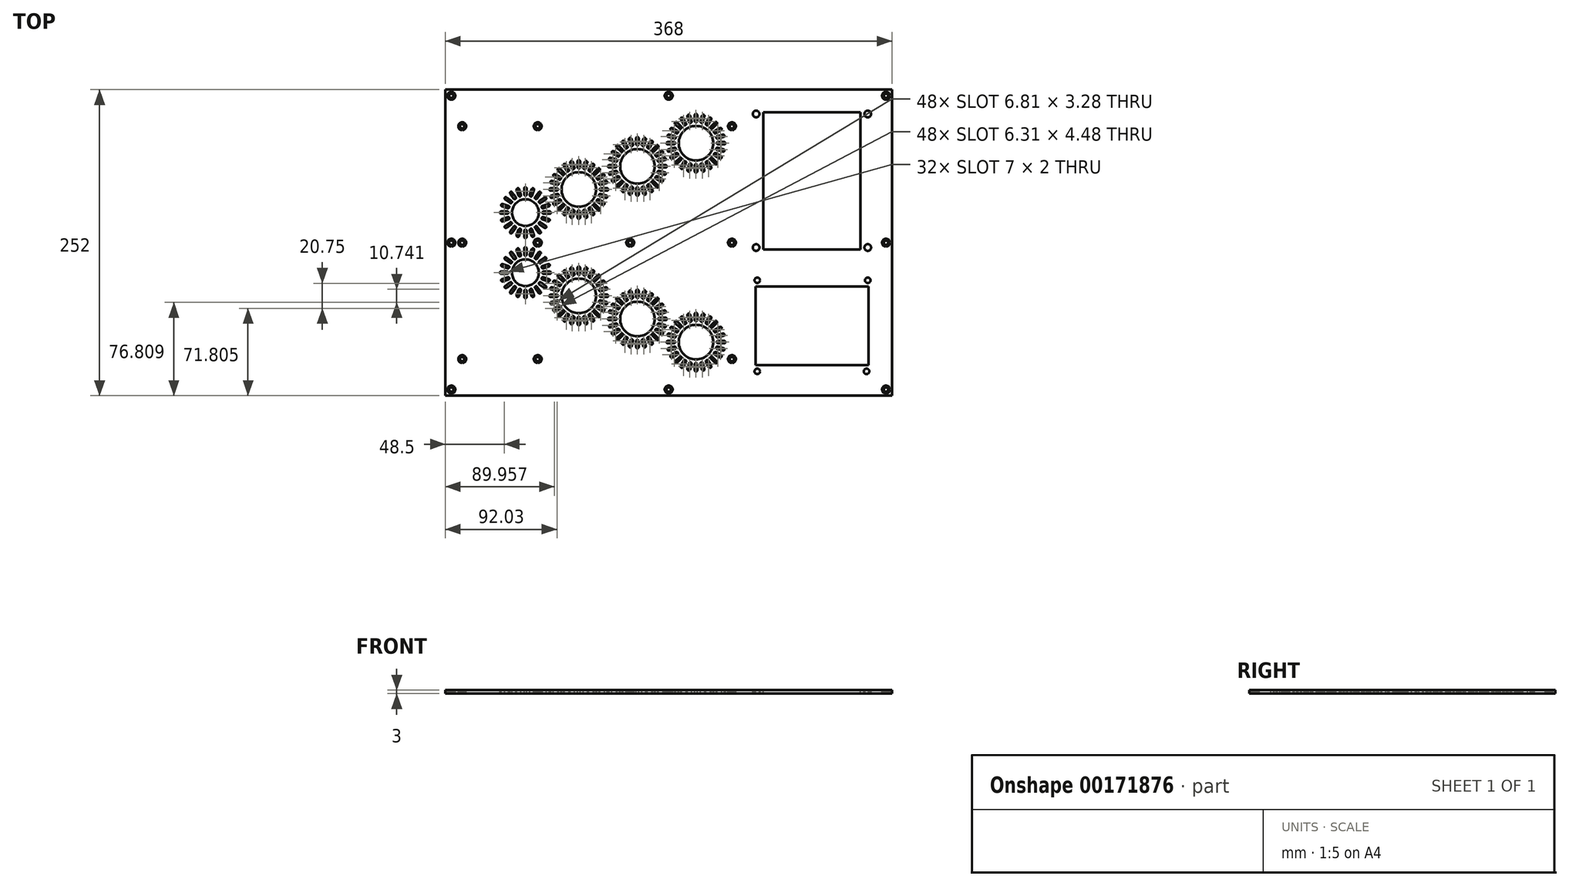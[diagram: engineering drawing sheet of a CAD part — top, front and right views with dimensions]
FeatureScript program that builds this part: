
annotation { "Feature Type Name" : "Feature", "Feature Type Description" : "" }
export const myFeature = defineFeature(function(context is Context, id is Id, definition is map)
    precondition{}
    {
        {
            var Q0;
            Q0=qCreatedBy(makeId("Top.planeOp"),FACE);
            var sketch = newSketch(context, id + "F0", { "sketchPlane" : qUnion([Q0])});
            skLineSegment(sketch, "E0.bottom", {"start": v(184, -126) * mm, "end": v(-184, -126) * mm});
            skLineSegment(sketch, "E0.top", {"start": v(184, 126) * mm, "end": v(-184, 126) * mm});
            skLineSegment(sketch, "E0.left", {"start": v(184, -126) * mm, "end": v(184, 126) * mm});
            skLineSegment(sketch, "E0.right", {"start": v(-184, -126) * mm, "end": v(-184, 126) * mm});
            skPoint(sketch, "E0.middle", {"position": v(0, 0) * mm});
            skLineSegment(sketch, "E1", {"start": v(-118, 153.33) * mm, "end": v(-118, -167.83) * mm, "construction": true});
            skLineSegment(sketch, "E2", {"start": v(-74, 180.26) * mm, "end": v(-74, -51.12) * mm, "construction": true});
            skLineSegment(sketch, "E3", {"start": v(-25.74, 83.61) * mm, "end": v(-25.74, -167.83) * mm, "construction": true});
            skLineSegment(sketch, "E4", {"start": v(-203.28, 62.86) * mm, "end": v(180.7, 62.86) * mm, "construction": true});
            skLineSegment(sketch, "E5", {"start": v(-202.8, 43.82) * mm, "end": v(185.48, 43.82) * mm, "construction": true});
            skLineSegment(sketch, "E6", {"start": v(-209.03, 24.75) * mm, "end": v(184.53, 24.75) * mm, "construction": true});
            skLineSegment(sketch, "E7.MirrorCS", {"start": v(-209.03, -24.75) * mm, "end": v(184.53, -24.75) * mm, "construction": true});
            skLineSegment(sketch, "E8.MirrorCS", {"start": v(-202.8, -43.82) * mm, "end": v(185.48, -43.82) * mm, "construction": true});
            skLineSegment(sketch, "E9.MirrorCS", {"start": v(-203.28, -62.86) * mm, "end": v(180.7, -62.86) * mm, "construction": true});
            skCircle(sketch, "E10", {"center": v(-118, 24.75) * mm, "radius": 11 * mm});
            skCircle(sketch, "E11", {"center": v(-74, 43.82) * mm, "radius": 14.25 * mm});
            skCircle(sketch, "E12", {"center": v(-118, -24.75) * mm, "radius": 11 * mm});
            skCircle(sketch, "E13", {"center": v(-74, -43.82) * mm, "radius": 14.25 * mm});
            skCircle(sketch, "E14", {"center": v(-25.74, -62.86) * mm, "radius": 14.25 * mm});
            skCircle(sketch, "E15", {"center": v(-25.74, 62.86) * mm, "radius": 14.25 * mm});
            skLineSegment(sketch, "E16.bottom", {"start": v(158, -5.5) * mm, "end": v(78, -5.5) * mm});
            skLineSegment(sketch, "E16.top", {"start": v(158, 107.5) * mm, "end": v(78, 107.5) * mm});
            skLineSegment(sketch, "E16.left", {"start": v(158, -5.5) * mm, "end": v(158, 107.5) * mm});
            skLineSegment(sketch, "E16.right", {"start": v(78, -5.5) * mm, "end": v(78, 107.5) * mm});
            skLineSegment(sketch, "E17", {"start": v(72, 135.4) * mm, "end": v(72, -139.42) * mm, "construction": true});
            skLineSegment(sketch, "E18", {"start": v(164, 132.45) * mm, "end": v(164, -295.29) * mm, "construction": true});
            skLineSegment(sketch, "E19", {"start": v(51.45, 106) * mm, "end": v(256.55, 106) * mm, "construction": true});
            skCircle(sketch, "E20", {"center": v(72, 106) * mm, "radius": 2.75 * mm});
            skCircle(sketch, "E21", {"center": v(164, 106) * mm, "radius": 2.75 * mm});
            skCircle(sketch, "E22", {"center": v(72, -4) * mm, "radius": 2.75 * mm});
            skCircle(sketch, "E23", {"center": v(164, -4) * mm, "radius": 2.75 * mm});
            skLineSegment(sketch, "E24", {"start": v(-146.66, 121) * mm, "end": v(202.1, 121) * mm, "construction": true});
            skLineSegment(sketch, "E25", {"start": v(-179, -133.01) * mm, "end": v(-179, 126) * mm, "construction": true});
            skLineSegment(sketch, "E26.MirrorCS", {"start": v(179, -133.01) * mm, "end": v(179, 126) * mm, "construction": true});
            skLineSegment(sketch, "E27.MirrorCS", {"start": v(-146.66, -121) * mm, "end": v(202.1, -121) * mm, "construction": true});
            skLineSegment(sketch, "E28", {"start": v(0, 148.7) * mm, "end": v(0, -121) * mm, "construction": true});
            skPoint(sketch, "E28.startSnap0", {"position": v(0, 126) * mm});
            skPoint(sketch, "E28.endSnap0", {"position": v(27.72, -121) * mm});
            skLineSegment(sketch, "E29", {"start": v(-194.49, 0) * mm, "end": v(194.49, 0) * mm, "construction": true});
            skPoint(sketch, "E29.startSnap0", {"position": v(-184, 0) * mm});
            skPoint(sketch, "E30", {"position": v(-179, 121) * mm});
            skPoint(sketch, "E31", {"position": v(0, 121) * mm});
            skPoint(sketch, "E32", {"position": v(-179, 0) * mm});
            skPoint(sketch, "E33", {"position": v(179, 121) * mm});
            skPoint(sketch, "E34", {"position": v(179, 0) * mm});
            skPoint(sketch, "E35", {"position": v(179, -121) * mm});
            skPoint(sketch, "E36", {"position": v(0, -121) * mm});
            skPoint(sketch, "E37", {"position": v(-179, -121) * mm});
            skLineSegment(sketch, "E38.bottom", {"start": v(169, -9) * mm, "end": v(67, -9) * mm, "construction": true});
            skLineSegment(sketch, "E38.top", {"start": v(169, 111) * mm, "end": v(67, 111) * mm, "construction": true});
            skLineSegment(sketch, "E38.left", {"start": v(169, -9) * mm, "end": v(169, 111) * mm, "construction": true});
            skLineSegment(sketch, "E38.right", {"start": v(67, -9) * mm, "end": v(67, 111) * mm, "construction": true});
            skPoint(sketch, "E38.middle", {"position": v(118, 51) * mm});
            skLineSegment(sketch, "E39", {"start": v(48.88, -4) * mm, "end": v(192, -4) * mm, "construction": true});
            skLineSegment(sketch, "E40.bottom", {"start": v(164.5, -101) * mm, "end": v(71.5, -101) * mm});
            skLineSegment(sketch, "E40.top", {"start": v(164.5, -36) * mm, "end": v(71.5, -36) * mm});
            skLineSegment(sketch, "E40.left", {"start": v(164.5, -101) * mm, "end": v(164.5, -36) * mm});
            skLineSegment(sketch, "E40.right", {"start": v(71.5, -101) * mm, "end": v(71.5, -36) * mm});
            skLineSegment(sketch, "E41", {"start": v(65.3, -31) * mm, "end": v(270.4, -31) * mm, "construction": true});
            skCircle(sketch, "E42", {"center": v(73, -31) * mm, "radius": 2.25 * mm});
            skCircle(sketch, "E43", {"center": v(164, -31) * mm, "radius": 2.25 * mm});
            skCircle(sketch, "E44", {"center": v(73, -106) * mm, "radius": 2.25 * mm});
            skCircle(sketch, "E45", {"center": v(163, -106) * mm, "radius": 2.25 * mm});
            skLineSegment(sketch, "E46.bottom", {"start": v(168, -111) * mm, "end": v(68, -111) * mm, "construction": true});
            skLineSegment(sketch, "E46.top", {"start": v(168, -26) * mm, "end": v(68, -26) * mm, "construction": true});
            skLineSegment(sketch, "E46.left", {"start": v(168, -111) * mm, "end": v(168, -26) * mm, "construction": true});
            skLineSegment(sketch, "E46.right", {"start": v(68, -111) * mm, "end": v(68, -26) * mm, "construction": true});
            skPoint(sketch, "E46.middle", {"position": v(118, -68.5) * mm});
            skLineSegment(sketch, "E47", {"start": v(62.73, -106) * mm, "end": v(205.85, -106) * mm, "construction": true});
            skLineSegment(sketch, "E48", {"start": v(118, 51) * mm, "end": v(118, -168.55) * mm, "construction": true});
            skLineSegment(sketch, "E49", {"start": v(73, -94.18) * mm, "end": v(73, -202) * mm, "construction": true});
            skLineSegment(sketch, "E50", {"start": v(163, -92.42) * mm, "end": v(163, -205.46) * mm, "construction": true});
            skLineSegment(sketch, "E51", {"start": v(22.52, 102.67) * mm, "end": v(22.52, -225.01) * mm, "construction": true});
            skLineSegment(sketch, "E52", {"start": v(-198.69, 81.92) * mm, "end": v(203.66, 81.92) * mm, "construction": true});
            skLineSegment(sketch, "E53.MirrorCS", {"start": v(-198.69, -81.92) * mm, "end": v(203.66, -81.92) * mm, "construction": true});
            skCircle(sketch, "E54", {"center": v(22.52, 81.92) * mm, "radius": 14.25 * mm});
            skCircle(sketch, "E55.MirrorC", {"center": v(22.52, -81.92) * mm, "radius": 14.25 * mm});
            skLineSegment(sketch, "E56.bottom", {"start": v(-118, 38.75) * mm, "end": v(-118, 38.75) * mm});
            skLineSegment(sketch, "E56.top", {"start": v(-118, 45.75) * mm, "end": v(-118, 45.75) * mm});
            skLineSegment(sketch, "E56.left", {"start": v(-117, 39.75) * mm, "end": v(-117, 44.75) * mm});
            skLineSegment(sketch, "E56.right", {"start": v(-119, 39.75) * mm, "end": v(-119, 44.75) * mm});
            skPoint(sketch, "E56.middle", {"position": v(-118, 42.25) * mm});
            skPoint(sketch, "E57.visualSharp", {"position": v(-117, 45.75) * mm});
            skArc(sketch, "E57.filletArc", {"start": v(-117, 44.75) * mm, "mid": v(-117.3, 45.46) * mm, "end": v(-118, 45.75) * mm});
            skPoint(sketch, "E58.visualSharp", {"position": v(-119, 45.75) * mm});
            skArc(sketch, "E58.filletArc", {"start": v(-118, 45.75) * mm, "mid": v(-118.7, 45.46) * mm, "end": v(-119, 44.75) * mm});
            skPoint(sketch, "E59.visualSharp", {"position": v(-119, 38.75) * mm});
            skArc(sketch, "E59.filletArc", {"start": v(-119, 39.75) * mm, "mid": v(-118.7, 39.04) * mm, "end": v(-118, 38.75) * mm});
            skPoint(sketch, "E60.visualSharp", {"position": v(-117, 38.75) * mm});
            skArc(sketch, "E60.filletArc", {"start": v(-118, 38.75) * mm, "mid": v(-117.3, 39.04) * mm, "end": v(-117, 39.75) * mm});
            skPoint(sketch, "E61.1.0", {"position": v(-123.54, 45.03) * mm});
            skPoint(sketch, "E61.1.1", {"position": v(-125.44, 44.41) * mm});
            skPoint(sketch, "E61.1.2", {"position": v(-121.38, 38.37) * mm});
            skLineSegment(sketch, "E61.1.3", {"start": v(-121.68, 39.32) * mm, "end": v(-123.23, 44.08) * mm});
            skPoint(sketch, "E61.1.4", {"position": v(-123.28, 37.76) * mm});
            skLineSegment(sketch, "E61.1.5", {"start": v(-123.59, 38.7) * mm, "end": v(-125.13, 43.46) * mm});
            skPoint(sketch, "E61.1.6", {"position": v(-123.4, 41.4) * mm});
            skArc(sketch, "E61.1.7", {"start": v(-124.49, 44.72) * mm, "mid": v(-125.07, 44.23) * mm, "end": v(-125.13, 43.46) * mm});
            skArc(sketch, "E61.1.8", {"start": v(-122.33, 38.06) * mm, "mid": v(-121.74, 38.56) * mm, "end": v(-121.68, 39.32) * mm});
            skArc(sketch, "E61.1.9", {"start": v(-123.59, 38.7) * mm, "mid": v(-123.09, 38.12) * mm, "end": v(-122.33, 38.06) * mm});
            skArc(sketch, "E61.1.10", {"start": v(-123.23, 44.08) * mm, "mid": v(-123.73, 44.66) * mm, "end": v(-124.49, 44.72) * mm});
            skPoint(sketch, "E61.2.0", {"position": v(-129.53, 42.33) * mm});
            skPoint(sketch, "E61.2.1", {"position": v(-131.15, 41.15) * mm});
            skPoint(sketch, "E61.2.2", {"position": v(-125.42, 36.66) * mm});
            skLineSegment(sketch, "E61.2.3", {"start": v(-126, 37.47) * mm, "end": v(-128.95, 41.52) * mm});
            skPoint(sketch, "E61.2.4", {"position": v(-127.04, 35.49) * mm});
            skLineSegment(sketch, "E61.2.5", {"start": v(-127.63, 36.3) * mm, "end": v(-130.56, 40.34) * mm});
            skPoint(sketch, "E61.2.6", {"position": v(-128.29, 38.9) * mm});
            skArc(sketch, "E61.2.7", {"start": v(-130.34, 41.74) * mm, "mid": v(-130.74, 41.09) * mm, "end": v(-130.56, 40.34) * mm});
            skArc(sketch, "E61.2.8", {"start": v(-126.23, 36.08) * mm, "mid": v(-125.83, 36.73) * mm, "end": v(-126, 37.47) * mm});
            skArc(sketch, "E61.2.9", {"start": v(-127.63, 36.3) * mm, "mid": v(-126.97, 35.9) * mm, "end": v(-126.23, 36.08) * mm});
            skArc(sketch, "E61.2.10", {"start": v(-128.95, 41.52) * mm, "mid": v(-129.6, 41.92) * mm, "end": v(-130.34, 41.74) * mm});
            skPoint(sketch, "E61.3.0", {"position": v(-134.4, 37.9) * mm});
            skPoint(sketch, "E61.3.1", {"position": v(-135.58, 36.28) * mm});
            skPoint(sketch, "E61.3.2", {"position": v(-128.74, 33.79) * mm});
            skLineSegment(sketch, "E61.3.3", {"start": v(-129.55, 34.38) * mm, "end": v(-133.6, 37.31) * mm});
            skPoint(sketch, "E61.3.4", {"position": v(-129.91, 32.17) * mm});
            skLineSegment(sketch, "E61.3.5", {"start": v(-130.72, 32.76) * mm, "end": v(-134.77, 35.7) * mm});
            skPoint(sketch, "E61.3.6", {"position": v(-132.16, 35.04) * mm});
            skArc(sketch, "E61.3.7", {"start": v(-134.99, 37.1) * mm, "mid": v(-135.17, 36.35) * mm, "end": v(-134.77, 35.7) * mm});
            skArc(sketch, "E61.3.8", {"start": v(-129.33, 32.98) * mm, "mid": v(-129.15, 33.72) * mm, "end": v(-129.55, 34.38) * mm});
            skArc(sketch, "E61.3.9", {"start": v(-130.72, 32.76) * mm, "mid": v(-129.98, 32.58) * mm, "end": v(-129.33, 32.98) * mm});
            skArc(sketch, "E61.3.10", {"start": v(-133.6, 37.31) * mm, "mid": v(-134.34, 37.5) * mm, "end": v(-134.99, 37.1) * mm});
            skPoint(sketch, "E61.4.0", {"position": v(-137.66, 32.2) * mm});
            skPoint(sketch, "E61.4.1", {"position": v(-138.28, 30.29) * mm});
            skPoint(sketch, "E61.4.2", {"position": v(-131, 30.03) * mm});
            skLineSegment(sketch, "E61.4.3", {"start": v(-131.96, 30.34) * mm, "end": v(-136.71, 31.88) * mm});
            skPoint(sketch, "E61.4.4", {"position": v(-131.62, 28.13) * mm});
            skLineSegment(sketch, "E61.4.5", {"start": v(-132.57, 28.43) * mm, "end": v(-137.33, 29.98) * mm});
            skPoint(sketch, "E61.4.6", {"position": v(-134.64, 30.16) * mm});
            skArc(sketch, "E61.4.7", {"start": v(-137.97, 31.24) * mm, "mid": v(-137.91, 30.48) * mm, "end": v(-137.33, 29.98) * mm});
            skArc(sketch, "E61.4.8", {"start": v(-131.31, 29.08) * mm, "mid": v(-131.37, 29.84) * mm, "end": v(-131.96, 30.34) * mm});
            skArc(sketch, "E61.4.9", {"start": v(-132.57, 28.43) * mm, "mid": v(-131.81, 28.5) * mm, "end": v(-131.31, 29.08) * mm});
            skArc(sketch, "E61.4.10", {"start": v(-136.71, 31.88) * mm, "mid": v(-137.48, 31.82) * mm, "end": v(-137.97, 31.24) * mm});
            skPoint(sketch, "E61.5.0", {"position": v(-139, 25.75) * mm});
            skPoint(sketch, "E61.5.1", {"position": v(-139, 23.75) * mm});
            skPoint(sketch, "E61.5.2", {"position": v(-132, 25.75) * mm});
            skLineSegment(sketch, "E61.5.3", {"start": v(-133, 25.75) * mm, "end": v(-138, 25.75) * mm});
            skPoint(sketch, "E61.5.4", {"position": v(-132, 23.75) * mm});
            skLineSegment(sketch, "E61.5.5", {"start": v(-133, 23.75) * mm, "end": v(-138, 23.75) * mm});
            skPoint(sketch, "E61.5.6", {"position": v(-135.5, 24.75) * mm});
            skArc(sketch, "E61.5.7", {"start": v(-139, 24.75) * mm, "mid": v(-138.7, 24.04) * mm, "end": v(-138, 23.75) * mm});
            skArc(sketch, "E61.5.8", {"start": v(-132, 24.75) * mm, "mid": v(-132.3, 25.46) * mm, "end": v(-133, 25.75) * mm});
            skArc(sketch, "E61.5.9", {"start": v(-133, 23.75) * mm, "mid": v(-132.3, 24.04) * mm, "end": v(-132, 24.75) * mm});
            skArc(sketch, "E61.5.10", {"start": v(-138, 25.75) * mm, "mid": v(-138.7, 25.46) * mm, "end": v(-139, 24.75) * mm});
            skPoint(sketch, "E61.6.0", {"position": v(-138.28, 19.21) * mm});
            skPoint(sketch, "E61.6.1", {"position": v(-137.66, 17.3) * mm});
            skPoint(sketch, "E61.6.2", {"position": v(-131.62, 21.37) * mm});
            skLineSegment(sketch, "E61.6.3", {"start": v(-132.57, 21.07) * mm, "end": v(-137.33, 19.52) * mm});
            skPoint(sketch, "E61.6.4", {"position": v(-131, 19.47) * mm});
            skLineSegment(sketch, "E61.6.5", {"start": v(-131.96, 19.16) * mm, "end": v(-136.71, 17.62) * mm});
            skPoint(sketch, "E61.6.6", {"position": v(-134.64, 19.34) * mm});
            skArc(sketch, "E61.6.7", {"start": v(-137.97, 18.26) * mm, "mid": v(-137.48, 17.68) * mm, "end": v(-136.71, 17.62) * mm});
            skArc(sketch, "E61.6.8", {"start": v(-131.31, 20.42) * mm, "mid": v(-131.81, 21) * mm, "end": v(-132.57, 21.07) * mm});
            skArc(sketch, "E61.6.9", {"start": v(-131.96, 19.16) * mm, "mid": v(-131.37, 19.66) * mm, "end": v(-131.31, 20.42) * mm});
            skArc(sketch, "E61.6.10", {"start": v(-137.33, 19.52) * mm, "mid": v(-137.91, 19.02) * mm, "end": v(-137.97, 18.26) * mm});
            skPoint(sketch, "E61.7.0", {"position": v(-135.58, 13.22) * mm});
            skPoint(sketch, "E61.7.1", {"position": v(-134.4, 11.6) * mm});
            skPoint(sketch, "E61.7.2", {"position": v(-129.91, 17.33) * mm});
            skLineSegment(sketch, "E61.7.3", {"start": v(-130.72, 16.74) * mm, "end": v(-134.77, 13.8) * mm});
            skPoint(sketch, "E61.7.4", {"position": v(-128.74, 15.71) * mm});
            skLineSegment(sketch, "E61.7.5", {"start": v(-129.55, 15.12) * mm, "end": v(-133.6, 12.19) * mm});
            skPoint(sketch, "E61.7.6", {"position": v(-132.16, 14.46) * mm});
            skArc(sketch, "E61.7.7", {"start": v(-134.99, 12.4) * mm, "mid": v(-134.34, 12) * mm, "end": v(-133.6, 12.19) * mm});
            skArc(sketch, "E61.7.8", {"start": v(-129.33, 16.52) * mm, "mid": v(-129.98, 16.92) * mm, "end": v(-130.72, 16.74) * mm});
            skArc(sketch, "E61.7.9", {"start": v(-129.55, 15.12) * mm, "mid": v(-129.15, 15.78) * mm, "end": v(-129.33, 16.52) * mm});
            skArc(sketch, "E61.7.10", {"start": v(-134.77, 13.8) * mm, "mid": v(-135.17, 13.15) * mm, "end": v(-134.99, 12.4) * mm});
            skPoint(sketch, "E61.8.0", {"position": v(-131.15, 8.35) * mm});
            skPoint(sketch, "E61.8.1", {"position": v(-129.53, 7.17) * mm});
            skPoint(sketch, "E61.8.2", {"position": v(-127.04, 14.01) * mm});
            skLineSegment(sketch, "E61.8.3", {"start": v(-127.63, 13.2) * mm, "end": v(-130.56, 9.16) * mm});
            skPoint(sketch, "E61.8.4", {"position": v(-125.42, 12.84) * mm});
            skLineSegment(sketch, "E61.8.5", {"start": v(-126, 12.03) * mm, "end": v(-128.95, 7.98) * mm});
            skPoint(sketch, "E61.8.6", {"position": v(-128.29, 10.6) * mm});
            skArc(sketch, "E61.8.7", {"start": v(-130.34, 7.76) * mm, "mid": v(-129.6, 7.58) * mm, "end": v(-128.95, 7.98) * mm});
            skArc(sketch, "E61.8.8", {"start": v(-126.23, 13.42) * mm, "mid": v(-126.97, 13.6) * mm, "end": v(-127.63, 13.2) * mm});
            skArc(sketch, "E61.8.9", {"start": v(-126, 12.03) * mm, "mid": v(-125.83, 12.77) * mm, "end": v(-126.23, 13.42) * mm});
            skArc(sketch, "E61.8.10", {"start": v(-130.56, 9.16) * mm, "mid": v(-130.74, 8.41) * mm, "end": v(-130.34, 7.76) * mm});
            skPoint(sketch, "E61.9.0", {"position": v(-125.44, 5.09) * mm});
            skPoint(sketch, "E61.9.1", {"position": v(-123.54, 4.47) * mm});
            skPoint(sketch, "E61.9.2", {"position": v(-123.28, 11.74) * mm});
            skLineSegment(sketch, "E61.9.3", {"start": v(-123.59, 10.8) * mm, "end": v(-125.13, 6.04) * mm});
            skPoint(sketch, "E61.9.4", {"position": v(-121.38, 11.13) * mm});
            skLineSegment(sketch, "E61.9.5", {"start": v(-121.68, 10.18) * mm, "end": v(-123.23, 5.42) * mm});
            skPoint(sketch, "E61.9.6", {"position": v(-123.4, 8.1) * mm});
            skArc(sketch, "E61.9.7", {"start": v(-124.49, 4.78) * mm, "mid": v(-123.73, 4.84) * mm, "end": v(-123.23, 5.42) * mm});
            skArc(sketch, "E61.9.8", {"start": v(-122.33, 11.44) * mm, "mid": v(-123.09, 11.38) * mm, "end": v(-123.59, 10.8) * mm});
            skArc(sketch, "E61.9.9", {"start": v(-121.68, 10.18) * mm, "mid": v(-121.74, 10.94) * mm, "end": v(-122.33, 11.44) * mm});
            skArc(sketch, "E61.9.10", {"start": v(-125.13, 6.04) * mm, "mid": v(-125.07, 5.27) * mm, "end": v(-124.49, 4.78) * mm});
            skPoint(sketch, "E61.10.0", {"position": v(-119, 3.75) * mm});
            skPoint(sketch, "E61.10.1", {"position": v(-117, 3.75) * mm});
            skPoint(sketch, "E61.10.2", {"position": v(-119, 10.75) * mm});
            skLineSegment(sketch, "E61.10.3", {"start": v(-119, 9.75) * mm, "end": v(-119, 4.75) * mm});
            skPoint(sketch, "E61.10.4", {"position": v(-117, 10.75) * mm});
            skLineSegment(sketch, "E61.10.5", {"start": v(-117, 9.75) * mm, "end": v(-117, 4.75) * mm});
            skPoint(sketch, "E61.10.6", {"position": v(-118, 7.25) * mm});
            skArc(sketch, "E61.10.7", {"start": v(-118, 3.75) * mm, "mid": v(-117.3, 4.04) * mm, "end": v(-117, 4.75) * mm});
            skArc(sketch, "E61.10.8", {"start": v(-118, 10.75) * mm, "mid": v(-118.7, 10.46) * mm, "end": v(-119, 9.75) * mm});
            skArc(sketch, "E61.10.9", {"start": v(-117, 9.75) * mm, "mid": v(-117.3, 10.46) * mm, "end": v(-118, 10.75) * mm});
            skArc(sketch, "E61.10.10", {"start": v(-119, 4.75) * mm, "mid": v(-118.7, 4.04) * mm, "end": v(-118, 3.75) * mm});
            skPoint(sketch, "E61.11.0", {"position": v(-112.46, 4.47) * mm});
            skPoint(sketch, "E61.11.1", {"position": v(-110.56, 5.09) * mm});
            skPoint(sketch, "E61.11.2", {"position": v(-114.62, 11.13) * mm});
            skLineSegment(sketch, "E61.11.3", {"start": v(-114.32, 10.18) * mm, "end": v(-112.77, 5.42) * mm});
            skPoint(sketch, "E61.11.4", {"position": v(-112.72, 11.74) * mm});
            skLineSegment(sketch, "E61.11.5", {"start": v(-112.41, 10.8) * mm, "end": v(-110.87, 6.04) * mm});
            skPoint(sketch, "E61.11.6", {"position": v(-112.6, 8.1) * mm});
            skArc(sketch, "E61.11.7", {"start": v(-111.51, 4.78) * mm, "mid": v(-110.93, 5.27) * mm, "end": v(-110.87, 6.04) * mm});
            skArc(sketch, "E61.11.8", {"start": v(-113.67, 11.44) * mm, "mid": v(-114.26, 10.94) * mm, "end": v(-114.32, 10.18) * mm});
            skArc(sketch, "E61.11.9", {"start": v(-112.41, 10.8) * mm, "mid": v(-112.91, 11.38) * mm, "end": v(-113.67, 11.44) * mm});
            skArc(sketch, "E61.11.10", {"start": v(-112.77, 5.42) * mm, "mid": v(-112.27, 4.84) * mm, "end": v(-111.51, 4.78) * mm});
            skPoint(sketch, "E61.12.0", {"position": v(-106.47, 7.17) * mm});
            skPoint(sketch, "E61.12.1", {"position": v(-104.85, 8.35) * mm});
            skPoint(sketch, "E61.12.2", {"position": v(-110.58, 12.84) * mm});
            skLineSegment(sketch, "E61.12.3", {"start": v(-110, 12.03) * mm, "end": v(-107.05, 7.98) * mm});
            skPoint(sketch, "E61.12.4", {"position": v(-108.96, 14.01) * mm});
            skLineSegment(sketch, "E61.12.5", {"start": v(-108.37, 13.2) * mm, "end": v(-105.44, 9.16) * mm});
            skPoint(sketch, "E61.12.6", {"position": v(-107.71, 10.6) * mm});
            skArc(sketch, "E61.12.7", {"start": v(-105.66, 7.76) * mm, "mid": v(-105.26, 8.41) * mm, "end": v(-105.44, 9.16) * mm});
            skArc(sketch, "E61.12.8", {"start": v(-109.77, 13.42) * mm, "mid": v(-110.17, 12.77) * mm, "end": v(-110, 12.03) * mm});
            skArc(sketch, "E61.12.9", {"start": v(-108.37, 13.2) * mm, "mid": v(-109.03, 13.6) * mm, "end": v(-109.77, 13.42) * mm});
            skArc(sketch, "E61.12.10", {"start": v(-107.05, 7.98) * mm, "mid": v(-106.4, 7.58) * mm, "end": v(-105.66, 7.76) * mm});
            skPoint(sketch, "E61.13.0", {"position": v(-101.6, 11.6) * mm});
            skPoint(sketch, "E61.13.1", {"position": v(-100.42, 13.22) * mm});
            skPoint(sketch, "E61.13.2", {"position": v(-107.26, 15.71) * mm});
            skLineSegment(sketch, "E61.13.3", {"start": v(-106.45, 15.12) * mm, "end": v(-102.4, 12.19) * mm});
            skPoint(sketch, "E61.13.4", {"position": v(-106.09, 17.33) * mm});
            skLineSegment(sketch, "E61.13.5", {"start": v(-105.28, 16.74) * mm, "end": v(-101.23, 13.8) * mm});
            skPoint(sketch, "E61.13.6", {"position": v(-103.84, 14.46) * mm});
            skArc(sketch, "E61.13.7", {"start": v(-101.01, 12.4) * mm, "mid": v(-100.83, 13.15) * mm, "end": v(-101.23, 13.8) * mm});
            skArc(sketch, "E61.13.8", {"start": v(-106.67, 16.52) * mm, "mid": v(-106.85, 15.78) * mm, "end": v(-106.45, 15.12) * mm});
            skArc(sketch, "E61.13.9", {"start": v(-105.28, 16.74) * mm, "mid": v(-106.02, 16.92) * mm, "end": v(-106.67, 16.52) * mm});
            skArc(sketch, "E61.13.10", {"start": v(-102.4, 12.19) * mm, "mid": v(-101.66, 12) * mm, "end": v(-101.01, 12.4) * mm});
            skPoint(sketch, "E61.14.0", {"position": v(-98.34, 17.3) * mm});
            skPoint(sketch, "E61.14.1", {"position": v(-97.72, 19.21) * mm});
            skPoint(sketch, "E61.14.2", {"position": v(-105, 19.47) * mm});
            skLineSegment(sketch, "E61.14.3", {"start": v(-104.04, 19.16) * mm, "end": v(-99.29, 17.62) * mm});
            skPoint(sketch, "E61.14.4", {"position": v(-104.38, 21.37) * mm});
            skLineSegment(sketch, "E61.14.5", {"start": v(-103.43, 21.07) * mm, "end": v(-98.67, 19.52) * mm});
            skPoint(sketch, "E61.14.6", {"position": v(-101.36, 19.34) * mm});
            skArc(sketch, "E61.14.7", {"start": v(-98.03, 18.26) * mm, "mid": v(-98.09, 19.02) * mm, "end": v(-98.67, 19.52) * mm});
            skArc(sketch, "E61.14.8", {"start": v(-104.69, 20.42) * mm, "mid": v(-104.63, 19.66) * mm, "end": v(-104.04, 19.16) * mm});
            skArc(sketch, "E61.14.9", {"start": v(-103.43, 21.07) * mm, "mid": v(-104.19, 21) * mm, "end": v(-104.69, 20.42) * mm});
            skArc(sketch, "E61.14.10", {"start": v(-99.29, 17.62) * mm, "mid": v(-98.52, 17.68) * mm, "end": v(-98.03, 18.26) * mm});
            skPoint(sketch, "E61.15.0", {"position": v(-97, 23.75) * mm});
            skPoint(sketch, "E61.15.1", {"position": v(-97, 25.75) * mm});
            skPoint(sketch, "E61.15.2", {"position": v(-104, 23.75) * mm});
            skLineSegment(sketch, "E61.15.3", {"start": v(-103, 23.75) * mm, "end": v(-98, 23.75) * mm});
            skPoint(sketch, "E61.15.4", {"position": v(-104, 25.75) * mm});
            skLineSegment(sketch, "E61.15.5", {"start": v(-103, 25.75) * mm, "end": v(-98, 25.75) * mm});
            skPoint(sketch, "E61.15.6", {"position": v(-100.5, 24.75) * mm});
            skArc(sketch, "E61.15.7", {"start": v(-97, 24.75) * mm, "mid": v(-97.3, 25.46) * mm, "end": v(-98, 25.75) * mm});
            skArc(sketch, "E61.15.8", {"start": v(-104, 24.75) * mm, "mid": v(-103.7, 24.04) * mm, "end": v(-103, 23.75) * mm});
            skArc(sketch, "E61.15.9", {"start": v(-103, 25.75) * mm, "mid": v(-103.7, 25.46) * mm, "end": v(-104, 24.75) * mm});
            skArc(sketch, "E61.15.10", {"start": v(-98, 23.75) * mm, "mid": v(-97.3, 24.04) * mm, "end": v(-97, 24.75) * mm});
            skPoint(sketch, "E61.16.0", {"position": v(-97.72, 30.29) * mm});
            skPoint(sketch, "E61.16.1", {"position": v(-98.34, 32.2) * mm});
            skPoint(sketch, "E61.16.2", {"position": v(-104.38, 28.13) * mm});
            skLineSegment(sketch, "E61.16.3", {"start": v(-103.43, 28.43) * mm, "end": v(-98.67, 29.98) * mm});
            skPoint(sketch, "E61.16.4", {"position": v(-105, 30.03) * mm});
            skLineSegment(sketch, "E61.16.5", {"start": v(-104.04, 30.34) * mm, "end": v(-99.29, 31.88) * mm});
            skPoint(sketch, "E61.16.6", {"position": v(-101.36, 30.16) * mm});
            skArc(sketch, "E61.16.7", {"start": v(-98.03, 31.24) * mm, "mid": v(-98.52, 31.82) * mm, "end": v(-99.29, 31.88) * mm});
            skArc(sketch, "E61.16.8", {"start": v(-104.69, 29.08) * mm, "mid": v(-104.19, 28.5) * mm, "end": v(-103.43, 28.43) * mm});
            skArc(sketch, "E61.16.9", {"start": v(-104.04, 30.34) * mm, "mid": v(-104.63, 29.84) * mm, "end": v(-104.69, 29.08) * mm});
            skArc(sketch, "E61.16.10", {"start": v(-98.67, 29.98) * mm, "mid": v(-98.09, 30.48) * mm, "end": v(-98.03, 31.24) * mm});
            skPoint(sketch, "E61.17.0", {"position": v(-100.42, 36.28) * mm});
            skPoint(sketch, "E61.17.1", {"position": v(-101.6, 37.9) * mm});
            skPoint(sketch, "E61.17.2", {"position": v(-106.09, 32.17) * mm});
            skLineSegment(sketch, "E61.17.3", {"start": v(-105.28, 32.76) * mm, "end": v(-101.23, 35.7) * mm});
            skPoint(sketch, "E61.17.4", {"position": v(-107.26, 33.79) * mm});
            skLineSegment(sketch, "E61.17.5", {"start": v(-106.45, 34.38) * mm, "end": v(-102.4, 37.31) * mm});
            skPoint(sketch, "E61.17.6", {"position": v(-103.84, 35.04) * mm});
            skArc(sketch, "E61.17.7", {"start": v(-101.01, 37.1) * mm, "mid": v(-101.66, 37.5) * mm, "end": v(-102.4, 37.31) * mm});
            skArc(sketch, "E61.17.8", {"start": v(-106.67, 32.98) * mm, "mid": v(-106.02, 32.58) * mm, "end": v(-105.28, 32.76) * mm});
            skArc(sketch, "E61.17.9", {"start": v(-106.45, 34.38) * mm, "mid": v(-106.85, 33.72) * mm, "end": v(-106.67, 32.98) * mm});
            skArc(sketch, "E61.17.10", {"start": v(-101.23, 35.7) * mm, "mid": v(-100.83, 36.35) * mm, "end": v(-101.01, 37.1) * mm});
            skPoint(sketch, "E61.18.0", {"position": v(-104.85, 41.15) * mm});
            skPoint(sketch, "E61.18.1", {"position": v(-106.47, 42.33) * mm});
            skPoint(sketch, "E61.18.2", {"position": v(-108.96, 35.49) * mm});
            skLineSegment(sketch, "E61.18.3", {"start": v(-108.37, 36.3) * mm, "end": v(-105.44, 40.34) * mm});
            skPoint(sketch, "E61.18.4", {"position": v(-110.58, 36.66) * mm});
            skLineSegment(sketch, "E61.18.5", {"start": v(-110, 37.47) * mm, "end": v(-107.05, 41.52) * mm});
            skPoint(sketch, "E61.18.6", {"position": v(-107.71, 38.9) * mm});
            skArc(sketch, "E61.18.7", {"start": v(-105.66, 41.74) * mm, "mid": v(-106.4, 41.92) * mm, "end": v(-107.05, 41.52) * mm});
            skArc(sketch, "E61.18.8", {"start": v(-109.77, 36.08) * mm, "mid": v(-109.03, 35.9) * mm, "end": v(-108.37, 36.3) * mm});
            skArc(sketch, "E61.18.9", {"start": v(-110, 37.47) * mm, "mid": v(-110.17, 36.73) * mm, "end": v(-109.77, 36.08) * mm});
            skArc(sketch, "E61.18.10", {"start": v(-105.44, 40.34) * mm, "mid": v(-105.26, 41.09) * mm, "end": v(-105.66, 41.74) * mm});
            skPoint(sketch, "E61.19.0", {"position": v(-110.56, 44.41) * mm});
            skPoint(sketch, "E61.19.1", {"position": v(-112.46, 45.03) * mm});
            skPoint(sketch, "E61.19.2", {"position": v(-112.72, 37.76) * mm});
            skLineSegment(sketch, "E61.19.3", {"start": v(-112.41, 38.7) * mm, "end": v(-110.87, 43.46) * mm});
            skPoint(sketch, "E61.19.4", {"position": v(-114.62, 38.37) * mm});
            skLineSegment(sketch, "E61.19.5", {"start": v(-114.32, 39.32) * mm, "end": v(-112.77, 44.08) * mm});
            skPoint(sketch, "E61.19.6", {"position": v(-112.6, 41.4) * mm});
            skArc(sketch, "E61.19.7", {"start": v(-111.51, 44.72) * mm, "mid": v(-112.27, 44.66) * mm, "end": v(-112.77, 44.08) * mm});
            skArc(sketch, "E61.19.8", {"start": v(-113.67, 38.06) * mm, "mid": v(-112.91, 38.12) * mm, "end": v(-112.41, 38.7) * mm});
            skArc(sketch, "E61.19.9", {"start": v(-114.32, 39.32) * mm, "mid": v(-114.26, 38.56) * mm, "end": v(-113.67, 38.06) * mm});
            skArc(sketch, "E61.19.10", {"start": v(-110.87, 43.46) * mm, "mid": v(-110.93, 44.23) * mm, "end": v(-111.51, 44.72) * mm});
            skLineSegment(sketch, "E62.bottom", {"start": v(-74, 61.07) * mm, "end": v(-74, 61.07) * mm});
            skLineSegment(sketch, "E62.top", {"start": v(-74, 68.07) * mm, "end": v(-74, 68.07) * mm});
            skLineSegment(sketch, "E62.left", {"start": v(-73, 62.07) * mm, "end": v(-73, 67.07) * mm});
            skLineSegment(sketch, "E62.right", {"start": v(-75, 62.07) * mm, "end": v(-75, 67.07) * mm});
            skPoint(sketch, "E62.middle", {"position": v(-74, 64.57) * mm});
            skPoint(sketch, "E63.visualSharp", {"position": v(-73, 68.07) * mm});
            skArc(sketch, "E63.filletArc", {"start": v(-73, 67.07) * mm, "mid": v(-73.3, 67.78) * mm, "end": v(-74, 68.07) * mm});
            skPoint(sketch, "E64.visualSharp", {"position": v(-75, 68.07) * mm});
            skArc(sketch, "E64.filletArc", {"start": v(-74, 68.07) * mm, "mid": v(-74.7, 67.78) * mm, "end": v(-75, 67.07) * mm});
            skPoint(sketch, "E65.visualSharp", {"position": v(-75, 61.07) * mm});
            skArc(sketch, "E65.filletArc", {"start": v(-75, 62.07) * mm, "mid": v(-74.7, 61.36) * mm, "end": v(-74, 61.07) * mm});
            skPoint(sketch, "E66.visualSharp", {"position": v(-73, 61.07) * mm});
            skArc(sketch, "E66.filletArc", {"start": v(-74, 61.07) * mm, "mid": v(-73.3, 61.36) * mm, "end": v(-73, 62.07) * mm});
            skPoint(sketch, "E67.1.0", {"position": v(-79.37, 63.86) * mm});
            skPoint(sketch, "E67.1.1", {"position": v(-77.5, 60.74) * mm});
            skLineSegment(sketch, "E67.1.2", {"start": v(-77.76, 61.7) * mm, "end": v(-79.05, 66.54) * mm});
            skLineSegment(sketch, "E67.1.3", {"start": v(-79.69, 61.19) * mm, "end": v(-80.98, 66.02) * mm});
            skPoint(sketch, "E67.1.4", {"position": v(-79.31, 67.5) * mm});
            skArc(sketch, "E67.1.5", {"start": v(-79.69, 61.19) * mm, "mid": v(-79.22, 60.58) * mm, "end": v(-78.46, 60.48) * mm});
            skPoint(sketch, "E67.1.6", {"position": v(-81.24, 66.98) * mm});
            skArc(sketch, "E67.1.7", {"start": v(-79.05, 66.54) * mm, "mid": v(-79.52, 67.14) * mm, "end": v(-80.28, 67.24) * mm});
            skPoint(sketch, "E67.1.8", {"position": v(-79.43, 60.22) * mm});
            skArc(sketch, "E67.1.9", {"start": v(-80.28, 67.24) * mm, "mid": v(-80.88, 66.78) * mm, "end": v(-80.98, 66.02) * mm});
            skArc(sketch, "E67.1.10", {"start": v(-78.46, 60.48) * mm, "mid": v(-77.86, 60.95) * mm, "end": v(-77.76, 61.7) * mm});
            skPoint(sketch, "E67.2.0", {"position": v(-84.37, 61.8) * mm});
            skPoint(sketch, "E67.2.1", {"position": v(-81.76, 59.26) * mm});
            skLineSegment(sketch, "E67.2.2", {"start": v(-82.26, 60.12) * mm, "end": v(-84.76, 64.46) * mm});
            skLineSegment(sketch, "E67.2.3", {"start": v(-84, 59.12) * mm, "end": v(-86.5, 63.46) * mm});
            skPoint(sketch, "E67.2.4", {"position": v(-85.26, 65.32) * mm});
            skArc(sketch, "E67.2.5", {"start": v(-84, 59.12) * mm, "mid": v(-83.38, 58.66) * mm, "end": v(-82.62, 58.76) * mm});
            skPoint(sketch, "E67.2.6", {"position": v(-87, 64.32) * mm});
            skArc(sketch, "E67.2.7", {"start": v(-84.76, 64.46) * mm, "mid": v(-85.37, 64.92) * mm, "end": v(-86.12, 64.82) * mm});
            skPoint(sketch, "E67.2.8", {"position": v(-83.5, 58.26) * mm});
            skArc(sketch, "E67.2.9", {"start": v(-86.12, 64.82) * mm, "mid": v(-86.6, 64.21) * mm, "end": v(-86.5, 63.46) * mm});
            skArc(sketch, "E67.2.10", {"start": v(-82.62, 58.76) * mm, "mid": v(-82.16, 59.37) * mm, "end": v(-82.26, 60.12) * mm});
            skPoint(sketch, "E67.3.0", {"position": v(-88.67, 58.5) * mm});
            skPoint(sketch, "E67.3.1", {"position": v(-85.5, 56.72) * mm});
            skLineSegment(sketch, "E67.3.2", {"start": v(-86.2, 57.43) * mm, "end": v(-89.73, 60.97) * mm});
            skLineSegment(sketch, "E67.3.3", {"start": v(-87.61, 56.02) * mm, "end": v(-91.15, 59.55) * mm});
            skPoint(sketch, "E67.3.4", {"position": v(-90.44, 61.67) * mm});
            skArc(sketch, "E67.3.5", {"start": v(-87.61, 56.02) * mm, "mid": v(-86.9, 55.72) * mm, "end": v(-86.2, 56.02) * mm});
            skPoint(sketch, "E67.3.6", {"position": v(-91.85, 60.26) * mm});
            skArc(sketch, "E67.3.7", {"start": v(-89.73, 60.97) * mm, "mid": v(-90.44, 61.26) * mm, "end": v(-91.15, 60.97) * mm});
            skPoint(sketch, "E67.3.8", {"position": v(-86.9, 55.31) * mm});
            skArc(sketch, "E67.3.9", {"start": v(-91.15, 60.97) * mm, "mid": v(-91.44, 60.26) * mm, "end": v(-91.15, 59.55) * mm});
            skArc(sketch, "E67.3.10", {"start": v(-86.2, 56.02) * mm, "mid": v(-85.9, 56.72) * mm, "end": v(-86.2, 57.43) * mm});
            skPoint(sketch, "E67.4.0", {"position": v(-91.97, 54.2) * mm});
            skPoint(sketch, "E67.4.1", {"position": v(-88.44, 53.31) * mm});
            skLineSegment(sketch, "E67.4.2", {"start": v(-89.3, 53.81) * mm, "end": v(-93.64, 56.31) * mm});
            skLineSegment(sketch, "E67.4.3", {"start": v(-90.3, 52.08) * mm, "end": v(-94.64, 54.58) * mm});
            skPoint(sketch, "E67.4.4", {"position": v(-94.5, 56.81) * mm});
            skArc(sketch, "E67.4.5", {"start": v(-90.3, 52.08) * mm, "mid": v(-89.55, 51.98) * mm, "end": v(-88.94, 52.44) * mm});
            skPoint(sketch, "E67.4.6", {"position": v(-95.5, 55.08) * mm});
            skArc(sketch, "E67.4.7", {"start": v(-93.64, 56.31) * mm, "mid": v(-94.4, 56.41) * mm, "end": v(-95, 55.94) * mm});
            skPoint(sketch, "E67.4.8", {"position": v(-89.44, 51.58) * mm});
            skArc(sketch, "E67.4.9", {"start": v(-95, 55.94) * mm, "mid": v(-95.1, 55.19) * mm, "end": v(-94.64, 54.58) * mm});
            skArc(sketch, "E67.4.10", {"start": v(-88.94, 52.44) * mm, "mid": v(-88.84, 53.2) * mm, "end": v(-89.3, 53.81) * mm});
            skPoint(sketch, "E67.5.0", {"position": v(-94.04, 49.2) * mm});
            skPoint(sketch, "E67.5.1", {"position": v(-90.4, 49.25) * mm});
            skLineSegment(sketch, "E67.5.2", {"start": v(-91.37, 49.5) * mm, "end": v(-96.2, 50.8) * mm});
            skLineSegment(sketch, "E67.5.3", {"start": v(-91.89, 47.58) * mm, "end": v(-96.72, 48.87) * mm});
            skPoint(sketch, "E67.5.4", {"position": v(-97.16, 51.06) * mm});
            skArc(sketch, "E67.5.5", {"start": v(-91.89, 47.58) * mm, "mid": v(-91.13, 47.68) * mm, "end": v(-90.66, 48.28) * mm});
            skPoint(sketch, "E67.5.6", {"position": v(-97.68, 49.13) * mm});
            skArc(sketch, "E67.5.7", {"start": v(-96.2, 50.8) * mm, "mid": v(-96.96, 50.7) * mm, "end": v(-97.42, 50.1) * mm});
            skPoint(sketch, "E67.5.8", {"position": v(-90.92, 47.32) * mm});
            skArc(sketch, "E67.5.9", {"start": v(-97.42, 50.1) * mm, "mid": v(-97.32, 49.34) * mm, "end": v(-96.72, 48.87) * mm});
            skArc(sketch, "E67.5.10", {"start": v(-90.66, 48.28) * mm, "mid": v(-90.76, 49.04) * mm, "end": v(-91.37, 49.5) * mm});
            skPoint(sketch, "E67.6.0", {"position": v(-94.75, 43.82) * mm});
            skPoint(sketch, "E67.6.1", {"position": v(-91.25, 44.82) * mm});
            skLineSegment(sketch, "E67.6.2", {"start": v(-92.25, 44.82) * mm, "end": v(-97.25, 44.82) * mm});
            skLineSegment(sketch, "E67.6.3", {"start": v(-92.25, 42.82) * mm, "end": v(-97.25, 42.82) * mm});
            skPoint(sketch, "E67.6.4", {"position": v(-98.25, 44.82) * mm});
            skArc(sketch, "E67.6.5", {"start": v(-92.25, 42.82) * mm, "mid": v(-91.54, 43.11) * mm, "end": v(-91.25, 43.82) * mm});
            skPoint(sketch, "E67.6.6", {"position": v(-98.25, 42.82) * mm});
            skArc(sketch, "E67.6.7", {"start": v(-97.25, 44.82) * mm, "mid": v(-97.96, 44.53) * mm, "end": v(-98.25, 43.82) * mm});
            skPoint(sketch, "E67.6.8", {"position": v(-91.25, 42.82) * mm});
            skArc(sketch, "E67.6.9", {"start": v(-98.25, 43.82) * mm, "mid": v(-97.96, 43.11) * mm, "end": v(-97.25, 42.82) * mm});
            skArc(sketch, "E67.6.10", {"start": v(-91.25, 43.82) * mm, "mid": v(-91.54, 44.53) * mm, "end": v(-92.25, 44.82) * mm});
            skPoint(sketch, "E67.7.0", {"position": v(-94.04, 38.45) * mm});
            skPoint(sketch, "E67.7.1", {"position": v(-90.92, 40.32) * mm});
            skLineSegment(sketch, "E67.7.2", {"start": v(-91.89, 40.06) * mm, "end": v(-96.72, 38.77) * mm});
            skLineSegment(sketch, "E67.7.3", {"start": v(-91.37, 38.13) * mm, "end": v(-96.2, 36.84) * mm});
            skPoint(sketch, "E67.7.4", {"position": v(-97.68, 38.5) * mm});
            skArc(sketch, "E67.7.5", {"start": v(-91.37, 38.13) * mm, "mid": v(-90.76, 38.6) * mm, "end": v(-90.66, 39.36) * mm});
            skPoint(sketch, "E67.7.6", {"position": v(-97.16, 36.58) * mm});
            skArc(sketch, "E67.7.7", {"start": v(-96.72, 38.77) * mm, "mid": v(-97.32, 38.3) * mm, "end": v(-97.42, 37.54) * mm});
            skPoint(sketch, "E67.7.8", {"position": v(-90.4, 38.39) * mm});
            skArc(sketch, "E67.7.9", {"start": v(-97.42, 37.54) * mm, "mid": v(-96.96, 36.94) * mm, "end": v(-96.2, 36.84) * mm});
            skArc(sketch, "E67.7.10", {"start": v(-90.66, 39.36) * mm, "mid": v(-91.13, 39.96) * mm, "end": v(-91.89, 40.06) * mm});
            skPoint(sketch, "E67.8.0", {"position": v(-91.97, 33.44) * mm});
            skPoint(sketch, "E67.8.1", {"position": v(-89.44, 36.06) * mm});
            skLineSegment(sketch, "E67.8.2", {"start": v(-90.3, 35.56) * mm, "end": v(-94.64, 33.06) * mm});
            skLineSegment(sketch, "E67.8.3", {"start": v(-89.3, 33.83) * mm, "end": v(-93.64, 31.33) * mm});
            skPoint(sketch, "E67.8.4", {"position": v(-95.5, 32.56) * mm});
            skArc(sketch, "E67.8.5", {"start": v(-89.3, 33.83) * mm, "mid": v(-88.84, 34.44) * mm, "end": v(-88.94, 35.2) * mm});
            skPoint(sketch, "E67.8.6", {"position": v(-94.5, 30.83) * mm});
            skArc(sketch, "E67.8.7", {"start": v(-94.64, 33.06) * mm, "mid": v(-95.1, 32.45) * mm, "end": v(-95, 31.7) * mm});
            skPoint(sketch, "E67.8.8", {"position": v(-88.44, 34.33) * mm});
            skArc(sketch, "E67.8.9", {"start": v(-95, 31.7) * mm, "mid": v(-94.4, 31.23) * mm, "end": v(-93.64, 31.33) * mm});
            skArc(sketch, "E67.8.10", {"start": v(-88.94, 35.2) * mm, "mid": v(-89.55, 35.66) * mm, "end": v(-90.3, 35.56) * mm});
            skPoint(sketch, "E67.9.0", {"position": v(-88.67, 29.15) * mm});
            skPoint(sketch, "E67.9.1", {"position": v(-86.9, 32.33) * mm});
            skLineSegment(sketch, "E67.9.2", {"start": v(-87.61, 31.62) * mm, "end": v(-91.15, 28.09) * mm});
            skLineSegment(sketch, "E67.9.3", {"start": v(-86.2, 30.2) * mm, "end": v(-89.73, 26.67) * mm});
            skPoint(sketch, "E67.9.4", {"position": v(-91.85, 27.38) * mm});
            skArc(sketch, "E67.9.5", {"start": v(-86.2, 30.2) * mm, "mid": v(-85.9, 30.92) * mm, "end": v(-86.2, 31.62) * mm});
            skPoint(sketch, "E67.9.6", {"position": v(-90.44, 25.97) * mm});
            skArc(sketch, "E67.9.7", {"start": v(-91.15, 28.09) * mm, "mid": v(-91.44, 27.38) * mm, "end": v(-91.15, 26.67) * mm});
            skPoint(sketch, "E67.9.8", {"position": v(-85.5, 30.92) * mm});
            skArc(sketch, "E67.9.9", {"start": v(-91.15, 26.67) * mm, "mid": v(-90.44, 26.38) * mm, "end": v(-89.73, 26.67) * mm});
            skArc(sketch, "E67.9.10", {"start": v(-86.2, 31.62) * mm, "mid": v(-86.9, 31.92) * mm, "end": v(-87.61, 31.62) * mm});
            skPoint(sketch, "E67.10.0", {"position": v(-84.38, 25.85) * mm});
            skPoint(sketch, "E67.10.1", {"position": v(-83.5, 29.38) * mm});
            skLineSegment(sketch, "E67.10.2", {"start": v(-84, 28.52) * mm, "end": v(-86.5, 24.18) * mm});
            skLineSegment(sketch, "E67.10.3", {"start": v(-82.26, 27.52) * mm, "end": v(-84.76, 23.18) * mm});
            skPoint(sketch, "E67.10.4", {"position": v(-87, 23.32) * mm});
            skArc(sketch, "E67.10.5", {"start": v(-82.26, 27.52) * mm, "mid": v(-82.16, 28.27) * mm, "end": v(-82.62, 28.88) * mm});
            skPoint(sketch, "E67.10.6", {"position": v(-85.26, 22.32) * mm});
            skArc(sketch, "E67.10.7", {"start": v(-86.5, 24.18) * mm, "mid": v(-86.6, 23.43) * mm, "end": v(-86.12, 22.82) * mm});
            skPoint(sketch, "E67.10.8", {"position": v(-81.76, 28.38) * mm});
            skArc(sketch, "E67.10.9", {"start": v(-86.13, 22.82) * mm, "mid": v(-85.37, 22.72) * mm, "end": v(-84.76, 23.18) * mm});
            skArc(sketch, "E67.10.10", {"start": v(-82.62, 28.88) * mm, "mid": v(-83.38, 28.98) * mm, "end": v(-84, 28.52) * mm});
            skPoint(sketch, "E67.11.0", {"position": v(-79.37, 23.78) * mm});
            skPoint(sketch, "E67.11.1", {"position": v(-79.43, 27.42) * mm});
            skLineSegment(sketch, "E67.11.2", {"start": v(-79.69, 26.45) * mm, "end": v(-80.98, 21.62) * mm});
            skLineSegment(sketch, "E67.11.3", {"start": v(-77.76, 25.93) * mm, "end": v(-79.05, 21.1) * mm});
            skPoint(sketch, "E67.11.4", {"position": v(-81.24, 20.66) * mm});
            skArc(sketch, "E67.11.5", {"start": v(-77.76, 25.93) * mm, "mid": v(-77.86, 26.7) * mm, "end": v(-78.46, 27.16) * mm});
            skPoint(sketch, "E67.11.6", {"position": v(-79.31, 20.14) * mm});
            skArc(sketch, "E67.11.7", {"start": v(-80.98, 21.62) * mm, "mid": v(-80.88, 20.86) * mm, "end": v(-80.28, 20.4) * mm});
            skPoint(sketch, "E67.11.8", {"position": v(-77.5, 26.9) * mm});
            skArc(sketch, "E67.11.9", {"start": v(-80.28, 20.4) * mm, "mid": v(-79.52, 20.5) * mm, "end": v(-79.05, 21.1) * mm});
            skArc(sketch, "E67.11.10", {"start": v(-78.46, 27.16) * mm, "mid": v(-79.22, 27.06) * mm, "end": v(-79.69, 26.45) * mm});
            skPoint(sketch, "E67.12.0", {"position": v(-74, 23.07) * mm});
            skPoint(sketch, "E67.12.1", {"position": v(-75, 26.57) * mm});
            skLineSegment(sketch, "E67.12.2", {"start": v(-75, 25.57) * mm, "end": v(-75, 20.57) * mm});
            skLineSegment(sketch, "E67.12.3", {"start": v(-73, 25.57) * mm, "end": v(-73, 20.57) * mm});
            skPoint(sketch, "E67.12.4", {"position": v(-75, 19.57) * mm});
            skArc(sketch, "E67.12.5", {"start": v(-73, 25.57) * mm, "mid": v(-73.3, 26.28) * mm, "end": v(-74, 26.57) * mm});
            skPoint(sketch, "E67.12.6", {"position": v(-73, 19.57) * mm});
            skArc(sketch, "E67.12.7", {"start": v(-75, 20.57) * mm, "mid": v(-74.7, 19.86) * mm, "end": v(-74, 19.57) * mm});
            skPoint(sketch, "E67.12.8", {"position": v(-73, 26.57) * mm});
            skArc(sketch, "E67.12.9", {"start": v(-74, 19.57) * mm, "mid": v(-73.3, 19.86) * mm, "end": v(-73, 20.57) * mm});
            skArc(sketch, "E67.12.10", {"start": v(-74, 26.57) * mm, "mid": v(-74.7, 26.28) * mm, "end": v(-75, 25.57) * mm});
            skPoint(sketch, "E67.13.0", {"position": v(-68.63, 23.78) * mm});
            skPoint(sketch, "E67.13.1", {"position": v(-70.5, 26.9) * mm});
            skLineSegment(sketch, "E67.13.2", {"start": v(-70.24, 25.93) * mm, "end": v(-68.95, 21.1) * mm});
            skLineSegment(sketch, "E67.13.3", {"start": v(-68.31, 26.45) * mm, "end": v(-67.02, 21.62) * mm});
            skPoint(sketch, "E67.13.4", {"position": v(-68.69, 20.14) * mm});
            skArc(sketch, "E67.13.5", {"start": v(-68.31, 26.45) * mm, "mid": v(-68.78, 27.06) * mm, "end": v(-69.54, 27.16) * mm});
            skPoint(sketch, "E67.13.6", {"position": v(-66.76, 20.66) * mm});
            skArc(sketch, "E67.13.7", {"start": v(-68.95, 21.1) * mm, "mid": v(-68.48, 20.5) * mm, "end": v(-67.72, 20.4) * mm});
            skPoint(sketch, "E67.13.8", {"position": v(-68.57, 27.42) * mm});
            skArc(sketch, "E67.13.9", {"start": v(-67.72, 20.4) * mm, "mid": v(-67.12, 20.86) * mm, "end": v(-67.02, 21.62) * mm});
            skArc(sketch, "E67.13.10", {"start": v(-69.54, 27.16) * mm, "mid": v(-70.14, 26.7) * mm, "end": v(-70.24, 25.93) * mm});
            skPoint(sketch, "E67.14.0", {"position": v(-63.63, 25.85) * mm});
            skPoint(sketch, "E67.14.1", {"position": v(-66.24, 28.38) * mm});
            skLineSegment(sketch, "E67.14.2", {"start": v(-65.74, 27.52) * mm, "end": v(-63.24, 23.18) * mm});
            skLineSegment(sketch, "E67.14.3", {"start": v(-64, 28.52) * mm, "end": v(-61.5, 24.18) * mm});
            skPoint(sketch, "E67.14.4", {"position": v(-62.74, 22.32) * mm});
            skArc(sketch, "E67.14.5", {"start": v(-64, 28.52) * mm, "mid": v(-64.62, 28.98) * mm, "end": v(-65.37, 28.88) * mm});
            skPoint(sketch, "E67.14.6", {"position": v(-61, 23.32) * mm});
            skArc(sketch, "E67.14.7", {"start": v(-63.24, 23.18) * mm, "mid": v(-62.63, 22.72) * mm, "end": v(-61.88, 22.82) * mm});
            skPoint(sketch, "E67.14.8", {"position": v(-64.5, 29.38) * mm});
            skArc(sketch, "E67.14.9", {"start": v(-61.88, 22.82) * mm, "mid": v(-61.4, 23.43) * mm, "end": v(-61.5, 24.18) * mm});
            skArc(sketch, "E67.14.10", {"start": v(-65.38, 28.88) * mm, "mid": v(-65.84, 28.27) * mm, "end": v(-65.74, 27.52) * mm});
            skPoint(sketch, "E67.15.0", {"position": v(-59.33, 29.15) * mm});
            skPoint(sketch, "E67.15.1", {"position": v(-62.5, 30.92) * mm});
            skLineSegment(sketch, "E67.15.2", {"start": v(-61.8, 30.2) * mm, "end": v(-58.27, 26.67) * mm});
            skLineSegment(sketch, "E67.15.3", {"start": v(-60.39, 31.62) * mm, "end": v(-56.85, 28.09) * mm});
            skPoint(sketch, "E67.15.4", {"position": v(-57.56, 25.97) * mm});
            skArc(sketch, "E67.15.5", {"start": v(-60.39, 31.62) * mm, "mid": v(-61.1, 31.92) * mm, "end": v(-61.8, 31.62) * mm});
            skPoint(sketch, "E67.15.6", {"position": v(-56.15, 27.38) * mm});
            skArc(sketch, "E67.15.7", {"start": v(-58.27, 26.67) * mm, "mid": v(-57.56, 26.38) * mm, "end": v(-56.85, 26.67) * mm});
            skPoint(sketch, "E67.15.8", {"position": v(-61.1, 32.33) * mm});
            skArc(sketch, "E67.15.9", {"start": v(-56.85, 26.67) * mm, "mid": v(-56.56, 27.38) * mm, "end": v(-56.85, 28.09) * mm});
            skArc(sketch, "E67.15.10", {"start": v(-61.8, 31.62) * mm, "mid": v(-62.1, 30.92) * mm, "end": v(-61.8, 30.2) * mm});
            skPoint(sketch, "E67.16.0", {"position": v(-56.03, 33.44) * mm});
            skPoint(sketch, "E67.16.1", {"position": v(-59.56, 34.33) * mm});
            skLineSegment(sketch, "E67.16.2", {"start": v(-58.7, 33.83) * mm, "end": v(-54.36, 31.33) * mm});
            skLineSegment(sketch, "E67.16.3", {"start": v(-57.7, 35.56) * mm, "end": v(-53.36, 33.06) * mm});
            skPoint(sketch, "E67.16.4", {"position": v(-53.5, 30.83) * mm});
            skArc(sketch, "E67.16.5", {"start": v(-57.7, 35.56) * mm, "mid": v(-58.45, 35.66) * mm, "end": v(-59.06, 35.2) * mm});
            skPoint(sketch, "E67.16.6", {"position": v(-52.5, 32.56) * mm});
            skArc(sketch, "E67.16.7", {"start": v(-54.36, 31.33) * mm, "mid": v(-53.6, 31.23) * mm, "end": v(-53, 31.7) * mm});
            skPoint(sketch, "E67.16.8", {"position": v(-58.56, 36.06) * mm});
            skArc(sketch, "E67.16.9", {"start": v(-53, 31.7) * mm, "mid": v(-52.9, 32.45) * mm, "end": v(-53.36, 33.06) * mm});
            skArc(sketch, "E67.16.10", {"start": v(-59.06, 35.2) * mm, "mid": v(-59.16, 34.44) * mm, "end": v(-58.7, 33.83) * mm});
            skPoint(sketch, "E67.17.0", {"position": v(-53.96, 38.45) * mm});
            skPoint(sketch, "E67.17.1", {"position": v(-57.6, 38.39) * mm});
            skLineSegment(sketch, "E67.17.2", {"start": v(-56.63, 38.13) * mm, "end": v(-51.8, 36.84) * mm});
            skLineSegment(sketch, "E67.17.3", {"start": v(-56.11, 40.06) * mm, "end": v(-51.28, 38.77) * mm});
            skPoint(sketch, "E67.17.4", {"position": v(-50.84, 36.58) * mm});
            skArc(sketch, "E67.17.5", {"start": v(-56.11, 40.06) * mm, "mid": v(-56.87, 39.96) * mm, "end": v(-57.34, 39.36) * mm});
            skPoint(sketch, "E67.17.6", {"position": v(-50.32, 38.5) * mm});
            skArc(sketch, "E67.17.7", {"start": v(-51.8, 36.84) * mm, "mid": v(-51.04, 36.94) * mm, "end": v(-50.58, 37.54) * mm});
            skPoint(sketch, "E67.17.8", {"position": v(-57.08, 40.32) * mm});
            skArc(sketch, "E67.17.9", {"start": v(-50.58, 37.54) * mm, "mid": v(-50.68, 38.3) * mm, "end": v(-51.28, 38.77) * mm});
            skArc(sketch, "E67.17.10", {"start": v(-57.34, 39.36) * mm, "mid": v(-57.24, 38.6) * mm, "end": v(-56.63, 38.13) * mm});
            skPoint(sketch, "E67.18.0", {"position": v(-53.25, 43.82) * mm});
            skPoint(sketch, "E67.18.1", {"position": v(-56.75, 42.82) * mm});
            skLineSegment(sketch, "E67.18.2", {"start": v(-55.75, 42.82) * mm, "end": v(-50.75, 42.82) * mm});
            skLineSegment(sketch, "E67.18.3", {"start": v(-55.75, 44.82) * mm, "end": v(-50.75, 44.82) * mm});
            skPoint(sketch, "E67.18.4", {"position": v(-49.75, 42.82) * mm});
            skArc(sketch, "E67.18.5", {"start": v(-55.75, 44.82) * mm, "mid": v(-56.46, 44.53) * mm, "end": v(-56.75, 43.82) * mm});
            skPoint(sketch, "E67.18.6", {"position": v(-49.75, 44.82) * mm});
            skArc(sketch, "E67.18.7", {"start": v(-50.75, 42.82) * mm, "mid": v(-50.04, 43.11) * mm, "end": v(-49.75, 43.82) * mm});
            skPoint(sketch, "E67.18.8", {"position": v(-56.75, 44.82) * mm});
            skArc(sketch, "E67.18.9", {"start": v(-49.75, 43.82) * mm, "mid": v(-50.04, 44.53) * mm, "end": v(-50.75, 44.82) * mm});
            skArc(sketch, "E67.18.10", {"start": v(-56.75, 43.82) * mm, "mid": v(-56.46, 43.11) * mm, "end": v(-55.75, 42.82) * mm});
            skPoint(sketch, "E67.19.0", {"position": v(-53.96, 49.2) * mm});
            skPoint(sketch, "E67.19.1", {"position": v(-57.08, 47.32) * mm});
            skLineSegment(sketch, "E67.19.2", {"start": v(-56.11, 47.58) * mm, "end": v(-51.28, 48.87) * mm});
            skLineSegment(sketch, "E67.19.3", {"start": v(-56.63, 49.5) * mm, "end": v(-51.8, 50.8) * mm});
            skPoint(sketch, "E67.19.4", {"position": v(-50.32, 49.13) * mm});
            skArc(sketch, "E67.19.5", {"start": v(-56.63, 49.5) * mm, "mid": v(-57.24, 49.04) * mm, "end": v(-57.34, 48.28) * mm});
            skPoint(sketch, "E67.19.6", {"position": v(-50.84, 51.06) * mm});
            skArc(sketch, "E67.19.7", {"start": v(-51.28, 48.87) * mm, "mid": v(-50.68, 49.34) * mm, "end": v(-50.58, 50.1) * mm});
            skPoint(sketch, "E67.19.8", {"position": v(-57.6, 49.25) * mm});
            skArc(sketch, "E67.19.9", {"start": v(-50.58, 50.1) * mm, "mid": v(-51.04, 50.7) * mm, "end": v(-51.8, 50.8) * mm});
            skArc(sketch, "E67.19.10", {"start": v(-57.34, 48.28) * mm, "mid": v(-56.87, 47.68) * mm, "end": v(-56.11, 47.58) * mm});
            skPoint(sketch, "E68.0.20.0", {"position": v(-59.56, 53.31) * mm});
            skPoint(sketch, "E68.1.20.0", {"position": v(-58.56, 51.58) * mm});
            skLineSegment(sketch, "E68.2.20.0", {"start": v(-57.7, 52.08) * mm, "end": v(-53.36, 54.58) * mm});
            skLineSegment(sketch, "E68.5.20.0", {"start": v(-58.7, 53.81) * mm, "end": v(-54.36, 56.31) * mm});
            skPoint(sketch, "E68.8.20.0", {"position": v(-52.5, 55.08) * mm});
            skArc(sketch, "E68.9.20.0", {"start": v(-58.7, 53.81) * mm, "mid": v(-59.16, 53.2) * mm, "end": v(-59.06, 52.44) * mm});
            skPoint(sketch, "E68.13.20.0", {"position": v(-53.5, 56.81) * mm});
            skArc(sketch, "E68.14.20.0", {"start": v(-53.36, 54.58) * mm, "mid": v(-52.9, 55.19) * mm, "end": v(-53, 55.94) * mm});
            skPoint(sketch, "E68.18.20.0", {"position": v(-56.03, 54.2) * mm});
            skArc(sketch, "E68.19.20.0", {"start": v(-53, 55.94) * mm, "mid": v(-53.6, 56.41) * mm, "end": v(-54.36, 56.31) * mm});
            skArc(sketch, "E68.23.20.0", {"start": v(-59.06, 52.44) * mm, "mid": v(-58.45, 51.98) * mm, "end": v(-57.7, 52.08) * mm});
            skPoint(sketch, "E68.0.21.0", {"position": v(-62.5, 56.72) * mm});
            skPoint(sketch, "E68.1.21.0", {"position": v(-61.1, 55.31) * mm});
            skLineSegment(sketch, "E68.2.21.0", {"start": v(-60.39, 56.02) * mm, "end": v(-56.85, 59.55) * mm});
            skLineSegment(sketch, "E68.5.21.0", {"start": v(-61.8, 57.43) * mm, "end": v(-58.27, 60.97) * mm});
            skPoint(sketch, "E68.8.21.0", {"position": v(-56.15, 60.26) * mm});
            skArc(sketch, "E68.9.21.0", {"start": v(-61.8, 57.43) * mm, "mid": v(-62.1, 56.72) * mm, "end": v(-61.8, 56.02) * mm});
            skPoint(sketch, "E68.13.21.0", {"position": v(-57.56, 61.67) * mm});
            skArc(sketch, "E68.14.21.0", {"start": v(-56.85, 59.55) * mm, "mid": v(-56.56, 60.26) * mm, "end": v(-56.85, 60.97) * mm});
            skPoint(sketch, "E68.18.21.0", {"position": v(-59.33, 58.5) * mm});
            skArc(sketch, "E68.19.21.0", {"start": v(-56.85, 60.97) * mm, "mid": v(-57.56, 61.26) * mm, "end": v(-58.27, 60.97) * mm});
            skArc(sketch, "E68.23.21.0", {"start": v(-61.8, 56.02) * mm, "mid": v(-61.1, 55.72) * mm, "end": v(-60.39, 56.02) * mm});
            skPoint(sketch, "E68.0.22.0", {"position": v(-66.24, 59.26) * mm});
            skPoint(sketch, "E68.1.22.0", {"position": v(-64.5, 58.26) * mm});
            skLineSegment(sketch, "E68.2.22.0", {"start": v(-64, 59.12) * mm, "end": v(-61.5, 63.46) * mm});
            skLineSegment(sketch, "E68.5.22.0", {"start": v(-65.74, 60.12) * mm, "end": v(-63.24, 64.46) * mm});
            skPoint(sketch, "E68.8.22.0", {"position": v(-61, 64.32) * mm});
            skArc(sketch, "E68.9.22.0", {"start": v(-65.74, 60.12) * mm, "mid": v(-65.84, 59.37) * mm, "end": v(-65.37, 58.76) * mm});
            skPoint(sketch, "E68.13.22.0", {"position": v(-62.74, 65.32) * mm});
            skArc(sketch, "E68.14.22.0", {"start": v(-61.5, 63.46) * mm, "mid": v(-61.4, 64.21) * mm, "end": v(-61.87, 64.82) * mm});
            skPoint(sketch, "E68.18.22.0", {"position": v(-63.62, 61.8) * mm});
            skArc(sketch, "E68.19.22.0", {"start": v(-61.87, 64.82) * mm, "mid": v(-62.63, 64.92) * mm, "end": v(-63.24, 64.46) * mm});
            skArc(sketch, "E68.23.22.0", {"start": v(-65.37, 58.76) * mm, "mid": v(-64.62, 58.66) * mm, "end": v(-64, 59.12) * mm});
            skPoint(sketch, "E68.0.23.0", {"position": v(-70.5, 60.74) * mm});
            skPoint(sketch, "E68.1.23.0", {"position": v(-68.57, 60.22) * mm});
            skLineSegment(sketch, "E68.2.23.0", {"start": v(-68.31, 61.19) * mm, "end": v(-67.02, 66.02) * mm});
            skLineSegment(sketch, "E68.5.23.0", {"start": v(-70.24, 61.7) * mm, "end": v(-68.95, 66.54) * mm});
            skPoint(sketch, "E68.8.23.0", {"position": v(-66.76, 66.98) * mm});
            skArc(sketch, "E68.9.23.0", {"start": v(-70.24, 61.7) * mm, "mid": v(-70.14, 60.95) * mm, "end": v(-69.54, 60.48) * mm});
            skPoint(sketch, "E68.13.23.0", {"position": v(-68.69, 67.5) * mm});
            skArc(sketch, "E68.14.23.0", {"start": v(-67.02, 66.02) * mm, "mid": v(-67.12, 66.78) * mm, "end": v(-67.72, 67.24) * mm});
            skPoint(sketch, "E68.18.23.0", {"position": v(-68.63, 63.86) * mm});
            skArc(sketch, "E68.19.23.0", {"start": v(-67.72, 67.24) * mm, "mid": v(-68.48, 67.14) * mm, "end": v(-68.95, 66.54) * mm});
            skArc(sketch, "E68.23.23.0", {"start": v(-69.54, 60.48) * mm, "mid": v(-68.78, 60.58) * mm, "end": v(-68.31, 61.19) * mm});
            skLineSegment(sketch, "E69.bottom", {"start": v(22.52, -64.67) * mm, "end": v(22.52, -64.67) * mm});
            skLineSegment(sketch, "E69.top", {"start": v(22.52, -57.67) * mm, "end": v(22.52, -57.67) * mm});
            skLineSegment(sketch, "E69.left", {"start": v(23.52, -63.67) * mm, "end": v(23.52, -58.67) * mm});
            skLineSegment(sketch, "E69.right", {"start": v(21.52, -63.67) * mm, "end": v(21.52, -58.67) * mm});
            skPoint(sketch, "E69.middle", {"position": v(22.52, -61.17) * mm});
            skPoint(sketch, "E70.visualSharp", {"position": v(23.52, -57.67) * mm});
            skArc(sketch, "E70.filletArc", {"start": v(23.52, -58.67) * mm, "mid": v(23.23, -57.96) * mm, "end": v(22.52, -57.67) * mm});
            skPoint(sketch, "E71.visualSharp", {"position": v(21.52, -57.67) * mm});
            skArc(sketch, "E71.filletArc", {"start": v(22.52, -57.67) * mm, "mid": v(21.81, -57.96) * mm, "end": v(21.52, -58.67) * mm});
            skPoint(sketch, "E72.visualSharp", {"position": v(21.52, -64.67) * mm});
            skArc(sketch, "E72.filletArc", {"start": v(21.52, -63.67) * mm, "mid": v(21.81, -64.38) * mm, "end": v(22.52, -64.67) * mm});
            skPoint(sketch, "E73.visualSharp", {"position": v(23.52, -64.67) * mm});
            skArc(sketch, "E73.filletArc", {"start": v(22.52, -64.67) * mm, "mid": v(23.23, -64.38) * mm, "end": v(23.52, -63.67) * mm});
            skLineSegment(sketch, "E74.bottom", {"start": v(-118, -10.75) * mm, "end": v(-118, -10.75) * mm});
            skLineSegment(sketch, "E74.top", {"start": v(-118, -3.75) * mm, "end": v(-118, -3.75) * mm});
            skLineSegment(sketch, "E74.left", {"start": v(-117, -9.75) * mm, "end": v(-117, -4.75) * mm});
            skLineSegment(sketch, "E74.right", {"start": v(-119, -9.75) * mm, "end": v(-119, -4.75) * mm});
            skPoint(sketch, "E74.middle", {"position": v(-118, -7.25) * mm});
            skPoint(sketch, "E75.visualSharp", {"position": v(-117, -3.75) * mm});
            skArc(sketch, "E75.filletArc", {"start": v(-117, -4.75) * mm, "mid": v(-117.3, -4.04) * mm, "end": v(-118, -3.75) * mm});
            skPoint(sketch, "E76.visualSharp", {"position": v(-119, -3.75) * mm});
            skArc(sketch, "E76.filletArc", {"start": v(-118, -3.75) * mm, "mid": v(-118.7, -4.04) * mm, "end": v(-119, -4.75) * mm});
            skPoint(sketch, "E77.visualSharp", {"position": v(-119, -10.75) * mm});
            skArc(sketch, "E77.filletArc", {"start": v(-119, -9.75) * mm, "mid": v(-118.7, -10.46) * mm, "end": v(-118, -10.75) * mm});
            skPoint(sketch, "E78.visualSharp", {"position": v(-117, -10.75) * mm});
            skArc(sketch, "E78.filletArc", {"start": v(-118, -10.75) * mm, "mid": v(-117.3, -10.46) * mm, "end": v(-117, -9.75) * mm});
            skLineSegment(sketch, "E79.bottom", {"start": v(-74, -26.57) * mm, "end": v(-74, -26.57) * mm});
            skLineSegment(sketch, "E79.top", {"start": v(-74, -19.57) * mm, "end": v(-74, -19.57) * mm});
            skLineSegment(sketch, "E79.left", {"start": v(-73, -25.57) * mm, "end": v(-73, -20.57) * mm});
            skLineSegment(sketch, "E79.right", {"start": v(-75, -25.57) * mm, "end": v(-75, -20.57) * mm});
            skPoint(sketch, "E79.middle", {"position": v(-74, -23.07) * mm});
            skPoint(sketch, "E80.visualSharp", {"position": v(-73, -19.57) * mm});
            skArc(sketch, "E80.filletArc", {"start": v(-73, -20.57) * mm, "mid": v(-73.3, -19.86) * mm, "end": v(-74, -19.57) * mm});
            skPoint(sketch, "E81.visualSharp", {"position": v(-75, -19.57) * mm});
            skArc(sketch, "E81.filletArc", {"start": v(-74, -19.57) * mm, "mid": v(-74.7, -19.86) * mm, "end": v(-75, -20.57) * mm});
            skPoint(sketch, "E82.visualSharp", {"position": v(-75, -26.57) * mm});
            skArc(sketch, "E82.filletArc", {"start": v(-75, -25.57) * mm, "mid": v(-74.7, -26.28) * mm, "end": v(-74, -26.57) * mm});
            skPoint(sketch, "E83.visualSharp", {"position": v(-73, -26.57) * mm});
            skArc(sketch, "E83.filletArc", {"start": v(-74, -26.57) * mm, "mid": v(-73.3, -26.28) * mm, "end": v(-73, -25.57) * mm});
            skLineSegment(sketch, "E84.bottom", {"start": v(-25.74, -45.6) * mm, "end": v(-25.74, -45.6) * mm});
            skLineSegment(sketch, "E84.top", {"start": v(-25.74, -38.6) * mm, "end": v(-25.74, -38.6) * mm});
            skLineSegment(sketch, "E84.left", {"start": v(-24.74, -44.6) * mm, "end": v(-24.74, -39.6) * mm});
            skLineSegment(sketch, "E84.right", {"start": v(-26.74, -44.6) * mm, "end": v(-26.74, -39.6) * mm});
            skPoint(sketch, "E84.middle", {"position": v(-25.74, -42.1) * mm});
            skPoint(sketch, "E85.visualSharp", {"position": v(-24.74, -38.6) * mm});
            skArc(sketch, "E85.filletArc", {"start": v(-24.74, -39.6) * mm, "mid": v(-25.03, -38.9) * mm, "end": v(-25.74, -38.6) * mm});
            skPoint(sketch, "E86.visualSharp", {"position": v(-26.74, -38.6) * mm});
            skArc(sketch, "E86.filletArc", {"start": v(-25.74, -38.6) * mm, "mid": v(-26.45, -38.9) * mm, "end": v(-26.74, -39.6) * mm});
            skPoint(sketch, "E87.visualSharp", {"position": v(-26.74, -45.6) * mm});
            skArc(sketch, "E87.filletArc", {"start": v(-26.74, -44.6) * mm, "mid": v(-26.45, -45.32) * mm, "end": v(-25.74, -45.61) * mm});
            skPoint(sketch, "E88.visualSharp", {"position": v(-24.74, -45.6) * mm});
            skArc(sketch, "E88.filletArc", {"start": v(-25.74, -45.61) * mm, "mid": v(-25.03, -45.32) * mm, "end": v(-24.74, -44.6) * mm});
            skLineSegment(sketch, "E89.bottom", {"start": v(-25.74, 80.11) * mm, "end": v(-25.74, 80.11) * mm});
            skLineSegment(sketch, "E89.top", {"start": v(-25.74, 87.11) * mm, "end": v(-25.74, 87.11) * mm});
            skLineSegment(sketch, "E89.left", {"start": v(-24.74, 81.11) * mm, "end": v(-24.74, 86.11) * mm});
            skLineSegment(sketch, "E89.right", {"start": v(-26.74, 81.11) * mm, "end": v(-26.74, 86.11) * mm});
            skPoint(sketch, "E89.middle", {"position": v(-25.74, 83.61) * mm});
            skPoint(sketch, "E90.visualSharp", {"position": v(-24.74, 87.11) * mm});
            skArc(sketch, "E90.filletArc", {"start": v(-24.74, 86.11) * mm, "mid": v(-25.03, 86.82) * mm, "end": v(-25.74, 87.11) * mm});
            skPoint(sketch, "E91.visualSharp", {"position": v(-26.74, 87.11) * mm});
            skArc(sketch, "E91.filletArc", {"start": v(-25.74, 87.11) * mm, "mid": v(-26.45, 86.82) * mm, "end": v(-26.74, 86.11) * mm});
            skPoint(sketch, "E92.visualSharp", {"position": v(-26.74, 80.11) * mm});
            skArc(sketch, "E92.filletArc", {"start": v(-26.74, 81.11) * mm, "mid": v(-26.45, 80.4) * mm, "end": v(-25.74, 80.11) * mm});
            skPoint(sketch, "E93.visualSharp", {"position": v(-24.74, 80.11) * mm});
            skArc(sketch, "E93.filletArc", {"start": v(-25.74, 80.11) * mm, "mid": v(-25.03, 80.4) * mm, "end": v(-24.74, 81.11) * mm});
            skLineSegment(sketch, "E94.bottom", {"start": v(22.52, 99.17) * mm, "end": v(22.52, 99.17) * mm});
            skLineSegment(sketch, "E94.top", {"start": v(22.52, 106.17) * mm, "end": v(22.52, 106.17) * mm});
            skLineSegment(sketch, "E94.left", {"start": v(23.52, 100.17) * mm, "end": v(23.52, 105.17) * mm});
            skLineSegment(sketch, "E94.right", {"start": v(21.52, 100.17) * mm, "end": v(21.52, 105.17) * mm});
            skPoint(sketch, "E94.middle", {"position": v(22.52, 102.67) * mm});
            skPoint(sketch, "E95.visualSharp", {"position": v(23.52, 106.17) * mm});
            skArc(sketch, "E95.filletArc", {"start": v(23.52, 105.17) * mm, "mid": v(23.23, 105.88) * mm, "end": v(22.52, 106.17) * mm});
            skPoint(sketch, "E96.visualSharp", {"position": v(21.52, 106.17) * mm});
            skArc(sketch, "E96.filletArc", {"start": v(22.52, 106.17) * mm, "mid": v(21.81, 105.88) * mm, "end": v(21.52, 105.17) * mm});
            skPoint(sketch, "E97.visualSharp", {"position": v(21.52, 99.17) * mm});
            skArc(sketch, "E97.filletArc", {"start": v(21.52, 100.17) * mm, "mid": v(21.81, 99.46) * mm, "end": v(22.52, 99.17) * mm});
            skPoint(sketch, "E98.visualSharp", {"position": v(23.52, 99.17) * mm});
            skArc(sketch, "E98.filletArc", {"start": v(22.52, 99.17) * mm, "mid": v(23.23, 99.46) * mm, "end": v(23.52, 100.17) * mm});
            skLineSegment(sketch, "E99", {"start": v(22.52, 92.76) * mm, "end": v(22.52, 112.58) * mm, "construction": true});
            skLineSegment(sketch, "E100", {"start": v(-25.74, 60.16) * mm, "end": v(-25.74, 107.06) * mm, "construction": true});
            skPoint(sketch, "E101.1.0", {"position": v(-31.17, 79.26) * mm});
            skArc(sketch, "E101.1.1", {"start": v(-30.2, 79.52) * mm, "mid": v(-29.6, 79.99) * mm, "end": v(-29.5, 80.75) * mm});
            skPoint(sketch, "E101.1.2", {"position": v(-31.11, 82.9) * mm});
            skPoint(sketch, "E101.1.3", {"position": v(-29.24, 79.78) * mm});
            skLineSegment(sketch, "E101.1.4", {"start": v(-29.5, 80.75) * mm, "end": v(-30.8, 85.58) * mm});
            skLineSegment(sketch, "E101.1.5", {"start": v(-31.43, 80.23) * mm, "end": v(-32.72, 85.06) * mm});
            skArc(sketch, "E101.1.6", {"start": v(-31.43, 80.23) * mm, "mid": v(-30.96, 79.62) * mm, "end": v(-30.2, 79.52) * mm});
            skPoint(sketch, "E101.1.7", {"position": v(-31.05, 86.54) * mm});
            skPoint(sketch, "E101.1.8", {"position": v(-32.98, 86.02) * mm});
            skArc(sketch, "E101.1.9", {"start": v(-30.8, 85.58) * mm, "mid": v(-31.26, 86.18) * mm, "end": v(-32.02, 86.28) * mm});
            skArc(sketch, "E101.1.10", {"start": v(-32.02, 86.28) * mm, "mid": v(-32.62, 85.82) * mm, "end": v(-32.72, 85.06) * mm});
            skPoint(sketch, "E101.2.0", {"position": v(-35.23, 77.3) * mm});
            skArc(sketch, "E101.2.1", {"start": v(-34.37, 77.8) * mm, "mid": v(-33.9, 78.4) * mm, "end": v(-34, 79.16) * mm});
            skPoint(sketch, "E101.2.2", {"position": v(-36.12, 80.83) * mm});
            skPoint(sketch, "E101.2.3", {"position": v(-33.5, 78.3) * mm});
            skLineSegment(sketch, "E101.2.4", {"start": v(-34, 79.16) * mm, "end": v(-36.5, 83.5) * mm});
            skLineSegment(sketch, "E101.2.5", {"start": v(-35.73, 78.16) * mm, "end": v(-38.23, 82.5) * mm});
            skArc(sketch, "E101.2.6", {"start": v(-35.73, 78.16) * mm, "mid": v(-35.12, 77.7) * mm, "end": v(-34.37, 77.8) * mm});
            skPoint(sketch, "E101.2.7", {"position": v(-37, 84.36) * mm});
            skPoint(sketch, "E101.2.8", {"position": v(-38.73, 83.36) * mm});
            skArc(sketch, "E101.2.9", {"start": v(-36.5, 83.5) * mm, "mid": v(-37.1, 83.96) * mm, "end": v(-37.87, 83.86) * mm});
            skArc(sketch, "E101.2.10", {"start": v(-37.87, 83.86) * mm, "mid": v(-38.33, 83.25) * mm, "end": v(-38.23, 82.5) * mm});
            skPoint(sketch, "E101.3.0", {"position": v(-38.64, 74.35) * mm});
            skArc(sketch, "E101.3.1", {"start": v(-37.94, 75.06) * mm, "mid": v(-37.64, 75.76) * mm, "end": v(-37.94, 76.47) * mm});
            skPoint(sketch, "E101.3.2", {"position": v(-40.41, 77.53) * mm});
            skPoint(sketch, "E101.3.3", {"position": v(-37.23, 75.76) * mm});
            skLineSegment(sketch, "E101.3.4", {"start": v(-37.94, 76.47) * mm, "end": v(-41.47, 80) * mm});
            skLineSegment(sketch, "E101.3.5", {"start": v(-39.35, 75.06) * mm, "end": v(-42.89, 78.6) * mm});
            skArc(sketch, "E101.3.6", {"start": v(-39.35, 75.06) * mm, "mid": v(-38.64, 74.76) * mm, "end": v(-37.94, 75.06) * mm});
            skPoint(sketch, "E101.3.7", {"position": v(-42.18, 80.71) * mm});
            skPoint(sketch, "E101.3.8", {"position": v(-43.6, 79.3) * mm});
            skArc(sketch, "E101.3.9", {"start": v(-41.47, 80) * mm, "mid": v(-42.18, 80.3) * mm, "end": v(-42.89, 80) * mm});
            skArc(sketch, "E101.3.10", {"start": v(-42.89, 80) * mm, "mid": v(-43.18, 79.3) * mm, "end": v(-42.89, 78.6) * mm});
            skPoint(sketch, "E101.4.0", {"position": v(-41.18, 70.62) * mm});
            skArc(sketch, "E101.4.1", {"start": v(-40.68, 71.48) * mm, "mid": v(-40.58, 72.24) * mm, "end": v(-41.04, 72.85) * mm});
            skPoint(sketch, "E101.4.2", {"position": v(-43.71, 73.23) * mm});
            skPoint(sketch, "E101.4.3", {"position": v(-40.18, 72.35) * mm});
            skLineSegment(sketch, "E101.4.4", {"start": v(-41.04, 72.85) * mm, "end": v(-45.38, 75.35) * mm});
            skLineSegment(sketch, "E101.4.5", {"start": v(-42.04, 71.12) * mm, "end": v(-46.38, 73.62) * mm});
            skArc(sketch, "E101.4.6", {"start": v(-42.04, 71.12) * mm, "mid": v(-41.29, 71.02) * mm, "end": v(-40.68, 71.48) * mm});
            skPoint(sketch, "E101.4.7", {"position": v(-46.24, 75.85) * mm});
            skPoint(sketch, "E101.4.8", {"position": v(-47.24, 74.12) * mm});
            skArc(sketch, "E101.4.9", {"start": v(-45.38, 75.35) * mm, "mid": v(-46.13, 75.45) * mm, "end": v(-46.74, 74.98) * mm});
            skArc(sketch, "E101.4.10", {"start": v(-46.74, 74.98) * mm, "mid": v(-46.84, 74.23) * mm, "end": v(-46.38, 73.62) * mm});
            skPoint(sketch, "E101.5.0", {"position": v(-42.66, 66.36) * mm});
            skArc(sketch, "E101.5.1", {"start": v(-42.4, 67.32) * mm, "mid": v(-42.5, 68.08) * mm, "end": v(-43.1, 68.55) * mm});
            skPoint(sketch, "E101.5.2", {"position": v(-45.78, 68.23) * mm});
            skPoint(sketch, "E101.5.3", {"position": v(-42.14, 68.3) * mm});
            skLineSegment(sketch, "E101.5.4", {"start": v(-43.1, 68.55) * mm, "end": v(-47.94, 69.84) * mm});
            skLineSegment(sketch, "E101.5.5", {"start": v(-43.63, 66.62) * mm, "end": v(-48.46, 67.91) * mm});
            skArc(sketch, "E101.5.6", {"start": v(-43.63, 66.62) * mm, "mid": v(-42.87, 66.72) * mm, "end": v(-42.4, 67.32) * mm});
            skPoint(sketch, "E101.5.7", {"position": v(-48.9, 70.1) * mm});
            skPoint(sketch, "E101.5.8", {"position": v(-49.42, 68.17) * mm});
            skArc(sketch, "E101.5.9", {"start": v(-47.94, 69.84) * mm, "mid": v(-48.7, 69.74) * mm, "end": v(-49.16, 69.14) * mm});
            skArc(sketch, "E101.5.10", {"start": v(-49.16, 69.14) * mm, "mid": v(-49.06, 68.38) * mm, "end": v(-48.46, 67.91) * mm});
            skPoint(sketch, "E101.6.0", {"position": v(-42.99, 61.86) * mm});
            skArc(sketch, "E101.6.1", {"start": v(-42.99, 62.86) * mm, "mid": v(-43.28, 63.57) * mm, "end": v(-43.99, 63.86) * mm});
            skPoint(sketch, "E101.6.2", {"position": v(-46.49, 62.86) * mm});
            skPoint(sketch, "E101.6.3", {"position": v(-42.99, 63.86) * mm});
            skLineSegment(sketch, "E101.6.4", {"start": v(-43.99, 63.86) * mm, "end": v(-48.99, 63.86) * mm});
            skLineSegment(sketch, "E101.6.5", {"start": v(-43.99, 61.86) * mm, "end": v(-48.99, 61.86) * mm});
            skArc(sketch, "E101.6.6", {"start": v(-43.99, 61.86) * mm, "mid": v(-43.28, 62.15) * mm, "end": v(-42.99, 62.86) * mm});
            skPoint(sketch, "E101.6.7", {"position": v(-49.99, 63.86) * mm});
            skPoint(sketch, "E101.6.8", {"position": v(-49.99, 61.86) * mm});
            skArc(sketch, "E101.6.9", {"start": v(-48.99, 63.86) * mm, "mid": v(-49.7, 63.57) * mm, "end": v(-49.99, 62.86) * mm});
            skArc(sketch, "E101.6.10", {"start": v(-49.99, 62.86) * mm, "mid": v(-49.7, 62.15) * mm, "end": v(-48.99, 61.86) * mm});
            skPoint(sketch, "E101.7.0", {"position": v(-42.14, 57.43) * mm});
            skArc(sketch, "E101.7.1", {"start": v(-42.4, 58.4) * mm, "mid": v(-42.87, 59) * mm, "end": v(-43.63, 59.1) * mm});
            skPoint(sketch, "E101.7.2", {"position": v(-45.78, 57.49) * mm});
            skPoint(sketch, "E101.7.3", {"position": v(-42.66, 59.36) * mm});
            skLineSegment(sketch, "E101.7.4", {"start": v(-43.63, 59.1) * mm, "end": v(-48.46, 57.8) * mm});
            skLineSegment(sketch, "E101.7.5", {"start": v(-43.1, 57.17) * mm, "end": v(-47.94, 55.88) * mm});
            skArc(sketch, "E101.7.6", {"start": v(-43.1, 57.17) * mm, "mid": v(-42.5, 57.64) * mm, "end": v(-42.4, 58.4) * mm});
            skPoint(sketch, "E101.7.7", {"position": v(-49.42, 57.55) * mm});
            skPoint(sketch, "E101.7.8", {"position": v(-48.9, 55.62) * mm});
            skArc(sketch, "E101.7.9", {"start": v(-48.46, 57.8) * mm, "mid": v(-49.06, 57.34) * mm, "end": v(-49.16, 56.58) * mm});
            skArc(sketch, "E101.7.10", {"start": v(-49.16, 56.58) * mm, "mid": v(-48.7, 55.98) * mm, "end": v(-47.94, 55.88) * mm});
            skPoint(sketch, "E101.8.0", {"position": v(-40.18, 53.37) * mm});
            skArc(sketch, "E101.8.1", {"start": v(-40.68, 54.23) * mm, "mid": v(-41.29, 54.7) * mm, "end": v(-42.04, 54.6) * mm});
            skPoint(sketch, "E101.8.2", {"position": v(-43.71, 52.48) * mm});
            skPoint(sketch, "E101.8.3", {"position": v(-41.18, 55.1) * mm});
            skLineSegment(sketch, "E101.8.4", {"start": v(-42.04, 54.6) * mm, "end": v(-46.38, 52.1) * mm});
            skLineSegment(sketch, "E101.8.5", {"start": v(-41.04, 52.87) * mm, "end": v(-45.38, 50.37) * mm});
            skArc(sketch, "E101.8.6", {"start": v(-41.04, 52.87) * mm, "mid": v(-40.58, 53.48) * mm, "end": v(-40.68, 54.23) * mm});
            skPoint(sketch, "E101.8.7", {"position": v(-47.24, 51.6) * mm});
            skPoint(sketch, "E101.8.8", {"position": v(-46.24, 49.87) * mm});
            skArc(sketch, "E101.8.9", {"start": v(-46.38, 52.1) * mm, "mid": v(-46.84, 51.5) * mm, "end": v(-46.74, 50.73) * mm});
            skArc(sketch, "E101.8.10", {"start": v(-46.74, 50.73) * mm, "mid": v(-46.13, 50.27) * mm, "end": v(-45.38, 50.37) * mm});
            skPoint(sketch, "E101.9.0", {"position": v(-37.23, 49.96) * mm});
            skArc(sketch, "E101.9.1", {"start": v(-37.94, 50.66) * mm, "mid": v(-38.64, 50.96) * mm, "end": v(-39.35, 50.66) * mm});
            skPoint(sketch, "E101.9.2", {"position": v(-40.41, 48.19) * mm});
            skPoint(sketch, "E101.9.3", {"position": v(-38.64, 51.37) * mm});
            skLineSegment(sketch, "E101.9.4", {"start": v(-39.35, 50.66) * mm, "end": v(-42.89, 47.13) * mm});
            skLineSegment(sketch, "E101.9.5", {"start": v(-37.94, 49.25) * mm, "end": v(-41.47, 45.71) * mm});
            skArc(sketch, "E101.9.6", {"start": v(-37.94, 49.25) * mm, "mid": v(-37.64, 49.96) * mm, "end": v(-37.94, 50.66) * mm});
            skPoint(sketch, "E101.9.7", {"position": v(-43.6, 46.42) * mm});
            skPoint(sketch, "E101.9.8", {"position": v(-42.18, 45) * mm});
            skArc(sketch, "E101.9.9", {"start": v(-42.89, 47.13) * mm, "mid": v(-43.18, 46.42) * mm, "end": v(-42.89, 45.71) * mm});
            skArc(sketch, "E101.9.10", {"start": v(-42.89, 45.71) * mm, "mid": v(-42.18, 45.42) * mm, "end": v(-41.47, 45.71) * mm});
            skPoint(sketch, "E101.10.0", {"position": v(-33.5, 47.42) * mm});
            skArc(sketch, "E101.10.1", {"start": v(-34.36, 47.92) * mm, "mid": v(-35.12, 48.02) * mm, "end": v(-35.73, 47.56) * mm});
            skPoint(sketch, "E101.10.2", {"position": v(-36.11, 44.89) * mm});
            skPoint(sketch, "E101.10.3", {"position": v(-35.23, 48.42) * mm});
            skLineSegment(sketch, "E101.10.4", {"start": v(-35.73, 47.56) * mm, "end": v(-38.23, 43.22) * mm});
            skLineSegment(sketch, "E101.10.5", {"start": v(-34, 46.56) * mm, "end": v(-36.5, 42.22) * mm});
            skArc(sketch, "E101.10.6", {"start": v(-34, 46.56) * mm, "mid": v(-33.9, 47.31) * mm, "end": v(-34.36, 47.92) * mm});
            skPoint(sketch, "E101.10.7", {"position": v(-38.73, 42.36) * mm});
            skPoint(sketch, "E101.10.8", {"position": v(-37, 41.36) * mm});
            skArc(sketch, "E101.10.9", {"start": v(-38.23, 43.22) * mm, "mid": v(-38.33, 42.47) * mm, "end": v(-37.86, 41.86) * mm});
            skArc(sketch, "E101.10.10", {"start": v(-37.86, 41.86) * mm, "mid": v(-37.1, 41.76) * mm, "end": v(-36.5, 42.22) * mm});
            skPoint(sketch, "E101.11.0", {"position": v(-29.24, 45.94) * mm});
            skArc(sketch, "E101.11.1", {"start": v(-30.2, 46.2) * mm, "mid": v(-30.96, 46.1) * mm, "end": v(-31.43, 45.5) * mm});
            skPoint(sketch, "E101.11.2", {"position": v(-31.11, 42.82) * mm});
            skPoint(sketch, "E101.11.3", {"position": v(-31.17, 46.46) * mm});
            skLineSegment(sketch, "E101.11.4", {"start": v(-31.43, 45.5) * mm, "end": v(-32.72, 40.66) * mm});
            skLineSegment(sketch, "E101.11.5", {"start": v(-29.5, 44.97) * mm, "end": v(-30.8, 40.14) * mm});
            skArc(sketch, "E101.11.6", {"start": v(-29.5, 44.97) * mm, "mid": v(-29.6, 45.73) * mm, "end": v(-30.2, 46.2) * mm});
            skPoint(sketch, "E101.11.7", {"position": v(-32.98, 39.7) * mm});
            skPoint(sketch, "E101.11.8", {"position": v(-31.05, 39.18) * mm});
            skArc(sketch, "E101.11.9", {"start": v(-32.72, 40.66) * mm, "mid": v(-32.62, 39.9) * mm, "end": v(-32.02, 39.44) * mm});
            skArc(sketch, "E101.11.10", {"start": v(-32.02, 39.44) * mm, "mid": v(-31.26, 39.54) * mm, "end": v(-30.8, 40.14) * mm});
            skPoint(sketch, "E101.12.0", {"position": v(-24.74, 45.6) * mm});
            skArc(sketch, "E101.12.1", {"start": v(-25.74, 45.6) * mm, "mid": v(-26.45, 45.32) * mm, "end": v(-26.74, 44.6) * mm});
            skPoint(sketch, "E101.12.2", {"position": v(-25.74, 42.1) * mm});
            skPoint(sketch, "E101.12.3", {"position": v(-26.74, 45.6) * mm});
            skLineSegment(sketch, "E101.12.4", {"start": v(-26.74, 44.6) * mm, "end": v(-26.74, 39.6) * mm});
            skLineSegment(sketch, "E101.12.5", {"start": v(-24.74, 44.6) * mm, "end": v(-24.74, 39.6) * mm});
            skArc(sketch, "E101.12.6", {"start": v(-24.74, 44.6) * mm, "mid": v(-25.03, 45.32) * mm, "end": v(-25.74, 45.6) * mm});
            skPoint(sketch, "E101.12.7", {"position": v(-26.74, 38.6) * mm});
            skPoint(sketch, "E101.12.8", {"position": v(-24.74, 38.6) * mm});
            skArc(sketch, "E101.12.9", {"start": v(-26.74, 39.6) * mm, "mid": v(-26.45, 38.9) * mm, "end": v(-25.74, 38.6) * mm});
            skArc(sketch, "E101.12.10", {"start": v(-25.74, 38.6) * mm, "mid": v(-25.03, 38.9) * mm, "end": v(-24.74, 39.6) * mm});
            skPoint(sketch, "E101.13.0", {"position": v(-20.3, 46.46) * mm});
            skArc(sketch, "E101.13.1", {"start": v(-21.28, 46.2) * mm, "mid": v(-21.88, 45.73) * mm, "end": v(-21.98, 44.97) * mm});
            skPoint(sketch, "E101.13.2", {"position": v(-20.37, 42.82) * mm});
            skPoint(sketch, "E101.13.3", {"position": v(-22.24, 45.94) * mm});
            skLineSegment(sketch, "E101.13.4", {"start": v(-21.98, 44.97) * mm, "end": v(-20.69, 40.14) * mm});
            skLineSegment(sketch, "E101.13.5", {"start": v(-20.05, 45.5) * mm, "end": v(-18.76, 40.66) * mm});
            skArc(sketch, "E101.13.6", {"start": v(-20.05, 45.5) * mm, "mid": v(-20.52, 46.1) * mm, "end": v(-21.28, 46.2) * mm});
            skPoint(sketch, "E101.13.7", {"position": v(-20.43, 39.18) * mm});
            skPoint(sketch, "E101.13.8", {"position": v(-18.5, 39.7) * mm});
            skArc(sketch, "E101.13.9", {"start": v(-20.69, 40.14) * mm, "mid": v(-20.22, 39.54) * mm, "end": v(-19.46, 39.44) * mm});
            skArc(sketch, "E101.13.10", {"start": v(-19.46, 39.44) * mm, "mid": v(-18.86, 39.9) * mm, "end": v(-18.76, 40.66) * mm});
            skPoint(sketch, "E101.14.0", {"position": v(-16.25, 48.42) * mm});
            skArc(sketch, "E101.14.1", {"start": v(-17.11, 47.92) * mm, "mid": v(-17.58, 47.31) * mm, "end": v(-17.48, 46.56) * mm});
            skPoint(sketch, "E101.14.2", {"position": v(-15.36, 44.89) * mm});
            skPoint(sketch, "E101.14.3", {"position": v(-17.98, 47.42) * mm});
            skLineSegment(sketch, "E101.14.4", {"start": v(-17.48, 46.56) * mm, "end": v(-14.98, 42.22) * mm});
            skLineSegment(sketch, "E101.14.5", {"start": v(-15.75, 47.56) * mm, "end": v(-13.25, 43.22) * mm});
            skArc(sketch, "E101.14.6", {"start": v(-15.75, 47.56) * mm, "mid": v(-16.36, 48.02) * mm, "end": v(-17.11, 47.92) * mm});
            skPoint(sketch, "E101.14.7", {"position": v(-14.48, 41.36) * mm});
            skPoint(sketch, "E101.14.8", {"position": v(-12.75, 42.36) * mm});
            skArc(sketch, "E101.14.9", {"start": v(-14.98, 42.22) * mm, "mid": v(-14.37, 41.76) * mm, "end": v(-13.61, 41.86) * mm});
            skArc(sketch, "E101.14.10", {"start": v(-13.61, 41.86) * mm, "mid": v(-13.15, 42.47) * mm, "end": v(-13.25, 43.22) * mm});
            skPoint(sketch, "E101.15.0", {"position": v(-12.84, 51.37) * mm});
            skArc(sketch, "E101.15.1", {"start": v(-13.54, 50.66) * mm, "mid": v(-13.84, 49.96) * mm, "end": v(-13.54, 49.25) * mm});
            skPoint(sketch, "E101.15.2", {"position": v(-11.07, 48.19) * mm});
            skPoint(sketch, "E101.15.3", {"position": v(-14.25, 49.96) * mm});
            skLineSegment(sketch, "E101.15.4", {"start": v(-13.54, 49.25) * mm, "end": v(-10, 45.71) * mm});
            skLineSegment(sketch, "E101.15.5", {"start": v(-12.13, 50.66) * mm, "end": v(-8.6, 47.13) * mm});
            skArc(sketch, "E101.15.6", {"start": v(-12.13, 50.66) * mm, "mid": v(-12.84, 50.96) * mm, "end": v(-13.54, 50.66) * mm});
            skPoint(sketch, "E101.15.7", {"position": v(-9.3, 45) * mm});
            skPoint(sketch, "E101.15.8", {"position": v(-7.89, 46.42) * mm});
            skArc(sketch, "E101.15.9", {"start": v(-10, 45.71) * mm, "mid": v(-9.3, 45.42) * mm, "end": v(-8.6, 45.71) * mm});
            skArc(sketch, "E101.15.10", {"start": v(-8.6, 45.71) * mm, "mid": v(-8.3, 46.42) * mm, "end": v(-8.6, 47.13) * mm});
            skPoint(sketch, "E101.16.0", {"position": v(-10.3, 55.1) * mm});
            skArc(sketch, "E101.16.1", {"start": v(-10.8, 54.24) * mm, "mid": v(-10.9, 53.48) * mm, "end": v(-10.44, 52.87) * mm});
            skPoint(sketch, "E101.16.2", {"position": v(-7.77, 52.49) * mm});
            skPoint(sketch, "E101.16.3", {"position": v(-11.3, 53.37) * mm});
            skLineSegment(sketch, "E101.16.4", {"start": v(-10.44, 52.87) * mm, "end": v(-6.1, 50.37) * mm});
            skLineSegment(sketch, "E101.16.5", {"start": v(-9.44, 54.6) * mm, "end": v(-5.1, 52.1) * mm});
            skArc(sketch, "E101.16.6", {"start": v(-9.44, 54.6) * mm, "mid": v(-10.2, 54.7) * mm, "end": v(-10.8, 54.24) * mm});
            skPoint(sketch, "E101.16.7", {"position": v(-5.24, 49.87) * mm});
            skPoint(sketch, "E101.16.8", {"position": v(-4.24, 51.6) * mm});
            skArc(sketch, "E101.16.9", {"start": v(-6.1, 50.37) * mm, "mid": v(-5.35, 50.27) * mm, "end": v(-4.74, 50.74) * mm});
            skArc(sketch, "E101.16.10", {"start": v(-4.74, 50.74) * mm, "mid": v(-4.64, 51.5) * mm, "end": v(-5.1, 52.1) * mm});
            skPoint(sketch, "E101.17.0", {"position": v(-8.82, 59.36) * mm});
            skArc(sketch, "E101.17.1", {"start": v(-9.08, 58.4) * mm, "mid": v(-8.98, 57.64) * mm, "end": v(-8.37, 57.17) * mm});
            skPoint(sketch, "E101.17.2", {"position": v(-5.7, 57.49) * mm});
            skPoint(sketch, "E101.17.3", {"position": v(-9.34, 57.43) * mm});
            skLineSegment(sketch, "E101.17.4", {"start": v(-8.37, 57.17) * mm, "end": v(-3.54, 55.88) * mm});
            skLineSegment(sketch, "E101.17.5", {"start": v(-7.85, 59.1) * mm, "end": v(-3.02, 57.8) * mm});
            skArc(sketch, "E101.17.6", {"start": v(-7.85, 59.1) * mm, "mid": v(-8.61, 59) * mm, "end": v(-9.08, 58.4) * mm});
            skPoint(sketch, "E101.17.7", {"position": v(-2.58, 55.62) * mm});
            skPoint(sketch, "E101.17.8", {"position": v(-2.06, 57.55) * mm});
            skArc(sketch, "E101.17.9", {"start": v(-3.54, 55.88) * mm, "mid": v(-2.78, 55.98) * mm, "end": v(-2.32, 56.58) * mm});
            skArc(sketch, "E101.17.10", {"start": v(-2.32, 56.58) * mm, "mid": v(-2.42, 57.34) * mm, "end": v(-3.02, 57.8) * mm});
            skPoint(sketch, "E101.18.0", {"position": v(-8.49, 63.86) * mm});
            skArc(sketch, "E101.18.1", {"start": v(-8.49, 62.86) * mm, "mid": v(-8.2, 62.15) * mm, "end": v(-7.49, 61.86) * mm});
            skPoint(sketch, "E101.18.2", {"position": v(-4.99, 62.86) * mm});
            skPoint(sketch, "E101.18.3", {"position": v(-8.49, 61.86) * mm});
            skLineSegment(sketch, "E101.18.4", {"start": v(-7.49, 61.86) * mm, "end": v(-2.49, 61.86) * mm});
            skLineSegment(sketch, "E101.18.5", {"start": v(-7.49, 63.86) * mm, "end": v(-2.49, 63.86) * mm});
            skArc(sketch, "E101.18.6", {"start": v(-7.49, 63.86) * mm, "mid": v(-8.2, 63.57) * mm, "end": v(-8.49, 62.86) * mm});
            skPoint(sketch, "E101.18.7", {"position": v(-1.49, 61.86) * mm});
            skPoint(sketch, "E101.18.8", {"position": v(-1.49, 63.86) * mm});
            skArc(sketch, "E101.18.9", {"start": v(-2.49, 61.86) * mm, "mid": v(-1.78, 62.15) * mm, "end": v(-1.49, 62.86) * mm});
            skArc(sketch, "E101.18.10", {"start": v(-1.49, 62.86) * mm, "mid": v(-1.78, 63.57) * mm, "end": v(-2.49, 63.86) * mm});
            skPoint(sketch, "E101.19.0", {"position": v(-9.34, 68.3) * mm});
            skArc(sketch, "E101.19.1", {"start": v(-9.08, 67.32) * mm, "mid": v(-8.61, 66.72) * mm, "end": v(-7.85, 66.62) * mm});
            skPoint(sketch, "E101.19.2", {"position": v(-5.7, 68.23) * mm});
            skPoint(sketch, "E101.19.3", {"position": v(-8.82, 66.36) * mm});
            skLineSegment(sketch, "E101.19.4", {"start": v(-7.85, 66.62) * mm, "end": v(-3.02, 67.91) * mm});
            skLineSegment(sketch, "E101.19.5", {"start": v(-8.37, 68.55) * mm, "end": v(-3.54, 69.84) * mm});
            skArc(sketch, "E101.19.6", {"start": v(-8.37, 68.55) * mm, "mid": v(-8.98, 68.08) * mm, "end": v(-9.08, 67.32) * mm});
            skPoint(sketch, "E101.19.7", {"position": v(-2.06, 68.17) * mm});
            skPoint(sketch, "E101.19.8", {"position": v(-2.58, 70.1) * mm});
            skArc(sketch, "E101.19.9", {"start": v(-3.02, 67.91) * mm, "mid": v(-2.42, 68.38) * mm, "end": v(-2.32, 69.14) * mm});
            skArc(sketch, "E101.19.10", {"start": v(-2.32, 69.14) * mm, "mid": v(-2.78, 69.74) * mm, "end": v(-3.54, 69.84) * mm});
            skPoint(sketch, "E101.20.0", {"position": v(-11.3, 72.35) * mm});
            skArc(sketch, "E101.20.1", {"start": v(-10.8, 71.49) * mm, "mid": v(-10.2, 71.02) * mm, "end": v(-9.44, 71.12) * mm});
            skPoint(sketch, "E101.20.2", {"position": v(-7.77, 73.24) * mm});
            skPoint(sketch, "E101.20.3", {"position": v(-10.3, 70.62) * mm});
            skLineSegment(sketch, "E101.20.4", {"start": v(-9.44, 71.12) * mm, "end": v(-5.1, 73.62) * mm});
            skLineSegment(sketch, "E101.20.5", {"start": v(-10.44, 72.85) * mm, "end": v(-6.1, 75.35) * mm});
            skArc(sketch, "E101.20.6", {"start": v(-10.44, 72.85) * mm, "mid": v(-10.9, 72.24) * mm, "end": v(-10.8, 71.49) * mm});
            skPoint(sketch, "E101.20.7", {"position": v(-4.24, 74.12) * mm});
            skPoint(sketch, "E101.20.8", {"position": v(-5.24, 75.85) * mm});
            skArc(sketch, "E101.20.9", {"start": v(-5.1, 73.62) * mm, "mid": v(-4.64, 74.23) * mm, "end": v(-4.74, 74.99) * mm});
            skArc(sketch, "E101.20.10", {"start": v(-4.74, 74.99) * mm, "mid": v(-5.35, 75.45) * mm, "end": v(-6.1, 75.35) * mm});
            skPoint(sketch, "E101.21.0", {"position": v(-14.25, 75.76) * mm});
            skArc(sketch, "E101.21.1", {"start": v(-13.54, 75.06) * mm, "mid": v(-12.84, 74.76) * mm, "end": v(-12.13, 75.06) * mm});
            skPoint(sketch, "E101.21.2", {"position": v(-11.07, 77.53) * mm});
            skPoint(sketch, "E101.21.3", {"position": v(-12.84, 74.35) * mm});
            skLineSegment(sketch, "E101.21.4", {"start": v(-12.13, 75.06) * mm, "end": v(-8.6, 78.6) * mm});
            skLineSegment(sketch, "E101.21.5", {"start": v(-13.54, 76.47) * mm, "end": v(-10, 80) * mm});
            skArc(sketch, "E101.21.6", {"start": v(-13.54, 76.47) * mm, "mid": v(-13.84, 75.76) * mm, "end": v(-13.54, 75.06) * mm});
            skPoint(sketch, "E101.21.7", {"position": v(-7.89, 79.3) * mm});
            skPoint(sketch, "E101.21.8", {"position": v(-9.3, 80.71) * mm});
            skArc(sketch, "E101.21.9", {"start": v(-8.6, 78.6) * mm, "mid": v(-8.3, 79.3) * mm, "end": v(-8.6, 80) * mm});
            skArc(sketch, "E101.21.10", {"start": v(-8.6, 80) * mm, "mid": v(-9.3, 80.3) * mm, "end": v(-10, 80) * mm});
            skPoint(sketch, "E101.22.0", {"position": v(-17.98, 78.3) * mm});
            skArc(sketch, "E101.22.1", {"start": v(-17.12, 77.8) * mm, "mid": v(-16.36, 77.7) * mm, "end": v(-15.75, 78.16) * mm});
            skPoint(sketch, "E101.22.2", {"position": v(-15.36, 80.83) * mm});
            skPoint(sketch, "E101.22.3", {"position": v(-16.25, 77.3) * mm});
            skLineSegment(sketch, "E101.22.4", {"start": v(-15.75, 78.16) * mm, "end": v(-13.25, 82.5) * mm});
            skLineSegment(sketch, "E101.22.5", {"start": v(-17.48, 79.16) * mm, "end": v(-14.98, 83.5) * mm});
            skArc(sketch, "E101.22.6", {"start": v(-17.48, 79.16) * mm, "mid": v(-17.58, 78.4) * mm, "end": v(-17.12, 77.8) * mm});
            skPoint(sketch, "E101.22.7", {"position": v(-12.75, 83.36) * mm});
            skPoint(sketch, "E101.22.8", {"position": v(-14.48, 84.36) * mm});
            skArc(sketch, "E101.22.9", {"start": v(-13.25, 82.5) * mm, "mid": v(-13.15, 83.25) * mm, "end": v(-13.62, 83.86) * mm});
            skArc(sketch, "E101.22.10", {"start": v(-13.61, 83.86) * mm, "mid": v(-14.37, 83.96) * mm, "end": v(-14.98, 83.5) * mm});
            skPoint(sketch, "E101.23.0", {"position": v(-22.24, 79.78) * mm});
            skArc(sketch, "E101.23.1", {"start": v(-21.28, 79.52) * mm, "mid": v(-20.52, 79.62) * mm, "end": v(-20.05, 80.23) * mm});
            skPoint(sketch, "E101.23.2", {"position": v(-20.37, 82.9) * mm});
            skPoint(sketch, "E101.23.3", {"position": v(-20.3, 79.26) * mm});
            skLineSegment(sketch, "E101.23.4", {"start": v(-20.05, 80.23) * mm, "end": v(-18.76, 85.06) * mm});
            skLineSegment(sketch, "E101.23.5", {"start": v(-21.98, 80.75) * mm, "end": v(-20.69, 85.58) * mm});
            skArc(sketch, "E101.23.6", {"start": v(-21.98, 80.75) * mm, "mid": v(-21.88, 79.99) * mm, "end": v(-21.28, 79.52) * mm});
            skPoint(sketch, "E101.23.7", {"position": v(-18.5, 86.02) * mm});
            skPoint(sketch, "E101.23.8", {"position": v(-20.43, 86.54) * mm});
            skArc(sketch, "E101.23.9", {"start": v(-18.76, 85.06) * mm, "mid": v(-18.86, 85.82) * mm, "end": v(-19.46, 86.28) * mm});
            skArc(sketch, "E101.23.10", {"start": v(-19.46, 86.28) * mm, "mid": v(-20.22, 86.18) * mm, "end": v(-20.69, 85.58) * mm});
            skLineSegment(sketch, "E102.1.0", {"start": v(18.76, 99.8) * mm, "end": v(17.47, 104.64) * mm});
            skPoint(sketch, "E102.1.1", {"position": v(17.15, 101.96) * mm});
            skLineSegment(sketch, "E102.1.2", {"start": v(16.83, 99.29) * mm, "end": v(15.54, 104.12) * mm});
            skPoint(sketch, "E102.1.3", {"position": v(17.09, 98.32) * mm});
            skPoint(sketch, "E102.1.4", {"position": v(19.02, 98.84) * mm});
            skArc(sketch, "E102.1.5", {"start": v(18.06, 98.58) * mm, "mid": v(18.66, 99.05) * mm, "end": v(18.76, 99.8) * mm});
            skArc(sketch, "E102.1.6", {"start": v(16.83, 99.29) * mm, "mid": v(17.3, 98.68) * mm, "end": v(18.06, 98.58) * mm});
            skArc(sketch, "E102.1.7", {"start": v(17.47, 104.64) * mm, "mid": v(17, 105.24) * mm, "end": v(16.24, 105.34) * mm});
            skArc(sketch, "E102.1.8", {"start": v(16.24, 105.34) * mm, "mid": v(15.64, 104.88) * mm, "end": v(15.54, 104.12) * mm});
            skPoint(sketch, "E102.1.9", {"position": v(15.28, 105.08) * mm});
            skPoint(sketch, "E102.1.10", {"position": v(17.2, 105.6) * mm});
            skLineSegment(sketch, "E102.2.0", {"start": v(14.26, 98.22) * mm, "end": v(11.76, 102.56) * mm});
            skPoint(sketch, "E102.2.1", {"position": v(12.14, 99.9) * mm});
            skLineSegment(sketch, "E102.2.2", {"start": v(12.53, 97.22) * mm, "end": v(10.03, 101.56) * mm});
            skPoint(sketch, "E102.2.3", {"position": v(13.03, 96.36) * mm});
            skPoint(sketch, "E102.2.4", {"position": v(14.76, 97.36) * mm});
            skArc(sketch, "E102.2.5", {"start": v(13.9, 96.86) * mm, "mid": v(14.36, 97.47) * mm, "end": v(14.26, 98.22) * mm});
            skArc(sketch, "E102.2.6", {"start": v(12.53, 97.22) * mm, "mid": v(13.14, 96.76) * mm, "end": v(13.9, 96.86) * mm});
            skArc(sketch, "E102.2.7", {"start": v(11.76, 102.56) * mm, "mid": v(11.15, 103.02) * mm, "end": v(10.4, 102.92) * mm});
            skArc(sketch, "E102.2.8", {"start": v(10.4, 102.92) * mm, "mid": v(9.93, 102.31) * mm, "end": v(10.03, 101.56) * mm});
            skPoint(sketch, "E102.2.9", {"position": v(9.53, 102.42) * mm});
            skPoint(sketch, "E102.2.10", {"position": v(11.26, 103.42) * mm});
            skLineSegment(sketch, "E102.3.0", {"start": v(10.32, 95.53) * mm, "end": v(6.79, 99.07) * mm});
            skPoint(sketch, "E102.3.1", {"position": v(7.85, 96.6) * mm});
            skLineSegment(sketch, "E102.3.2", {"start": v(8.9, 94.12) * mm, "end": v(5.37, 97.65) * mm});
            skPoint(sketch, "E102.3.3", {"position": v(9.62, 93.41) * mm});
            skPoint(sketch, "E102.3.4", {"position": v(11.03, 94.82) * mm});
            skArc(sketch, "E102.3.5", {"start": v(10.32, 94.12) * mm, "mid": v(10.62, 94.82) * mm, "end": v(10.32, 95.53) * mm});
            skArc(sketch, "E102.3.6", {"start": v(8.9, 94.12) * mm, "mid": v(9.62, 93.82) * mm, "end": v(10.32, 94.12) * mm});
            skArc(sketch, "E102.3.7", {"start": v(6.79, 99.07) * mm, "mid": v(6.08, 99.36) * mm, "end": v(5.37, 99.07) * mm});
            skArc(sketch, "E102.3.8", {"start": v(5.37, 99.07) * mm, "mid": v(5.08, 98.36) * mm, "end": v(5.37, 97.65) * mm});
            skPoint(sketch, "E102.3.9", {"position": v(4.67, 98.36) * mm});
            skPoint(sketch, "E102.3.10", {"position": v(6.08, 99.77) * mm});
            skLineSegment(sketch, "E102.4.0", {"start": v(7.22, 91.91) * mm, "end": v(2.88, 94.41) * mm});
            skPoint(sketch, "E102.4.1", {"position": v(4.55, 92.3) * mm});
            skLineSegment(sketch, "E102.4.2", {"start": v(6.22, 90.18) * mm, "end": v(1.88, 92.68) * mm});
            skPoint(sketch, "E102.4.3", {"position": v(7.08, 89.68) * mm});
            skPoint(sketch, "E102.4.4", {"position": v(8.08, 91.41) * mm});
            skArc(sketch, "E102.4.5", {"start": v(7.58, 90.54) * mm, "mid": v(7.68, 91.3) * mm, "end": v(7.22, 91.91) * mm});
            skArc(sketch, "E102.4.6", {"start": v(6.22, 90.18) * mm, "mid": v(6.97, 90.08) * mm, "end": v(7.58, 90.54) * mm});
            skArc(sketch, "E102.4.7", {"start": v(2.88, 94.41) * mm, "mid": v(2.13, 94.51) * mm, "end": v(1.52, 94.05) * mm});
            skArc(sketch, "E102.4.8", {"start": v(1.52, 94.04) * mm, "mid": v(1.42, 93.29) * mm, "end": v(1.88, 92.68) * mm});
            skPoint(sketch, "E102.4.9", {"position": v(1.02, 93.18) * mm});
            skPoint(sketch, "E102.4.10", {"position": v(2.02, 94.91) * mm});
            skLineSegment(sketch, "E102.5.0", {"start": v(5.15, 87.6) * mm, "end": v(0.32, 88.9) * mm});
            skPoint(sketch, "E102.5.1", {"position": v(2.48, 87.3) * mm});
            skLineSegment(sketch, "E102.5.2", {"start": v(4.63, 85.68) * mm, "end": v(-0.2, 86.97) * mm});
            skPoint(sketch, "E102.5.3", {"position": v(5.6, 85.42) * mm});
            skPoint(sketch, "E102.5.4", {"position": v(6.12, 87.35) * mm});
            skArc(sketch, "E102.5.5", {"start": v(5.86, 86.38) * mm, "mid": v(5.76, 87.14) * mm, "end": v(5.15, 87.6) * mm});
            skArc(sketch, "E102.5.6", {"start": v(4.63, 85.68) * mm, "mid": v(5.4, 85.78) * mm, "end": v(5.86, 86.38) * mm});
            skArc(sketch, "E102.5.7", {"start": v(0.32, 88.9) * mm, "mid": v(-0.44, 88.8) * mm, "end": v(-0.9, 88.2) * mm});
            skArc(sketch, "E102.5.8", {"start": v(-0.9, 88.2) * mm, "mid": v(-0.8, 87.44) * mm, "end": v(-0.2, 86.97) * mm});
            skPoint(sketch, "E102.5.9", {"position": v(-1.16, 87.23) * mm});
            skPoint(sketch, "E102.5.10", {"position": v(-0.64, 89.16) * mm});
            skLineSegment(sketch, "E102.6.0", {"start": v(4.27, 82.92) * mm, "end": v(-0.73, 82.92) * mm});
            skPoint(sketch, "E102.6.1", {"position": v(1.77, 81.92) * mm});
            skLineSegment(sketch, "E102.6.2", {"start": v(4.27, 80.92) * mm, "end": v(-0.73, 80.92) * mm});
            skPoint(sketch, "E102.6.3", {"position": v(5.27, 80.92) * mm});
            skPoint(sketch, "E102.6.4", {"position": v(5.27, 82.92) * mm});
            skArc(sketch, "E102.6.5", {"start": v(5.27, 81.92) * mm, "mid": v(4.98, 82.63) * mm, "end": v(4.27, 82.92) * mm});
            skArc(sketch, "E102.6.6", {"start": v(4.27, 80.92) * mm, "mid": v(4.98, 81.21) * mm, "end": v(5.27, 81.92) * mm});
            skArc(sketch, "E102.6.7", {"start": v(-0.73, 82.92) * mm, "mid": v(-1.44, 82.63) * mm, "end": v(-1.73, 81.92) * mm});
            skArc(sketch, "E102.6.8", {"start": v(-1.73, 81.92) * mm, "mid": v(-1.44, 81.21) * mm, "end": v(-0.73, 80.92) * mm});
            skPoint(sketch, "E102.6.9", {"position": v(-1.73, 80.92) * mm});
            skPoint(sketch, "E102.6.10", {"position": v(-1.73, 82.92) * mm});
            skLineSegment(sketch, "E102.7.0", {"start": v(4.63, 78.16) * mm, "end": v(-0.2, 76.87) * mm});
            skPoint(sketch, "E102.7.1", {"position": v(2.48, 76.55) * mm});
            skLineSegment(sketch, "E102.7.2", {"start": v(5.15, 76.23) * mm, "end": v(0.32, 74.94) * mm});
            skPoint(sketch, "E102.7.3", {"position": v(6.12, 76.49) * mm});
            skPoint(sketch, "E102.7.4", {"position": v(5.6, 78.42) * mm});
            skArc(sketch, "E102.7.5", {"start": v(5.86, 77.46) * mm, "mid": v(5.4, 78.06) * mm, "end": v(4.63, 78.16) * mm});
            skArc(sketch, "E102.7.6", {"start": v(5.15, 76.23) * mm, "mid": v(5.76, 76.7) * mm, "end": v(5.86, 77.46) * mm});
            skArc(sketch, "E102.7.7", {"start": v(-0.2, 76.87) * mm, "mid": v(-0.8, 76.4) * mm, "end": v(-0.9, 75.64) * mm});
            skArc(sketch, "E102.7.8", {"start": v(-0.9, 75.64) * mm, "mid": v(-0.44, 75.04) * mm, "end": v(0.32, 74.94) * mm});
            skPoint(sketch, "E102.7.9", {"position": v(-0.64, 74.68) * mm});
            skPoint(sketch, "E102.7.10", {"position": v(-1.16, 76.6) * mm});
            skLineSegment(sketch, "E102.8.0", {"start": v(6.22, 73.66) * mm, "end": v(1.88, 71.16) * mm});
            skPoint(sketch, "E102.8.1", {"position": v(4.55, 71.54) * mm});
            skLineSegment(sketch, "E102.8.2", {"start": v(7.22, 71.93) * mm, "end": v(2.88, 69.43) * mm});
            skPoint(sketch, "E102.8.3", {"position": v(8.08, 72.43) * mm});
            skPoint(sketch, "E102.8.4", {"position": v(7.08, 74.16) * mm});
            skArc(sketch, "E102.8.5", {"start": v(7.58, 73.3) * mm, "mid": v(6.97, 73.76) * mm, "end": v(6.22, 73.66) * mm});
            skArc(sketch, "E102.8.6", {"start": v(7.22, 71.93) * mm, "mid": v(7.68, 72.54) * mm, "end": v(7.58, 73.3) * mm});
            skArc(sketch, "E102.8.7", {"start": v(1.88, 71.16) * mm, "mid": v(1.42, 70.55) * mm, "end": v(1.52, 69.8) * mm});
            skArc(sketch, "E102.8.8", {"start": v(1.52, 69.8) * mm, "mid": v(2.13, 69.33) * mm, "end": v(2.88, 69.43) * mm});
            skPoint(sketch, "E102.8.9", {"position": v(2.02, 68.93) * mm});
            skPoint(sketch, "E102.8.10", {"position": v(1.02, 70.66) * mm});
            skLineSegment(sketch, "E102.9.0", {"start": v(8.9, 69.72) * mm, "end": v(5.37, 66.19) * mm});
            skPoint(sketch, "E102.9.1", {"position": v(7.85, 67.25) * mm});
            skLineSegment(sketch, "E102.9.2", {"start": v(10.32, 68.3) * mm, "end": v(6.79, 64.77) * mm});
            skPoint(sketch, "E102.9.3", {"position": v(11.03, 69.02) * mm});
            skPoint(sketch, "E102.9.4", {"position": v(9.62, 70.43) * mm});
            skArc(sketch, "E102.9.5", {"start": v(10.32, 69.72) * mm, "mid": v(9.62, 70.02) * mm, "end": v(8.9, 69.72) * mm});
            skArc(sketch, "E102.9.6", {"start": v(10.32, 68.3) * mm, "mid": v(10.62, 69.02) * mm, "end": v(10.32, 69.72) * mm});
            skArc(sketch, "E102.9.7", {"start": v(5.37, 66.19) * mm, "mid": v(5.08, 65.48) * mm, "end": v(5.37, 64.77) * mm});
            skArc(sketch, "E102.9.8", {"start": v(5.37, 64.77) * mm, "mid": v(6.08, 64.48) * mm, "end": v(6.79, 64.77) * mm});
            skPoint(sketch, "E102.9.9", {"position": v(6.08, 64.07) * mm});
            skPoint(sketch, "E102.9.10", {"position": v(4.67, 65.48) * mm});
            skLineSegment(sketch, "E102.10.0", {"start": v(12.53, 66.62) * mm, "end": v(10.03, 62.28) * mm});
            skPoint(sketch, "E102.10.1", {"position": v(12.14, 63.95) * mm});
            skLineSegment(sketch, "E102.10.2", {"start": v(14.26, 65.62) * mm, "end": v(11.76, 61.28) * mm});
            skPoint(sketch, "E102.10.3", {"position": v(14.76, 66.48) * mm});
            skPoint(sketch, "E102.10.4", {"position": v(13.03, 67.48) * mm});
            skArc(sketch, "E102.10.5", {"start": v(13.9, 66.98) * mm, "mid": v(13.14, 67.08) * mm, "end": v(12.53, 66.62) * mm});
            skArc(sketch, "E102.10.6", {"start": v(14.26, 65.62) * mm, "mid": v(14.36, 66.37) * mm, "end": v(13.9, 66.98) * mm});
            skArc(sketch, "E102.10.7", {"start": v(10.03, 62.28) * mm, "mid": v(9.93, 61.53) * mm, "end": v(10.4, 60.92) * mm});
            skArc(sketch, "E102.10.8", {"start": v(10.4, 60.92) * mm, "mid": v(11.15, 60.82) * mm, "end": v(11.76, 61.28) * mm});
            skPoint(sketch, "E102.10.9", {"position": v(11.26, 60.42) * mm});
            skPoint(sketch, "E102.10.10", {"position": v(9.53, 61.42) * mm});
            skLineSegment(sketch, "E102.11.0", {"start": v(16.83, 64.55) * mm, "end": v(15.54, 59.72) * mm});
            skPoint(sketch, "E102.11.1", {"position": v(17.15, 61.88) * mm});
            skLineSegment(sketch, "E102.11.2", {"start": v(18.76, 64.03) * mm, "end": v(17.47, 59.2) * mm});
            skPoint(sketch, "E102.11.3", {"position": v(19.02, 65) * mm});
            skPoint(sketch, "E102.11.4", {"position": v(17.09, 65.52) * mm});
            skArc(sketch, "E102.11.5", {"start": v(18.06, 65.26) * mm, "mid": v(17.3, 65.16) * mm, "end": v(16.83, 64.55) * mm});
            skArc(sketch, "E102.11.6", {"start": v(18.76, 64.03) * mm, "mid": v(18.66, 64.8) * mm, "end": v(18.06, 65.26) * mm});
            skArc(sketch, "E102.11.7", {"start": v(15.54, 59.72) * mm, "mid": v(15.64, 58.96) * mm, "end": v(16.24, 58.5) * mm});
            skArc(sketch, "E102.11.8", {"start": v(16.24, 58.5) * mm, "mid": v(17, 58.6) * mm, "end": v(17.47, 59.2) * mm});
            skPoint(sketch, "E102.11.9", {"position": v(17.2, 58.24) * mm});
            skPoint(sketch, "E102.11.10", {"position": v(15.28, 58.76) * mm});
            skLineSegment(sketch, "E102.12.0", {"start": v(21.52, 63.67) * mm, "end": v(21.52, 58.67) * mm});
            skPoint(sketch, "E102.12.1", {"position": v(22.52, 61.17) * mm});
            skLineSegment(sketch, "E102.12.2", {"start": v(23.52, 63.67) * mm, "end": v(23.52, 58.67) * mm});
            skPoint(sketch, "E102.12.3", {"position": v(23.52, 64.67) * mm});
            skPoint(sketch, "E102.12.4", {"position": v(21.52, 64.67) * mm});
            skArc(sketch, "E102.12.5", {"start": v(22.52, 64.67) * mm, "mid": v(21.81, 64.38) * mm, "end": v(21.52, 63.67) * mm});
            skArc(sketch, "E102.12.6", {"start": v(23.52, 63.67) * mm, "mid": v(23.23, 64.38) * mm, "end": v(22.52, 64.67) * mm});
            skArc(sketch, "E102.12.7", {"start": v(21.52, 58.67) * mm, "mid": v(21.81, 57.96) * mm, "end": v(22.52, 57.67) * mm});
            skArc(sketch, "E102.12.8", {"start": v(22.52, 57.67) * mm, "mid": v(23.23, 57.96) * mm, "end": v(23.52, 58.67) * mm});
            skPoint(sketch, "E102.12.9", {"position": v(23.52, 57.67) * mm});
            skPoint(sketch, "E102.12.10", {"position": v(21.52, 57.67) * mm});
            skLineSegment(sketch, "E102.13.0", {"start": v(26.28, 64.03) * mm, "end": v(27.57, 59.2) * mm});
            skPoint(sketch, "E102.13.1", {"position": v(27.9, 61.88) * mm});
            skLineSegment(sketch, "E102.13.2", {"start": v(28.2, 64.55) * mm, "end": v(29.5, 59.72) * mm});
            skPoint(sketch, "E102.13.3", {"position": v(27.95, 65.52) * mm});
            skPoint(sketch, "E102.13.4", {"position": v(26.02, 65) * mm});
            skArc(sketch, "E102.13.5", {"start": v(26.98, 65.26) * mm, "mid": v(26.38, 64.8) * mm, "end": v(26.28, 64.03) * mm});
            skArc(sketch, "E102.13.6", {"start": v(28.2, 64.55) * mm, "mid": v(27.74, 65.16) * mm, "end": v(26.98, 65.26) * mm});
            skArc(sketch, "E102.13.7", {"start": v(27.57, 59.2) * mm, "mid": v(28.04, 58.6) * mm, "end": v(28.8, 58.5) * mm});
            skArc(sketch, "E102.13.8", {"start": v(28.8, 58.5) * mm, "mid": v(29.4, 58.96) * mm, "end": v(29.5, 59.72) * mm});
            skPoint(sketch, "E102.13.9", {"position": v(29.76, 58.76) * mm});
            skPoint(sketch, "E102.13.10", {"position": v(27.83, 58.24) * mm});
            skLineSegment(sketch, "E102.14.0", {"start": v(30.78, 65.62) * mm, "end": v(33.28, 61.28) * mm});
            skPoint(sketch, "E102.14.1", {"position": v(32.9, 63.95) * mm});
            skLineSegment(sketch, "E102.14.2", {"start": v(32.51, 66.62) * mm, "end": v(35.01, 62.28) * mm});
            skPoint(sketch, "E102.14.3", {"position": v(32.01, 67.48) * mm});
            skPoint(sketch, "E102.14.4", {"position": v(30.28, 66.48) * mm});
            skArc(sketch, "E102.14.5", {"start": v(31.14, 66.98) * mm, "mid": v(30.68, 66.37) * mm, "end": v(30.78, 65.62) * mm});
            skArc(sketch, "E102.14.6", {"start": v(32.51, 66.62) * mm, "mid": v(31.9, 67.08) * mm, "end": v(31.14, 66.98) * mm});
            skArc(sketch, "E102.14.7", {"start": v(33.28, 61.28) * mm, "mid": v(33.89, 60.82) * mm, "end": v(34.64, 60.92) * mm});
            skArc(sketch, "E102.14.8", {"start": v(34.64, 60.92) * mm, "mid": v(35.11, 61.53) * mm, "end": v(35.01, 62.28) * mm});
            skPoint(sketch, "E102.14.9", {"position": v(35.51, 61.42) * mm});
            skPoint(sketch, "E102.14.10", {"position": v(33.78, 60.42) * mm});
            skLineSegment(sketch, "E102.15.0", {"start": v(34.72, 68.3) * mm, "end": v(38.25, 64.77) * mm});
            skPoint(sketch, "E102.15.1", {"position": v(37.2, 67.25) * mm});
            skLineSegment(sketch, "E102.15.2", {"start": v(36.13, 69.72) * mm, "end": v(39.67, 66.19) * mm});
            skPoint(sketch, "E102.15.3", {"position": v(35.42, 70.43) * mm});
            skPoint(sketch, "E102.15.4", {"position": v(34.01, 69.02) * mm});
            skArc(sketch, "E102.15.5", {"start": v(34.72, 69.72) * mm, "mid": v(34.42, 69.02) * mm, "end": v(34.72, 68.3) * mm});
            skArc(sketch, "E102.15.6", {"start": v(36.13, 69.72) * mm, "mid": v(35.42, 70.02) * mm, "end": v(34.72, 69.72) * mm});
            skArc(sketch, "E102.15.7", {"start": v(38.25, 64.77) * mm, "mid": v(38.96, 64.48) * mm, "end": v(39.67, 64.77) * mm});
            skArc(sketch, "E102.15.8", {"start": v(39.67, 64.77) * mm, "mid": v(39.96, 65.48) * mm, "end": v(39.67, 66.19) * mm});
            skPoint(sketch, "E102.15.9", {"position": v(40.37, 65.48) * mm});
            skPoint(sketch, "E102.15.10", {"position": v(38.96, 64.07) * mm});
            skLineSegment(sketch, "E102.16.0", {"start": v(37.82, 71.93) * mm, "end": v(42.16, 69.43) * mm});
            skPoint(sketch, "E102.16.1", {"position": v(40.5, 71.55) * mm});
            skLineSegment(sketch, "E102.16.2", {"start": v(38.82, 73.66) * mm, "end": v(43.16, 71.16) * mm});
            skPoint(sketch, "E102.16.3", {"position": v(37.96, 74.16) * mm});
            skPoint(sketch, "E102.16.4", {"position": v(36.96, 72.43) * mm});
            skArc(sketch, "E102.16.5", {"start": v(37.46, 73.3) * mm, "mid": v(37.36, 72.54) * mm, "end": v(37.82, 71.93) * mm});
            skArc(sketch, "E102.16.6", {"start": v(38.82, 73.66) * mm, "mid": v(38.07, 73.76) * mm, "end": v(37.46, 73.3) * mm});
            skArc(sketch, "E102.16.7", {"start": v(42.16, 69.43) * mm, "mid": v(42.91, 69.33) * mm, "end": v(43.52, 69.8) * mm});
            skArc(sketch, "E102.16.8", {"start": v(43.52, 69.8) * mm, "mid": v(43.62, 70.55) * mm, "end": v(43.16, 71.16) * mm});
            skPoint(sketch, "E102.16.9", {"position": v(44.02, 70.66) * mm});
            skPoint(sketch, "E102.16.10", {"position": v(43.02, 68.93) * mm});
            skLineSegment(sketch, "E102.17.0", {"start": v(39.89, 76.23) * mm, "end": v(44.72, 74.94) * mm});
            skPoint(sketch, "E102.17.1", {"position": v(42.56, 76.55) * mm});
            skLineSegment(sketch, "E102.17.2", {"start": v(40.4, 78.16) * mm, "end": v(45.24, 76.87) * mm});
            skPoint(sketch, "E102.17.3", {"position": v(39.44, 78.42) * mm});
            skPoint(sketch, "E102.17.4", {"position": v(38.92, 76.49) * mm});
            skArc(sketch, "E102.17.5", {"start": v(39.18, 77.46) * mm, "mid": v(39.28, 76.7) * mm, "end": v(39.89, 76.23) * mm});
            skArc(sketch, "E102.17.6", {"start": v(40.4, 78.16) * mm, "mid": v(39.65, 78.06) * mm, "end": v(39.18, 77.46) * mm});
            skArc(sketch, "E102.17.7", {"start": v(44.72, 74.94) * mm, "mid": v(45.48, 75.04) * mm, "end": v(45.94, 75.64) * mm});
            skArc(sketch, "E102.17.8", {"start": v(45.94, 75.64) * mm, "mid": v(45.84, 76.4) * mm, "end": v(45.24, 76.87) * mm});
            skPoint(sketch, "E102.17.9", {"position": v(46.2, 76.6) * mm});
            skPoint(sketch, "E102.17.10", {"position": v(45.68, 74.68) * mm});
            skLineSegment(sketch, "E102.18.0", {"start": v(40.77, 80.92) * mm, "end": v(45.77, 80.92) * mm});
            skPoint(sketch, "E102.18.1", {"position": v(43.27, 81.92) * mm});
            skLineSegment(sketch, "E102.18.2", {"start": v(40.77, 82.92) * mm, "end": v(45.77, 82.92) * mm});
            skPoint(sketch, "E102.18.3", {"position": v(39.77, 82.92) * mm});
            skPoint(sketch, "E102.18.4", {"position": v(39.77, 80.92) * mm});
            skArc(sketch, "E102.18.5", {"start": v(39.77, 81.92) * mm, "mid": v(40.06, 81.21) * mm, "end": v(40.77, 80.92) * mm});
            skArc(sketch, "E102.18.6", {"start": v(40.77, 82.92) * mm, "mid": v(40.06, 82.63) * mm, "end": v(39.77, 81.92) * mm});
            skArc(sketch, "E102.18.7", {"start": v(45.77, 80.92) * mm, "mid": v(46.48, 81.21) * mm, "end": v(46.77, 81.92) * mm});
            skArc(sketch, "E102.18.8", {"start": v(46.77, 81.92) * mm, "mid": v(46.48, 82.63) * mm, "end": v(45.77, 82.92) * mm});
            skPoint(sketch, "E102.18.9", {"position": v(46.77, 82.92) * mm});
            skPoint(sketch, "E102.18.10", {"position": v(46.77, 80.92) * mm});
            skLineSegment(sketch, "E102.19.0", {"start": v(40.4, 85.68) * mm, "end": v(45.24, 86.97) * mm});
            skPoint(sketch, "E102.19.1", {"position": v(42.56, 87.3) * mm});
            skLineSegment(sketch, "E102.19.2", {"start": v(39.89, 87.6) * mm, "end": v(44.72, 88.9) * mm});
            skPoint(sketch, "E102.19.3", {"position": v(38.92, 87.35) * mm});
            skPoint(sketch, "E102.19.4", {"position": v(39.44, 85.42) * mm});
            skArc(sketch, "E102.19.5", {"start": v(39.18, 86.38) * mm, "mid": v(39.65, 85.78) * mm, "end": v(40.4, 85.68) * mm});
            skArc(sketch, "E102.19.6", {"start": v(39.89, 87.6) * mm, "mid": v(39.28, 87.14) * mm, "end": v(39.18, 86.38) * mm});
            skArc(sketch, "E102.19.7", {"start": v(45.24, 86.97) * mm, "mid": v(45.84, 87.44) * mm, "end": v(45.94, 88.2) * mm});
            skArc(sketch, "E102.19.8", {"start": v(45.94, 88.2) * mm, "mid": v(45.48, 88.8) * mm, "end": v(44.72, 88.9) * mm});
            skPoint(sketch, "E102.19.9", {"position": v(45.68, 89.16) * mm});
            skPoint(sketch, "E102.19.10", {"position": v(46.2, 87.23) * mm});
            skLineSegment(sketch, "E102.20.0", {"start": v(38.82, 90.18) * mm, "end": v(43.16, 92.68) * mm});
            skPoint(sketch, "E102.20.1", {"position": v(40.5, 92.3) * mm});
            skLineSegment(sketch, "E102.20.2", {"start": v(37.82, 91.91) * mm, "end": v(42.16, 94.41) * mm});
            skPoint(sketch, "E102.20.3", {"position": v(36.96, 91.41) * mm});
            skPoint(sketch, "E102.20.4", {"position": v(37.96, 89.68) * mm});
            skArc(sketch, "E102.20.5", {"start": v(37.46, 90.55) * mm, "mid": v(38.07, 90.08) * mm, "end": v(38.82, 90.18) * mm});
            skArc(sketch, "E102.20.6", {"start": v(37.82, 91.91) * mm, "mid": v(37.36, 91.3) * mm, "end": v(37.46, 90.55) * mm});
            skArc(sketch, "E102.20.7", {"start": v(43.16, 92.68) * mm, "mid": v(43.62, 93.29) * mm, "end": v(43.52, 94.05) * mm});
            skArc(sketch, "E102.20.8", {"start": v(43.52, 94.05) * mm, "mid": v(42.91, 94.51) * mm, "end": v(42.16, 94.41) * mm});
            skPoint(sketch, "E102.20.9", {"position": v(43.02, 94.91) * mm});
            skPoint(sketch, "E102.20.10", {"position": v(44.02, 93.18) * mm});
            skLineSegment(sketch, "E102.21.0", {"start": v(36.13, 94.12) * mm, "end": v(39.67, 97.65) * mm});
            skPoint(sketch, "E102.21.1", {"position": v(37.2, 96.6) * mm});
            skLineSegment(sketch, "E102.21.2", {"start": v(34.72, 95.53) * mm, "end": v(38.25, 99.07) * mm});
            skPoint(sketch, "E102.21.3", {"position": v(34.01, 94.82) * mm});
            skPoint(sketch, "E102.21.4", {"position": v(35.42, 93.41) * mm});
            skArc(sketch, "E102.21.5", {"start": v(34.72, 94.12) * mm, "mid": v(35.42, 93.82) * mm, "end": v(36.13, 94.12) * mm});
            skArc(sketch, "E102.21.6", {"start": v(34.72, 95.53) * mm, "mid": v(34.42, 94.82) * mm, "end": v(34.72, 94.12) * mm});
            skArc(sketch, "E102.21.7", {"start": v(39.67, 97.65) * mm, "mid": v(39.96, 98.36) * mm, "end": v(39.67, 99.07) * mm});
            skArc(sketch, "E102.21.8", {"start": v(39.67, 99.07) * mm, "mid": v(38.96, 99.36) * mm, "end": v(38.25, 99.07) * mm});
            skPoint(sketch, "E102.21.9", {"position": v(38.96, 99.77) * mm});
            skPoint(sketch, "E102.21.10", {"position": v(40.37, 98.36) * mm});
            skLineSegment(sketch, "E102.22.0", {"start": v(32.51, 97.22) * mm, "end": v(35.01, 101.56) * mm});
            skPoint(sketch, "E102.22.1", {"position": v(32.9, 99.9) * mm});
            skLineSegment(sketch, "E102.22.2", {"start": v(30.78, 98.22) * mm, "end": v(33.28, 102.56) * mm});
            skPoint(sketch, "E102.22.3", {"position": v(30.28, 97.36) * mm});
            skPoint(sketch, "E102.22.4", {"position": v(32.01, 96.36) * mm});
            skArc(sketch, "E102.22.5", {"start": v(31.14, 96.86) * mm, "mid": v(31.9, 96.76) * mm, "end": v(32.51, 97.22) * mm});
            skArc(sketch, "E102.22.6", {"start": v(30.78, 98.22) * mm, "mid": v(30.68, 97.47) * mm, "end": v(31.14, 96.86) * mm});
            skArc(sketch, "E102.22.7", {"start": v(35.01, 101.56) * mm, "mid": v(35.11, 102.31) * mm, "end": v(34.64, 102.92) * mm});
            skArc(sketch, "E102.22.8", {"start": v(34.64, 102.92) * mm, "mid": v(33.89, 103.02) * mm, "end": v(33.28, 102.56) * mm});
            skPoint(sketch, "E102.22.9", {"position": v(33.78, 103.42) * mm});
            skPoint(sketch, "E102.22.10", {"position": v(35.51, 102.42) * mm});
            skLineSegment(sketch, "E102.23.0", {"start": v(28.2, 99.29) * mm, "end": v(29.5, 104.12) * mm});
            skPoint(sketch, "E102.23.1", {"position": v(27.9, 101.96) * mm});
            skLineSegment(sketch, "E102.23.2", {"start": v(26.28, 99.8) * mm, "end": v(27.57, 104.64) * mm});
            skPoint(sketch, "E102.23.3", {"position": v(26.02, 98.84) * mm});
            skPoint(sketch, "E102.23.4", {"position": v(27.95, 98.32) * mm});
            skArc(sketch, "E102.23.5", {"start": v(26.98, 98.58) * mm, "mid": v(27.74, 98.68) * mm, "end": v(28.2, 99.29) * mm});
            skArc(sketch, "E102.23.6", {"start": v(26.28, 99.8) * mm, "mid": v(26.38, 99.05) * mm, "end": v(26.98, 98.58) * mm});
            skArc(sketch, "E102.23.7", {"start": v(29.5, 104.12) * mm, "mid": v(29.4, 104.88) * mm, "end": v(28.8, 105.34) * mm});
            skArc(sketch, "E102.23.8", {"start": v(28.8, 105.34) * mm, "mid": v(28.04, 105.24) * mm, "end": v(27.57, 104.64) * mm});
            skPoint(sketch, "E102.23.9", {"position": v(27.83, 105.6) * mm});
            skPoint(sketch, "E102.23.10", {"position": v(29.76, 105.08) * mm});
            skPoint(sketch, "E103.1.0", {"position": v(19.02, -65) * mm});
            skPoint(sketch, "E103.1.1", {"position": v(17.15, -61.88) * mm});
            skPoint(sketch, "E103.1.2", {"position": v(17.09, -65.52) * mm});
            skLineSegment(sketch, "E103.1.3", {"start": v(18.76, -64.03) * mm, "end": v(17.47, -59.2) * mm});
            skLineSegment(sketch, "E103.1.4", {"start": v(16.83, -64.55) * mm, "end": v(15.54, -59.72) * mm});
            skPoint(sketch, "E103.1.5", {"position": v(19.02, -65) * mm});
            skPoint(sketch, "E103.1.6", {"position": v(17.15, -61.88) * mm});
            skPoint(sketch, "E103.1.7", {"position": v(17.09, -65.52) * mm});
            skLineSegment(sketch, "E103.1.8", {"start": v(18.76, -64.03) * mm, "end": v(17.47, -59.2) * mm});
            skLineSegment(sketch, "E103.1.9", {"start": v(16.83, -64.55) * mm, "end": v(15.54, -59.72) * mm});
            skArc(sketch, "E103.1.10", {"start": v(16.83, -64.55) * mm, "mid": v(17.3, -65.16) * mm, "end": v(18.06, -65.26) * mm});
            skPoint(sketch, "E103.1.11", {"position": v(15.28, -58.76) * mm});
            skArc(sketch, "E103.1.12", {"start": v(18.06, -65.26) * mm, "mid": v(18.66, -64.8) * mm, "end": v(18.76, -64.03) * mm});
            skPoint(sketch, "E103.1.13", {"position": v(17.2, -58.24) * mm});
            skArc(sketch, "E103.1.14", {"start": v(16.83, -64.55) * mm, "mid": v(17.3, -65.16) * mm, "end": v(18.06, -65.26) * mm});
            skArc(sketch, "E103.1.15", {"start": v(18.06, -65.26) * mm, "mid": v(18.66, -64.8) * mm, "end": v(18.76, -64.03) * mm});
            skPoint(sketch, "E103.1.16", {"position": v(15.28, -58.76) * mm});
            skPoint(sketch, "E103.1.17", {"position": v(17.2, -58.24) * mm});
            skArc(sketch, "E103.1.18", {"start": v(17.47, -59.2) * mm, "mid": v(17, -58.6) * mm, "end": v(16.24, -58.5) * mm});
            skArc(sketch, "E103.1.19", {"start": v(16.24, -58.5) * mm, "mid": v(15.64, -58.96) * mm, "end": v(15.54, -59.72) * mm});
            skArc(sketch, "E103.1.20", {"start": v(17.47, -59.2) * mm, "mid": v(17, -58.6) * mm, "end": v(16.24, -58.5) * mm});
            skArc(sketch, "E103.1.21", {"start": v(16.24, -58.5) * mm, "mid": v(15.64, -58.96) * mm, "end": v(15.54, -59.72) * mm});
            skPoint(sketch, "E103.2.0", {"position": v(14.76, -66.48) * mm});
            skPoint(sketch, "E103.2.1", {"position": v(12.14, -63.95) * mm});
            skPoint(sketch, "E103.2.2", {"position": v(13.03, -67.48) * mm});
            skLineSegment(sketch, "E103.2.3", {"start": v(14.26, -65.62) * mm, "end": v(11.76, -61.28) * mm});
            skLineSegment(sketch, "E103.2.4", {"start": v(12.53, -66.62) * mm, "end": v(10.03, -62.28) * mm});
            skPoint(sketch, "E103.2.5", {"position": v(14.76, -66.48) * mm});
            skPoint(sketch, "E103.2.6", {"position": v(12.14, -63.95) * mm});
            skPoint(sketch, "E103.2.7", {"position": v(13.03, -67.48) * mm});
            skLineSegment(sketch, "E103.2.8", {"start": v(14.26, -65.62) * mm, "end": v(11.76, -61.28) * mm});
            skLineSegment(sketch, "E103.2.9", {"start": v(12.53, -66.62) * mm, "end": v(10.03, -62.28) * mm});
            skArc(sketch, "E103.2.10", {"start": v(12.53, -66.62) * mm, "mid": v(13.14, -67.08) * mm, "end": v(13.9, -66.98) * mm});
            skPoint(sketch, "E103.2.11", {"position": v(9.53, -61.42) * mm});
            skArc(sketch, "E103.2.12", {"start": v(13.9, -66.98) * mm, "mid": v(14.36, -66.37) * mm, "end": v(14.26, -65.62) * mm});
            skPoint(sketch, "E103.2.13", {"position": v(11.26, -60.42) * mm});
            skArc(sketch, "E103.2.14", {"start": v(12.53, -66.62) * mm, "mid": v(13.14, -67.08) * mm, "end": v(13.9, -66.98) * mm});
            skArc(sketch, "E103.2.15", {"start": v(13.9, -66.98) * mm, "mid": v(14.36, -66.37) * mm, "end": v(14.26, -65.62) * mm});
            skPoint(sketch, "E103.2.16", {"position": v(9.53, -61.42) * mm});
            skPoint(sketch, "E103.2.17", {"position": v(11.26, -60.42) * mm});
            skArc(sketch, "E103.2.18", {"start": v(11.76, -61.28) * mm, "mid": v(11.15, -60.82) * mm, "end": v(10.4, -60.92) * mm});
            skArc(sketch, "E103.2.19", {"start": v(10.4, -60.92) * mm, "mid": v(9.93, -61.53) * mm, "end": v(10.03, -62.28) * mm});
            skArc(sketch, "E103.2.20", {"start": v(11.76, -61.28) * mm, "mid": v(11.15, -60.82) * mm, "end": v(10.4, -60.92) * mm});
            skArc(sketch, "E103.2.21", {"start": v(10.4, -60.92) * mm, "mid": v(9.93, -61.53) * mm, "end": v(10.03, -62.28) * mm});
            skPoint(sketch, "E103.3.0", {"position": v(11.03, -69.02) * mm});
            skPoint(sketch, "E103.3.1", {"position": v(7.85, -67.25) * mm});
            skPoint(sketch, "E103.3.2", {"position": v(9.62, -70.43) * mm});
            skLineSegment(sketch, "E103.3.3", {"start": v(10.32, -68.3) * mm, "end": v(6.79, -64.77) * mm});
            skLineSegment(sketch, "E103.3.4", {"start": v(8.9, -69.72) * mm, "end": v(5.37, -66.19) * mm});
            skPoint(sketch, "E103.3.5", {"position": v(11.03, -69.02) * mm});
            skPoint(sketch, "E103.3.6", {"position": v(7.85, -67.25) * mm});
            skPoint(sketch, "E103.3.7", {"position": v(9.62, -70.43) * mm});
            skLineSegment(sketch, "E103.3.8", {"start": v(10.32, -68.3) * mm, "end": v(6.79, -64.77) * mm});
            skLineSegment(sketch, "E103.3.9", {"start": v(8.9, -69.72) * mm, "end": v(5.37, -66.19) * mm});
            skArc(sketch, "E103.3.10", {"start": v(8.9, -69.72) * mm, "mid": v(9.62, -70.02) * mm, "end": v(10.32, -69.72) * mm});
            skPoint(sketch, "E103.3.11", {"position": v(4.67, -65.48) * mm});
            skArc(sketch, "E103.3.12", {"start": v(10.32, -69.72) * mm, "mid": v(10.62, -69.02) * mm, "end": v(10.32, -68.3) * mm});
            skPoint(sketch, "E103.3.13", {"position": v(6.08, -64.07) * mm});
            skArc(sketch, "E103.3.14", {"start": v(8.9, -69.72) * mm, "mid": v(9.62, -70.02) * mm, "end": v(10.32, -69.72) * mm});
            skArc(sketch, "E103.3.15", {"start": v(10.32, -69.72) * mm, "mid": v(10.62, -69.02) * mm, "end": v(10.32, -68.3) * mm});
            skPoint(sketch, "E103.3.16", {"position": v(4.67, -65.48) * mm});
            skPoint(sketch, "E103.3.17", {"position": v(6.08, -64.07) * mm});
            skArc(sketch, "E103.3.18", {"start": v(6.79, -64.77) * mm, "mid": v(6.08, -64.48) * mm, "end": v(5.37, -64.77) * mm});
            skArc(sketch, "E103.3.19", {"start": v(5.37, -64.77) * mm, "mid": v(5.08, -65.48) * mm, "end": v(5.37, -66.19) * mm});
            skArc(sketch, "E103.3.20", {"start": v(6.79, -64.77) * mm, "mid": v(6.08, -64.48) * mm, "end": v(5.37, -64.77) * mm});
            skArc(sketch, "E103.3.21", {"start": v(5.37, -64.77) * mm, "mid": v(5.08, -65.48) * mm, "end": v(5.37, -66.19) * mm});
            skPoint(sketch, "E103.4.0", {"position": v(8.08, -72.43) * mm});
            skPoint(sketch, "E103.4.1", {"position": v(4.55, -71.55) * mm});
            skPoint(sketch, "E103.4.2", {"position": v(7.08, -74.16) * mm});
            skLineSegment(sketch, "E103.4.3", {"start": v(7.22, -71.93) * mm, "end": v(2.88, -69.43) * mm});
            skLineSegment(sketch, "E103.4.4", {"start": v(6.22, -73.66) * mm, "end": v(1.88, -71.16) * mm});
            skPoint(sketch, "E103.4.5", {"position": v(8.08, -72.43) * mm});
            skPoint(sketch, "E103.4.6", {"position": v(4.55, -71.55) * mm});
            skPoint(sketch, "E103.4.7", {"position": v(7.08, -74.16) * mm});
            skLineSegment(sketch, "E103.4.8", {"start": v(7.22, -71.93) * mm, "end": v(2.88, -69.43) * mm});
            skLineSegment(sketch, "E103.4.9", {"start": v(6.22, -73.66) * mm, "end": v(1.88, -71.16) * mm});
            skArc(sketch, "E103.4.10", {"start": v(6.22, -73.66) * mm, "mid": v(6.97, -73.76) * mm, "end": v(7.58, -73.3) * mm});
            skPoint(sketch, "E103.4.11", {"position": v(1.02, -70.66) * mm});
            skArc(sketch, "E103.4.12", {"start": v(7.58, -73.3) * mm, "mid": v(7.68, -72.54) * mm, "end": v(7.22, -71.93) * mm});
            skPoint(sketch, "E103.4.13", {"position": v(2.02, -68.93) * mm});
            skArc(sketch, "E103.4.14", {"start": v(6.22, -73.66) * mm, "mid": v(6.97, -73.76) * mm, "end": v(7.58, -73.3) * mm});
            skArc(sketch, "E103.4.15", {"start": v(7.58, -73.3) * mm, "mid": v(7.68, -72.54) * mm, "end": v(7.22, -71.93) * mm});
            skPoint(sketch, "E103.4.16", {"position": v(1.02, -70.66) * mm});
            skPoint(sketch, "E103.4.17", {"position": v(2.02, -68.93) * mm});
            skArc(sketch, "E103.4.18", {"start": v(2.88, -69.43) * mm, "mid": v(2.13, -69.33) * mm, "end": v(1.52, -69.8) * mm});
            skArc(sketch, "E103.4.19", {"start": v(1.52, -69.8) * mm, "mid": v(1.42, -70.55) * mm, "end": v(1.88, -71.16) * mm});
            skArc(sketch, "E103.4.20", {"start": v(2.88, -69.43) * mm, "mid": v(2.13, -69.33) * mm, "end": v(1.52, -69.8) * mm});
            skArc(sketch, "E103.4.21", {"start": v(1.52, -69.8) * mm, "mid": v(1.42, -70.55) * mm, "end": v(1.88, -71.16) * mm});
            skPoint(sketch, "E103.5.0", {"position": v(6.12, -76.49) * mm});
            skPoint(sketch, "E103.5.1", {"position": v(2.48, -76.55) * mm});
            skPoint(sketch, "E103.5.2", {"position": v(5.6, -78.42) * mm});
            skLineSegment(sketch, "E103.5.3", {"start": v(5.15, -76.23) * mm, "end": v(0.32, -74.94) * mm});
            skLineSegment(sketch, "E103.5.4", {"start": v(4.63, -78.16) * mm, "end": v(-0.2, -76.87) * mm});
            skPoint(sketch, "E103.5.5", {"position": v(6.12, -76.49) * mm});
            skPoint(sketch, "E103.5.6", {"position": v(2.48, -76.55) * mm});
            skPoint(sketch, "E103.5.7", {"position": v(5.6, -78.42) * mm});
            skLineSegment(sketch, "E103.5.8", {"start": v(5.15, -76.23) * mm, "end": v(0.32, -74.94) * mm});
            skLineSegment(sketch, "E103.5.9", {"start": v(4.63, -78.16) * mm, "end": v(-0.2, -76.87) * mm});
            skArc(sketch, "E103.5.10", {"start": v(4.63, -78.16) * mm, "mid": v(5.4, -78.06) * mm, "end": v(5.86, -77.46) * mm});
            skPoint(sketch, "E103.5.11", {"position": v(-1.16, -76.6) * mm});
            skArc(sketch, "E103.5.12", {"start": v(5.86, -77.46) * mm, "mid": v(5.76, -76.7) * mm, "end": v(5.15, -76.23) * mm});
            skPoint(sketch, "E103.5.13", {"position": v(-0.64, -74.68) * mm});
            skArc(sketch, "E103.5.14", {"start": v(4.63, -78.16) * mm, "mid": v(5.4, -78.06) * mm, "end": v(5.86, -77.46) * mm});
            skArc(sketch, "E103.5.15", {"start": v(5.86, -77.46) * mm, "mid": v(5.76, -76.7) * mm, "end": v(5.15, -76.23) * mm});
            skPoint(sketch, "E103.5.16", {"position": v(-1.16, -76.6) * mm});
            skPoint(sketch, "E103.5.17", {"position": v(-0.64, -74.68) * mm});
            skArc(sketch, "E103.5.18", {"start": v(0.32, -74.94) * mm, "mid": v(-0.44, -75.04) * mm, "end": v(-0.9, -75.64) * mm});
            skArc(sketch, "E103.5.19", {"start": v(-0.9, -75.64) * mm, "mid": v(-0.8, -76.4) * mm, "end": v(-0.2, -76.87) * mm});
            skArc(sketch, "E103.5.20", {"start": v(0.32, -74.94) * mm, "mid": v(-0.44, -75.04) * mm, "end": v(-0.9, -75.64) * mm});
            skArc(sketch, "E103.5.21", {"start": v(-0.9, -75.64) * mm, "mid": v(-0.8, -76.4) * mm, "end": v(-0.2, -76.87) * mm});
            skPoint(sketch, "E103.6.0", {"position": v(5.27, -80.92) * mm});
            skPoint(sketch, "E103.6.1", {"position": v(1.77, -81.92) * mm});
            skPoint(sketch, "E103.6.2", {"position": v(5.27, -82.92) * mm});
            skLineSegment(sketch, "E103.6.3", {"start": v(4.27, -80.92) * mm, "end": v(-0.73, -80.92) * mm});
            skLineSegment(sketch, "E103.6.4", {"start": v(4.27, -82.92) * mm, "end": v(-0.73, -82.92) * mm});
            skPoint(sketch, "E103.6.5", {"position": v(5.27, -80.92) * mm});
            skPoint(sketch, "E103.6.6", {"position": v(1.77, -81.92) * mm});
            skPoint(sketch, "E103.6.7", {"position": v(5.27, -82.92) * mm});
            skLineSegment(sketch, "E103.6.8", {"start": v(4.27, -80.92) * mm, "end": v(-0.73, -80.92) * mm});
            skLineSegment(sketch, "E103.6.9", {"start": v(4.27, -82.92) * mm, "end": v(-0.73, -82.92) * mm});
            skArc(sketch, "E103.6.10", {"start": v(4.27, -82.92) * mm, "mid": v(4.98, -82.63) * mm, "end": v(5.27, -81.92) * mm});
            skPoint(sketch, "E103.6.11", {"position": v(-1.73, -82.92) * mm});
            skArc(sketch, "E103.6.12", {"start": v(5.27, -81.92) * mm, "mid": v(4.98, -81.21) * mm, "end": v(4.27, -80.92) * mm});
            skPoint(sketch, "E103.6.13", {"position": v(-1.73, -80.92) * mm});
            skArc(sketch, "E103.6.14", {"start": v(4.27, -82.92) * mm, "mid": v(4.98, -82.63) * mm, "end": v(5.27, -81.92) * mm});
            skArc(sketch, "E103.6.15", {"start": v(5.27, -81.92) * mm, "mid": v(4.98, -81.21) * mm, "end": v(4.27, -80.92) * mm});
            skPoint(sketch, "E103.6.16", {"position": v(-1.73, -82.92) * mm});
            skPoint(sketch, "E103.6.17", {"position": v(-1.73, -80.92) * mm});
            skArc(sketch, "E103.6.18", {"start": v(-0.73, -80.92) * mm, "mid": v(-1.44, -81.21) * mm, "end": v(-1.73, -81.92) * mm});
            skArc(sketch, "E103.6.19", {"start": v(-1.73, -81.92) * mm, "mid": v(-1.44, -82.63) * mm, "end": v(-0.73, -82.92) * mm});
            skArc(sketch, "E103.6.20", {"start": v(-0.73, -80.92) * mm, "mid": v(-1.44, -81.21) * mm, "end": v(-1.73, -81.92) * mm});
            skArc(sketch, "E103.6.21", {"start": v(-1.73, -81.92) * mm, "mid": v(-1.44, -82.63) * mm, "end": v(-0.73, -82.92) * mm});
            skPoint(sketch, "E103.7.0", {"position": v(5.6, -85.42) * mm});
            skPoint(sketch, "E103.7.1", {"position": v(2.48, -87.3) * mm});
            skPoint(sketch, "E103.7.2", {"position": v(6.12, -87.35) * mm});
            skLineSegment(sketch, "E103.7.3", {"start": v(4.63, -85.68) * mm, "end": v(-0.2, -86.97) * mm});
            skLineSegment(sketch, "E103.7.4", {"start": v(5.15, -87.6) * mm, "end": v(0.32, -88.9) * mm});
            skPoint(sketch, "E103.7.5", {"position": v(5.6, -85.42) * mm});
            skPoint(sketch, "E103.7.6", {"position": v(2.48, -87.3) * mm});
            skPoint(sketch, "E103.7.7", {"position": v(6.12, -87.35) * mm});
            skLineSegment(sketch, "E103.7.8", {"start": v(4.63, -85.68) * mm, "end": v(-0.2, -86.97) * mm});
            skLineSegment(sketch, "E103.7.9", {"start": v(5.15, -87.6) * mm, "end": v(0.32, -88.9) * mm});
            skArc(sketch, "E103.7.10", {"start": v(5.15, -87.6) * mm, "mid": v(5.76, -87.14) * mm, "end": v(5.86, -86.38) * mm});
            skPoint(sketch, "E103.7.11", {"position": v(-0.64, -89.16) * mm});
            skArc(sketch, "E103.7.12", {"start": v(5.86, -86.38) * mm, "mid": v(5.4, -85.78) * mm, "end": v(4.63, -85.68) * mm});
            skPoint(sketch, "E103.7.13", {"position": v(-1.16, -87.23) * mm});
            skArc(sketch, "E103.7.14", {"start": v(5.15, -87.6) * mm, "mid": v(5.76, -87.14) * mm, "end": v(5.86, -86.38) * mm});
            skArc(sketch, "E103.7.15", {"start": v(5.86, -86.38) * mm, "mid": v(5.4, -85.78) * mm, "end": v(4.63, -85.68) * mm});
            skPoint(sketch, "E103.7.16", {"position": v(-0.64, -89.16) * mm});
            skPoint(sketch, "E103.7.17", {"position": v(-1.16, -87.23) * mm});
            skArc(sketch, "E103.7.18", {"start": v(-0.2, -86.97) * mm, "mid": v(-0.8, -87.44) * mm, "end": v(-0.9, -88.2) * mm});
            skArc(sketch, "E103.7.19", {"start": v(-0.9, -88.2) * mm, "mid": v(-0.44, -88.8) * mm, "end": v(0.32, -88.9) * mm});
            skArc(sketch, "E103.7.20", {"start": v(-0.2, -86.97) * mm, "mid": v(-0.8, -87.44) * mm, "end": v(-0.9, -88.2) * mm});
            skArc(sketch, "E103.7.21", {"start": v(-0.9, -88.2) * mm, "mid": v(-0.44, -88.8) * mm, "end": v(0.32, -88.9) * mm});
            skPoint(sketch, "E103.8.0", {"position": v(7.08, -89.68) * mm});
            skPoint(sketch, "E103.8.1", {"position": v(4.55, -92.3) * mm});
            skPoint(sketch, "E103.8.2", {"position": v(8.08, -91.41) * mm});
            skLineSegment(sketch, "E103.8.3", {"start": v(6.22, -90.18) * mm, "end": v(1.88, -92.68) * mm});
            skLineSegment(sketch, "E103.8.4", {"start": v(7.22, -91.91) * mm, "end": v(2.88, -94.41) * mm});
            skPoint(sketch, "E103.8.5", {"position": v(7.08, -89.68) * mm});
            skPoint(sketch, "E103.8.6", {"position": v(4.55, -92.3) * mm});
            skPoint(sketch, "E103.8.7", {"position": v(8.08, -91.41) * mm});
            skLineSegment(sketch, "E103.8.8", {"start": v(6.22, -90.18) * mm, "end": v(1.88, -92.68) * mm});
            skLineSegment(sketch, "E103.8.9", {"start": v(7.22, -91.91) * mm, "end": v(2.88, -94.41) * mm});
            skArc(sketch, "E103.8.10", {"start": v(7.22, -91.91) * mm, "mid": v(7.68, -91.3) * mm, "end": v(7.58, -90.55) * mm});
            skPoint(sketch, "E103.8.11", {"position": v(2.02, -94.91) * mm});
            skArc(sketch, "E103.8.12", {"start": v(7.58, -90.55) * mm, "mid": v(6.97, -90.08) * mm, "end": v(6.22, -90.18) * mm});
            skPoint(sketch, "E103.8.13", {"position": v(1.02, -93.18) * mm});
            skArc(sketch, "E103.8.14", {"start": v(7.22, -91.91) * mm, "mid": v(7.68, -91.3) * mm, "end": v(7.58, -90.55) * mm});
            skArc(sketch, "E103.8.15", {"start": v(7.58, -90.55) * mm, "mid": v(6.97, -90.08) * mm, "end": v(6.22, -90.18) * mm});
            skPoint(sketch, "E103.8.16", {"position": v(2.02, -94.91) * mm});
            skPoint(sketch, "E103.8.17", {"position": v(1.02, -93.18) * mm});
            skArc(sketch, "E103.8.18", {"start": v(1.88, -92.68) * mm, "mid": v(1.42, -93.29) * mm, "end": v(1.52, -94.05) * mm});
            skArc(sketch, "E103.8.19", {"start": v(1.52, -94.05) * mm, "mid": v(2.13, -94.51) * mm, "end": v(2.88, -94.41) * mm});
            skArc(sketch, "E103.8.20", {"start": v(1.88, -92.68) * mm, "mid": v(1.42, -93.29) * mm, "end": v(1.52, -94.05) * mm});
            skArc(sketch, "E103.8.21", {"start": v(1.52, -94.05) * mm, "mid": v(2.13, -94.51) * mm, "end": v(2.88, -94.41) * mm});
            skPoint(sketch, "E103.9.0", {"position": v(9.62, -93.41) * mm});
            skPoint(sketch, "E103.9.1", {"position": v(7.85, -96.6) * mm});
            skPoint(sketch, "E103.9.2", {"position": v(11.03, -94.82) * mm});
            skLineSegment(sketch, "E103.9.3", {"start": v(8.9, -94.12) * mm, "end": v(5.37, -97.65) * mm});
            skLineSegment(sketch, "E103.9.4", {"start": v(10.32, -95.53) * mm, "end": v(6.79, -99.07) * mm});
            skPoint(sketch, "E103.9.5", {"position": v(9.62, -93.41) * mm});
            skPoint(sketch, "E103.9.6", {"position": v(7.85, -96.6) * mm});
            skPoint(sketch, "E103.9.7", {"position": v(11.03, -94.82) * mm});
            skLineSegment(sketch, "E103.9.8", {"start": v(8.9, -94.12) * mm, "end": v(5.37, -97.65) * mm});
            skLineSegment(sketch, "E103.9.9", {"start": v(10.32, -95.53) * mm, "end": v(6.79, -99.07) * mm});
            skArc(sketch, "E103.9.10", {"start": v(10.32, -95.53) * mm, "mid": v(10.62, -94.82) * mm, "end": v(10.32, -94.12) * mm});
            skPoint(sketch, "E103.9.11", {"position": v(6.08, -99.77) * mm});
            skArc(sketch, "E103.9.12", {"start": v(10.32, -94.12) * mm, "mid": v(9.62, -93.82) * mm, "end": v(8.9, -94.12) * mm});
            skPoint(sketch, "E103.9.13", {"position": v(4.67, -98.36) * mm});
            skArc(sketch, "E103.9.14", {"start": v(10.32, -95.53) * mm, "mid": v(10.62, -94.82) * mm, "end": v(10.32, -94.12) * mm});
            skArc(sketch, "E103.9.15", {"start": v(10.32, -94.12) * mm, "mid": v(9.62, -93.82) * mm, "end": v(8.9, -94.12) * mm});
            skPoint(sketch, "E103.9.16", {"position": v(6.08, -99.77) * mm});
            skPoint(sketch, "E103.9.17", {"position": v(4.67, -98.36) * mm});
            skArc(sketch, "E103.9.18", {"start": v(5.37, -97.65) * mm, "mid": v(5.08, -98.36) * mm, "end": v(5.37, -99.07) * mm});
            skArc(sketch, "E103.9.19", {"start": v(5.37, -99.07) * mm, "mid": v(6.08, -99.36) * mm, "end": v(6.79, -99.07) * mm});
            skArc(sketch, "E103.9.20", {"start": v(5.37, -97.65) * mm, "mid": v(5.08, -98.36) * mm, "end": v(5.37, -99.07) * mm});
            skArc(sketch, "E103.9.21", {"start": v(5.37, -99.07) * mm, "mid": v(6.08, -99.36) * mm, "end": v(6.79, -99.07) * mm});
            skPoint(sketch, "E103.10.0", {"position": v(13.03, -96.36) * mm});
            skPoint(sketch, "E103.10.1", {"position": v(12.14, -99.9) * mm});
            skPoint(sketch, "E103.10.2", {"position": v(14.76, -97.36) * mm});
            skLineSegment(sketch, "E103.10.3", {"start": v(12.53, -97.22) * mm, "end": v(10.03, -101.56) * mm});
            skLineSegment(sketch, "E103.10.4", {"start": v(14.26, -98.22) * mm, "end": v(11.76, -102.56) * mm});
            skPoint(sketch, "E103.10.5", {"position": v(13.03, -96.36) * mm});
            skPoint(sketch, "E103.10.6", {"position": v(12.14, -99.9) * mm});
            skPoint(sketch, "E103.10.7", {"position": v(14.76, -97.36) * mm});
            skLineSegment(sketch, "E103.10.8", {"start": v(12.53, -97.22) * mm, "end": v(10.03, -101.56) * mm});
            skLineSegment(sketch, "E103.10.9", {"start": v(14.26, -98.22) * mm, "end": v(11.76, -102.56) * mm});
            skArc(sketch, "E103.10.10", {"start": v(14.26, -98.22) * mm, "mid": v(14.36, -97.47) * mm, "end": v(13.9, -96.86) * mm});
            skPoint(sketch, "E103.10.11", {"position": v(11.26, -103.42) * mm});
            skArc(sketch, "E103.10.12", {"start": v(13.9, -96.86) * mm, "mid": v(13.14, -96.76) * mm, "end": v(12.53, -97.22) * mm});
            skPoint(sketch, "E103.10.13", {"position": v(9.53, -102.42) * mm});
            skArc(sketch, "E103.10.14", {"start": v(14.26, -98.22) * mm, "mid": v(14.36, -97.47) * mm, "end": v(13.9, -96.86) * mm});
            skArc(sketch, "E103.10.15", {"start": v(13.9, -96.86) * mm, "mid": v(13.14, -96.76) * mm, "end": v(12.53, -97.22) * mm});
            skPoint(sketch, "E103.10.16", {"position": v(11.26, -103.42) * mm});
            skPoint(sketch, "E103.10.17", {"position": v(9.53, -102.42) * mm});
            skArc(sketch, "E103.10.18", {"start": v(10.03, -101.56) * mm, "mid": v(9.93, -102.31) * mm, "end": v(10.4, -102.92) * mm});
            skArc(sketch, "E103.10.19", {"start": v(10.4, -102.92) * mm, "mid": v(11.15, -103.02) * mm, "end": v(11.76, -102.56) * mm});
            skArc(sketch, "E103.10.20", {"start": v(10.03, -101.56) * mm, "mid": v(9.93, -102.31) * mm, "end": v(10.4, -102.92) * mm});
            skArc(sketch, "E103.10.21", {"start": v(10.4, -102.92) * mm, "mid": v(11.15, -103.02) * mm, "end": v(11.76, -102.56) * mm});
            skPoint(sketch, "E103.11.0", {"position": v(17.09, -98.32) * mm});
            skPoint(sketch, "E103.11.1", {"position": v(17.15, -101.96) * mm});
            skPoint(sketch, "E103.11.2", {"position": v(19.02, -98.84) * mm});
            skLineSegment(sketch, "E103.11.3", {"start": v(16.83, -99.29) * mm, "end": v(15.54, -104.12) * mm});
            skLineSegment(sketch, "E103.11.4", {"start": v(18.76, -99.8) * mm, "end": v(17.47, -104.64) * mm});
            skPoint(sketch, "E103.11.5", {"position": v(17.09, -98.32) * mm});
            skPoint(sketch, "E103.11.6", {"position": v(17.15, -101.96) * mm});
            skPoint(sketch, "E103.11.7", {"position": v(19.02, -98.84) * mm});
            skLineSegment(sketch, "E103.11.8", {"start": v(16.83, -99.29) * mm, "end": v(15.54, -104.12) * mm});
            skLineSegment(sketch, "E103.11.9", {"start": v(18.76, -99.8) * mm, "end": v(17.47, -104.64) * mm});
            skArc(sketch, "E103.11.10", {"start": v(18.76, -99.8) * mm, "mid": v(18.66, -99.05) * mm, "end": v(18.06, -98.58) * mm});
            skPoint(sketch, "E103.11.11", {"position": v(17.2, -105.6) * mm});
            skArc(sketch, "E103.11.12", {"start": v(18.06, -98.58) * mm, "mid": v(17.3, -98.68) * mm, "end": v(16.83, -99.29) * mm});
            skPoint(sketch, "E103.11.13", {"position": v(15.28, -105.08) * mm});
            skArc(sketch, "E103.11.14", {"start": v(18.76, -99.8) * mm, "mid": v(18.66, -99.05) * mm, "end": v(18.06, -98.58) * mm});
            skArc(sketch, "E103.11.15", {"start": v(18.06, -98.58) * mm, "mid": v(17.3, -98.68) * mm, "end": v(16.83, -99.29) * mm});
            skPoint(sketch, "E103.11.16", {"position": v(17.2, -105.6) * mm});
            skPoint(sketch, "E103.11.17", {"position": v(15.28, -105.08) * mm});
            skArc(sketch, "E103.11.18", {"start": v(15.54, -104.12) * mm, "mid": v(15.64, -104.88) * mm, "end": v(16.24, -105.34) * mm});
            skArc(sketch, "E103.11.19", {"start": v(16.24, -105.34) * mm, "mid": v(17, -105.24) * mm, "end": v(17.47, -104.64) * mm});
            skArc(sketch, "E103.11.20", {"start": v(15.54, -104.12) * mm, "mid": v(15.64, -104.88) * mm, "end": v(16.24, -105.34) * mm});
            skArc(sketch, "E103.11.21", {"start": v(16.24, -105.34) * mm, "mid": v(17, -105.24) * mm, "end": v(17.47, -104.64) * mm});
            skPoint(sketch, "E103.12.0", {"position": v(21.52, -99.17) * mm});
            skPoint(sketch, "E103.12.1", {"position": v(22.52, -102.67) * mm});
            skPoint(sketch, "E103.12.2", {"position": v(23.52, -99.17) * mm});
            skLineSegment(sketch, "E103.12.3", {"start": v(21.52, -100.17) * mm, "end": v(21.52, -105.17) * mm});
            skLineSegment(sketch, "E103.12.4", {"start": v(23.52, -100.17) * mm, "end": v(23.52, -105.17) * mm});
            skPoint(sketch, "E103.12.5", {"position": v(21.52, -99.17) * mm});
            skPoint(sketch, "E103.12.6", {"position": v(22.52, -102.67) * mm});
            skPoint(sketch, "E103.12.7", {"position": v(23.52, -99.17) * mm});
            skLineSegment(sketch, "E103.12.8", {"start": v(21.52, -100.17) * mm, "end": v(21.52, -105.17) * mm});
            skLineSegment(sketch, "E103.12.9", {"start": v(23.52, -100.17) * mm, "end": v(23.52, -105.17) * mm});
            skArc(sketch, "E103.12.10", {"start": v(23.52, -100.17) * mm, "mid": v(23.23, -99.46) * mm, "end": v(22.52, -99.17) * mm});
            skPoint(sketch, "E103.12.11", {"position": v(23.52, -106.17) * mm});
            skArc(sketch, "E103.12.12", {"start": v(22.52, -99.17) * mm, "mid": v(21.81, -99.46) * mm, "end": v(21.52, -100.17) * mm});
            skPoint(sketch, "E103.12.13", {"position": v(21.52, -106.17) * mm});
            skArc(sketch, "E103.12.14", {"start": v(23.52, -100.17) * mm, "mid": v(23.23, -99.46) * mm, "end": v(22.52, -99.17) * mm});
            skArc(sketch, "E103.12.15", {"start": v(22.52, -99.17) * mm, "mid": v(21.81, -99.46) * mm, "end": v(21.52, -100.17) * mm});
            skPoint(sketch, "E103.12.16", {"position": v(23.52, -106.17) * mm});
            skPoint(sketch, "E103.12.17", {"position": v(21.52, -106.17) * mm});
            skArc(sketch, "E103.12.18", {"start": v(21.52, -105.17) * mm, "mid": v(21.81, -105.88) * mm, "end": v(22.52, -106.17) * mm});
            skArc(sketch, "E103.12.19", {"start": v(22.52, -106.17) * mm, "mid": v(23.23, -105.88) * mm, "end": v(23.52, -105.17) * mm});
            skArc(sketch, "E103.12.20", {"start": v(21.52, -105.17) * mm, "mid": v(21.81, -105.88) * mm, "end": v(22.52, -106.17) * mm});
            skArc(sketch, "E103.12.21", {"start": v(22.52, -106.17) * mm, "mid": v(23.23, -105.88) * mm, "end": v(23.52, -105.17) * mm});
            skPoint(sketch, "E103.13.0", {"position": v(26.02, -98.84) * mm});
            skPoint(sketch, "E103.13.1", {"position": v(27.9, -101.96) * mm});
            skPoint(sketch, "E103.13.2", {"position": v(27.95, -98.32) * mm});
            skLineSegment(sketch, "E103.13.3", {"start": v(26.28, -99.8) * mm, "end": v(27.57, -104.64) * mm});
            skLineSegment(sketch, "E103.13.4", {"start": v(28.2, -99.29) * mm, "end": v(29.5, -104.12) * mm});
            skPoint(sketch, "E103.13.5", {"position": v(26.02, -98.84) * mm});
            skPoint(sketch, "E103.13.6", {"position": v(27.9, -101.96) * mm});
            skPoint(sketch, "E103.13.7", {"position": v(27.95, -98.32) * mm});
            skLineSegment(sketch, "E103.13.8", {"start": v(26.28, -99.8) * mm, "end": v(27.57, -104.64) * mm});
            skLineSegment(sketch, "E103.13.9", {"start": v(28.2, -99.29) * mm, "end": v(29.5, -104.12) * mm});
            skArc(sketch, "E103.13.10", {"start": v(28.2, -99.29) * mm, "mid": v(27.74, -98.68) * mm, "end": v(26.98, -98.58) * mm});
            skPoint(sketch, "E103.13.11", {"position": v(29.76, -105.08) * mm});
            skArc(sketch, "E103.13.12", {"start": v(26.98, -98.58) * mm, "mid": v(26.38, -99.05) * mm, "end": v(26.28, -99.8) * mm});
            skPoint(sketch, "E103.13.13", {"position": v(27.83, -105.6) * mm});
            skArc(sketch, "E103.13.14", {"start": v(28.2, -99.29) * mm, "mid": v(27.74, -98.68) * mm, "end": v(26.98, -98.58) * mm});
            skArc(sketch, "E103.13.15", {"start": v(26.98, -98.58) * mm, "mid": v(26.38, -99.05) * mm, "end": v(26.28, -99.8) * mm});
            skPoint(sketch, "E103.13.16", {"position": v(29.76, -105.08) * mm});
            skPoint(sketch, "E103.13.17", {"position": v(27.83, -105.6) * mm});
            skArc(sketch, "E103.13.18", {"start": v(27.57, -104.64) * mm, "mid": v(28.04, -105.24) * mm, "end": v(28.8, -105.34) * mm});
            skArc(sketch, "E103.13.19", {"start": v(28.8, -105.34) * mm, "mid": v(29.4, -104.88) * mm, "end": v(29.5, -104.12) * mm});
            skArc(sketch, "E103.13.20", {"start": v(27.57, -104.64) * mm, "mid": v(28.04, -105.24) * mm, "end": v(28.8, -105.34) * mm});
            skArc(sketch, "E103.13.21", {"start": v(28.8, -105.34) * mm, "mid": v(29.4, -104.88) * mm, "end": v(29.5, -104.12) * mm});
            skPoint(sketch, "E103.14.0", {"position": v(30.28, -97.36) * mm});
            skPoint(sketch, "E103.14.1", {"position": v(32.9, -99.9) * mm});
            skPoint(sketch, "E103.14.2", {"position": v(32.01, -96.36) * mm});
            skLineSegment(sketch, "E103.14.3", {"start": v(30.78, -98.22) * mm, "end": v(33.28, -102.56) * mm});
            skLineSegment(sketch, "E103.14.4", {"start": v(32.51, -97.22) * mm, "end": v(35.01, -101.56) * mm});
            skPoint(sketch, "E103.14.5", {"position": v(30.28, -97.36) * mm});
            skPoint(sketch, "E103.14.6", {"position": v(32.9, -99.9) * mm});
            skPoint(sketch, "E103.14.7", {"position": v(32.01, -96.36) * mm});
            skLineSegment(sketch, "E103.14.8", {"start": v(30.78, -98.22) * mm, "end": v(33.28, -102.56) * mm});
            skLineSegment(sketch, "E103.14.9", {"start": v(32.51, -97.22) * mm, "end": v(35.01, -101.56) * mm});
            skArc(sketch, "E103.14.10", {"start": v(32.51, -97.22) * mm, "mid": v(31.9, -96.76) * mm, "end": v(31.14, -96.86) * mm});
            skPoint(sketch, "E103.14.11", {"position": v(35.51, -102.42) * mm});
            skArc(sketch, "E103.14.12", {"start": v(31.14, -96.86) * mm, "mid": v(30.68, -97.47) * mm, "end": v(30.78, -98.22) * mm});
            skPoint(sketch, "E103.14.13", {"position": v(33.78, -103.42) * mm});
            skArc(sketch, "E103.14.14", {"start": v(32.51, -97.22) * mm, "mid": v(31.9, -96.76) * mm, "end": v(31.15, -96.86) * mm});
            skArc(sketch, "E103.14.15", {"start": v(31.14, -96.86) * mm, "mid": v(30.68, -97.47) * mm, "end": v(30.78, -98.22) * mm});
            skPoint(sketch, "E103.14.16", {"position": v(35.51, -102.42) * mm});
            skPoint(sketch, "E103.14.17", {"position": v(33.78, -103.42) * mm});
            skArc(sketch, "E103.14.18", {"start": v(33.28, -102.56) * mm, "mid": v(33.89, -103.02) * mm, "end": v(34.64, -102.92) * mm});
            skArc(sketch, "E103.14.19", {"start": v(34.65, -102.92) * mm, "mid": v(35.11, -102.31) * mm, "end": v(35.01, -101.56) * mm});
            skArc(sketch, "E103.14.20", {"start": v(33.28, -102.56) * mm, "mid": v(33.89, -103.02) * mm, "end": v(34.64, -102.92) * mm});
            skArc(sketch, "E103.14.21", {"start": v(34.65, -102.92) * mm, "mid": v(35.11, -102.31) * mm, "end": v(35.01, -101.56) * mm});
            skPoint(sketch, "E103.15.0", {"position": v(34.01, -94.82) * mm});
            skPoint(sketch, "E103.15.1", {"position": v(37.2, -96.6) * mm});
            skPoint(sketch, "E103.15.2", {"position": v(35.42, -93.41) * mm});
            skLineSegment(sketch, "E103.15.3", {"start": v(34.72, -95.53) * mm, "end": v(38.25, -99.07) * mm});
            skLineSegment(sketch, "E103.15.4", {"start": v(36.13, -94.12) * mm, "end": v(39.67, -97.65) * mm});
            skPoint(sketch, "E103.15.5", {"position": v(34.01, -94.82) * mm});
            skPoint(sketch, "E103.15.6", {"position": v(37.2, -96.6) * mm});
            skPoint(sketch, "E103.15.7", {"position": v(35.42, -93.41) * mm});
            skLineSegment(sketch, "E103.15.8", {"start": v(34.72, -95.53) * mm, "end": v(38.25, -99.07) * mm});
            skLineSegment(sketch, "E103.15.9", {"start": v(36.13, -94.12) * mm, "end": v(39.67, -97.65) * mm});
            skArc(sketch, "E103.15.10", {"start": v(36.13, -94.12) * mm, "mid": v(35.42, -93.82) * mm, "end": v(34.72, -94.12) * mm});
            skPoint(sketch, "E103.15.11", {"position": v(40.37, -98.36) * mm});
            skArc(sketch, "E103.15.12", {"start": v(34.72, -94.12) * mm, "mid": v(34.42, -94.82) * mm, "end": v(34.72, -95.53) * mm});
            skPoint(sketch, "E103.15.13", {"position": v(38.96, -99.77) * mm});
            skArc(sketch, "E103.15.14", {"start": v(36.13, -94.12) * mm, "mid": v(35.42, -93.82) * mm, "end": v(34.72, -94.12) * mm});
            skArc(sketch, "E103.15.15", {"start": v(34.72, -94.12) * mm, "mid": v(34.42, -94.82) * mm, "end": v(34.72, -95.53) * mm});
            skPoint(sketch, "E103.15.16", {"position": v(40.37, -98.36) * mm});
            skPoint(sketch, "E103.15.17", {"position": v(38.96, -99.77) * mm});
            skArc(sketch, "E103.15.18", {"start": v(38.25, -99.07) * mm, "mid": v(38.96, -99.36) * mm, "end": v(39.67, -99.07) * mm});
            skArc(sketch, "E103.15.19", {"start": v(39.67, -99.07) * mm, "mid": v(39.96, -98.36) * mm, "end": v(39.67, -97.65) * mm});
            skArc(sketch, "E103.15.20", {"start": v(38.25, -99.07) * mm, "mid": v(38.96, -99.36) * mm, "end": v(39.67, -99.07) * mm});
            skArc(sketch, "E103.15.21", {"start": v(39.67, -99.07) * mm, "mid": v(39.96, -98.36) * mm, "end": v(39.67, -97.65) * mm});
            skPoint(sketch, "E103.16.0", {"position": v(36.96, -91.41) * mm});
            skPoint(sketch, "E103.16.1", {"position": v(40.5, -92.3) * mm});
            skPoint(sketch, "E103.16.2", {"position": v(37.96, -89.68) * mm});
            skLineSegment(sketch, "E103.16.3", {"start": v(37.82, -91.91) * mm, "end": v(42.16, -94.41) * mm});
            skLineSegment(sketch, "E103.16.4", {"start": v(38.82, -90.18) * mm, "end": v(43.16, -92.68) * mm});
            skPoint(sketch, "E103.16.5", {"position": v(36.96, -91.41) * mm});
            skPoint(sketch, "E103.16.6", {"position": v(40.5, -92.3) * mm});
            skPoint(sketch, "E103.16.7", {"position": v(37.96, -89.68) * mm});
            skLineSegment(sketch, "E103.16.8", {"start": v(37.82, -91.91) * mm, "end": v(42.16, -94.41) * mm});
            skLineSegment(sketch, "E103.16.9", {"start": v(38.82, -90.18) * mm, "end": v(43.16, -92.68) * mm});
            skArc(sketch, "E103.16.10", {"start": v(38.82, -90.18) * mm, "mid": v(38.07, -90.08) * mm, "end": v(37.46, -90.54) * mm});
            skPoint(sketch, "E103.16.11", {"position": v(44.02, -93.18) * mm});
            skArc(sketch, "E103.16.12", {"start": v(37.46, -90.54) * mm, "mid": v(37.36, -91.3) * mm, "end": v(37.82, -91.91) * mm});
            skPoint(sketch, "E103.16.13", {"position": v(43.02, -94.91) * mm});
            skArc(sketch, "E103.16.14", {"start": v(38.82, -90.18) * mm, "mid": v(38.07, -90.08) * mm, "end": v(37.46, -90.54) * mm});
            skArc(sketch, "E103.16.15", {"start": v(37.46, -90.54) * mm, "mid": v(37.36, -91.3) * mm, "end": v(37.82, -91.91) * mm});
            skPoint(sketch, "E103.16.16", {"position": v(44.02, -93.18) * mm});
            skPoint(sketch, "E103.16.17", {"position": v(43.02, -94.91) * mm});
            skArc(sketch, "E103.16.18", {"start": v(42.16, -94.41) * mm, "mid": v(42.91, -94.51) * mm, "end": v(43.52, -94.04) * mm});
            skArc(sketch, "E103.16.19", {"start": v(43.52, -94.04) * mm, "mid": v(43.62, -93.29) * mm, "end": v(43.16, -92.68) * mm});
            skArc(sketch, "E103.16.20", {"start": v(42.16, -94.41) * mm, "mid": v(42.91, -94.51) * mm, "end": v(43.52, -94.04) * mm});
            skArc(sketch, "E103.16.21", {"start": v(43.52, -94.04) * mm, "mid": v(43.62, -93.29) * mm, "end": v(43.16, -92.68) * mm});
            skPoint(sketch, "E103.17.0", {"position": v(38.92, -87.35) * mm});
            skPoint(sketch, "E103.17.1", {"position": v(42.56, -87.3) * mm});
            skPoint(sketch, "E103.17.2", {"position": v(39.44, -85.42) * mm});
            skLineSegment(sketch, "E103.17.3", {"start": v(39.89, -87.6) * mm, "end": v(44.72, -88.9) * mm});
            skLineSegment(sketch, "E103.17.4", {"start": v(40.4, -85.68) * mm, "end": v(45.24, -86.97) * mm});
            skPoint(sketch, "E103.17.5", {"position": v(38.92, -87.35) * mm});
            skPoint(sketch, "E103.17.6", {"position": v(42.56, -87.3) * mm});
            skPoint(sketch, "E103.17.7", {"position": v(39.44, -85.42) * mm});
            skLineSegment(sketch, "E103.17.8", {"start": v(39.89, -87.6) * mm, "end": v(44.72, -88.9) * mm});
            skLineSegment(sketch, "E103.17.9", {"start": v(40.4, -85.68) * mm, "end": v(45.24, -86.97) * mm});
            skArc(sketch, "E103.17.10", {"start": v(40.4, -85.68) * mm, "mid": v(39.65, -85.78) * mm, "end": v(39.18, -86.38) * mm});
            skPoint(sketch, "E103.17.11", {"position": v(46.2, -87.23) * mm});
            skArc(sketch, "E103.17.12", {"start": v(39.18, -86.38) * mm, "mid": v(39.28, -87.14) * mm, "end": v(39.89, -87.6) * mm});
            skPoint(sketch, "E103.17.13", {"position": v(45.68, -89.16) * mm});
            skArc(sketch, "E103.17.14", {"start": v(40.4, -85.68) * mm, "mid": v(39.65, -85.78) * mm, "end": v(39.18, -86.38) * mm});
            skArc(sketch, "E103.17.15", {"start": v(39.18, -86.38) * mm, "mid": v(39.28, -87.14) * mm, "end": v(39.89, -87.6) * mm});
            skPoint(sketch, "E103.17.16", {"position": v(46.2, -87.23) * mm});
            skPoint(sketch, "E103.17.17", {"position": v(45.68, -89.16) * mm});
            skArc(sketch, "E103.17.18", {"start": v(44.72, -88.9) * mm, "mid": v(45.48, -88.8) * mm, "end": v(45.94, -88.2) * mm});
            skArc(sketch, "E103.17.19", {"start": v(45.94, -88.2) * mm, "mid": v(45.84, -87.44) * mm, "end": v(45.24, -86.97) * mm});
            skArc(sketch, "E103.17.20", {"start": v(44.72, -88.9) * mm, "mid": v(45.48, -88.8) * mm, "end": v(45.94, -88.2) * mm});
            skArc(sketch, "E103.17.21", {"start": v(45.94, -88.2) * mm, "mid": v(45.84, -87.44) * mm, "end": v(45.24, -86.97) * mm});
            skPoint(sketch, "E103.18.0", {"position": v(39.77, -82.92) * mm});
            skPoint(sketch, "E103.18.1", {"position": v(43.27, -81.92) * mm});
            skPoint(sketch, "E103.18.2", {"position": v(39.77, -80.92) * mm});
            skLineSegment(sketch, "E103.18.3", {"start": v(40.77, -82.92) * mm, "end": v(45.77, -82.92) * mm});
            skLineSegment(sketch, "E103.18.4", {"start": v(40.77, -80.92) * mm, "end": v(45.77, -80.92) * mm});
            skPoint(sketch, "E103.18.5", {"position": v(39.77, -82.92) * mm});
            skPoint(sketch, "E103.18.6", {"position": v(43.27, -81.92) * mm});
            skPoint(sketch, "E103.18.7", {"position": v(39.77, -80.92) * mm});
            skLineSegment(sketch, "E103.18.8", {"start": v(40.77, -82.92) * mm, "end": v(45.77, -82.92) * mm});
            skLineSegment(sketch, "E103.18.9", {"start": v(40.77, -80.92) * mm, "end": v(45.77, -80.92) * mm});
            skArc(sketch, "E103.18.10", {"start": v(40.77, -80.92) * mm, "mid": v(40.06, -81.21) * mm, "end": v(39.77, -81.92) * mm});
            skPoint(sketch, "E103.18.11", {"position": v(46.77, -80.92) * mm});
            skArc(sketch, "E103.18.12", {"start": v(39.77, -81.92) * mm, "mid": v(40.06, -82.63) * mm, "end": v(40.77, -82.92) * mm});
            skPoint(sketch, "E103.18.13", {"position": v(46.77, -82.92) * mm});
            skArc(sketch, "E103.18.14", {"start": v(40.77, -80.92) * mm, "mid": v(40.06, -81.21) * mm, "end": v(39.77, -81.92) * mm});
            skArc(sketch, "E103.18.15", {"start": v(39.77, -81.92) * mm, "mid": v(40.06, -82.63) * mm, "end": v(40.77, -82.92) * mm});
            skPoint(sketch, "E103.18.16", {"position": v(46.77, -80.92) * mm});
            skPoint(sketch, "E103.18.17", {"position": v(46.77, -82.92) * mm});
            skArc(sketch, "E103.18.18", {"start": v(45.77, -82.92) * mm, "mid": v(46.48, -82.63) * mm, "end": v(46.77, -81.92) * mm});
            skArc(sketch, "E103.18.19", {"start": v(46.77, -81.92) * mm, "mid": v(46.48, -81.21) * mm, "end": v(45.77, -80.92) * mm});
            skArc(sketch, "E103.18.20", {"start": v(45.77, -82.92) * mm, "mid": v(46.48, -82.63) * mm, "end": v(46.77, -81.92) * mm});
            skArc(sketch, "E103.18.21", {"start": v(46.77, -81.92) * mm, "mid": v(46.48, -81.21) * mm, "end": v(45.77, -80.92) * mm});
            skPoint(sketch, "E103.19.0", {"position": v(39.44, -78.42) * mm});
            skPoint(sketch, "E103.19.1", {"position": v(42.56, -76.55) * mm});
            skPoint(sketch, "E103.19.2", {"position": v(38.92, -76.49) * mm});
            skLineSegment(sketch, "E103.19.3", {"start": v(40.4, -78.16) * mm, "end": v(45.24, -76.87) * mm});
            skLineSegment(sketch, "E103.19.4", {"start": v(39.89, -76.23) * mm, "end": v(44.72, -74.94) * mm});
            skPoint(sketch, "E103.19.5", {"position": v(39.44, -78.42) * mm});
            skPoint(sketch, "E103.19.6", {"position": v(42.56, -76.55) * mm});
            skPoint(sketch, "E103.19.7", {"position": v(38.92, -76.49) * mm});
            skLineSegment(sketch, "E103.19.8", {"start": v(40.4, -78.16) * mm, "end": v(45.24, -76.87) * mm});
            skLineSegment(sketch, "E103.19.9", {"start": v(39.89, -76.23) * mm, "end": v(44.72, -74.94) * mm});
            skArc(sketch, "E103.19.10", {"start": v(39.89, -76.23) * mm, "mid": v(39.28, -76.7) * mm, "end": v(39.18, -77.46) * mm});
            skPoint(sketch, "E103.19.11", {"position": v(45.68, -74.68) * mm});
            skArc(sketch, "E103.19.12", {"start": v(39.18, -77.46) * mm, "mid": v(39.65, -78.06) * mm, "end": v(40.4, -78.16) * mm});
            skPoint(sketch, "E103.19.13", {"position": v(46.2, -76.6) * mm});
            skArc(sketch, "E103.19.14", {"start": v(39.89, -76.23) * mm, "mid": v(39.28, -76.7) * mm, "end": v(39.18, -77.46) * mm});
            skArc(sketch, "E103.19.15", {"start": v(39.18, -77.46) * mm, "mid": v(39.65, -78.06) * mm, "end": v(40.4, -78.16) * mm});
            skPoint(sketch, "E103.19.16", {"position": v(45.68, -74.68) * mm});
            skPoint(sketch, "E103.19.17", {"position": v(46.2, -76.6) * mm});
            skArc(sketch, "E103.19.18", {"start": v(45.24, -76.87) * mm, "mid": v(45.84, -76.4) * mm, "end": v(45.94, -75.64) * mm});
            skArc(sketch, "E103.19.19", {"start": v(45.94, -75.64) * mm, "mid": v(45.48, -75.04) * mm, "end": v(44.72, -74.94) * mm});
            skArc(sketch, "E103.19.20", {"start": v(45.24, -76.87) * mm, "mid": v(45.84, -76.4) * mm, "end": v(45.94, -75.64) * mm});
            skArc(sketch, "E103.19.21", {"start": v(45.94, -75.64) * mm, "mid": v(45.48, -75.04) * mm, "end": v(44.72, -74.94) * mm});
            skPoint(sketch, "E103.20.0", {"position": v(37.96, -74.16) * mm});
            skPoint(sketch, "E103.20.1", {"position": v(40.5, -71.54) * mm});
            skPoint(sketch, "E103.20.2", {"position": v(36.96, -72.43) * mm});
            skLineSegment(sketch, "E103.20.3", {"start": v(38.82, -73.66) * mm, "end": v(43.16, -71.16) * mm});
            skLineSegment(sketch, "E103.20.4", {"start": v(37.82, -71.93) * mm, "end": v(42.16, -69.43) * mm});
            skPoint(sketch, "E103.20.5", {"position": v(37.96, -74.16) * mm});
            skPoint(sketch, "E103.20.6", {"position": v(40.5, -71.54) * mm});
            skPoint(sketch, "E103.20.7", {"position": v(36.96, -72.43) * mm});
            skLineSegment(sketch, "E103.20.8", {"start": v(38.82, -73.66) * mm, "end": v(43.16, -71.16) * mm});
            skLineSegment(sketch, "E103.20.9", {"start": v(37.82, -71.93) * mm, "end": v(42.16, -69.43) * mm});
            skArc(sketch, "E103.20.10", {"start": v(37.82, -71.93) * mm, "mid": v(37.36, -72.54) * mm, "end": v(37.46, -73.3) * mm});
            skPoint(sketch, "E103.20.11", {"position": v(43.02, -68.93) * mm});
            skArc(sketch, "E103.20.12", {"start": v(37.46, -73.3) * mm, "mid": v(38.07, -73.76) * mm, "end": v(38.82, -73.66) * mm});
            skPoint(sketch, "E103.20.13", {"position": v(44.02, -70.66) * mm});
            skArc(sketch, "E103.20.14", {"start": v(37.82, -71.93) * mm, "mid": v(37.36, -72.54) * mm, "end": v(37.46, -73.3) * mm});
            skArc(sketch, "E103.20.15", {"start": v(37.46, -73.3) * mm, "mid": v(38.07, -73.76) * mm, "end": v(38.82, -73.66) * mm});
            skPoint(sketch, "E103.20.16", {"position": v(43.02, -68.93) * mm});
            skPoint(sketch, "E103.20.17", {"position": v(44.02, -70.66) * mm});
            skArc(sketch, "E103.20.18", {"start": v(43.16, -71.16) * mm, "mid": v(43.62, -70.55) * mm, "end": v(43.52, -69.8) * mm});
            skArc(sketch, "E103.20.19", {"start": v(43.52, -69.8) * mm, "mid": v(42.91, -69.33) * mm, "end": v(42.16, -69.43) * mm});
            skArc(sketch, "E103.20.20", {"start": v(43.16, -71.16) * mm, "mid": v(43.62, -70.55) * mm, "end": v(43.52, -69.8) * mm});
            skArc(sketch, "E103.20.21", {"start": v(43.52, -69.8) * mm, "mid": v(42.91, -69.33) * mm, "end": v(42.16, -69.43) * mm});
            skPoint(sketch, "E103.21.0", {"position": v(35.42, -70.43) * mm});
            skPoint(sketch, "E103.21.1", {"position": v(37.2, -67.25) * mm});
            skPoint(sketch, "E103.21.2", {"position": v(34.01, -69.02) * mm});
            skLineSegment(sketch, "E103.21.3", {"start": v(36.13, -69.72) * mm, "end": v(39.67, -66.19) * mm});
            skLineSegment(sketch, "E103.21.4", {"start": v(34.72, -68.3) * mm, "end": v(38.25, -64.77) * mm});
            skPoint(sketch, "E103.21.5", {"position": v(35.42, -70.43) * mm});
            skPoint(sketch, "E103.21.6", {"position": v(37.2, -67.25) * mm});
            skPoint(sketch, "E103.21.7", {"position": v(34.01, -69.02) * mm});
            skLineSegment(sketch, "E103.21.8", {"start": v(36.13, -69.72) * mm, "end": v(39.67, -66.19) * mm});
            skLineSegment(sketch, "E103.21.9", {"start": v(34.72, -68.3) * mm, "end": v(38.25, -64.77) * mm});
            skArc(sketch, "E103.21.10", {"start": v(34.72, -68.3) * mm, "mid": v(34.42, -69.02) * mm, "end": v(34.72, -69.72) * mm});
            skPoint(sketch, "E103.21.11", {"position": v(38.96, -64.07) * mm});
            skArc(sketch, "E103.21.12", {"start": v(34.72, -69.72) * mm, "mid": v(35.42, -70.02) * mm, "end": v(36.13, -69.72) * mm});
            skPoint(sketch, "E103.21.13", {"position": v(40.37, -65.48) * mm});
            skArc(sketch, "E103.21.14", {"start": v(34.72, -68.3) * mm, "mid": v(34.42, -69.02) * mm, "end": v(34.72, -69.72) * mm});
            skArc(sketch, "E103.21.15", {"start": v(34.72, -69.72) * mm, "mid": v(35.42, -70.02) * mm, "end": v(36.13, -69.72) * mm});
            skPoint(sketch, "E103.21.16", {"position": v(38.96, -64.07) * mm});
            skPoint(sketch, "E103.21.17", {"position": v(40.37, -65.48) * mm});
            skArc(sketch, "E103.21.18", {"start": v(39.67, -66.19) * mm, "mid": v(39.96, -65.48) * mm, "end": v(39.67, -64.77) * mm});
            skArc(sketch, "E103.21.19", {"start": v(39.67, -64.77) * mm, "mid": v(38.96, -64.48) * mm, "end": v(38.25, -64.77) * mm});
            skArc(sketch, "E103.21.20", {"start": v(39.67, -66.19) * mm, "mid": v(39.96, -65.48) * mm, "end": v(39.67, -64.77) * mm});
            skArc(sketch, "E103.21.21", {"start": v(39.67, -64.77) * mm, "mid": v(38.96, -64.48) * mm, "end": v(38.25, -64.77) * mm});
            skPoint(sketch, "E103.22.0", {"position": v(32.01, -67.48) * mm});
            skPoint(sketch, "E103.22.1", {"position": v(32.9, -63.95) * mm});
            skPoint(sketch, "E103.22.2", {"position": v(30.28, -66.48) * mm});
            skLineSegment(sketch, "E103.22.3", {"start": v(32.51, -66.62) * mm, "end": v(35.01, -62.28) * mm});
            skLineSegment(sketch, "E103.22.4", {"start": v(30.78, -65.62) * mm, "end": v(33.28, -61.28) * mm});
            skPoint(sketch, "E103.22.5", {"position": v(32.01, -67.48) * mm});
            skPoint(sketch, "E103.22.6", {"position": v(32.9, -63.95) * mm});
            skPoint(sketch, "E103.22.7", {"position": v(30.28, -66.48) * mm});
            skLineSegment(sketch, "E103.22.8", {"start": v(32.51, -66.62) * mm, "end": v(35.01, -62.28) * mm});
            skLineSegment(sketch, "E103.22.9", {"start": v(30.78, -65.62) * mm, "end": v(33.28, -61.28) * mm});
            skArc(sketch, "E103.22.10", {"start": v(30.78, -65.62) * mm, "mid": v(30.68, -66.37) * mm, "end": v(31.14, -66.98) * mm});
            skPoint(sketch, "E103.22.11", {"position": v(33.78, -60.42) * mm});
            skArc(sketch, "E103.22.12", {"start": v(31.14, -66.98) * mm, "mid": v(31.9, -67.08) * mm, "end": v(32.51, -66.62) * mm});
            skPoint(sketch, "E103.22.13", {"position": v(35.51, -61.42) * mm});
            skArc(sketch, "E103.22.14", {"start": v(30.78, -65.62) * mm, "mid": v(30.68, -66.37) * mm, "end": v(31.14, -66.98) * mm});
            skArc(sketch, "E103.22.15", {"start": v(31.14, -66.98) * mm, "mid": v(31.9, -67.08) * mm, "end": v(32.51, -66.62) * mm});
            skPoint(sketch, "E103.22.16", {"position": v(33.78, -60.42) * mm});
            skPoint(sketch, "E103.22.17", {"position": v(35.51, -61.42) * mm});
            skArc(sketch, "E103.22.18", {"start": v(35.01, -62.28) * mm, "mid": v(35.11, -61.53) * mm, "end": v(34.64, -60.92) * mm});
            skArc(sketch, "E103.22.19", {"start": v(34.64, -60.92) * mm, "mid": v(33.89, -60.82) * mm, "end": v(33.28, -61.28) * mm});
            skArc(sketch, "E103.22.20", {"start": v(35.01, -62.28) * mm, "mid": v(35.11, -61.53) * mm, "end": v(34.64, -60.92) * mm});
            skArc(sketch, "E103.22.21", {"start": v(34.64, -60.92) * mm, "mid": v(33.89, -60.82) * mm, "end": v(33.28, -61.28) * mm});
            skPoint(sketch, "E103.23.0", {"position": v(27.95, -65.52) * mm});
            skPoint(sketch, "E103.23.1", {"position": v(27.9, -61.88) * mm});
            skPoint(sketch, "E103.23.2", {"position": v(26.02, -65) * mm});
            skLineSegment(sketch, "E103.23.3", {"start": v(28.2, -64.55) * mm, "end": v(29.5, -59.72) * mm});
            skLineSegment(sketch, "E103.23.4", {"start": v(26.28, -64.03) * mm, "end": v(27.57, -59.2) * mm});
            skPoint(sketch, "E103.23.5", {"position": v(27.95, -65.52) * mm});
            skPoint(sketch, "E103.23.6", {"position": v(27.9, -61.88) * mm});
            skPoint(sketch, "E103.23.7", {"position": v(26.02, -65) * mm});
            skLineSegment(sketch, "E103.23.8", {"start": v(28.2, -64.55) * mm, "end": v(29.5, -59.72) * mm});
            skLineSegment(sketch, "E103.23.9", {"start": v(26.28, -64.03) * mm, "end": v(27.57, -59.2) * mm});
            skArc(sketch, "E103.23.10", {"start": v(26.28, -64.03) * mm, "mid": v(26.38, -64.8) * mm, "end": v(26.98, -65.26) * mm});
            skPoint(sketch, "E103.23.11", {"position": v(27.83, -58.24) * mm});
            skArc(sketch, "E103.23.12", {"start": v(26.98, -65.26) * mm, "mid": v(27.74, -65.16) * mm, "end": v(28.2, -64.55) * mm});
            skPoint(sketch, "E103.23.13", {"position": v(29.76, -58.76) * mm});
            skArc(sketch, "E103.23.14", {"start": v(26.28, -64.03) * mm, "mid": v(26.38, -64.8) * mm, "end": v(26.98, -65.26) * mm});
            skArc(sketch, "E103.23.15", {"start": v(26.98, -65.26) * mm, "mid": v(27.74, -65.16) * mm, "end": v(28.2, -64.55) * mm});
            skPoint(sketch, "E103.23.16", {"position": v(27.83, -58.24) * mm});
            skPoint(sketch, "E103.23.17", {"position": v(29.76, -58.76) * mm});
            skArc(sketch, "E103.23.18", {"start": v(29.5, -59.72) * mm, "mid": v(29.4, -58.96) * mm, "end": v(28.8, -58.5) * mm});
            skArc(sketch, "E103.23.19", {"start": v(28.8, -58.5) * mm, "mid": v(28.04, -58.6) * mm, "end": v(27.57, -59.2) * mm});
            skArc(sketch, "E103.23.20", {"start": v(29.5, -59.72) * mm, "mid": v(29.4, -58.96) * mm, "end": v(28.8, -58.5) * mm});
            skArc(sketch, "E103.23.21", {"start": v(28.8, -58.5) * mm, "mid": v(28.04, -58.6) * mm, "end": v(27.57, -59.2) * mm});
            skLineSegment(sketch, "E104.1.0", {"start": v(-31.43, -45.5) * mm, "end": v(-32.72, -40.66) * mm});
            skLineSegment(sketch, "E104.1.1", {"start": v(-29.5, -44.97) * mm, "end": v(-30.8, -40.14) * mm});
            skPoint(sketch, "E104.1.2", {"position": v(-31.17, -46.46) * mm});
            skPoint(sketch, "E104.1.3", {"position": v(-31.11, -42.82) * mm});
            skPoint(sketch, "E104.1.4", {"position": v(-29.24, -45.94) * mm});
            skArc(sketch, "E104.1.5", {"start": v(-30.2, -46.2) * mm, "mid": v(-29.6, -45.73) * mm, "end": v(-29.5, -44.97) * mm});
            skArc(sketch, "E104.1.6", {"start": v(-31.43, -45.5) * mm, "mid": v(-30.96, -46.1) * mm, "end": v(-30.2, -46.2) * mm});
            skPoint(sketch, "E104.1.7", {"position": v(-32.98, -39.7) * mm});
            skPoint(sketch, "E104.1.8", {"position": v(-31.05, -39.18) * mm});
            skArc(sketch, "E104.1.9", {"start": v(-30.8, -40.14) * mm, "mid": v(-31.26, -39.54) * mm, "end": v(-32.02, -39.44) * mm});
            skArc(sketch, "E104.1.10", {"start": v(-32.02, -39.44) * mm, "mid": v(-32.62, -39.9) * mm, "end": v(-32.72, -40.66) * mm});
            skLineSegment(sketch, "E104.2.0", {"start": v(-35.73, -47.56) * mm, "end": v(-38.23, -43.22) * mm});
            skLineSegment(sketch, "E104.2.1", {"start": v(-34, -46.56) * mm, "end": v(-36.5, -42.22) * mm});
            skPoint(sketch, "E104.2.2", {"position": v(-35.23, -48.42) * mm});
            skPoint(sketch, "E104.2.3", {"position": v(-36.12, -44.89) * mm});
            skPoint(sketch, "E104.2.4", {"position": v(-33.5, -47.42) * mm});
            skArc(sketch, "E104.2.5", {"start": v(-34.37, -47.92) * mm, "mid": v(-33.9, -47.31) * mm, "end": v(-34, -46.56) * mm});
            skArc(sketch, "E104.2.6", {"start": v(-35.73, -47.56) * mm, "mid": v(-35.12, -48.02) * mm, "end": v(-34.37, -47.92) * mm});
            skPoint(sketch, "E104.2.7", {"position": v(-38.73, -42.36) * mm});
            skPoint(sketch, "E104.2.8", {"position": v(-37, -41.36) * mm});
            skArc(sketch, "E104.2.9", {"start": v(-36.5, -42.22) * mm, "mid": v(-37.1, -41.76) * mm, "end": v(-37.87, -41.86) * mm});
            skArc(sketch, "E104.2.10", {"start": v(-37.87, -41.86) * mm, "mid": v(-38.33, -42.47) * mm, "end": v(-38.23, -43.22) * mm});
            skLineSegment(sketch, "E104.3.0", {"start": v(-39.35, -50.66) * mm, "end": v(-42.89, -47.13) * mm});
            skLineSegment(sketch, "E104.3.1", {"start": v(-37.94, -49.25) * mm, "end": v(-41.47, -45.71) * mm});
            skPoint(sketch, "E104.3.2", {"position": v(-38.64, -51.37) * mm});
            skPoint(sketch, "E104.3.3", {"position": v(-40.41, -48.19) * mm});
            skPoint(sketch, "E104.3.4", {"position": v(-37.23, -49.96) * mm});
            skArc(sketch, "E104.3.5", {"start": v(-37.94, -50.66) * mm, "mid": v(-37.64, -49.96) * mm, "end": v(-37.94, -49.25) * mm});
            skArc(sketch, "E104.3.6", {"start": v(-39.35, -50.66) * mm, "mid": v(-38.64, -50.96) * mm, "end": v(-37.94, -50.66) * mm});
            skPoint(sketch, "E104.3.7", {"position": v(-43.6, -46.42) * mm});
            skPoint(sketch, "E104.3.8", {"position": v(-42.18, -45) * mm});
            skArc(sketch, "E104.3.9", {"start": v(-41.47, -45.71) * mm, "mid": v(-42.18, -45.42) * mm, "end": v(-42.89, -45.71) * mm});
            skArc(sketch, "E104.3.10", {"start": v(-42.89, -45.71) * mm, "mid": v(-43.18, -46.42) * mm, "end": v(-42.89, -47.13) * mm});
            skLineSegment(sketch, "E104.4.0", {"start": v(-42.04, -54.6) * mm, "end": v(-46.38, -52.1) * mm});
            skLineSegment(sketch, "E104.4.1", {"start": v(-41.04, -52.87) * mm, "end": v(-45.38, -50.37) * mm});
            skPoint(sketch, "E104.4.2", {"position": v(-41.18, -55.1) * mm});
            skPoint(sketch, "E104.4.3", {"position": v(-43.71, -52.49) * mm});
            skPoint(sketch, "E104.4.4", {"position": v(-40.18, -53.37) * mm});
            skArc(sketch, "E104.4.5", {"start": v(-40.68, -54.24) * mm, "mid": v(-40.58, -53.48) * mm, "end": v(-41.04, -52.87) * mm});
            skArc(sketch, "E104.4.6", {"start": v(-42.04, -54.6) * mm, "mid": v(-41.29, -54.7) * mm, "end": v(-40.68, -54.24) * mm});
            skPoint(sketch, "E104.4.7", {"position": v(-47.24, -51.6) * mm});
            skPoint(sketch, "E104.4.8", {"position": v(-46.24, -49.87) * mm});
            skArc(sketch, "E104.4.9", {"start": v(-45.38, -50.37) * mm, "mid": v(-46.13, -50.27) * mm, "end": v(-46.74, -50.74) * mm});
            skArc(sketch, "E104.4.10", {"start": v(-46.74, -50.74) * mm, "mid": v(-46.84, -51.5) * mm, "end": v(-46.38, -52.1) * mm});
            skLineSegment(sketch, "E104.5.0", {"start": v(-43.63, -59.1) * mm, "end": v(-48.46, -57.8) * mm});
            skLineSegment(sketch, "E104.5.1", {"start": v(-43.1, -57.17) * mm, "end": v(-47.94, -55.88) * mm});
            skPoint(sketch, "E104.5.2", {"position": v(-42.66, -59.36) * mm});
            skPoint(sketch, "E104.5.3", {"position": v(-45.78, -57.49) * mm});
            skPoint(sketch, "E104.5.4", {"position": v(-42.14, -57.43) * mm});
            skArc(sketch, "E104.5.5", {"start": v(-42.4, -58.4) * mm, "mid": v(-42.5, -57.64) * mm, "end": v(-43.1, -57.17) * mm});
            skArc(sketch, "E104.5.6", {"start": v(-43.63, -59.1) * mm, "mid": v(-42.87, -59) * mm, "end": v(-42.4, -58.4) * mm});
            skPoint(sketch, "E104.5.7", {"position": v(-49.42, -57.55) * mm});
            skPoint(sketch, "E104.5.8", {"position": v(-48.9, -55.62) * mm});
            skArc(sketch, "E104.5.9", {"start": v(-47.94, -55.88) * mm, "mid": v(-48.7, -55.98) * mm, "end": v(-49.16, -56.58) * mm});
            skArc(sketch, "E104.5.10", {"start": v(-49.16, -56.58) * mm, "mid": v(-49.06, -57.34) * mm, "end": v(-48.46, -57.8) * mm});
            skLineSegment(sketch, "E104.6.0", {"start": v(-43.99, -63.86) * mm, "end": v(-48.99, -63.86) * mm});
            skLineSegment(sketch, "E104.6.1", {"start": v(-43.99, -61.86) * mm, "end": v(-48.99, -61.86) * mm});
            skPoint(sketch, "E104.6.2", {"position": v(-42.99, -63.86) * mm});
            skPoint(sketch, "E104.6.3", {"position": v(-46.49, -62.86) * mm});
            skPoint(sketch, "E104.6.4", {"position": v(-42.99, -61.86) * mm});
            skArc(sketch, "E104.6.5", {"start": v(-42.99, -62.86) * mm, "mid": v(-43.28, -62.15) * mm, "end": v(-43.99, -61.86) * mm});
            skArc(sketch, "E104.6.6", {"start": v(-43.99, -63.86) * mm, "mid": v(-43.28, -63.57) * mm, "end": v(-42.99, -62.86) * mm});
            skPoint(sketch, "E104.6.7", {"position": v(-49.99, -63.86) * mm});
            skPoint(sketch, "E104.6.8", {"position": v(-49.99, -61.86) * mm});
            skArc(sketch, "E104.6.9", {"start": v(-48.99, -61.86) * mm, "mid": v(-49.7, -62.15) * mm, "end": v(-49.99, -62.86) * mm});
            skArc(sketch, "E104.6.10", {"start": v(-49.99, -62.86) * mm, "mid": v(-49.7, -63.57) * mm, "end": v(-48.99, -63.86) * mm});
            skLineSegment(sketch, "E104.7.0", {"start": v(-43.1, -68.55) * mm, "end": v(-47.94, -69.84) * mm});
            skLineSegment(sketch, "E104.7.1", {"start": v(-43.63, -66.62) * mm, "end": v(-48.46, -67.91) * mm});
            skPoint(sketch, "E104.7.2", {"position": v(-42.14, -68.3) * mm});
            skPoint(sketch, "E104.7.3", {"position": v(-45.78, -68.23) * mm});
            skPoint(sketch, "E104.7.4", {"position": v(-42.66, -66.36) * mm});
            skArc(sketch, "E104.7.5", {"start": v(-42.4, -67.32) * mm, "mid": v(-42.87, -66.72) * mm, "end": v(-43.63, -66.62) * mm});
            skArc(sketch, "E104.7.6", {"start": v(-43.1, -68.55) * mm, "mid": v(-42.5, -68.08) * mm, "end": v(-42.4, -67.32) * mm});
            skPoint(sketch, "E104.7.7", {"position": v(-48.9, -70.1) * mm});
            skPoint(sketch, "E104.7.8", {"position": v(-49.42, -68.17) * mm});
            skArc(sketch, "E104.7.9", {"start": v(-48.46, -67.91) * mm, "mid": v(-49.06, -68.38) * mm, "end": v(-49.16, -69.14) * mm});
            skArc(sketch, "E104.7.10", {"start": v(-49.16, -69.14) * mm, "mid": v(-48.7, -69.74) * mm, "end": v(-47.94, -69.84) * mm});
            skLineSegment(sketch, "E104.8.0", {"start": v(-41.04, -72.85) * mm, "end": v(-45.38, -75.35) * mm});
            skLineSegment(sketch, "E104.8.1", {"start": v(-42.04, -71.12) * mm, "end": v(-46.38, -73.62) * mm});
            skPoint(sketch, "E104.8.2", {"position": v(-40.18, -72.35) * mm});
            skPoint(sketch, "E104.8.3", {"position": v(-43.71, -73.24) * mm});
            skPoint(sketch, "E104.8.4", {"position": v(-41.18, -70.62) * mm});
            skArc(sketch, "E104.8.5", {"start": v(-40.68, -71.49) * mm, "mid": v(-41.29, -71.02) * mm, "end": v(-42.04, -71.12) * mm});
            skArc(sketch, "E104.8.6", {"start": v(-41.04, -72.85) * mm, "mid": v(-40.58, -72.24) * mm, "end": v(-40.68, -71.49) * mm});
            skPoint(sketch, "E104.8.7", {"position": v(-46.24, -75.85) * mm});
            skPoint(sketch, "E104.8.8", {"position": v(-47.24, -74.12) * mm});
            skArc(sketch, "E104.8.9", {"start": v(-46.38, -73.62) * mm, "mid": v(-46.84, -74.23) * mm, "end": v(-46.74, -74.99) * mm});
            skArc(sketch, "E104.8.10", {"start": v(-46.74, -74.99) * mm, "mid": v(-46.13, -75.45) * mm, "end": v(-45.38, -75.35) * mm});
            skLineSegment(sketch, "E104.9.0", {"start": v(-37.94, -76.47) * mm, "end": v(-41.47, -80) * mm});
            skLineSegment(sketch, "E104.9.1", {"start": v(-39.35, -75.06) * mm, "end": v(-42.89, -78.6) * mm});
            skPoint(sketch, "E104.9.2", {"position": v(-37.23, -75.76) * mm});
            skPoint(sketch, "E104.9.3", {"position": v(-40.41, -77.53) * mm});
            skPoint(sketch, "E104.9.4", {"position": v(-38.64, -74.35) * mm});
            skArc(sketch, "E104.9.5", {"start": v(-37.94, -75.06) * mm, "mid": v(-38.64, -74.76) * mm, "end": v(-39.35, -75.06) * mm});
            skArc(sketch, "E104.9.6", {"start": v(-37.94, -76.47) * mm, "mid": v(-37.64, -75.76) * mm, "end": v(-37.94, -75.06) * mm});
            skPoint(sketch, "E104.9.7", {"position": v(-42.18, -80.71) * mm});
            skPoint(sketch, "E104.9.8", {"position": v(-43.6, -79.3) * mm});
            skArc(sketch, "E104.9.9", {"start": v(-42.89, -78.6) * mm, "mid": v(-43.18, -79.3) * mm, "end": v(-42.89, -80) * mm});
            skArc(sketch, "E104.9.10", {"start": v(-42.89, -80) * mm, "mid": v(-42.18, -80.3) * mm, "end": v(-41.47, -80) * mm});
            skLineSegment(sketch, "E104.10.0", {"start": v(-34, -79.16) * mm, "end": v(-36.5, -83.5) * mm});
            skLineSegment(sketch, "E104.10.1", {"start": v(-35.73, -78.16) * mm, "end": v(-38.23, -82.5) * mm});
            skPoint(sketch, "E104.10.2", {"position": v(-33.5, -78.3) * mm});
            skPoint(sketch, "E104.10.3", {"position": v(-36.11, -80.83) * mm});
            skPoint(sketch, "E104.10.4", {"position": v(-35.23, -77.3) * mm});
            skArc(sketch, "E104.10.5", {"start": v(-34.36, -77.8) * mm, "mid": v(-35.12, -77.7) * mm, "end": v(-35.73, -78.16) * mm});
            skArc(sketch, "E104.10.6", {"start": v(-34, -79.16) * mm, "mid": v(-33.9, -78.4) * mm, "end": v(-34.36, -77.8) * mm});
            skPoint(sketch, "E104.10.7", {"position": v(-37, -84.36) * mm});
            skPoint(sketch, "E104.10.8", {"position": v(-38.73, -83.36) * mm});
            skArc(sketch, "E104.10.9", {"start": v(-38.23, -82.5) * mm, "mid": v(-38.33, -83.25) * mm, "end": v(-37.86, -83.86) * mm});
            skArc(sketch, "E104.10.10", {"start": v(-37.86, -83.86) * mm, "mid": v(-37.1, -83.96) * mm, "end": v(-36.5, -83.5) * mm});
            skLineSegment(sketch, "E104.11.0", {"start": v(-29.5, -80.75) * mm, "end": v(-30.8, -85.58) * mm});
            skLineSegment(sketch, "E104.11.1", {"start": v(-31.43, -80.23) * mm, "end": v(-32.72, -85.06) * mm});
            skPoint(sketch, "E104.11.2", {"position": v(-29.24, -79.78) * mm});
            skPoint(sketch, "E104.11.3", {"position": v(-31.11, -82.9) * mm});
            skPoint(sketch, "E104.11.4", {"position": v(-31.17, -79.26) * mm});
            skArc(sketch, "E104.11.5", {"start": v(-30.2, -79.52) * mm, "mid": v(-30.96, -79.62) * mm, "end": v(-31.43, -80.23) * mm});
            skArc(sketch, "E104.11.6", {"start": v(-29.5, -80.75) * mm, "mid": v(-29.6, -79.99) * mm, "end": v(-30.2, -79.52) * mm});
            skPoint(sketch, "E104.11.7", {"position": v(-31.05, -86.54) * mm});
            skPoint(sketch, "E104.11.8", {"position": v(-32.98, -86.02) * mm});
            skArc(sketch, "E104.11.9", {"start": v(-32.72, -85.06) * mm, "mid": v(-32.62, -85.82) * mm, "end": v(-32.02, -86.28) * mm});
            skArc(sketch, "E104.11.10", {"start": v(-32.02, -86.28) * mm, "mid": v(-31.26, -86.18) * mm, "end": v(-30.8, -85.58) * mm});
            skLineSegment(sketch, "E104.12.0", {"start": v(-24.74, -81.1) * mm, "end": v(-24.74, -86.1) * mm});
            skLineSegment(sketch, "E104.12.1", {"start": v(-26.74, -81.11) * mm, "end": v(-26.74, -86.11) * mm});
            skPoint(sketch, "E104.12.2", {"position": v(-24.74, -80.11) * mm});
            skPoint(sketch, "E104.12.3", {"position": v(-25.74, -83.6) * mm});
            skPoint(sketch, "E104.12.4", {"position": v(-26.74, -80.11) * mm});
            skArc(sketch, "E104.12.5", {"start": v(-25.74, -80.1) * mm, "mid": v(-26.45, -80.4) * mm, "end": v(-26.74, -81.11) * mm});
            skArc(sketch, "E104.12.6", {"start": v(-24.74, -81.11) * mm, "mid": v(-25.03, -80.4) * mm, "end": v(-25.74, -80.1) * mm});
            skPoint(sketch, "E104.12.7", {"position": v(-24.74, -87.11) * mm});
            skPoint(sketch, "E104.12.8", {"position": v(-26.74, -87.11) * mm});
            skArc(sketch, "E104.12.9", {"start": v(-26.74, -86.1) * mm, "mid": v(-26.45, -86.82) * mm, "end": v(-25.74, -87.11) * mm});
            skArc(sketch, "E104.12.10", {"start": v(-25.74, -87.11) * mm, "mid": v(-25.03, -86.82) * mm, "end": v(-24.74, -86.1) * mm});
            skLineSegment(sketch, "E104.13.0", {"start": v(-20.05, -80.23) * mm, "end": v(-18.76, -85.06) * mm});
            skLineSegment(sketch, "E104.13.1", {"start": v(-21.98, -80.75) * mm, "end": v(-20.69, -85.58) * mm});
            skPoint(sketch, "E104.13.2", {"position": v(-20.3, -79.26) * mm});
            skPoint(sketch, "E104.13.3", {"position": v(-20.37, -82.9) * mm});
            skPoint(sketch, "E104.13.4", {"position": v(-22.24, -79.78) * mm});
            skArc(sketch, "E104.13.5", {"start": v(-21.28, -79.52) * mm, "mid": v(-21.88, -79.99) * mm, "end": v(-21.98, -80.75) * mm});
            skArc(sketch, "E104.13.6", {"start": v(-20.05, -80.23) * mm, "mid": v(-20.52, -79.62) * mm, "end": v(-21.28, -79.52) * mm});
            skPoint(sketch, "E104.13.7", {"position": v(-18.5, -86.02) * mm});
            skPoint(sketch, "E104.13.8", {"position": v(-20.43, -86.54) * mm});
            skArc(sketch, "E104.13.9", {"start": v(-20.69, -85.58) * mm, "mid": v(-20.22, -86.18) * mm, "end": v(-19.46, -86.28) * mm});
            skArc(sketch, "E104.13.10", {"start": v(-19.46, -86.28) * mm, "mid": v(-18.86, -85.82) * mm, "end": v(-18.76, -85.06) * mm});
            skLineSegment(sketch, "E104.14.0", {"start": v(-15.75, -78.16) * mm, "end": v(-13.25, -82.5) * mm});
            skLineSegment(sketch, "E104.14.1", {"start": v(-17.48, -79.16) * mm, "end": v(-14.98, -83.5) * mm});
            skPoint(sketch, "E104.14.2", {"position": v(-16.25, -77.3) * mm});
            skPoint(sketch, "E104.14.3", {"position": v(-15.36, -80.83) * mm});
            skPoint(sketch, "E104.14.4", {"position": v(-17.98, -78.3) * mm});
            skArc(sketch, "E104.14.5", {"start": v(-17.11, -77.8) * mm, "mid": v(-17.58, -78.4) * mm, "end": v(-17.48, -79.16) * mm});
            skArc(sketch, "E104.14.6", {"start": v(-15.75, -78.16) * mm, "mid": v(-16.36, -77.7) * mm, "end": v(-17.11, -77.8) * mm});
            skPoint(sketch, "E104.14.7", {"position": v(-12.75, -83.36) * mm});
            skPoint(sketch, "E104.14.8", {"position": v(-14.48, -84.36) * mm});
            skArc(sketch, "E104.14.9", {"start": v(-14.98, -83.5) * mm, "mid": v(-14.37, -83.96) * mm, "end": v(-13.61, -83.86) * mm});
            skArc(sketch, "E104.14.10", {"start": v(-13.61, -83.86) * mm, "mid": v(-13.15, -83.25) * mm, "end": v(-13.25, -82.5) * mm});
            skLineSegment(sketch, "E104.15.0", {"start": v(-12.13, -75.06) * mm, "end": v(-8.6, -78.6) * mm});
            skLineSegment(sketch, "E104.15.1", {"start": v(-13.54, -76.47) * mm, "end": v(-10, -80) * mm});
            skPoint(sketch, "E104.15.2", {"position": v(-12.84, -74.35) * mm});
            skPoint(sketch, "E104.15.3", {"position": v(-11.07, -77.53) * mm});
            skPoint(sketch, "E104.15.4", {"position": v(-14.25, -75.76) * mm});
            skArc(sketch, "E104.15.5", {"start": v(-13.54, -75.06) * mm, "mid": v(-13.84, -75.76) * mm, "end": v(-13.54, -76.47) * mm});
            skArc(sketch, "E104.15.6", {"start": v(-12.13, -75.06) * mm, "mid": v(-12.84, -74.76) * mm, "end": v(-13.54, -75.06) * mm});
            skPoint(sketch, "E104.15.7", {"position": v(-7.89, -79.3) * mm});
            skPoint(sketch, "E104.15.8", {"position": v(-9.3, -80.71) * mm});
            skArc(sketch, "E104.15.9", {"start": v(-10, -80) * mm, "mid": v(-9.3, -80.3) * mm, "end": v(-8.6, -80) * mm});
            skArc(sketch, "E104.15.10", {"start": v(-8.6, -80) * mm, "mid": v(-8.3, -79.3) * mm, "end": v(-8.6, -78.6) * mm});
            skLineSegment(sketch, "E104.16.0", {"start": v(-9.44, -71.12) * mm, "end": v(-5.1, -73.62) * mm});
            skLineSegment(sketch, "E104.16.1", {"start": v(-10.44, -72.85) * mm, "end": v(-6.1, -75.35) * mm});
            skPoint(sketch, "E104.16.2", {"position": v(-10.3, -70.62) * mm});
            skPoint(sketch, "E104.16.3", {"position": v(-7.77, -73.23) * mm});
            skPoint(sketch, "E104.16.4", {"position": v(-11.3, -72.35) * mm});
            skArc(sketch, "E104.16.5", {"start": v(-10.8, -71.48) * mm, "mid": v(-10.9, -72.24) * mm, "end": v(-10.44, -72.85) * mm});
            skArc(sketch, "E104.16.6", {"start": v(-9.44, -71.12) * mm, "mid": v(-10.2, -71.02) * mm, "end": v(-10.8, -71.48) * mm});
            skPoint(sketch, "E104.16.7", {"position": v(-4.24, -74.12) * mm});
            skPoint(sketch, "E104.16.8", {"position": v(-5.24, -75.85) * mm});
            skArc(sketch, "E104.16.9", {"start": v(-6.1, -75.35) * mm, "mid": v(-5.35, -75.45) * mm, "end": v(-4.74, -74.98) * mm});
            skArc(sketch, "E104.16.10", {"start": v(-4.74, -74.98) * mm, "mid": v(-4.64, -74.23) * mm, "end": v(-5.1, -73.62) * mm});
            skLineSegment(sketch, "E104.17.0", {"start": v(-7.85, -66.62) * mm, "end": v(-3.02, -67.91) * mm});
            skLineSegment(sketch, "E104.17.1", {"start": v(-8.37, -68.55) * mm, "end": v(-3.54, -69.84) * mm});
            skPoint(sketch, "E104.17.2", {"position": v(-8.82, -66.36) * mm});
            skPoint(sketch, "E104.17.3", {"position": v(-5.7, -68.23) * mm});
            skPoint(sketch, "E104.17.4", {"position": v(-9.34, -68.3) * mm});
            skArc(sketch, "E104.17.5", {"start": v(-9.08, -67.32) * mm, "mid": v(-8.98, -68.08) * mm, "end": v(-8.37, -68.55) * mm});
            skArc(sketch, "E104.17.6", {"start": v(-7.85, -66.62) * mm, "mid": v(-8.61, -66.72) * mm, "end": v(-9.08, -67.32) * mm});
            skPoint(sketch, "E104.17.7", {"position": v(-2.06, -68.17) * mm});
            skPoint(sketch, "E104.17.8", {"position": v(-2.58, -70.1) * mm});
            skArc(sketch, "E104.17.9", {"start": v(-3.54, -69.84) * mm, "mid": v(-2.78, -69.74) * mm, "end": v(-2.32, -69.14) * mm});
            skArc(sketch, "E104.17.10", {"start": v(-2.32, -69.14) * mm, "mid": v(-2.42, -68.38) * mm, "end": v(-3.02, -67.91) * mm});
            skLineSegment(sketch, "E104.18.0", {"start": v(-7.49, -61.86) * mm, "end": v(-2.49, -61.86) * mm});
            skLineSegment(sketch, "E104.18.1", {"start": v(-7.49, -63.86) * mm, "end": v(-2.49, -63.86) * mm});
            skPoint(sketch, "E104.18.2", {"position": v(-8.49, -61.86) * mm});
            skPoint(sketch, "E104.18.3", {"position": v(-4.99, -62.86) * mm});
            skPoint(sketch, "E104.18.4", {"position": v(-8.49, -63.86) * mm});
            skArc(sketch, "E104.18.5", {"start": v(-8.49, -62.86) * mm, "mid": v(-8.2, -63.57) * mm, "end": v(-7.49, -63.86) * mm});
            skArc(sketch, "E104.18.6", {"start": v(-7.49, -61.86) * mm, "mid": v(-8.2, -62.15) * mm, "end": v(-8.49, -62.86) * mm});
            skPoint(sketch, "E104.18.7", {"position": v(-1.49, -61.86) * mm});
            skPoint(sketch, "E104.18.8", {"position": v(-1.49, -63.86) * mm});
            skArc(sketch, "E104.18.9", {"start": v(-2.49, -63.86) * mm, "mid": v(-1.78, -63.57) * mm, "end": v(-1.49, -62.86) * mm});
            skArc(sketch, "E104.18.10", {"start": v(-1.49, -62.86) * mm, "mid": v(-1.78, -62.15) * mm, "end": v(-2.49, -61.86) * mm});
            skLineSegment(sketch, "E104.19.0", {"start": v(-8.37, -57.17) * mm, "end": v(-3.54, -55.88) * mm});
            skLineSegment(sketch, "E104.19.1", {"start": v(-7.85, -59.1) * mm, "end": v(-3.02, -57.8) * mm});
            skPoint(sketch, "E104.19.2", {"position": v(-9.34, -57.43) * mm});
            skPoint(sketch, "E104.19.3", {"position": v(-5.7, -57.49) * mm});
            skPoint(sketch, "E104.19.4", {"position": v(-8.82, -59.36) * mm});
            skArc(sketch, "E104.19.5", {"start": v(-9.08, -58.4) * mm, "mid": v(-8.61, -59) * mm, "end": v(-7.85, -59.1) * mm});
            skArc(sketch, "E104.19.6", {"start": v(-8.37, -57.17) * mm, "mid": v(-8.98, -57.64) * mm, "end": v(-9.08, -58.4) * mm});
            skPoint(sketch, "E104.19.7", {"position": v(-2.58, -55.62) * mm});
            skPoint(sketch, "E104.19.8", {"position": v(-2.06, -57.55) * mm});
            skArc(sketch, "E104.19.9", {"start": v(-3.02, -57.8) * mm, "mid": v(-2.42, -57.34) * mm, "end": v(-2.32, -56.58) * mm});
            skArc(sketch, "E104.19.10", {"start": v(-2.32, -56.58) * mm, "mid": v(-2.78, -55.98) * mm, "end": v(-3.54, -55.88) * mm});
            skLineSegment(sketch, "E104.20.0", {"start": v(-10.44, -52.87) * mm, "end": v(-6.1, -50.37) * mm});
            skLineSegment(sketch, "E104.20.1", {"start": v(-9.44, -54.6) * mm, "end": v(-5.1, -52.1) * mm});
            skPoint(sketch, "E104.20.2", {"position": v(-11.3, -53.37) * mm});
            skPoint(sketch, "E104.20.3", {"position": v(-7.77, -52.48) * mm});
            skPoint(sketch, "E104.20.4", {"position": v(-10.3, -55.1) * mm});
            skArc(sketch, "E104.20.5", {"start": v(-10.8, -54.23) * mm, "mid": v(-10.2, -54.7) * mm, "end": v(-9.44, -54.6) * mm});
            skArc(sketch, "E104.20.6", {"start": v(-10.44, -52.87) * mm, "mid": v(-10.9, -53.48) * mm, "end": v(-10.8, -54.23) * mm});
            skPoint(sketch, "E104.20.7", {"position": v(-5.24, -49.87) * mm});
            skPoint(sketch, "E104.20.8", {"position": v(-4.24, -51.6) * mm});
            skArc(sketch, "E104.20.9", {"start": v(-5.1, -52.1) * mm, "mid": v(-4.64, -51.5) * mm, "end": v(-4.74, -50.73) * mm});
            skArc(sketch, "E104.20.10", {"start": v(-4.74, -50.73) * mm, "mid": v(-5.35, -50.27) * mm, "end": v(-6.1, -50.37) * mm});
            skLineSegment(sketch, "E104.21.0", {"start": v(-13.54, -49.25) * mm, "end": v(-10, -45.71) * mm});
            skLineSegment(sketch, "E104.21.1", {"start": v(-12.13, -50.66) * mm, "end": v(-8.6, -47.13) * mm});
            skPoint(sketch, "E104.21.2", {"position": v(-14.25, -49.96) * mm});
            skPoint(sketch, "E104.21.3", {"position": v(-11.07, -48.19) * mm});
            skPoint(sketch, "E104.21.4", {"position": v(-12.84, -51.37) * mm});
            skArc(sketch, "E104.21.5", {"start": v(-13.54, -50.66) * mm, "mid": v(-12.84, -50.96) * mm, "end": v(-12.13, -50.66) * mm});
            skArc(sketch, "E104.21.6", {"start": v(-13.54, -49.25) * mm, "mid": v(-13.84, -49.96) * mm, "end": v(-13.54, -50.66) * mm});
            skPoint(sketch, "E104.21.7", {"position": v(-9.3, -45) * mm});
            skPoint(sketch, "E104.21.8", {"position": v(-7.89, -46.42) * mm});
            skArc(sketch, "E104.21.9", {"start": v(-8.6, -47.13) * mm, "mid": v(-8.3, -46.42) * mm, "end": v(-8.6, -45.71) * mm});
            skArc(sketch, "E104.21.10", {"start": v(-8.6, -45.71) * mm, "mid": v(-9.3, -45.42) * mm, "end": v(-10, -45.71) * mm});
            skLineSegment(sketch, "E104.22.0", {"start": v(-17.48, -46.56) * mm, "end": v(-14.98, -42.22) * mm});
            skLineSegment(sketch, "E104.22.1", {"start": v(-15.75, -47.56) * mm, "end": v(-13.25, -43.22) * mm});
            skPoint(sketch, "E104.22.2", {"position": v(-17.98, -47.42) * mm});
            skPoint(sketch, "E104.22.3", {"position": v(-15.37, -44.89) * mm});
            skPoint(sketch, "E104.22.4", {"position": v(-16.25, -48.42) * mm});
            skArc(sketch, "E104.22.5", {"start": v(-17.12, -47.92) * mm, "mid": v(-16.36, -48.02) * mm, "end": v(-15.75, -47.56) * mm});
            skArc(sketch, "E104.22.6", {"start": v(-17.48, -46.56) * mm, "mid": v(-17.58, -47.31) * mm, "end": v(-17.12, -47.92) * mm});
            skPoint(sketch, "E104.22.7", {"position": v(-14.48, -41.36) * mm});
            skPoint(sketch, "E104.22.8", {"position": v(-12.75, -42.36) * mm});
            skArc(sketch, "E104.22.9", {"start": v(-13.25, -43.22) * mm, "mid": v(-13.15, -42.47) * mm, "end": v(-13.62, -41.86) * mm});
            skArc(sketch, "E104.22.10", {"start": v(-13.62, -41.86) * mm, "mid": v(-14.37, -41.76) * mm, "end": v(-14.98, -42.22) * mm});
            skLineSegment(sketch, "E104.23.0", {"start": v(-21.98, -44.97) * mm, "end": v(-20.69, -40.14) * mm});
            skLineSegment(sketch, "E104.23.1", {"start": v(-20.05, -45.5) * mm, "end": v(-18.76, -40.66) * mm});
            skPoint(sketch, "E104.23.2", {"position": v(-22.24, -45.94) * mm});
            skPoint(sketch, "E104.23.3", {"position": v(-20.37, -42.82) * mm});
            skPoint(sketch, "E104.23.4", {"position": v(-20.3, -46.46) * mm});
            skArc(sketch, "E104.23.5", {"start": v(-21.28, -46.2) * mm, "mid": v(-20.52, -46.1) * mm, "end": v(-20.05, -45.5) * mm});
            skArc(sketch, "E104.23.6", {"start": v(-21.98, -44.97) * mm, "mid": v(-21.88, -45.73) * mm, "end": v(-21.28, -46.2) * mm});
            skPoint(sketch, "E104.23.7", {"position": v(-20.43, -39.18) * mm});
            skPoint(sketch, "E104.23.8", {"position": v(-18.5, -39.7) * mm});
            skArc(sketch, "E104.23.9", {"start": v(-18.76, -40.66) * mm, "mid": v(-18.86, -39.9) * mm, "end": v(-19.46, -39.44) * mm});
            skArc(sketch, "E104.23.10", {"start": v(-19.46, -39.44) * mm, "mid": v(-20.22, -39.54) * mm, "end": v(-20.69, -40.14) * mm});
            skPoint(sketch, "E105.1.0", {"position": v(-79.37, -23.78) * mm});
            skLineSegment(sketch, "E105.1.1", {"start": v(-77.76, -25.93) * mm, "end": v(-79.05, -21.1) * mm});
            skLineSegment(sketch, "E105.1.2", {"start": v(-79.69, -26.45) * mm, "end": v(-80.98, -21.62) * mm});
            skPoint(sketch, "E105.1.3", {"position": v(-79.43, -27.42) * mm});
            skPoint(sketch, "E105.1.4", {"position": v(-77.5, -26.9) * mm});
            skArc(sketch, "E105.1.5", {"start": v(-79.69, -26.45) * mm, "mid": v(-79.22, -27.06) * mm, "end": v(-78.46, -27.16) * mm});
            skArc(sketch, "E105.1.6", {"start": v(-78.46, -27.16) * mm, "mid": v(-77.86, -26.7) * mm, "end": v(-77.76, -25.93) * mm});
            skPoint(sketch, "E105.1.7", {"position": v(-81.24, -20.66) * mm});
            skPoint(sketch, "E105.1.8", {"position": v(-79.31, -20.14) * mm});
            skArc(sketch, "E105.1.9", {"start": v(-79.05, -21.1) * mm, "mid": v(-79.52, -20.5) * mm, "end": v(-80.28, -20.4) * mm});
            skArc(sketch, "E105.1.10", {"start": v(-80.28, -20.4) * mm, "mid": v(-80.88, -20.86) * mm, "end": v(-80.98, -21.62) * mm});
            skPoint(sketch, "E105.2.0", {"position": v(-84.37, -25.85) * mm});
            skLineSegment(sketch, "E105.2.1", {"start": v(-82.26, -27.52) * mm, "end": v(-84.76, -23.18) * mm});
            skLineSegment(sketch, "E105.2.2", {"start": v(-84, -28.52) * mm, "end": v(-86.5, -24.18) * mm});
            skPoint(sketch, "E105.2.3", {"position": v(-83.5, -29.38) * mm});
            skPoint(sketch, "E105.2.4", {"position": v(-81.76, -28.38) * mm});
            skArc(sketch, "E105.2.5", {"start": v(-84, -28.52) * mm, "mid": v(-83.38, -28.98) * mm, "end": v(-82.62, -28.88) * mm});
            skArc(sketch, "E105.2.6", {"start": v(-82.62, -28.88) * mm, "mid": v(-82.16, -28.27) * mm, "end": v(-82.26, -27.52) * mm});
            skPoint(sketch, "E105.2.7", {"position": v(-87, -23.32) * mm});
            skPoint(sketch, "E105.2.8", {"position": v(-85.26, -22.32) * mm});
            skArc(sketch, "E105.2.9", {"start": v(-84.76, -23.18) * mm, "mid": v(-85.37, -22.72) * mm, "end": v(-86.12, -22.82) * mm});
            skArc(sketch, "E105.2.10", {"start": v(-86.12, -22.82) * mm, "mid": v(-86.6, -23.43) * mm, "end": v(-86.5, -24.18) * mm});
            skPoint(sketch, "E105.3.0", {"position": v(-88.67, -29.15) * mm});
            skLineSegment(sketch, "E105.3.1", {"start": v(-86.2, -30.2) * mm, "end": v(-89.73, -26.67) * mm});
            skLineSegment(sketch, "E105.3.2", {"start": v(-87.61, -31.62) * mm, "end": v(-91.15, -28.09) * mm});
            skPoint(sketch, "E105.3.3", {"position": v(-86.9, -32.33) * mm});
            skPoint(sketch, "E105.3.4", {"position": v(-85.5, -30.92) * mm});
            skArc(sketch, "E105.3.5", {"start": v(-87.61, -31.62) * mm, "mid": v(-86.9, -31.92) * mm, "end": v(-86.2, -31.62) * mm});
            skArc(sketch, "E105.3.6", {"start": v(-86.2, -31.62) * mm, "mid": v(-85.9, -30.92) * mm, "end": v(-86.2, -30.2) * mm});
            skPoint(sketch, "E105.3.7", {"position": v(-91.85, -27.38) * mm});
            skPoint(sketch, "E105.3.8", {"position": v(-90.44, -25.97) * mm});
            skArc(sketch, "E105.3.9", {"start": v(-89.73, -26.67) * mm, "mid": v(-90.44, -26.38) * mm, "end": v(-91.15, -26.67) * mm});
            skArc(sketch, "E105.3.10", {"start": v(-91.15, -26.67) * mm, "mid": v(-91.44, -27.38) * mm, "end": v(-91.15, -28.09) * mm});
            skPoint(sketch, "E105.4.0", {"position": v(-91.97, -33.44) * mm});
            skLineSegment(sketch, "E105.4.1", {"start": v(-89.3, -33.83) * mm, "end": v(-93.64, -31.33) * mm});
            skLineSegment(sketch, "E105.4.2", {"start": v(-90.3, -35.56) * mm, "end": v(-94.64, -33.06) * mm});
            skPoint(sketch, "E105.4.3", {"position": v(-89.44, -36.06) * mm});
            skPoint(sketch, "E105.4.4", {"position": v(-88.44, -34.33) * mm});
            skArc(sketch, "E105.4.5", {"start": v(-90.3, -35.56) * mm, "mid": v(-89.55, -35.66) * mm, "end": v(-88.94, -35.2) * mm});
            skArc(sketch, "E105.4.6", {"start": v(-88.94, -35.2) * mm, "mid": v(-88.84, -34.44) * mm, "end": v(-89.3, -33.83) * mm});
            skPoint(sketch, "E105.4.7", {"position": v(-95.5, -32.56) * mm});
            skPoint(sketch, "E105.4.8", {"position": v(-94.5, -30.83) * mm});
            skArc(sketch, "E105.4.9", {"start": v(-93.64, -31.33) * mm, "mid": v(-94.4, -31.23) * mm, "end": v(-95, -31.7) * mm});
            skArc(sketch, "E105.4.10", {"start": v(-95, -31.7) * mm, "mid": v(-95.1, -32.45) * mm, "end": v(-94.64, -33.06) * mm});
            skPoint(sketch, "E105.5.0", {"position": v(-94.04, -38.45) * mm});
            skLineSegment(sketch, "E105.5.1", {"start": v(-91.37, -38.13) * mm, "end": v(-96.2, -36.84) * mm});
            skLineSegment(sketch, "E105.5.2", {"start": v(-91.89, -40.06) * mm, "end": v(-96.72, -38.77) * mm});
            skPoint(sketch, "E105.5.3", {"position": v(-90.92, -40.32) * mm});
            skPoint(sketch, "E105.5.4", {"position": v(-90.4, -38.39) * mm});
            skArc(sketch, "E105.5.5", {"start": v(-91.89, -40.06) * mm, "mid": v(-91.13, -39.96) * mm, "end": v(-90.66, -39.36) * mm});
            skArc(sketch, "E105.5.6", {"start": v(-90.66, -39.36) * mm, "mid": v(-90.76, -38.6) * mm, "end": v(-91.37, -38.13) * mm});
            skPoint(sketch, "E105.5.7", {"position": v(-97.68, -38.5) * mm});
            skPoint(sketch, "E105.5.8", {"position": v(-97.16, -36.58) * mm});
            skArc(sketch, "E105.5.9", {"start": v(-96.2, -36.84) * mm, "mid": v(-96.96, -36.94) * mm, "end": v(-97.42, -37.54) * mm});
            skArc(sketch, "E105.5.10", {"start": v(-97.42, -37.54) * mm, "mid": v(-97.32, -38.3) * mm, "end": v(-96.72, -38.77) * mm});
            skPoint(sketch, "E105.6.0", {"position": v(-94.75, -43.82) * mm});
            skLineSegment(sketch, "E105.6.1", {"start": v(-92.25, -42.82) * mm, "end": v(-97.25, -42.82) * mm});
            skLineSegment(sketch, "E105.6.2", {"start": v(-92.25, -44.82) * mm, "end": v(-97.25, -44.82) * mm});
            skPoint(sketch, "E105.6.3", {"position": v(-91.25, -44.82) * mm});
            skPoint(sketch, "E105.6.4", {"position": v(-91.25, -42.82) * mm});
            skArc(sketch, "E105.6.5", {"start": v(-92.25, -44.82) * mm, "mid": v(-91.54, -44.53) * mm, "end": v(-91.25, -43.82) * mm});
            skArc(sketch, "E105.6.6", {"start": v(-91.25, -43.82) * mm, "mid": v(-91.54, -43.11) * mm, "end": v(-92.25, -42.82) * mm});
            skPoint(sketch, "E105.6.7", {"position": v(-98.25, -44.82) * mm});
            skPoint(sketch, "E105.6.8", {"position": v(-98.25, -42.82) * mm});
            skArc(sketch, "E105.6.9", {"start": v(-97.25, -42.82) * mm, "mid": v(-97.96, -43.11) * mm, "end": v(-98.25, -43.82) * mm});
            skArc(sketch, "E105.6.10", {"start": v(-98.25, -43.82) * mm, "mid": v(-97.96, -44.53) * mm, "end": v(-97.25, -44.82) * mm});
            skPoint(sketch, "E105.7.0", {"position": v(-94.04, -49.2) * mm});
            skLineSegment(sketch, "E105.7.1", {"start": v(-91.89, -47.58) * mm, "end": v(-96.72, -48.87) * mm});
            skLineSegment(sketch, "E105.7.2", {"start": v(-91.37, -49.5) * mm, "end": v(-96.2, -50.8) * mm});
            skPoint(sketch, "E105.7.3", {"position": v(-90.4, -49.25) * mm});
            skPoint(sketch, "E105.7.4", {"position": v(-90.92, -47.32) * mm});
            skArc(sketch, "E105.7.5", {"start": v(-91.37, -49.5) * mm, "mid": v(-90.76, -49.04) * mm, "end": v(-90.66, -48.28) * mm});
            skArc(sketch, "E105.7.6", {"start": v(-90.66, -48.28) * mm, "mid": v(-91.13, -47.68) * mm, "end": v(-91.89, -47.58) * mm});
            skPoint(sketch, "E105.7.7", {"position": v(-97.16, -51.06) * mm});
            skPoint(sketch, "E105.7.8", {"position": v(-97.68, -49.13) * mm});
            skArc(sketch, "E105.7.9", {"start": v(-96.72, -48.87) * mm, "mid": v(-97.32, -49.34) * mm, "end": v(-97.42, -50.1) * mm});
            skArc(sketch, "E105.7.10", {"start": v(-97.42, -50.1) * mm, "mid": v(-96.96, -50.7) * mm, "end": v(-96.2, -50.8) * mm});
            skPoint(sketch, "E105.8.0", {"position": v(-91.97, -54.2) * mm});
            skLineSegment(sketch, "E105.8.1", {"start": v(-90.3, -52.08) * mm, "end": v(-94.64, -54.58) * mm});
            skLineSegment(sketch, "E105.8.2", {"start": v(-89.3, -53.81) * mm, "end": v(-93.64, -56.31) * mm});
            skPoint(sketch, "E105.8.3", {"position": v(-88.44, -53.31) * mm});
            skPoint(sketch, "E105.8.4", {"position": v(-89.44, -51.58) * mm});
            skArc(sketch, "E105.8.5", {"start": v(-89.3, -53.81) * mm, "mid": v(-88.84, -53.2) * mm, "end": v(-88.94, -52.44) * mm});
            skArc(sketch, "E105.8.6", {"start": v(-88.94, -52.44) * mm, "mid": v(-89.55, -51.98) * mm, "end": v(-90.3, -52.08) * mm});
            skPoint(sketch, "E105.8.7", {"position": v(-94.5, -56.81) * mm});
            skPoint(sketch, "E105.8.8", {"position": v(-95.5, -55.08) * mm});
            skArc(sketch, "E105.8.9", {"start": v(-94.64, -54.58) * mm, "mid": v(-95.1, -55.19) * mm, "end": v(-95, -55.95) * mm});
            skArc(sketch, "E105.8.10", {"start": v(-95, -55.95) * mm, "mid": v(-94.4, -56.41) * mm, "end": v(-93.64, -56.31) * mm});
            skPoint(sketch, "E105.9.0", {"position": v(-88.67, -58.5) * mm});
            skLineSegment(sketch, "E105.9.1", {"start": v(-87.61, -56.02) * mm, "end": v(-91.15, -59.55) * mm});
            skLineSegment(sketch, "E105.9.2", {"start": v(-86.2, -57.43) * mm, "end": v(-89.73, -60.97) * mm});
            skPoint(sketch, "E105.9.3", {"position": v(-85.5, -56.72) * mm});
            skPoint(sketch, "E105.9.4", {"position": v(-86.9, -55.31) * mm});
            skArc(sketch, "E105.9.5", {"start": v(-86.2, -57.43) * mm, "mid": v(-85.9, -56.72) * mm, "end": v(-86.2, -56.02) * mm});
            skArc(sketch, "E105.9.6", {"start": v(-86.2, -56.02) * mm, "mid": v(-86.9, -55.72) * mm, "end": v(-87.61, -56.02) * mm});
            skPoint(sketch, "E105.9.7", {"position": v(-90.44, -61.67) * mm});
            skPoint(sketch, "E105.9.8", {"position": v(-91.85, -60.26) * mm});
            skArc(sketch, "E105.9.9", {"start": v(-91.15, -59.55) * mm, "mid": v(-91.44, -60.26) * mm, "end": v(-91.15, -60.97) * mm});
            skArc(sketch, "E105.9.10", {"start": v(-91.15, -60.97) * mm, "mid": v(-90.44, -61.26) * mm, "end": v(-89.73, -60.97) * mm});
            skPoint(sketch, "E105.10.0", {"position": v(-84.37, -61.8) * mm});
            skLineSegment(sketch, "E105.10.1", {"start": v(-84, -59.12) * mm, "end": v(-86.5, -63.46) * mm});
            skLineSegment(sketch, "E105.10.2", {"start": v(-82.26, -60.12) * mm, "end": v(-84.76, -64.46) * mm});
            skPoint(sketch, "E105.10.3", {"position": v(-81.76, -59.26) * mm});
            skPoint(sketch, "E105.10.4", {"position": v(-83.5, -58.26) * mm});
            skArc(sketch, "E105.10.5", {"start": v(-82.26, -60.12) * mm, "mid": v(-82.16, -59.37) * mm, "end": v(-82.62, -58.76) * mm});
            skArc(sketch, "E105.10.6", {"start": v(-82.62, -58.76) * mm, "mid": v(-83.38, -58.66) * mm, "end": v(-84, -59.12) * mm});
            skPoint(sketch, "E105.10.7", {"position": v(-85.26, -65.32) * mm});
            skPoint(sketch, "E105.10.8", {"position": v(-87, -64.32) * mm});
            skArc(sketch, "E105.10.9", {"start": v(-86.5, -63.46) * mm, "mid": v(-86.6, -64.21) * mm, "end": v(-86.12, -64.82) * mm});
            skArc(sketch, "E105.10.10", {"start": v(-86.12, -64.82) * mm, "mid": v(-85.37, -64.92) * mm, "end": v(-84.76, -64.46) * mm});
            skPoint(sketch, "E105.11.0", {"position": v(-79.37, -63.86) * mm});
            skLineSegment(sketch, "E105.11.1", {"start": v(-79.69, -61.19) * mm, "end": v(-80.98, -66.02) * mm});
            skLineSegment(sketch, "E105.11.2", {"start": v(-77.76, -61.7) * mm, "end": v(-79.05, -66.54) * mm});
            skPoint(sketch, "E105.11.3", {"position": v(-77.5, -60.74) * mm});
            skPoint(sketch, "E105.11.4", {"position": v(-79.43, -60.22) * mm});
            skArc(sketch, "E105.11.5", {"start": v(-77.76, -61.7) * mm, "mid": v(-77.86, -60.95) * mm, "end": v(-78.46, -60.48) * mm});
            skArc(sketch, "E105.11.6", {"start": v(-78.46, -60.48) * mm, "mid": v(-79.22, -60.58) * mm, "end": v(-79.69, -61.19) * mm});
            skPoint(sketch, "E105.11.7", {"position": v(-79.31, -67.5) * mm});
            skPoint(sketch, "E105.11.8", {"position": v(-81.24, -66.98) * mm});
            skArc(sketch, "E105.11.9", {"start": v(-80.98, -66.02) * mm, "mid": v(-80.88, -66.78) * mm, "end": v(-80.28, -67.24) * mm});
            skArc(sketch, "E105.11.10", {"start": v(-80.28, -67.24) * mm, "mid": v(-79.52, -67.14) * mm, "end": v(-79.05, -66.54) * mm});
            skPoint(sketch, "E105.12.0", {"position": v(-74, -64.57) * mm});
            skLineSegment(sketch, "E105.12.1", {"start": v(-75, -62.07) * mm, "end": v(-75, -67.07) * mm});
            skLineSegment(sketch, "E105.12.2", {"start": v(-73, -62.07) * mm, "end": v(-73, -67.07) * mm});
            skPoint(sketch, "E105.12.3", {"position": v(-73, -61.07) * mm});
            skPoint(sketch, "E105.12.4", {"position": v(-75, -61.07) * mm});
            skArc(sketch, "E105.12.5", {"start": v(-73, -62.07) * mm, "mid": v(-73.3, -61.36) * mm, "end": v(-74, -61.07) * mm});
            skArc(sketch, "E105.12.6", {"start": v(-74, -61.07) * mm, "mid": v(-74.7, -61.36) * mm, "end": v(-75, -62.07) * mm});
            skPoint(sketch, "E105.12.7", {"position": v(-73, -68.07) * mm});
            skPoint(sketch, "E105.12.8", {"position": v(-75, -68.07) * mm});
            skArc(sketch, "E105.12.9", {"start": v(-75, -67.07) * mm, "mid": v(-74.7, -67.78) * mm, "end": v(-74, -68.07) * mm});
            skArc(sketch, "E105.12.10", {"start": v(-74, -68.07) * mm, "mid": v(-73.3, -67.78) * mm, "end": v(-73, -67.07) * mm});
            skPoint(sketch, "E105.13.0", {"position": v(-68.63, -63.86) * mm});
            skLineSegment(sketch, "E105.13.1", {"start": v(-70.24, -61.7) * mm, "end": v(-68.95, -66.54) * mm});
            skLineSegment(sketch, "E105.13.2", {"start": v(-68.31, -61.19) * mm, "end": v(-67.02, -66.02) * mm});
            skPoint(sketch, "E105.13.3", {"position": v(-68.57, -60.22) * mm});
            skPoint(sketch, "E105.13.4", {"position": v(-70.5, -60.74) * mm});
            skArc(sketch, "E105.13.5", {"start": v(-68.31, -61.19) * mm, "mid": v(-68.78, -60.58) * mm, "end": v(-69.54, -60.48) * mm});
            skArc(sketch, "E105.13.6", {"start": v(-69.54, -60.48) * mm, "mid": v(-70.14, -60.95) * mm, "end": v(-70.24, -61.7) * mm});
            skPoint(sketch, "E105.13.7", {"position": v(-66.76, -66.98) * mm});
            skPoint(sketch, "E105.13.8", {"position": v(-68.69, -67.5) * mm});
            skArc(sketch, "E105.13.9", {"start": v(-68.95, -66.54) * mm, "mid": v(-68.48, -67.14) * mm, "end": v(-67.72, -67.24) * mm});
            skArc(sketch, "E105.13.10", {"start": v(-67.72, -67.24) * mm, "mid": v(-67.12, -66.78) * mm, "end": v(-67.02, -66.02) * mm});
            skPoint(sketch, "E105.14.0", {"position": v(-63.62, -61.8) * mm});
            skLineSegment(sketch, "E105.14.1", {"start": v(-65.74, -60.12) * mm, "end": v(-63.24, -64.46) * mm});
            skLineSegment(sketch, "E105.14.2", {"start": v(-64, -59.12) * mm, "end": v(-61.5, -63.46) * mm});
            skPoint(sketch, "E105.14.3", {"position": v(-64.5, -58.26) * mm});
            skPoint(sketch, "E105.14.4", {"position": v(-66.24, -59.26) * mm});
            skArc(sketch, "E105.14.5", {"start": v(-64, -59.12) * mm, "mid": v(-64.62, -58.66) * mm, "end": v(-65.37, -58.76) * mm});
            skArc(sketch, "E105.14.6", {"start": v(-65.37, -58.76) * mm, "mid": v(-65.84, -59.37) * mm, "end": v(-65.74, -60.12) * mm});
            skPoint(sketch, "E105.14.7", {"position": v(-61, -64.32) * mm});
            skPoint(sketch, "E105.14.8", {"position": v(-62.74, -65.32) * mm});
            skArc(sketch, "E105.14.9", {"start": v(-63.24, -64.46) * mm, "mid": v(-62.63, -64.92) * mm, "end": v(-61.87, -64.82) * mm});
            skArc(sketch, "E105.14.10", {"start": v(-61.87, -64.82) * mm, "mid": v(-61.4, -64.21) * mm, "end": v(-61.5, -63.46) * mm});
            skPoint(sketch, "E105.15.0", {"position": v(-59.33, -58.5) * mm});
            skLineSegment(sketch, "E105.15.1", {"start": v(-61.8, -57.43) * mm, "end": v(-58.27, -60.97) * mm});
            skLineSegment(sketch, "E105.15.2", {"start": v(-60.39, -56.02) * mm, "end": v(-56.85, -59.55) * mm});
            skPoint(sketch, "E105.15.3", {"position": v(-61.1, -55.31) * mm});
            skPoint(sketch, "E105.15.4", {"position": v(-62.5, -56.72) * mm});
            skArc(sketch, "E105.15.5", {"start": v(-60.39, -56.02) * mm, "mid": v(-61.1, -55.72) * mm, "end": v(-61.8, -56.02) * mm});
            skArc(sketch, "E105.15.6", {"start": v(-61.8, -56.02) * mm, "mid": v(-62.1, -56.72) * mm, "end": v(-61.8, -57.43) * mm});
            skPoint(sketch, "E105.15.7", {"position": v(-56.15, -60.26) * mm});
            skPoint(sketch, "E105.15.8", {"position": v(-57.56, -61.67) * mm});
            skArc(sketch, "E105.15.9", {"start": v(-58.27, -60.97) * mm, "mid": v(-57.56, -61.26) * mm, "end": v(-56.85, -60.97) * mm});
            skArc(sketch, "E105.15.10", {"start": v(-56.85, -60.97) * mm, "mid": v(-56.56, -60.26) * mm, "end": v(-56.85, -59.55) * mm});
            skPoint(sketch, "E105.16.0", {"position": v(-56.03, -54.2) * mm});
            skLineSegment(sketch, "E105.16.1", {"start": v(-58.7, -53.81) * mm, "end": v(-54.36, -56.31) * mm});
            skLineSegment(sketch, "E105.16.2", {"start": v(-57.7, -52.08) * mm, "end": v(-53.36, -54.58) * mm});
            skPoint(sketch, "E105.16.3", {"position": v(-58.56, -51.58) * mm});
            skPoint(sketch, "E105.16.4", {"position": v(-59.56, -53.31) * mm});
            skArc(sketch, "E105.16.5", {"start": v(-57.7, -52.08) * mm, "mid": v(-58.45, -51.98) * mm, "end": v(-59.06, -52.44) * mm});
            skArc(sketch, "E105.16.6", {"start": v(-59.06, -52.44) * mm, "mid": v(-59.16, -53.2) * mm, "end": v(-58.7, -53.81) * mm});
            skPoint(sketch, "E105.16.7", {"position": v(-52.5, -55.08) * mm});
            skPoint(sketch, "E105.16.8", {"position": v(-53.5, -56.81) * mm});
            skArc(sketch, "E105.16.9", {"start": v(-54.36, -56.31) * mm, "mid": v(-53.6, -56.41) * mm, "end": v(-53, -55.94) * mm});
            skArc(sketch, "E105.16.10", {"start": v(-53, -55.95) * mm, "mid": v(-52.9, -55.19) * mm, "end": v(-53.36, -54.58) * mm});
            skPoint(sketch, "E105.17.0", {"position": v(-53.96, -49.2) * mm});
            skLineSegment(sketch, "E105.17.1", {"start": v(-56.63, -49.5) * mm, "end": v(-51.8, -50.8) * mm});
            skLineSegment(sketch, "E105.17.2", {"start": v(-56.11, -47.58) * mm, "end": v(-51.28, -48.87) * mm});
            skPoint(sketch, "E105.17.3", {"position": v(-57.08, -47.32) * mm});
            skPoint(sketch, "E105.17.4", {"position": v(-57.6, -49.25) * mm});
            skArc(sketch, "E105.17.5", {"start": v(-56.11, -47.58) * mm, "mid": v(-56.87, -47.68) * mm, "end": v(-57.34, -48.28) * mm});
            skArc(sketch, "E105.17.6", {"start": v(-57.34, -48.28) * mm, "mid": v(-57.24, -49.04) * mm, "end": v(-56.63, -49.5) * mm});
            skPoint(sketch, "E105.17.7", {"position": v(-50.32, -49.13) * mm});
            skPoint(sketch, "E105.17.8", {"position": v(-50.84, -51.06) * mm});
            skArc(sketch, "E105.17.9", {"start": v(-51.8, -50.8) * mm, "mid": v(-51.04, -50.7) * mm, "end": v(-50.58, -50.1) * mm});
            skArc(sketch, "E105.17.10", {"start": v(-50.58, -50.1) * mm, "mid": v(-50.68, -49.34) * mm, "end": v(-51.28, -48.87) * mm});
            skPoint(sketch, "E105.18.0", {"position": v(-53.25, -43.82) * mm});
            skLineSegment(sketch, "E105.18.1", {"start": v(-55.75, -44.82) * mm, "end": v(-50.75, -44.82) * mm});
            skLineSegment(sketch, "E105.18.2", {"start": v(-55.75, -42.82) * mm, "end": v(-50.75, -42.82) * mm});
            skPoint(sketch, "E105.18.3", {"position": v(-56.75, -42.82) * mm});
            skPoint(sketch, "E105.18.4", {"position": v(-56.75, -44.82) * mm});
            skArc(sketch, "E105.18.5", {"start": v(-55.75, -42.82) * mm, "mid": v(-56.46, -43.11) * mm, "end": v(-56.75, -43.82) * mm});
            skArc(sketch, "E105.18.6", {"start": v(-56.75, -43.82) * mm, "mid": v(-56.46, -44.53) * mm, "end": v(-55.75, -44.82) * mm});
            skPoint(sketch, "E105.18.7", {"position": v(-49.75, -42.82) * mm});
            skPoint(sketch, "E105.18.8", {"position": v(-49.75, -44.82) * mm});
            skArc(sketch, "E105.18.9", {"start": v(-50.75, -44.82) * mm, "mid": v(-50.04, -44.53) * mm, "end": v(-49.75, -43.82) * mm});
            skArc(sketch, "E105.18.10", {"start": v(-49.75, -43.82) * mm, "mid": v(-50.04, -43.11) * mm, "end": v(-50.75, -42.82) * mm});
            skPoint(sketch, "E105.19.0", {"position": v(-53.96, -38.45) * mm});
            skLineSegment(sketch, "E105.19.1", {"start": v(-56.11, -40.06) * mm, "end": v(-51.28, -38.77) * mm});
            skLineSegment(sketch, "E105.19.2", {"start": v(-56.63, -38.13) * mm, "end": v(-51.8, -36.84) * mm});
            skPoint(sketch, "E105.19.3", {"position": v(-57.6, -38.39) * mm});
            skPoint(sketch, "E105.19.4", {"position": v(-57.08, -40.32) * mm});
            skArc(sketch, "E105.19.5", {"start": v(-56.63, -38.13) * mm, "mid": v(-57.24, -38.6) * mm, "end": v(-57.34, -39.36) * mm});
            skArc(sketch, "E105.19.6", {"start": v(-57.34, -39.36) * mm, "mid": v(-56.87, -39.96) * mm, "end": v(-56.11, -40.06) * mm});
            skPoint(sketch, "E105.19.7", {"position": v(-50.84, -36.58) * mm});
            skPoint(sketch, "E105.19.8", {"position": v(-50.32, -38.5) * mm});
            skArc(sketch, "E105.19.9", {"start": v(-51.28, -38.77) * mm, "mid": v(-50.68, -38.3) * mm, "end": v(-50.58, -37.54) * mm});
            skArc(sketch, "E105.19.10", {"start": v(-50.58, -37.54) * mm, "mid": v(-51.04, -36.94) * mm, "end": v(-51.8, -36.84) * mm});
            skPoint(sketch, "E105.20.0", {"position": v(-56.03, -33.44) * mm});
            skLineSegment(sketch, "E105.20.1", {"start": v(-57.7, -35.56) * mm, "end": v(-53.36, -33.06) * mm});
            skLineSegment(sketch, "E105.20.2", {"start": v(-58.7, -33.83) * mm, "end": v(-54.36, -31.33) * mm});
            skPoint(sketch, "E105.20.3", {"position": v(-59.56, -34.33) * mm});
            skPoint(sketch, "E105.20.4", {"position": v(-58.56, -36.06) * mm});
            skArc(sketch, "E105.20.5", {"start": v(-58.7, -33.83) * mm, "mid": v(-59.16, -34.44) * mm, "end": v(-59.06, -35.2) * mm});
            skArc(sketch, "E105.20.6", {"start": v(-59.06, -35.2) * mm, "mid": v(-58.45, -35.66) * mm, "end": v(-57.7, -35.56) * mm});
            skPoint(sketch, "E105.20.7", {"position": v(-53.5, -30.83) * mm});
            skPoint(sketch, "E105.20.8", {"position": v(-52.5, -32.56) * mm});
            skArc(sketch, "E105.20.9", {"start": v(-53.36, -33.06) * mm, "mid": v(-52.9, -32.45) * mm, "end": v(-53, -31.7) * mm});
            skArc(sketch, "E105.20.10", {"start": v(-53, -31.7) * mm, "mid": v(-53.6, -31.23) * mm, "end": v(-54.36, -31.33) * mm});
            skPoint(sketch, "E105.21.0", {"position": v(-59.33, -29.15) * mm});
            skLineSegment(sketch, "E105.21.1", {"start": v(-60.39, -31.62) * mm, "end": v(-56.85, -28.09) * mm});
            skLineSegment(sketch, "E105.21.2", {"start": v(-61.8, -30.2) * mm, "end": v(-58.27, -26.67) * mm});
            skPoint(sketch, "E105.21.3", {"position": v(-62.5, -30.92) * mm});
            skPoint(sketch, "E105.21.4", {"position": v(-61.1, -32.33) * mm});
            skArc(sketch, "E105.21.5", {"start": v(-61.8, -30.2) * mm, "mid": v(-62.1, -30.92) * mm, "end": v(-61.8, -31.62) * mm});
            skArc(sketch, "E105.21.6", {"start": v(-61.8, -31.62) * mm, "mid": v(-61.1, -31.92) * mm, "end": v(-60.39, -31.62) * mm});
            skPoint(sketch, "E105.21.7", {"position": v(-57.56, -25.97) * mm});
            skPoint(sketch, "E105.21.8", {"position": v(-56.15, -27.38) * mm});
            skArc(sketch, "E105.21.9", {"start": v(-56.85, -28.09) * mm, "mid": v(-56.56, -27.38) * mm, "end": v(-56.85, -26.67) * mm});
            skArc(sketch, "E105.21.10", {"start": v(-56.85, -26.67) * mm, "mid": v(-57.56, -26.38) * mm, "end": v(-58.27, -26.67) * mm});
            skPoint(sketch, "E105.22.0", {"position": v(-63.62, -25.85) * mm});
            skLineSegment(sketch, "E105.22.1", {"start": v(-64, -28.52) * mm, "end": v(-61.5, -24.18) * mm});
            skLineSegment(sketch, "E105.22.2", {"start": v(-65.74, -27.52) * mm, "end": v(-63.24, -23.18) * mm});
            skPoint(sketch, "E105.22.3", {"position": v(-66.24, -28.38) * mm});
            skPoint(sketch, "E105.22.4", {"position": v(-64.5, -29.38) * mm});
            skArc(sketch, "E105.22.5", {"start": v(-65.74, -27.52) * mm, "mid": v(-65.84, -28.27) * mm, "end": v(-65.37, -28.88) * mm});
            skArc(sketch, "E105.22.6", {"start": v(-65.37, -28.88) * mm, "mid": v(-64.62, -28.98) * mm, "end": v(-64, -28.52) * mm});
            skPoint(sketch, "E105.22.7", {"position": v(-62.74, -22.32) * mm});
            skPoint(sketch, "E105.22.8", {"position": v(-61, -23.32) * mm});
            skArc(sketch, "E105.22.9", {"start": v(-61.5, -24.18) * mm, "mid": v(-61.4, -23.43) * mm, "end": v(-61.87, -22.82) * mm});
            skArc(sketch, "E105.22.10", {"start": v(-61.87, -22.82) * mm, "mid": v(-62.63, -22.72) * mm, "end": v(-63.24, -23.18) * mm});
            skPoint(sketch, "E105.23.0", {"position": v(-68.63, -23.78) * mm});
            skLineSegment(sketch, "E105.23.1", {"start": v(-68.31, -26.45) * mm, "end": v(-67.02, -21.62) * mm});
            skLineSegment(sketch, "E105.23.2", {"start": v(-70.24, -25.93) * mm, "end": v(-68.95, -21.1) * mm});
            skPoint(sketch, "E105.23.3", {"position": v(-70.5, -26.9) * mm});
            skPoint(sketch, "E105.23.4", {"position": v(-68.57, -27.42) * mm});
            skArc(sketch, "E105.23.5", {"start": v(-70.24, -25.93) * mm, "mid": v(-70.14, -26.7) * mm, "end": v(-69.54, -27.16) * mm});
            skArc(sketch, "E105.23.6", {"start": v(-69.54, -27.16) * mm, "mid": v(-68.78, -27.06) * mm, "end": v(-68.31, -26.45) * mm});
            skPoint(sketch, "E105.23.7", {"position": v(-68.69, -20.14) * mm});
            skPoint(sketch, "E105.23.8", {"position": v(-66.76, -20.66) * mm});
            skArc(sketch, "E105.23.9", {"start": v(-67.02, -21.62) * mm, "mid": v(-67.12, -20.86) * mm, "end": v(-67.72, -20.4) * mm});
            skArc(sketch, "E105.23.10", {"start": v(-67.72, -20.4) * mm, "mid": v(-68.48, -20.5) * mm, "end": v(-68.95, -21.1) * mm});
            skLineSegment(sketch, "E106.1.0", {"start": v(-123.59, -10.8) * mm, "end": v(-125.13, -6.04) * mm});
            skLineSegment(sketch, "E106.1.1", {"start": v(-121.68, -10.18) * mm, "end": v(-123.23, -5.42) * mm});
            skPoint(sketch, "E106.1.2", {"position": v(-123.28, -11.74) * mm});
            skLineSegment(sketch, "E106.1.3", {"start": v(-122.33, -11.44) * mm, "end": v(-122.33, -11.44) * mm});
            skPoint(sketch, "E106.1.4", {"position": v(-123.4, -8.1) * mm});
            skPoint(sketch, "E106.1.5", {"position": v(-121.38, -11.13) * mm});
            skArc(sketch, "E106.1.6", {"start": v(-123.59, -10.8) * mm, "mid": v(-123.09, -11.38) * mm, "end": v(-122.33, -11.44) * mm});
            skArc(sketch, "E106.1.7", {"start": v(-122.33, -11.44) * mm, "mid": v(-121.74, -10.94) * mm, "end": v(-121.68, -10.18) * mm});
            skLineSegment(sketch, "E106.1.8", {"start": v(-124.49, -4.78) * mm, "end": v(-124.49, -4.78) * mm});
            skPoint(sketch, "E106.1.9", {"position": v(-123.54, -4.47) * mm});
            skPoint(sketch, "E106.1.10", {"position": v(-125.44, -5.09) * mm});
            skArc(sketch, "E106.1.11", {"start": v(-123.23, -5.42) * mm, "mid": v(-123.73, -4.84) * mm, "end": v(-124.49, -4.78) * mm});
            skArc(sketch, "E106.1.12", {"start": v(-124.49, -4.78) * mm, "mid": v(-125.07, -5.27) * mm, "end": v(-125.13, -6.04) * mm});
            skLineSegment(sketch, "E106.2.0", {"start": v(-127.63, -13.2) * mm, "end": v(-130.56, -9.16) * mm});
            skLineSegment(sketch, "E106.2.1", {"start": v(-126, -12.03) * mm, "end": v(-128.95, -7.98) * mm});
            skPoint(sketch, "E106.2.2", {"position": v(-127.04, -14.01) * mm});
            skLineSegment(sketch, "E106.2.3", {"start": v(-126.23, -13.42) * mm, "end": v(-126.23, -13.42) * mm});
            skPoint(sketch, "E106.2.4", {"position": v(-128.29, -10.6) * mm});
            skPoint(sketch, "E106.2.5", {"position": v(-125.42, -12.84) * mm});
            skArc(sketch, "E106.2.6", {"start": v(-127.63, -13.2) * mm, "mid": v(-126.97, -13.6) * mm, "end": v(-126.23, -13.42) * mm});
            skArc(sketch, "E106.2.7", {"start": v(-126.23, -13.42) * mm, "mid": v(-125.83, -12.77) * mm, "end": v(-126, -12.03) * mm});
            skLineSegment(sketch, "E106.2.8", {"start": v(-130.34, -7.76) * mm, "end": v(-130.34, -7.76) * mm});
            skPoint(sketch, "E106.2.9", {"position": v(-129.53, -7.17) * mm});
            skPoint(sketch, "E106.2.10", {"position": v(-131.15, -8.35) * mm});
            skArc(sketch, "E106.2.11", {"start": v(-128.95, -7.98) * mm, "mid": v(-129.6, -7.58) * mm, "end": v(-130.34, -7.76) * mm});
            skArc(sketch, "E106.2.12", {"start": v(-130.34, -7.76) * mm, "mid": v(-130.74, -8.41) * mm, "end": v(-130.56, -9.16) * mm});
            skLineSegment(sketch, "E106.3.0", {"start": v(-130.72, -16.74) * mm, "end": v(-134.77, -13.8) * mm});
            skLineSegment(sketch, "E106.3.1", {"start": v(-129.55, -15.12) * mm, "end": v(-133.6, -12.19) * mm});
            skPoint(sketch, "E106.3.2", {"position": v(-129.91, -17.33) * mm});
            skLineSegment(sketch, "E106.3.3", {"start": v(-129.33, -16.52) * mm, "end": v(-129.33, -16.52) * mm});
            skPoint(sketch, "E106.3.4", {"position": v(-132.16, -14.46) * mm});
            skPoint(sketch, "E106.3.5", {"position": v(-128.74, -15.71) * mm});
            skArc(sketch, "E106.3.6", {"start": v(-130.72, -16.74) * mm, "mid": v(-129.98, -16.92) * mm, "end": v(-129.33, -16.52) * mm});
            skArc(sketch, "E106.3.7", {"start": v(-129.33, -16.52) * mm, "mid": v(-129.15, -15.78) * mm, "end": v(-129.55, -15.12) * mm});
            skLineSegment(sketch, "E106.3.8", {"start": v(-134.99, -12.4) * mm, "end": v(-134.99, -12.4) * mm});
            skPoint(sketch, "E106.3.9", {"position": v(-134.4, -11.6) * mm});
            skPoint(sketch, "E106.3.10", {"position": v(-135.58, -13.22) * mm});
            skArc(sketch, "E106.3.11", {"start": v(-133.6, -12.19) * mm, "mid": v(-134.34, -12) * mm, "end": v(-134.99, -12.4) * mm});
            skArc(sketch, "E106.3.12", {"start": v(-134.99, -12.4) * mm, "mid": v(-135.17, -13.15) * mm, "end": v(-134.77, -13.8) * mm});
            skLineSegment(sketch, "E106.4.0", {"start": v(-132.57, -21.07) * mm, "end": v(-137.33, -19.52) * mm});
            skLineSegment(sketch, "E106.4.1", {"start": v(-131.96, -19.16) * mm, "end": v(-136.71, -17.62) * mm});
            skPoint(sketch, "E106.4.2", {"position": v(-131.62, -21.37) * mm});
            skLineSegment(sketch, "E106.4.3", {"start": v(-131.31, -20.42) * mm, "end": v(-131.31, -20.42) * mm});
            skPoint(sketch, "E106.4.4", {"position": v(-134.64, -19.34) * mm});
            skPoint(sketch, "E106.4.5", {"position": v(-131, -19.47) * mm});
            skArc(sketch, "E106.4.6", {"start": v(-132.57, -21.07) * mm, "mid": v(-131.81, -21) * mm, "end": v(-131.31, -20.42) * mm});
            skArc(sketch, "E106.4.7", {"start": v(-131.31, -20.42) * mm, "mid": v(-131.37, -19.66) * mm, "end": v(-131.96, -19.16) * mm});
            skLineSegment(sketch, "E106.4.8", {"start": v(-137.97, -18.26) * mm, "end": v(-137.97, -18.26) * mm});
            skPoint(sketch, "E106.4.9", {"position": v(-137.66, -17.3) * mm});
            skPoint(sketch, "E106.4.10", {"position": v(-138.28, -19.21) * mm});
            skArc(sketch, "E106.4.11", {"start": v(-136.71, -17.62) * mm, "mid": v(-137.48, -17.68) * mm, "end": v(-137.97, -18.26) * mm});
            skArc(sketch, "E106.4.12", {"start": v(-137.97, -18.26) * mm, "mid": v(-137.91, -19.02) * mm, "end": v(-137.33, -19.52) * mm});
            skLineSegment(sketch, "E106.5.0", {"start": v(-133, -25.75) * mm, "end": v(-138, -25.75) * mm});
            skLineSegment(sketch, "E106.5.1", {"start": v(-133, -23.75) * mm, "end": v(-138, -23.75) * mm});
            skPoint(sketch, "E106.5.2", {"position": v(-132, -25.75) * mm});
            skLineSegment(sketch, "E106.5.3", {"start": v(-132, -24.75) * mm, "end": v(-132, -24.75) * mm});
            skPoint(sketch, "E106.5.4", {"position": v(-135.5, -24.75) * mm});
            skPoint(sketch, "E106.5.5", {"position": v(-132, -23.75) * mm});
            skArc(sketch, "E106.5.6", {"start": v(-133, -25.75) * mm, "mid": v(-132.3, -25.46) * mm, "end": v(-132, -24.75) * mm});
            skArc(sketch, "E106.5.7", {"start": v(-132, -24.75) * mm, "mid": v(-132.3, -24.04) * mm, "end": v(-133, -23.75) * mm});
            skLineSegment(sketch, "E106.5.8", {"start": v(-139, -24.75) * mm, "end": v(-139, -24.75) * mm});
            skPoint(sketch, "E106.5.9", {"position": v(-139, -23.75) * mm});
            skPoint(sketch, "E106.5.10", {"position": v(-139, -25.75) * mm});
            skArc(sketch, "E106.5.11", {"start": v(-138, -23.75) * mm, "mid": v(-138.7, -24.04) * mm, "end": v(-139, -24.75) * mm});
            skArc(sketch, "E106.5.12", {"start": v(-139, -24.75) * mm, "mid": v(-138.7, -25.46) * mm, "end": v(-138, -25.75) * mm});
            skLineSegment(sketch, "E106.6.0", {"start": v(-131.96, -30.34) * mm, "end": v(-136.71, -31.88) * mm});
            skLineSegment(sketch, "E106.6.1", {"start": v(-132.57, -28.43) * mm, "end": v(-137.33, -29.98) * mm});
            skPoint(sketch, "E106.6.2", {"position": v(-131, -30.03) * mm});
            skLineSegment(sketch, "E106.6.3", {"start": v(-131.31, -29.08) * mm, "end": v(-131.31, -29.08) * mm});
            skPoint(sketch, "E106.6.4", {"position": v(-134.64, -30.16) * mm});
            skPoint(sketch, "E106.6.5", {"position": v(-131.62, -28.13) * mm});
            skArc(sketch, "E106.6.6", {"start": v(-131.96, -30.34) * mm, "mid": v(-131.37, -29.84) * mm, "end": v(-131.31, -29.08) * mm});
            skArc(sketch, "E106.6.7", {"start": v(-131.31, -29.08) * mm, "mid": v(-131.81, -28.5) * mm, "end": v(-132.57, -28.43) * mm});
            skLineSegment(sketch, "E106.6.8", {"start": v(-137.97, -31.24) * mm, "end": v(-137.97, -31.24) * mm});
            skPoint(sketch, "E106.6.9", {"position": v(-138.28, -30.29) * mm});
            skPoint(sketch, "E106.6.10", {"position": v(-137.66, -32.2) * mm});
            skArc(sketch, "E106.6.11", {"start": v(-137.33, -29.98) * mm, "mid": v(-137.91, -30.48) * mm, "end": v(-137.97, -31.24) * mm});
            skArc(sketch, "E106.6.12", {"start": v(-137.97, -31.24) * mm, "mid": v(-137.48, -31.82) * mm, "end": v(-136.71, -31.88) * mm});
            skLineSegment(sketch, "E106.7.0", {"start": v(-129.55, -34.38) * mm, "end": v(-133.6, -37.31) * mm});
            skLineSegment(sketch, "E106.7.1", {"start": v(-130.72, -32.76) * mm, "end": v(-134.77, -35.7) * mm});
            skPoint(sketch, "E106.7.2", {"position": v(-128.74, -33.79) * mm});
            skLineSegment(sketch, "E106.7.3", {"start": v(-129.33, -32.98) * mm, "end": v(-129.33, -32.98) * mm});
            skPoint(sketch, "E106.7.4", {"position": v(-132.16, -35.04) * mm});
            skPoint(sketch, "E106.7.5", {"position": v(-129.91, -32.17) * mm});
            skArc(sketch, "E106.7.6", {"start": v(-129.55, -34.38) * mm, "mid": v(-129.15, -33.72) * mm, "end": v(-129.33, -32.98) * mm});
            skArc(sketch, "E106.7.7", {"start": v(-129.33, -32.98) * mm, "mid": v(-129.98, -32.58) * mm, "end": v(-130.72, -32.76) * mm});
            skLineSegment(sketch, "E106.7.8", {"start": v(-134.99, -37.1) * mm, "end": v(-134.99, -37.1) * mm});
            skPoint(sketch, "E106.7.9", {"position": v(-135.58, -36.28) * mm});
            skPoint(sketch, "E106.7.10", {"position": v(-134.4, -37.9) * mm});
            skArc(sketch, "E106.7.11", {"start": v(-134.77, -35.7) * mm, "mid": v(-135.17, -36.35) * mm, "end": v(-134.99, -37.1) * mm});
            skArc(sketch, "E106.7.12", {"start": v(-134.99, -37.1) * mm, "mid": v(-134.34, -37.5) * mm, "end": v(-133.6, -37.31) * mm});
            skLineSegment(sketch, "E106.8.0", {"start": v(-126, -37.47) * mm, "end": v(-128.95, -41.52) * mm});
            skLineSegment(sketch, "E106.8.1", {"start": v(-127.63, -36.3) * mm, "end": v(-130.56, -40.34) * mm});
            skPoint(sketch, "E106.8.2", {"position": v(-125.42, -36.66) * mm});
            skLineSegment(sketch, "E106.8.3", {"start": v(-126.23, -36.08) * mm, "end": v(-126.23, -36.08) * mm});
            skPoint(sketch, "E106.8.4", {"position": v(-128.29, -38.9) * mm});
            skPoint(sketch, "E106.8.5", {"position": v(-127.04, -35.49) * mm});
            skArc(sketch, "E106.8.6", {"start": v(-126, -37.47) * mm, "mid": v(-125.83, -36.73) * mm, "end": v(-126.23, -36.08) * mm});
            skArc(sketch, "E106.8.7", {"start": v(-126.23, -36.08) * mm, "mid": v(-126.97, -35.9) * mm, "end": v(-127.63, -36.3) * mm});
            skLineSegment(sketch, "E106.8.8", {"start": v(-130.34, -41.74) * mm, "end": v(-130.34, -41.74) * mm});
            skPoint(sketch, "E106.8.9", {"position": v(-131.15, -41.15) * mm});
            skPoint(sketch, "E106.8.10", {"position": v(-129.53, -42.33) * mm});
            skArc(sketch, "E106.8.11", {"start": v(-130.56, -40.34) * mm, "mid": v(-130.74, -41.09) * mm, "end": v(-130.34, -41.74) * mm});
            skArc(sketch, "E106.8.12", {"start": v(-130.34, -41.74) * mm, "mid": v(-129.6, -41.92) * mm, "end": v(-128.95, -41.52) * mm});
            skLineSegment(sketch, "E106.9.0", {"start": v(-121.68, -39.32) * mm, "end": v(-123.23, -44.08) * mm});
            skLineSegment(sketch, "E106.9.1", {"start": v(-123.59, -38.7) * mm, "end": v(-125.13, -43.46) * mm});
            skPoint(sketch, "E106.9.2", {"position": v(-121.38, -38.37) * mm});
            skLineSegment(sketch, "E106.9.3", {"start": v(-122.33, -38.06) * mm, "end": v(-122.33, -38.06) * mm});
            skPoint(sketch, "E106.9.4", {"position": v(-123.4, -41.4) * mm});
            skPoint(sketch, "E106.9.5", {"position": v(-123.28, -37.76) * mm});
            skArc(sketch, "E106.9.6", {"start": v(-121.68, -39.32) * mm, "mid": v(-121.74, -38.56) * mm, "end": v(-122.33, -38.06) * mm});
            skArc(sketch, "E106.9.7", {"start": v(-122.33, -38.06) * mm, "mid": v(-123.09, -38.12) * mm, "end": v(-123.59, -38.7) * mm});
            skLineSegment(sketch, "E106.9.8", {"start": v(-124.49, -44.72) * mm, "end": v(-124.49, -44.72) * mm});
            skPoint(sketch, "E106.9.9", {"position": v(-125.44, -44.41) * mm});
            skPoint(sketch, "E106.9.10", {"position": v(-123.54, -45.03) * mm});
            skArc(sketch, "E106.9.11", {"start": v(-125.13, -43.46) * mm, "mid": v(-125.07, -44.23) * mm, "end": v(-124.49, -44.72) * mm});
            skArc(sketch, "E106.9.12", {"start": v(-124.49, -44.72) * mm, "mid": v(-123.73, -44.66) * mm, "end": v(-123.23, -44.08) * mm});
            skLineSegment(sketch, "E106.10.0", {"start": v(-117, -39.75) * mm, "end": v(-117, -44.75) * mm});
            skLineSegment(sketch, "E106.10.1", {"start": v(-119, -39.75) * mm, "end": v(-119, -44.75) * mm});
            skPoint(sketch, "E106.10.2", {"position": v(-117, -38.75) * mm});
            skLineSegment(sketch, "E106.10.3", {"start": v(-118, -38.75) * mm, "end": v(-118, -38.75) * mm});
            skPoint(sketch, "E106.10.4", {"position": v(-118, -42.25) * mm});
            skPoint(sketch, "E106.10.5", {"position": v(-119, -38.75) * mm});
            skArc(sketch, "E106.10.6", {"start": v(-117, -39.75) * mm, "mid": v(-117.3, -39.04) * mm, "end": v(-118, -38.75) * mm});
            skArc(sketch, "E106.10.7", {"start": v(-118, -38.75) * mm, "mid": v(-118.7, -39.04) * mm, "end": v(-119, -39.75) * mm});
            skLineSegment(sketch, "E106.10.8", {"start": v(-118, -45.75) * mm, "end": v(-118, -45.75) * mm});
            skPoint(sketch, "E106.10.9", {"position": v(-119, -45.75) * mm});
            skPoint(sketch, "E106.10.10", {"position": v(-117, -45.75) * mm});
            skArc(sketch, "E106.10.11", {"start": v(-119, -44.75) * mm, "mid": v(-118.7, -45.46) * mm, "end": v(-118, -45.75) * mm});
            skArc(sketch, "E106.10.12", {"start": v(-118, -45.75) * mm, "mid": v(-117.3, -45.46) * mm, "end": v(-117, -44.75) * mm});
            skLineSegment(sketch, "E106.11.0", {"start": v(-112.41, -38.7) * mm, "end": v(-110.87, -43.46) * mm});
            skLineSegment(sketch, "E106.11.1", {"start": v(-114.32, -39.32) * mm, "end": v(-112.77, -44.08) * mm});
            skPoint(sketch, "E106.11.2", {"position": v(-112.72, -37.76) * mm});
            skLineSegment(sketch, "E106.11.3", {"start": v(-113.67, -38.06) * mm, "end": v(-113.67, -38.06) * mm});
            skPoint(sketch, "E106.11.4", {"position": v(-112.6, -41.4) * mm});
            skPoint(sketch, "E106.11.5", {"position": v(-114.62, -38.37) * mm});
            skArc(sketch, "E106.11.6", {"start": v(-112.41, -38.7) * mm, "mid": v(-112.91, -38.12) * mm, "end": v(-113.67, -38.06) * mm});
            skArc(sketch, "E106.11.7", {"start": v(-113.67, -38.06) * mm, "mid": v(-114.26, -38.56) * mm, "end": v(-114.32, -39.32) * mm});
            skLineSegment(sketch, "E106.11.8", {"start": v(-111.51, -44.72) * mm, "end": v(-111.51, -44.72) * mm});
            skPoint(sketch, "E106.11.9", {"position": v(-112.46, -45.03) * mm});
            skPoint(sketch, "E106.11.10", {"position": v(-110.56, -44.41) * mm});
            skArc(sketch, "E106.11.11", {"start": v(-112.77, -44.08) * mm, "mid": v(-112.27, -44.66) * mm, "end": v(-111.51, -44.72) * mm});
            skArc(sketch, "E106.11.12", {"start": v(-111.51, -44.72) * mm, "mid": v(-110.93, -44.23) * mm, "end": v(-110.87, -43.46) * mm});
            skLineSegment(sketch, "E106.12.0", {"start": v(-108.37, -36.3) * mm, "end": v(-105.44, -40.34) * mm});
            skLineSegment(sketch, "E106.12.1", {"start": v(-110, -37.47) * mm, "end": v(-107.05, -41.52) * mm});
            skPoint(sketch, "E106.12.2", {"position": v(-108.96, -35.49) * mm});
            skLineSegment(sketch, "E106.12.3", {"start": v(-109.77, -36.08) * mm, "end": v(-109.77, -36.08) * mm});
            skPoint(sketch, "E106.12.4", {"position": v(-107.71, -38.9) * mm});
            skPoint(sketch, "E106.12.5", {"position": v(-110.58, -36.66) * mm});
            skArc(sketch, "E106.12.6", {"start": v(-108.37, -36.3) * mm, "mid": v(-109.03, -35.9) * mm, "end": v(-109.77, -36.08) * mm});
            skArc(sketch, "E106.12.7", {"start": v(-109.77, -36.08) * mm, "mid": v(-110.17, -36.73) * mm, "end": v(-110, -37.47) * mm});
            skLineSegment(sketch, "E106.12.8", {"start": v(-105.66, -41.74) * mm, "end": v(-105.66, -41.74) * mm});
            skPoint(sketch, "E106.12.9", {"position": v(-106.47, -42.33) * mm});
            skPoint(sketch, "E106.12.10", {"position": v(-104.85, -41.15) * mm});
            skArc(sketch, "E106.12.11", {"start": v(-107.05, -41.52) * mm, "mid": v(-106.4, -41.92) * mm, "end": v(-105.66, -41.74) * mm});
            skArc(sketch, "E106.12.12", {"start": v(-105.66, -41.74) * mm, "mid": v(-105.26, -41.09) * mm, "end": v(-105.44, -40.34) * mm});
            skLineSegment(sketch, "E106.13.0", {"start": v(-105.28, -32.76) * mm, "end": v(-101.23, -35.7) * mm});
            skLineSegment(sketch, "E106.13.1", {"start": v(-106.45, -34.38) * mm, "end": v(-102.4, -37.31) * mm});
            skPoint(sketch, "E106.13.2", {"position": v(-106.09, -32.17) * mm});
            skLineSegment(sketch, "E106.13.3", {"start": v(-106.67, -32.98) * mm, "end": v(-106.67, -32.98) * mm});
            skPoint(sketch, "E106.13.4", {"position": v(-103.84, -35.04) * mm});
            skPoint(sketch, "E106.13.5", {"position": v(-107.26, -33.79) * mm});
            skArc(sketch, "E106.13.6", {"start": v(-105.28, -32.76) * mm, "mid": v(-106.02, -32.58) * mm, "end": v(-106.67, -32.98) * mm});
            skArc(sketch, "E106.13.7", {"start": v(-106.67, -32.98) * mm, "mid": v(-106.85, -33.72) * mm, "end": v(-106.45, -34.38) * mm});
            skLineSegment(sketch, "E106.13.8", {"start": v(-101.01, -37.1) * mm, "end": v(-101.01, -37.1) * mm});
            skPoint(sketch, "E106.13.9", {"position": v(-101.6, -37.9) * mm});
            skPoint(sketch, "E106.13.10", {"position": v(-100.42, -36.28) * mm});
            skArc(sketch, "E106.13.11", {"start": v(-102.4, -37.31) * mm, "mid": v(-101.66, -37.5) * mm, "end": v(-101.01, -37.1) * mm});
            skArc(sketch, "E106.13.12", {"start": v(-101.01, -37.1) * mm, "mid": v(-100.83, -36.35) * mm, "end": v(-101.23, -35.7) * mm});
            skLineSegment(sketch, "E106.14.0", {"start": v(-103.43, -28.43) * mm, "end": v(-98.67, -29.98) * mm});
            skLineSegment(sketch, "E106.14.1", {"start": v(-104.04, -30.34) * mm, "end": v(-99.29, -31.88) * mm});
            skPoint(sketch, "E106.14.2", {"position": v(-104.38, -28.13) * mm});
            skLineSegment(sketch, "E106.14.3", {"start": v(-104.69, -29.08) * mm, "end": v(-104.69, -29.08) * mm});
            skPoint(sketch, "E106.14.4", {"position": v(-101.36, -30.16) * mm});
            skPoint(sketch, "E106.14.5", {"position": v(-105, -30.03) * mm});
            skArc(sketch, "E106.14.6", {"start": v(-103.43, -28.43) * mm, "mid": v(-104.19, -28.5) * mm, "end": v(-104.69, -29.08) * mm});
            skArc(sketch, "E106.14.7", {"start": v(-104.69, -29.08) * mm, "mid": v(-104.63, -29.84) * mm, "end": v(-104.04, -30.34) * mm});
            skLineSegment(sketch, "E106.14.8", {"start": v(-98.03, -31.24) * mm, "end": v(-98.03, -31.24) * mm});
            skPoint(sketch, "E106.14.9", {"position": v(-98.34, -32.2) * mm});
            skPoint(sketch, "E106.14.10", {"position": v(-97.72, -30.29) * mm});
            skArc(sketch, "E106.14.11", {"start": v(-99.29, -31.88) * mm, "mid": v(-98.52, -31.82) * mm, "end": v(-98.03, -31.24) * mm});
            skArc(sketch, "E106.14.12", {"start": v(-98.03, -31.24) * mm, "mid": v(-98.09, -30.48) * mm, "end": v(-98.67, -29.98) * mm});
            skLineSegment(sketch, "E106.15.0", {"start": v(-103, -23.75) * mm, "end": v(-98, -23.75) * mm});
            skLineSegment(sketch, "E106.15.1", {"start": v(-103, -25.75) * mm, "end": v(-98, -25.75) * mm});
            skPoint(sketch, "E106.15.2", {"position": v(-104, -23.75) * mm});
            skLineSegment(sketch, "E106.15.3", {"start": v(-104, -24.75) * mm, "end": v(-104, -24.75) * mm});
            skPoint(sketch, "E106.15.4", {"position": v(-100.5, -24.75) * mm});
            skPoint(sketch, "E106.15.5", {"position": v(-104, -25.75) * mm});
            skArc(sketch, "E106.15.6", {"start": v(-103, -23.75) * mm, "mid": v(-103.7, -24.04) * mm, "end": v(-104, -24.75) * mm});
            skArc(sketch, "E106.15.7", {"start": v(-104, -24.75) * mm, "mid": v(-103.7, -25.46) * mm, "end": v(-103, -25.75) * mm});
            skLineSegment(sketch, "E106.15.8", {"start": v(-97, -24.75) * mm, "end": v(-97, -24.75) * mm});
            skPoint(sketch, "E106.15.9", {"position": v(-97, -25.75) * mm});
            skPoint(sketch, "E106.15.10", {"position": v(-97, -23.75) * mm});
            skArc(sketch, "E106.15.11", {"start": v(-98, -25.75) * mm, "mid": v(-97.3, -25.46) * mm, "end": v(-97, -24.75) * mm});
            skArc(sketch, "E106.15.12", {"start": v(-97, -24.75) * mm, "mid": v(-97.3, -24.04) * mm, "end": v(-98, -23.75) * mm});
            skLineSegment(sketch, "E106.16.0", {"start": v(-104.04, -19.16) * mm, "end": v(-99.29, -17.62) * mm});
            skLineSegment(sketch, "E106.16.1", {"start": v(-103.43, -21.07) * mm, "end": v(-98.67, -19.52) * mm});
            skPoint(sketch, "E106.16.2", {"position": v(-105, -19.47) * mm});
            skLineSegment(sketch, "E106.16.3", {"start": v(-104.69, -20.42) * mm, "end": v(-104.69, -20.42) * mm});
            skPoint(sketch, "E106.16.4", {"position": v(-101.36, -19.34) * mm});
            skPoint(sketch, "E106.16.5", {"position": v(-104.38, -21.37) * mm});
            skArc(sketch, "E106.16.6", {"start": v(-104.04, -19.16) * mm, "mid": v(-104.63, -19.66) * mm, "end": v(-104.69, -20.42) * mm});
            skArc(sketch, "E106.16.7", {"start": v(-104.69, -20.42) * mm, "mid": v(-104.19, -21) * mm, "end": v(-103.43, -21.07) * mm});
            skLineSegment(sketch, "E106.16.8", {"start": v(-98.03, -18.26) * mm, "end": v(-98.03, -18.26) * mm});
            skPoint(sketch, "E106.16.9", {"position": v(-97.72, -19.21) * mm});
            skPoint(sketch, "E106.16.10", {"position": v(-98.34, -17.3) * mm});
            skArc(sketch, "E106.16.11", {"start": v(-98.67, -19.52) * mm, "mid": v(-98.09, -19.02) * mm, "end": v(-98.03, -18.26) * mm});
            skArc(sketch, "E106.16.12", {"start": v(-98.03, -18.26) * mm, "mid": v(-98.52, -17.68) * mm, "end": v(-99.29, -17.62) * mm});
            skLineSegment(sketch, "E106.17.0", {"start": v(-106.45, -15.12) * mm, "end": v(-102.4, -12.19) * mm});
            skLineSegment(sketch, "E106.17.1", {"start": v(-105.28, -16.74) * mm, "end": v(-101.23, -13.8) * mm});
            skPoint(sketch, "E106.17.2", {"position": v(-107.26, -15.71) * mm});
            skLineSegment(sketch, "E106.17.3", {"start": v(-106.67, -16.52) * mm, "end": v(-106.67, -16.52) * mm});
            skPoint(sketch, "E106.17.4", {"position": v(-103.84, -14.46) * mm});
            skPoint(sketch, "E106.17.5", {"position": v(-106.09, -17.33) * mm});
            skArc(sketch, "E106.17.6", {"start": v(-106.45, -15.12) * mm, "mid": v(-106.85, -15.78) * mm, "end": v(-106.67, -16.52) * mm});
            skArc(sketch, "E106.17.7", {"start": v(-106.67, -16.52) * mm, "mid": v(-106.02, -16.92) * mm, "end": v(-105.28, -16.74) * mm});
            skLineSegment(sketch, "E106.17.8", {"start": v(-101.01, -12.4) * mm, "end": v(-101.01, -12.4) * mm});
            skPoint(sketch, "E106.17.9", {"position": v(-100.42, -13.22) * mm});
            skPoint(sketch, "E106.17.10", {"position": v(-101.6, -11.6) * mm});
            skArc(sketch, "E106.17.11", {"start": v(-101.23, -13.8) * mm, "mid": v(-100.83, -13.15) * mm, "end": v(-101.01, -12.4) * mm});
            skArc(sketch, "E106.17.12", {"start": v(-101.01, -12.4) * mm, "mid": v(-101.66, -12) * mm, "end": v(-102.4, -12.19) * mm});
            skLineSegment(sketch, "E106.18.0", {"start": v(-110, -12.03) * mm, "end": v(-107.05, -7.98) * mm});
            skLineSegment(sketch, "E106.18.1", {"start": v(-108.37, -13.2) * mm, "end": v(-105.44, -9.16) * mm});
            skPoint(sketch, "E106.18.2", {"position": v(-110.58, -12.84) * mm});
            skLineSegment(sketch, "E106.18.3", {"start": v(-109.77, -13.42) * mm, "end": v(-109.77, -13.42) * mm});
            skPoint(sketch, "E106.18.4", {"position": v(-107.71, -10.6) * mm});
            skPoint(sketch, "E106.18.5", {"position": v(-108.96, -14.01) * mm});
            skArc(sketch, "E106.18.6", {"start": v(-110, -12.03) * mm, "mid": v(-110.17, -12.77) * mm, "end": v(-109.77, -13.42) * mm});
            skArc(sketch, "E106.18.7", {"start": v(-109.77, -13.42) * mm, "mid": v(-109.03, -13.6) * mm, "end": v(-108.37, -13.2) * mm});
            skLineSegment(sketch, "E106.18.8", {"start": v(-105.66, -7.76) * mm, "end": v(-105.66, -7.76) * mm});
            skPoint(sketch, "E106.18.9", {"position": v(-104.85, -8.35) * mm});
            skPoint(sketch, "E106.18.10", {"position": v(-106.47, -7.17) * mm});
            skArc(sketch, "E106.18.11", {"start": v(-105.44, -9.16) * mm, "mid": v(-105.26, -8.41) * mm, "end": v(-105.66, -7.76) * mm});
            skArc(sketch, "E106.18.12", {"start": v(-105.66, -7.76) * mm, "mid": v(-106.4, -7.58) * mm, "end": v(-107.05, -7.98) * mm});
            skLineSegment(sketch, "E106.19.0", {"start": v(-114.32, -10.18) * mm, "end": v(-112.77, -5.42) * mm});
            skLineSegment(sketch, "E106.19.1", {"start": v(-112.41, -10.8) * mm, "end": v(-110.87, -6.04) * mm});
            skPoint(sketch, "E106.19.2", {"position": v(-114.62, -11.13) * mm});
            skLineSegment(sketch, "E106.19.3", {"start": v(-113.67, -11.44) * mm, "end": v(-113.67, -11.44) * mm});
            skPoint(sketch, "E106.19.4", {"position": v(-112.6, -8.1) * mm});
            skPoint(sketch, "E106.19.5", {"position": v(-112.72, -11.74) * mm});
            skArc(sketch, "E106.19.6", {"start": v(-114.32, -10.18) * mm, "mid": v(-114.26, -10.94) * mm, "end": v(-113.67, -11.44) * mm});
            skArc(sketch, "E106.19.7", {"start": v(-113.67, -11.44) * mm, "mid": v(-112.91, -11.38) * mm, "end": v(-112.41, -10.8) * mm});
            skLineSegment(sketch, "E106.19.8", {"start": v(-111.51, -4.78) * mm, "end": v(-111.51, -4.78) * mm});
            skPoint(sketch, "E106.19.9", {"position": v(-110.56, -5.09) * mm});
            skPoint(sketch, "E106.19.10", {"position": v(-112.46, -4.47) * mm});
            skArc(sketch, "E106.19.11", {"start": v(-110.87, -6.04) * mm, "mid": v(-110.93, -5.27) * mm, "end": v(-111.51, -4.78) * mm});
            skArc(sketch, "E106.19.12", {"start": v(-111.51, -4.78) * mm, "mid": v(-112.27, -4.84) * mm, "end": v(-112.77, -5.42) * mm});
            skSolve(sketch);
        }
        {
            var Q0;
            Q0=makeQuery(id+"F0.imprint","IMPRINT",FACE,{"disambiguationData":[TD([[makeQuery(id+"F0.imprint","IMPRINT",EDGE,{"derivedFrom":sQuery(id+"F0.wireOp",EDGE,"E0.bottom")}),-1.0]])]});
            extrude(context, id + "F1", {"entities" : qUnion([Q0]), "oppositeDirection" : true, "depth" : 3 * mm});
        }
        {
            var Q0;
            Q0=sQuery(id+"F0.wireOp",VERTEX,"E30");
            var Q1;
            Q1=sQuery(id+"F0.wireOp",VERTEX,"E31");
            var Q2;
            Q2=sQuery(id+"F0.wireOp",VERTEX,"E33");
            var Q3;
            Q3=sQuery(id+"F0.wireOp",VERTEX,"E34");
            var Q4;
            Q4=sQuery(id+"F0.wireOp",VERTEX,"E35");
            var Q5;
            Q5=sQuery(id+"F0.wireOp",VERTEX,"E36");
            var Q6;
            Q6=sQuery(id+"F0.wireOp",VERTEX,"E37");
            var Q7;
            Q7=sQuery(id+"F0.wireOp",VERTEX,"E32");
            var Q8;
            Q8=makeQuery(id+"F1.opExtrude","SWEPT_BODY",BODY,{"disambiguationData":[OSD([sQuery(id+"F0.wireOp",EDGE,"E0.bottom"),sQuery(id+"F0.wireOp",EDGE,"E0.top"),sQuery(id+"F0.wireOp",EDGE,"E0.left"),sQuery(id+"F0.wireOp",EDGE,"E0.right"),sQuery(id+"F0.wireOp",EDGE,"E10"),sQuery(id+"F0.wireOp",EDGE,"E11"),sQuery(id+"F0.wireOp",EDGE,"E12"),sQuery(id+"F0.wireOp",EDGE,"E13"),sQuery(id+"F0.wireOp",EDGE,"E14"),sQuery(id+"F0.wireOp",EDGE,"E15"),sQuery(id+"F0.wireOp",EDGE,"E16.bottom"),sQuery(id+"F0.wireOp",EDGE,"E16.top"),sQuery(id+"F0.wireOp",EDGE,"E16.left"),sQuery(id+"F0.wireOp",EDGE,"E16.right"),sQuery(id+"F0.wireOp",EDGE,"E20"),sQuery(id+"F0.wireOp",EDGE,"E21"),sQuery(id+"F0.wireOp",EDGE,"E22"),sQuery(id+"F0.wireOp",EDGE,"E23")])]});
            hole(context, id + "F2", {"style" : HoleStyle.C_BORE, "endStyle" : HoleEndStyle.THROUGH, "holeDiameter" : 3.5 * mm, "cBoreDiameter" : 6.5 * mm, "cBoreDepth" : 2 * mm, "startFromSketch" : true, "locations" : qUnion([Q0, Q1, Q2, Q3, Q4, Q5, Q6, Q7]), "scope" : qUnion([Q8]), "isTappedThrough" : true});
        }
        {
            var Q0;
            Q0=qCreatedBy(makeId("Top.planeOp"),FACE);
            var sketch = newSketch(context, id + "F3", { "sketchPlane" : qUnion([Q0])});
            skLineSegment(sketch, "E107", {"start": v(-241.07, 95.9) * mm, "end": v(240.37, 95.9) * mm, "construction": true});
            skLineSegment(sketch, "E108", {"start": v(-254.45, -95.89) * mm, "end": v(246.64, -95.89) * mm, "construction": true});
            skLineSegment(sketch, "E109", {"start": v(52.1, 143.84) * mm, "end": v(52.1, -148.82) * mm, "construction": true});
            skLineSegment(sketch, "E110", {"start": v(-31.7, 150.11) * mm, "end": v(-31.7, -148.82) * mm, "construction": true});
            skLineSegment(sketch, "E111", {"start": v(-107.9, 143.06) * mm, "end": v(-107.9, -148.82) * mm, "construction": true});
            skLineSegment(sketch, "E112", {"start": v(-170.1, 148.94) * mm, "end": v(-170.1, -156.27) * mm, "construction": true});
            skLineSegment(sketch, "E113", {"start": v(-266.6, 0) * mm, "end": v(236.06, 0) * mm, "construction": true});
            skPoint(sketch, "E114", {"position": v(-170.1, 95.9) * mm});
            skPoint(sketch, "E115", {"position": v(-107.9, 95.9) * mm});
            skPoint(sketch, "E116", {"position": v(52.1, 95.9) * mm});
            skPoint(sketch, "E117", {"position": v(-31.7, 0) * mm});
            skPoint(sketch, "E118", {"position": v(-107.9, 0) * mm});
            skPoint(sketch, "E119", {"position": v(-170.1, 0) * mm});
            skPoint(sketch, "E120", {"position": v(52.1, 0) * mm});
            skPoint(sketch, "E121", {"position": v(52.1, -95.89) * mm});
            skPoint(sketch, "E122", {"position": v(-107.9, -95.89) * mm});
            skPoint(sketch, "E123", {"position": v(-170.1, -95.89) * mm});
            skSolve(sketch);
        }
        {
            var Q0;
            Q0=sQuery(id+"F3.wireOp",VERTEX,"E114");
            var Q1;
            Q1=sQuery(id+"F3.wireOp",VERTEX,"E115");
            var Q2;
            Q2=sQuery(id+"F3.wireOp",VERTEX,"E116");
            var Q3;
            Q3=sQuery(id+"F3.wireOp",VERTEX,"E120");
            var Q4;
            Q4=sQuery(id+"F3.wireOp",VERTEX,"E117");
            var Q5;
            Q5=sQuery(id+"F3.wireOp",VERTEX,"E118");
            var Q6;
            Q6=sQuery(id+"F3.wireOp",VERTEX,"E119");
            var Q7;
            Q7=sQuery(id+"F3.wireOp",VERTEX,"E123");
            var Q8;
            Q8=sQuery(id+"F3.wireOp",VERTEX,"E122");
            var Q9;
            Q9=sQuery(id+"F3.wireOp",VERTEX,"E121");
            var Q10;
            Q10=makeQuery(id+"F1.opExtrude","SWEPT_BODY",BODY,{"disambiguationData":[OSD([sQuery(id+"F0.wireOp",EDGE,"E0.bottom"),sQuery(id+"F0.wireOp",EDGE,"E0.top"),sQuery(id+"F0.wireOp",EDGE,"E0.left"),sQuery(id+"F0.wireOp",EDGE,"E0.right"),sQuery(id+"F0.wireOp",EDGE,"E10"),sQuery(id+"F0.wireOp",EDGE,"E11"),sQuery(id+"F0.wireOp",EDGE,"E12"),sQuery(id+"F0.wireOp",EDGE,"E13"),sQuery(id+"F0.wireOp",EDGE,"E14"),sQuery(id+"F0.wireOp",EDGE,"E15"),sQuery(id+"F0.wireOp",EDGE,"E16.bottom"),sQuery(id+"F0.wireOp",EDGE,"E16.top"),sQuery(id+"F0.wireOp",EDGE,"E16.left"),sQuery(id+"F0.wireOp",EDGE,"E16.right"),sQuery(id+"F0.wireOp",EDGE,"E20"),sQuery(id+"F0.wireOp",EDGE,"E21"),sQuery(id+"F0.wireOp",EDGE,"E22"),sQuery(id+"F0.wireOp",EDGE,"E23"),sQuery(id+"F0.wireOp",EDGE,"E40.bottom"),sQuery(id+"F0.wireOp",EDGE,"E40.top"),sQuery(id+"F0.wireOp",EDGE,"E40.left"),sQuery(id+"F0.wireOp",EDGE,"E40.right"),sQuery(id+"F0.wireOp",EDGE,"E42"),sQuery(id+"F0.wireOp",EDGE,"E43"),sQuery(id+"F0.wireOp",EDGE,"E44"),sQuery(id+"F0.wireOp",EDGE,"E45"),sQuery(id+"F0.wireOp",EDGE,"E54"),sQuery(id+"F0.wireOp",EDGE,"E55.MirrorC"),sQuery(id+"F0.wireOp",EDGE,"E56.left"),sQuery(id+"F0.wireOp",EDGE,"E56.right"),sQuery(id+"F0.wireOp",EDGE,"E57.filletArc"),sQuery(id+"F0.wireOp",EDGE,"E58.filletArc"),sQuery(id+"F0.wireOp",EDGE,"E59.filletArc"),sQuery(id+"F0.wireOp",EDGE,"E60.filletArc"),sQuery(id+"F0.wireOp",EDGE,"E61.1.3"),sQuery(id+"F0.wireOp",EDGE,"E61.1.5"),sQuery(id+"F0.wireOp",EDGE,"E61.1.7"),sQuery(id+"F0.wireOp",EDGE,"E61.1.8"),sQuery(id+"F0.wireOp",EDGE,"E61.1.9"),sQuery(id+"F0.wireOp",EDGE,"E61.1.10"),sQuery(id+"F0.wireOp",EDGE,"E61.2.3"),sQuery(id+"F0.wireOp",EDGE,"E61.2.5"),sQuery(id+"F0.wireOp",EDGE,"E61.2.7"),sQuery(id+"F0.wireOp",EDGE,"E61.2.8"),sQuery(id+"F0.wireOp",EDGE,"E61.2.9"),sQuery(id+"F0.wireOp",EDGE,"E61.2.10"),sQuery(id+"F0.wireOp",EDGE,"E61.3.3"),sQuery(id+"F0.wireOp",EDGE,"E61.3.5"),sQuery(id+"F0.wireOp",EDGE,"E61.3.7"),sQuery(id+"F0.wireOp",EDGE,"E61.3.8"),sQuery(id+"F0.wireOp",EDGE,"E61.3.9"),sQuery(id+"F0.wireOp",EDGE,"E61.3.10"),sQuery(id+"F0.wireOp",EDGE,"E61.4.3"),sQuery(id+"F0.wireOp",EDGE,"E61.4.5"),sQuery(id+"F0.wireOp",EDGE,"E61.4.7"),sQuery(id+"F0.wireOp",EDGE,"E61.4.8"),sQuery(id+"F0.wireOp",EDGE,"E61.4.9"),sQuery(id+"F0.wireOp",EDGE,"E61.4.10"),sQuery(id+"F0.wireOp",EDGE,"E61.5.3"),sQuery(id+"F0.wireOp",EDGE,"E61.5.5"),sQuery(id+"F0.wireOp",EDGE,"E61.5.7"),sQuery(id+"F0.wireOp",EDGE,"E61.5.8"),sQuery(id+"F0.wireOp",EDGE,"E61.5.9"),sQuery(id+"F0.wireOp",EDGE,"E61.5.10"),sQuery(id+"F0.wireOp",EDGE,"E61.6.3"),sQuery(id+"F0.wireOp",EDGE,"E61.6.5"),sQuery(id+"F0.wireOp",EDGE,"E61.6.7"),sQuery(id+"F0.wireOp",EDGE,"E61.6.8"),sQuery(id+"F0.wireOp",EDGE,"E61.6.9"),sQuery(id+"F0.wireOp",EDGE,"E61.6.10"),sQuery(id+"F0.wireOp",EDGE,"E61.7.3"),sQuery(id+"F0.wireOp",EDGE,"E61.7.5"),sQuery(id+"F0.wireOp",EDGE,"E61.7.7"),sQuery(id+"F0.wireOp",EDGE,"E61.7.8"),sQuery(id+"F0.wireOp",EDGE,"E61.7.9"),sQuery(id+"F0.wireOp",EDGE,"E61.7.10"),sQuery(id+"F0.wireOp",EDGE,"E61.8.3"),sQuery(id+"F0.wireOp",EDGE,"E61.8.5"),sQuery(id+"F0.wireOp",EDGE,"E61.8.7"),sQuery(id+"F0.wireOp",EDGE,"E61.8.8"),sQuery(id+"F0.wireOp",EDGE,"E61.8.9"),sQuery(id+"F0.wireOp",EDGE,"E61.8.10"),sQuery(id+"F0.wireOp",EDGE,"E61.9.3"),sQuery(id+"F0.wireOp",EDGE,"E61.9.5"),sQuery(id+"F0.wireOp",EDGE,"E61.9.7"),sQuery(id+"F0.wireOp",EDGE,"E61.9.8"),sQuery(id+"F0.wireOp",EDGE,"E61.9.9"),sQuery(id+"F0.wireOp",EDGE,"E61.9.10"),sQuery(id+"F0.wireOp",EDGE,"E61.10.3"),sQuery(id+"F0.wireOp",EDGE,"E61.10.5"),sQuery(id+"F0.wireOp",EDGE,"E61.10.7"),sQuery(id+"F0.wireOp",EDGE,"E61.10.8"),sQuery(id+"F0.wireOp",EDGE,"E61.10.9"),sQuery(id+"F0.wireOp",EDGE,"E61.10.10"),sQuery(id+"F0.wireOp",EDGE,"E61.11.3"),sQuery(id+"F0.wireOp",EDGE,"E61.11.5"),sQuery(id+"F0.wireOp",EDGE,"E61.11.7"),sQuery(id+"F0.wireOp",EDGE,"E61.11.8"),sQuery(id+"F0.wireOp",EDGE,"E61.11.9"),sQuery(id+"F0.wireOp",EDGE,"E61.11.10"),sQuery(id+"F0.wireOp",EDGE,"E61.12.3"),sQuery(id+"F0.wireOp",EDGE,"E61.12.5"),sQuery(id+"F0.wireOp",EDGE,"E61.12.7"),sQuery(id+"F0.wireOp",EDGE,"E61.12.8"),sQuery(id+"F0.wireOp",EDGE,"E61.12.9"),sQuery(id+"F0.wireOp",EDGE,"E61.12.10"),sQuery(id+"F0.wireOp",EDGE,"E61.13.3"),sQuery(id+"F0.wireOp",EDGE,"E61.13.5"),sQuery(id+"F0.wireOp",EDGE,"E61.13.7"),sQuery(id+"F0.wireOp",EDGE,"E61.13.8"),sQuery(id+"F0.wireOp",EDGE,"E61.13.9"),sQuery(id+"F0.wireOp",EDGE,"E61.13.10"),sQuery(id+"F0.wireOp",EDGE,"E61.14.3"),sQuery(id+"F0.wireOp",EDGE,"E61.14.5"),sQuery(id+"F0.wireOp",EDGE,"E61.14.7"),sQuery(id+"F0.wireOp",EDGE,"E61.14.8"),sQuery(id+"F0.wireOp",EDGE,"E61.14.9"),sQuery(id+"F0.wireOp",EDGE,"E61.14.10"),sQuery(id+"F0.wireOp",EDGE,"E61.15.3"),sQuery(id+"F0.wireOp",EDGE,"E61.15.5"),sQuery(id+"F0.wireOp",EDGE,"E61.15.7"),sQuery(id+"F0.wireOp",EDGE,"E61.15.8"),sQuery(id+"F0.wireOp",EDGE,"E61.15.9"),sQuery(id+"F0.wireOp",EDGE,"E61.15.10"),sQuery(id+"F0.wireOp",EDGE,"E61.16.3"),sQuery(id+"F0.wireOp",EDGE,"E61.16.5"),sQuery(id+"F0.wireOp",EDGE,"E61.16.7"),sQuery(id+"F0.wireOp",EDGE,"E61.16.8"),sQuery(id+"F0.wireOp",EDGE,"E61.16.9"),sQuery(id+"F0.wireOp",EDGE,"E61.16.10"),sQuery(id+"F0.wireOp",EDGE,"E61.17.3"),sQuery(id+"F0.wireOp",EDGE,"E61.17.5"),sQuery(id+"F0.wireOp",EDGE,"E61.17.7"),sQuery(id+"F0.wireOp",EDGE,"E61.17.8"),sQuery(id+"F0.wireOp",EDGE,"E61.17.9"),sQuery(id+"F0.wireOp",EDGE,"E61.17.10"),sQuery(id+"F0.wireOp",EDGE,"E61.18.3"),sQuery(id+"F0.wireOp",EDGE,"E61.18.5"),sQuery(id+"F0.wireOp",EDGE,"E61.18.7"),sQuery(id+"F0.wireOp",EDGE,"E61.18.8"),sQuery(id+"F0.wireOp",EDGE,"E61.18.9"),sQuery(id+"F0.wireOp",EDGE,"E61.18.10"),sQuery(id+"F0.wireOp",EDGE,"E61.19.3"),sQuery(id+"F0.wireOp",EDGE,"E61.19.5"),sQuery(id+"F0.wireOp",EDGE,"E61.19.7"),sQuery(id+"F0.wireOp",EDGE,"E61.19.8"),sQuery(id+"F0.wireOp",EDGE,"E61.19.9"),sQuery(id+"F0.wireOp",EDGE,"E61.19.10"),sQuery(id+"F0.wireOp",EDGE,"E62.left"),sQuery(id+"F0.wireOp",EDGE,"E62.right"),sQuery(id+"F0.wireOp",EDGE,"E63.filletArc"),sQuery(id+"F0.wireOp",EDGE,"E64.filletArc"),sQuery(id+"F0.wireOp",EDGE,"E65.filletArc"),sQuery(id+"F0.wireOp",EDGE,"E66.filletArc"),sQuery(id+"F0.wireOp",EDGE,"E67.1.2"),sQuery(id+"F0.wireOp",EDGE,"E67.1.3"),sQuery(id+"F0.wireOp",EDGE,"E67.1.5"),sQuery(id+"F0.wireOp",EDGE,"E67.1.7"),sQuery(id+"F0.wireOp",EDGE,"E67.1.9"),sQuery(id+"F0.wireOp",EDGE,"E67.1.10"),sQuery(id+"F0.wireOp",EDGE,"E67.2.2"),sQuery(id+"F0.wireOp",EDGE,"E67.2.3"),sQuery(id+"F0.wireOp",EDGE,"E67.2.5"),sQuery(id+"F0.wireOp",EDGE,"E67.2.7"),sQuery(id+"F0.wireOp",EDGE,"E67.2.9"),sQuery(id+"F0.wireOp",EDGE,"E67.2.10"),sQuery(id+"F0.wireOp",EDGE,"E67.3.2"),sQuery(id+"F0.wireOp",EDGE,"E67.3.3"),sQuery(id+"F0.wireOp",EDGE,"E67.3.5"),sQuery(id+"F0.wireOp",EDGE,"E67.3.7"),sQuery(id+"F0.wireOp",EDGE,"E67.3.9"),sQuery(id+"F0.wireOp",EDGE,"E67.3.10"),sQuery(id+"F0.wireOp",EDGE,"E67.4.2"),sQuery(id+"F0.wireOp",EDGE,"E67.4.3"),sQuery(id+"F0.wireOp",EDGE,"E67.4.5"),sQuery(id+"F0.wireOp",EDGE,"E67.4.7"),sQuery(id+"F0.wireOp",EDGE,"E67.4.9"),sQuery(id+"F0.wireOp",EDGE,"E67.4.10"),sQuery(id+"F0.wireOp",EDGE,"E67.5.2"),sQuery(id+"F0.wireOp",EDGE,"E67.5.3"),sQuery(id+"F0.wireOp",EDGE,"E67.5.5"),sQuery(id+"F0.wireOp",EDGE,"E67.5.7"),sQuery(id+"F0.wireOp",EDGE,"E67.5.9"),sQuery(id+"F0.wireOp",EDGE,"E67.5.10"),sQuery(id+"F0.wireOp",EDGE,"E67.6.2"),sQuery(id+"F0.wireOp",EDGE,"E67.6.3"),sQuery(id+"F0.wireOp",EDGE,"E67.6.5"),sQuery(id+"F0.wireOp",EDGE,"E67.6.7"),sQuery(id+"F0.wireOp",EDGE,"E67.6.9"),sQuery(id+"F0.wireOp",EDGE,"E67.6.10"),sQuery(id+"F0.wireOp",EDGE,"E67.7.2"),sQuery(id+"F0.wireOp",EDGE,"E67.7.3"),sQuery(id+"F0.wireOp",EDGE,"E67.7.5"),sQuery(id+"F0.wireOp",EDGE,"E67.7.7"),sQuery(id+"F0.wireOp",EDGE,"E67.7.9"),sQuery(id+"F0.wireOp",EDGE,"E67.7.10"),sQuery(id+"F0.wireOp",EDGE,"E67.8.2"),sQuery(id+"F0.wireOp",EDGE,"E67.8.3"),sQuery(id+"F0.wireOp",EDGE,"E67.8.5"),sQuery(id+"F0.wireOp",EDGE,"E67.8.7"),sQuery(id+"F0.wireOp",EDGE,"E67.8.9"),sQuery(id+"F0.wireOp",EDGE,"E67.8.10"),sQuery(id+"F0.wireOp",EDGE,"E67.9.2"),sQuery(id+"F0.wireOp",EDGE,"E67.9.3"),sQuery(id+"F0.wireOp",EDGE,"E67.9.5"),sQuery(id+"F0.wireOp",EDGE,"E67.9.7"),sQuery(id+"F0.wireOp",EDGE,"E67.9.9"),sQuery(id+"F0.wireOp",EDGE,"E67.9.10"),sQuery(id+"F0.wireOp",EDGE,"E67.10.2"),sQuery(id+"F0.wireOp",EDGE,"E67.10.3"),sQuery(id+"F0.wireOp",EDGE,"E67.10.5"),sQuery(id+"F0.wireOp",EDGE,"E67.10.7"),sQuery(id+"F0.wireOp",EDGE,"E67.10.9"),sQuery(id+"F0.wireOp",EDGE,"E67.10.10"),sQuery(id+"F0.wireOp",EDGE,"E67.11.2"),sQuery(id+"F0.wireOp",EDGE,"E67.11.3"),sQuery(id+"F0.wireOp",EDGE,"E67.11.5"),sQuery(id+"F0.wireOp",EDGE,"E67.11.7"),sQuery(id+"F0.wireOp",EDGE,"E67.11.9"),sQuery(id+"F0.wireOp",EDGE,"E67.11.10"),sQuery(id+"F0.wireOp",EDGE,"E67.12.2"),sQuery(id+"F0.wireOp",EDGE,"E67.12.3"),sQuery(id+"F0.wireOp",EDGE,"E67.12.5"),sQuery(id+"F0.wireOp",EDGE,"E67.12.7"),sQuery(id+"F0.wireOp",EDGE,"E67.12.9"),sQuery(id+"F0.wireOp",EDGE,"E67.12.10"),sQuery(id+"F0.wireOp",EDGE,"E67.13.2"),sQuery(id+"F0.wireOp",EDGE,"E67.13.3"),sQuery(id+"F0.wireOp",EDGE,"E67.13.5"),sQuery(id+"F0.wireOp",EDGE,"E67.13.7"),sQuery(id+"F0.wireOp",EDGE,"E67.13.9"),sQuery(id+"F0.wireOp",EDGE,"E67.13.10"),sQuery(id+"F0.wireOp",EDGE,"E67.14.2"),sQuery(id+"F0.wireOp",EDGE,"E67.14.3"),sQuery(id+"F0.wireOp",EDGE,"E67.14.5"),sQuery(id+"F0.wireOp",EDGE,"E67.14.7"),sQuery(id+"F0.wireOp",EDGE,"E67.14.9"),sQuery(id+"F0.wireOp",EDGE,"E67.14.10"),sQuery(id+"F0.wireOp",EDGE,"E67.15.2"),sQuery(id+"F0.wireOp",EDGE,"E67.15.3"),sQuery(id+"F0.wireOp",EDGE,"E67.15.5"),sQuery(id+"F0.wireOp",EDGE,"E67.15.7"),sQuery(id+"F0.wireOp",EDGE,"E67.15.9"),sQuery(id+"F0.wireOp",EDGE,"E67.15.10"),sQuery(id+"F0.wireOp",EDGE,"E67.16.2"),sQuery(id+"F0.wireOp",EDGE,"E67.16.3"),sQuery(id+"F0.wireOp",EDGE,"E67.16.5"),sQuery(id+"F0.wireOp",EDGE,"E67.16.7"),sQuery(id+"F0.wireOp",EDGE,"E67.16.9"),sQuery(id+"F0.wireOp",EDGE,"E67.16.10"),sQuery(id+"F0.wireOp",EDGE,"E67.17.2"),sQuery(id+"F0.wireOp",EDGE,"E67.17.3"),sQuery(id+"F0.wireOp",EDGE,"E67.17.5"),sQuery(id+"F0.wireOp",EDGE,"E67.17.7"),sQuery(id+"F0.wireOp",EDGE,"E67.17.9"),sQuery(id+"F0.wireOp",EDGE,"E67.17.10"),sQuery(id+"F0.wireOp",EDGE,"E67.18.2"),sQuery(id+"F0.wireOp",EDGE,"E67.18.3"),sQuery(id+"F0.wireOp",EDGE,"E67.18.5"),sQuery(id+"F0.wireOp",EDGE,"E67.18.7"),sQuery(id+"F0.wireOp",EDGE,"E67.18.9"),sQuery(id+"F0.wireOp",EDGE,"E67.18.10"),sQuery(id+"F0.wireOp",EDGE,"E67.19.2"),sQuery(id+"F0.wireOp",EDGE,"E67.19.3"),sQuery(id+"F0.wireOp",EDGE,"E67.19.5"),sQuery(id+"F0.wireOp",EDGE,"E67.19.7"),sQuery(id+"F0.wireOp",EDGE,"E67.19.9"),sQuery(id+"F0.wireOp",EDGE,"E67.19.10"),sQuery(id+"F0.wireOp",EDGE,"E68.2.20.0"),sQuery(id+"F0.wireOp",EDGE,"E68.5.20.0"),sQuery(id+"F0.wireOp",EDGE,"E68.9.20.0"),sQuery(id+"F0.wireOp",EDGE,"E68.14.20.0"),sQuery(id+"F0.wireOp",EDGE,"E68.19.20.0"),sQuery(id+"F0.wireOp",EDGE,"E68.23.20.0"),sQuery(id+"F0.wireOp",EDGE,"E68.2.21.0"),sQuery(id+"F0.wireOp",EDGE,"E68.5.21.0"),sQuery(id+"F0.wireOp",EDGE,"E68.9.21.0"),sQuery(id+"F0.wireOp",EDGE,"E68.14.21.0"),sQuery(id+"F0.wireOp",EDGE,"E68.19.21.0"),sQuery(id+"F0.wireOp",EDGE,"E68.23.21.0"),sQuery(id+"F0.wireOp",EDGE,"E68.2.22.0"),sQuery(id+"F0.wireOp",EDGE,"E68.5.22.0"),sQuery(id+"F0.wireOp",EDGE,"E68.9.22.0"),sQuery(id+"F0.wireOp",EDGE,"E68.14.22.0"),sQuery(id+"F0.wireOp",EDGE,"E68.19.22.0"),sQuery(id+"F0.wireOp",EDGE,"E68.23.22.0"),sQuery(id+"F0.wireOp",EDGE,"E68.2.23.0"),sQuery(id+"F0.wireOp",EDGE,"E68.5.23.0"),sQuery(id+"F0.wireOp",EDGE,"E68.9.23.0"),sQuery(id+"F0.wireOp",EDGE,"E68.14.23.0"),sQuery(id+"F0.wireOp",EDGE,"E68.19.23.0"),sQuery(id+"F0.wireOp",EDGE,"E68.23.23.0"),sQuery(id+"F0.wireOp",EDGE,"E74.left"),sQuery(id+"F0.wireOp",EDGE,"E74.right"),sQuery(id+"F0.wireOp",EDGE,"E75.filletArc"),sQuery(id+"F0.wireOp",EDGE,"E76.filletArc"),sQuery(id+"F0.wireOp",EDGE,"E77.filletArc"),sQuery(id+"F0.wireOp",EDGE,"E78.filletArc"),sQuery(id+"F0.wireOp",EDGE,"E79.left"),sQuery(id+"F0.wireOp",EDGE,"E79.right"),sQuery(id+"F0.wireOp",EDGE,"E80.filletArc"),sQuery(id+"F0.wireOp",EDGE,"E81.filletArc"),sQuery(id+"F0.wireOp",EDGE,"E82.filletArc"),sQuery(id+"F0.wireOp",EDGE,"E83.filletArc"),sQuery(id+"F0.wireOp",EDGE,"E69.left"),sQuery(id+"F0.wireOp",EDGE,"E69.right"),sQuery(id+"F0.wireOp",EDGE,"E70.filletArc"),sQuery(id+"F0.wireOp",EDGE,"E71.filletArc"),sQuery(id+"F0.wireOp",EDGE,"E72.filletArc"),sQuery(id+"F0.wireOp",EDGE,"E73.filletArc"),sQuery(id+"F0.wireOp",EDGE,"E84.left"),sQuery(id+"F0.wireOp",EDGE,"E84.right"),sQuery(id+"F0.wireOp",EDGE,"E85.filletArc"),sQuery(id+"F0.wireOp",EDGE,"E86.filletArc"),sQuery(id+"F0.wireOp",EDGE,"E87.filletArc"),sQuery(id+"F0.wireOp",EDGE,"E88.filletArc"),sQuery(id+"F0.wireOp",EDGE,"E89.left"),sQuery(id+"F0.wireOp",EDGE,"E89.right"),sQuery(id+"F0.wireOp",EDGE,"E90.filletArc"),sQuery(id+"F0.wireOp",EDGE,"E91.filletArc"),sQuery(id+"F0.wireOp",EDGE,"E92.filletArc"),sQuery(id+"F0.wireOp",EDGE,"E93.filletArc"),sQuery(id+"F0.wireOp",EDGE,"E94.left"),sQuery(id+"F0.wireOp",EDGE,"E94.right"),sQuery(id+"F0.wireOp",EDGE,"E95.filletArc"),sQuery(id+"F0.wireOp",EDGE,"E96.filletArc"),sQuery(id+"F0.wireOp",EDGE,"E97.filletArc"),sQuery(id+"F0.wireOp",EDGE,"E98.filletArc"),sQuery(id+"F0.wireOp",EDGE,"E101.1.1"),sQuery(id+"F0.wireOp",EDGE,"E101.1.4"),sQuery(id+"F0.wireOp",EDGE,"E101.1.5"),sQuery(id+"F0.wireOp",EDGE,"E101.1.6"),sQuery(id+"F0.wireOp",EDGE,"E101.1.9"),sQuery(id+"F0.wireOp",EDGE,"E101.1.10"),sQuery(id+"F0.wireOp",EDGE,"E101.2.1"),sQuery(id+"F0.wireOp",EDGE,"E101.2.4"),sQuery(id+"F0.wireOp",EDGE,"E101.2.5"),sQuery(id+"F0.wireOp",EDGE,"E101.2.6"),sQuery(id+"F0.wireOp",EDGE,"E101.2.9"),sQuery(id+"F0.wireOp",EDGE,"E101.2.10"),sQuery(id+"F0.wireOp",EDGE,"E101.3.1"),sQuery(id+"F0.wireOp",EDGE,"E101.3.4"),sQuery(id+"F0.wireOp",EDGE,"E101.3.5"),sQuery(id+"F0.wireOp",EDGE,"E101.3.6"),sQuery(id+"F0.wireOp",EDGE,"E101.3.9"),sQuery(id+"F0.wireOp",EDGE,"E101.3.10"),sQuery(id+"F0.wireOp",EDGE,"E101.4.1"),sQuery(id+"F0.wireOp",EDGE,"E101.4.4"),sQuery(id+"F0.wireOp",EDGE,"E101.4.5"),sQuery(id+"F0.wireOp",EDGE,"E101.4.6"),sQuery(id+"F0.wireOp",EDGE,"E101.4.9"),sQuery(id+"F0.wireOp",EDGE,"E101.4.10"),sQuery(id+"F0.wireOp",EDGE,"E101.5.1"),sQuery(id+"F0.wireOp",EDGE,"E101.5.4"),sQuery(id+"F0.wireOp",EDGE,"E101.5.5"),sQuery(id+"F0.wireOp",EDGE,"E101.5.6"),sQuery(id+"F0.wireOp",EDGE,"E101.5.9"),sQuery(id+"F0.wireOp",EDGE,"E101.5.10"),sQuery(id+"F0.wireOp",EDGE,"E101.6.1"),sQuery(id+"F0.wireOp",EDGE,"E101.6.4"),sQuery(id+"F0.wireOp",EDGE,"E101.6.5"),sQuery(id+"F0.wireOp",EDGE,"E101.6.6"),sQuery(id+"F0.wireOp",EDGE,"E101.6.9"),sQuery(id+"F0.wireOp",EDGE,"E101.6.10"),sQuery(id+"F0.wireOp",EDGE,"E101.7.1"),sQuery(id+"F0.wireOp",EDGE,"E101.7.4"),sQuery(id+"F0.wireOp",EDGE,"E101.7.5"),sQuery(id+"F0.wireOp",EDGE,"E101.7.6"),sQuery(id+"F0.wireOp",EDGE,"E101.7.9"),sQuery(id+"F0.wireOp",EDGE,"E101.7.10"),sQuery(id+"F0.wireOp",EDGE,"E101.8.1"),sQuery(id+"F0.wireOp",EDGE,"E101.8.4"),sQuery(id+"F0.wireOp",EDGE,"E101.8.5"),sQuery(id+"F0.wireOp",EDGE,"E101.8.6"),sQuery(id+"F0.wireOp",EDGE,"E101.8.9"),sQuery(id+"F0.wireOp",EDGE,"E101.8.10"),sQuery(id+"F0.wireOp",EDGE,"E101.9.1"),sQuery(id+"F0.wireOp",EDGE,"E101.9.4"),sQuery(id+"F0.wireOp",EDGE,"E101.9.5"),sQuery(id+"F0.wireOp",EDGE,"E101.9.6"),sQuery(id+"F0.wireOp",EDGE,"E101.9.9"),sQuery(id+"F0.wireOp",EDGE,"E101.9.10"),sQuery(id+"F0.wireOp",EDGE,"E101.10.1"),sQuery(id+"F0.wireOp",EDGE,"E101.10.4"),sQuery(id+"F0.wireOp",EDGE,"E101.10.5"),sQuery(id+"F0.wireOp",EDGE,"E101.10.6"),sQuery(id+"F0.wireOp",EDGE,"E101.10.9"),sQuery(id+"F0.wireOp",EDGE,"E101.10.10"),sQuery(id+"F0.wireOp",EDGE,"E101.11.1"),sQuery(id+"F0.wireOp",EDGE,"E101.11.4"),sQuery(id+"F0.wireOp",EDGE,"E101.11.5"),sQuery(id+"F0.wireOp",EDGE,"E101.11.6"),sQuery(id+"F0.wireOp",EDGE,"E101.11.9"),sQuery(id+"F0.wireOp",EDGE,"E101.11.10"),sQuery(id+"F0.wireOp",EDGE,"E101.12.1"),sQuery(id+"F0.wireOp",EDGE,"E101.12.4"),sQuery(id+"F0.wireOp",EDGE,"E101.12.5"),sQuery(id+"F0.wireOp",EDGE,"E101.12.6"),sQuery(id+"F0.wireOp",EDGE,"E101.12.9"),sQuery(id+"F0.wireOp",EDGE,"E101.12.10"),sQuery(id+"F0.wireOp",EDGE,"E101.13.1"),sQuery(id+"F0.wireOp",EDGE,"E101.13.4"),sQuery(id+"F0.wireOp",EDGE,"E101.13.5"),sQuery(id+"F0.wireOp",EDGE,"E101.13.6"),sQuery(id+"F0.wireOp",EDGE,"E101.13.9"),sQuery(id+"F0.wireOp",EDGE,"E101.13.10"),sQuery(id+"F0.wireOp",EDGE,"E101.14.1"),sQuery(id+"F0.wireOp",EDGE,"E101.14.4"),sQuery(id+"F0.wireOp",EDGE,"E101.14.5"),sQuery(id+"F0.wireOp",EDGE,"E101.14.6"),sQuery(id+"F0.wireOp",EDGE,"E101.14.9"),sQuery(id+"F0.wireOp",EDGE,"E101.14.10"),sQuery(id+"F0.wireOp",EDGE,"E101.15.1"),sQuery(id+"F0.wireOp",EDGE,"E101.15.4"),sQuery(id+"F0.wireOp",EDGE,"E101.15.5"),sQuery(id+"F0.wireOp",EDGE,"E101.15.6"),sQuery(id+"F0.wireOp",EDGE,"E101.15.9"),sQuery(id+"F0.wireOp",EDGE,"E101.15.10"),sQuery(id+"F0.wireOp",EDGE,"E101.16.1"),sQuery(id+"F0.wireOp",EDGE,"E101.16.4"),sQuery(id+"F0.wireOp",EDGE,"E101.16.5"),sQuery(id+"F0.wireOp",EDGE,"E101.16.6"),sQuery(id+"F0.wireOp",EDGE,"E101.16.9"),sQuery(id+"F0.wireOp",EDGE,"E101.16.10"),sQuery(id+"F0.wireOp",EDGE,"E101.17.1"),sQuery(id+"F0.wireOp",EDGE,"E101.17.4"),sQuery(id+"F0.wireOp",EDGE,"E101.17.5"),sQuery(id+"F0.wireOp",EDGE,"E101.17.6"),sQuery(id+"F0.wireOp",EDGE,"E101.17.9"),sQuery(id+"F0.wireOp",EDGE,"E101.17.10"),sQuery(id+"F0.wireOp",EDGE,"E101.18.1"),sQuery(id+"F0.wireOp",EDGE,"E101.18.4"),sQuery(id+"F0.wireOp",EDGE,"E101.18.5"),sQuery(id+"F0.wireOp",EDGE,"E101.18.6"),sQuery(id+"F0.wireOp",EDGE,"E101.18.9"),sQuery(id+"F0.wireOp",EDGE,"E101.18.10"),sQuery(id+"F0.wireOp",EDGE,"E101.19.1"),sQuery(id+"F0.wireOp",EDGE,"E101.19.4"),sQuery(id+"F0.wireOp",EDGE,"E101.19.5"),sQuery(id+"F0.wireOp",EDGE,"E101.19.6"),sQuery(id+"F0.wireOp",EDGE,"E101.19.9"),sQuery(id+"F0.wireOp",EDGE,"E101.19.10"),sQuery(id+"F0.wireOp",EDGE,"E101.20.1"),sQuery(id+"F0.wireOp",EDGE,"E101.20.4"),sQuery(id+"F0.wireOp",EDGE,"E101.20.5"),sQuery(id+"F0.wireOp",EDGE,"E101.20.6"),sQuery(id+"F0.wireOp",EDGE,"E101.20.9"),sQuery(id+"F0.wireOp",EDGE,"E101.20.10"),sQuery(id+"F0.wireOp",EDGE,"E101.21.1"),sQuery(id+"F0.wireOp",EDGE,"E101.21.4"),sQuery(id+"F0.wireOp",EDGE,"E101.21.5"),sQuery(id+"F0.wireOp",EDGE,"E101.21.6"),sQuery(id+"F0.wireOp",EDGE,"E101.21.9"),sQuery(id+"F0.wireOp",EDGE,"E101.21.10"),sQuery(id+"F0.wireOp",EDGE,"E101.22.1"),sQuery(id+"F0.wireOp",EDGE,"E101.22.4"),sQuery(id+"F0.wireOp",EDGE,"E101.22.5"),sQuery(id+"F0.wireOp",EDGE,"E101.22.6"),sQuery(id+"F0.wireOp",EDGE,"E101.22.9"),sQuery(id+"F0.wireOp",EDGE,"E101.22.10"),sQuery(id+"F0.wireOp",EDGE,"E101.23.1"),sQuery(id+"F0.wireOp",EDGE,"E101.23.4"),sQuery(id+"F0.wireOp",EDGE,"E101.23.5"),sQuery(id+"F0.wireOp",EDGE,"E101.23.6"),sQuery(id+"F0.wireOp",EDGE,"E101.23.9"),sQuery(id+"F0.wireOp",EDGE,"E101.23.10"),sQuery(id+"F0.wireOp",EDGE,"E102.1.0"),sQuery(id+"F0.wireOp",EDGE,"E102.1.2"),sQuery(id+"F0.wireOp",EDGE,"E102.1.5"),sQuery(id+"F0.wireOp",EDGE,"E102.1.6"),sQuery(id+"F0.wireOp",EDGE,"E102.1.7"),sQuery(id+"F0.wireOp",EDGE,"E102.1.8"),sQuery(id+"F0.wireOp",EDGE,"E102.2.0"),sQuery(id+"F0.wireOp",EDGE,"E102.2.2"),sQuery(id+"F0.wireOp",EDGE,"E102.2.5"),sQuery(id+"F0.wireOp",EDGE,"E102.2.6"),sQuery(id+"F0.wireOp",EDGE,"E102.2.7"),sQuery(id+"F0.wireOp",EDGE,"E102.2.8"),sQuery(id+"F0.wireOp",EDGE,"E102.3.0"),sQuery(id+"F0.wireOp",EDGE,"E102.3.2"),sQuery(id+"F0.wireOp",EDGE,"E102.3.5"),sQuery(id+"F0.wireOp",EDGE,"E102.3.6"),sQuery(id+"F0.wireOp",EDGE,"E102.3.7"),sQuery(id+"F0.wireOp",EDGE,"E102.3.8"),sQuery(id+"F0.wireOp",EDGE,"E102.4.0"),sQuery(id+"F0.wireOp",EDGE,"E102.4.2"),sQuery(id+"F0.wireOp",EDGE,"E102.4.5"),sQuery(id+"F0.wireOp",EDGE,"E102.4.6"),sQuery(id+"F0.wireOp",EDGE,"E102.4.7"),sQuery(id+"F0.wireOp",EDGE,"E102.4.8"),sQuery(id+"F0.wireOp",EDGE,"E102.5.0"),sQuery(id+"F0.wireOp",EDGE,"E102.5.2"),sQuery(id+"F0.wireOp",EDGE,"E102.5.5"),sQuery(id+"F0.wireOp",EDGE,"E102.5.6"),sQuery(id+"F0.wireOp",EDGE,"E102.5.7"),sQuery(id+"F0.wireOp",EDGE,"E102.5.8"),sQuery(id+"F0.wireOp",EDGE,"E102.6.0"),sQuery(id+"F0.wireOp",EDGE,"E102.6.2"),sQuery(id+"F0.wireOp",EDGE,"E102.6.5"),sQuery(id+"F0.wireOp",EDGE,"E102.6.6"),sQuery(id+"F0.wireOp",EDGE,"E102.6.7"),sQuery(id+"F0.wireOp",EDGE,"E102.6.8"),sQuery(id+"F0.wireOp",EDGE,"E102.7.0"),sQuery(id+"F0.wireOp",EDGE,"E102.7.2"),sQuery(id+"F0.wireOp",EDGE,"E102.7.5"),sQuery(id+"F0.wireOp",EDGE,"E102.7.6"),sQuery(id+"F0.wireOp",EDGE,"E102.7.7"),sQuery(id+"F0.wireOp",EDGE,"E102.7.8"),sQuery(id+"F0.wireOp",EDGE,"E102.8.0"),sQuery(id+"F0.wireOp",EDGE,"E102.8.2"),sQuery(id+"F0.wireOp",EDGE,"E102.8.5"),sQuery(id+"F0.wireOp",EDGE,"E102.8.6"),sQuery(id+"F0.wireOp",EDGE,"E102.8.7"),sQuery(id+"F0.wireOp",EDGE,"E102.8.8"),sQuery(id+"F0.wireOp",EDGE,"E102.9.0"),sQuery(id+"F0.wireOp",EDGE,"E102.9.2"),sQuery(id+"F0.wireOp",EDGE,"E102.9.5"),sQuery(id+"F0.wireOp",EDGE,"E102.9.6"),sQuery(id+"F0.wireOp",EDGE,"E102.9.7"),sQuery(id+"F0.wireOp",EDGE,"E102.9.8"),sQuery(id+"F0.wireOp",EDGE,"E102.10.0"),sQuery(id+"F0.wireOp",EDGE,"E102.10.2"),sQuery(id+"F0.wireOp",EDGE,"E102.10.5"),sQuery(id+"F0.wireOp",EDGE,"E102.10.6"),sQuery(id+"F0.wireOp",EDGE,"E102.10.7"),sQuery(id+"F0.wireOp",EDGE,"E102.10.8"),sQuery(id+"F0.wireOp",EDGE,"E102.11.0"),sQuery(id+"F0.wireOp",EDGE,"E102.11.2"),sQuery(id+"F0.wireOp",EDGE,"E102.11.5"),sQuery(id+"F0.wireOp",EDGE,"E102.11.6"),sQuery(id+"F0.wireOp",EDGE,"E102.11.7"),sQuery(id+"F0.wireOp",EDGE,"E102.11.8"),sQuery(id+"F0.wireOp",EDGE,"E102.12.0"),sQuery(id+"F0.wireOp",EDGE,"E102.12.2"),sQuery(id+"F0.wireOp",EDGE,"E102.12.5"),sQuery(id+"F0.wireOp",EDGE,"E102.12.6"),sQuery(id+"F0.wireOp",EDGE,"E102.12.7"),sQuery(id+"F0.wireOp",EDGE,"E102.12.8"),sQuery(id+"F0.wireOp",EDGE,"E102.13.0"),sQuery(id+"F0.wireOp",EDGE,"E102.13.2"),sQuery(id+"F0.wireOp",EDGE,"E102.13.5"),sQuery(id+"F0.wireOp",EDGE,"E102.13.6"),sQuery(id+"F0.wireOp",EDGE,"E102.13.7"),sQuery(id+"F0.wireOp",EDGE,"E102.13.8"),sQuery(id+"F0.wireOp",EDGE,"E102.14.0"),sQuery(id+"F0.wireOp",EDGE,"E102.14.2"),sQuery(id+"F0.wireOp",EDGE,"E102.14.5"),sQuery(id+"F0.wireOp",EDGE,"E102.14.6"),sQuery(id+"F0.wireOp",EDGE,"E102.14.7"),sQuery(id+"F0.wireOp",EDGE,"E102.14.8"),sQuery(id+"F0.wireOp",EDGE,"E102.15.0"),sQuery(id+"F0.wireOp",EDGE,"E102.15.2"),sQuery(id+"F0.wireOp",EDGE,"E102.15.5"),sQuery(id+"F0.wireOp",EDGE,"E102.15.6"),sQuery(id+"F0.wireOp",EDGE,"E102.15.7"),sQuery(id+"F0.wireOp",EDGE,"E102.15.8"),sQuery(id+"F0.wireOp",EDGE,"E102.16.0"),sQuery(id+"F0.wireOp",EDGE,"E102.16.2"),sQuery(id+"F0.wireOp",EDGE,"E102.16.5"),sQuery(id+"F0.wireOp",EDGE,"E102.16.6"),sQuery(id+"F0.wireOp",EDGE,"E102.16.7"),sQuery(id+"F0.wireOp",EDGE,"E102.16.8"),sQuery(id+"F0.wireOp",EDGE,"E102.17.0"),sQuery(id+"F0.wireOp",EDGE,"E102.17.2"),sQuery(id+"F0.wireOp",EDGE,"E102.17.5"),sQuery(id+"F0.wireOp",EDGE,"E102.17.6"),sQuery(id+"F0.wireOp",EDGE,"E102.17.7"),sQuery(id+"F0.wireOp",EDGE,"E102.17.8"),sQuery(id+"F0.wireOp",EDGE,"E102.18.0"),sQuery(id+"F0.wireOp",EDGE,"E102.18.2"),sQuery(id+"F0.wireOp",EDGE,"E102.18.5"),sQuery(id+"F0.wireOp",EDGE,"E102.18.6"),sQuery(id+"F0.wireOp",EDGE,"E102.18.7"),sQuery(id+"F0.wireOp",EDGE,"E102.18.8"),sQuery(id+"F0.wireOp",EDGE,"E102.19.0"),sQuery(id+"F0.wireOp",EDGE,"E102.19.2"),sQuery(id+"F0.wireOp",EDGE,"E102.19.5"),sQuery(id+"F0.wireOp",EDGE,"E102.19.6"),sQuery(id+"F0.wireOp",EDGE,"E102.19.7"),sQuery(id+"F0.wireOp",EDGE,"E102.19.8"),sQuery(id+"F0.wireOp",EDGE,"E102.20.0"),sQuery(id+"F0.wireOp",EDGE,"E102.20.2"),sQuery(id+"F0.wireOp",EDGE,"E102.20.5"),sQuery(id+"F0.wireOp",EDGE,"E102.20.6"),sQuery(id+"F0.wireOp",EDGE,"E102.20.7"),sQuery(id+"F0.wireOp",EDGE,"E102.20.8"),sQuery(id+"F0.wireOp",EDGE,"E102.21.0"),sQuery(id+"F0.wireOp",EDGE,"E102.21.2"),sQuery(id+"F0.wireOp",EDGE,"E102.21.5"),sQuery(id+"F0.wireOp",EDGE,"E102.21.6"),sQuery(id+"F0.wireOp",EDGE,"E102.21.7"),sQuery(id+"F0.wireOp",EDGE,"E102.21.8"),sQuery(id+"F0.wireOp",EDGE,"E102.22.0"),sQuery(id+"F0.wireOp",EDGE,"E102.22.2"),sQuery(id+"F0.wireOp",EDGE,"E102.22.5"),sQuery(id+"F0.wireOp",EDGE,"E102.22.6"),sQuery(id+"F0.wireOp",EDGE,"E102.22.7"),sQuery(id+"F0.wireOp",EDGE,"E102.22.8"),sQuery(id+"F0.wireOp",EDGE,"E102.23.0"),sQuery(id+"F0.wireOp",EDGE,"E102.23.2"),sQuery(id+"F0.wireOp",EDGE,"E102.23.5"),sQuery(id+"F0.wireOp",EDGE,"E102.23.6"),sQuery(id+"F0.wireOp",EDGE,"E102.23.7"),sQuery(id+"F0.wireOp",EDGE,"E102.23.8"),sQuery(id+"F0.wireOp",EDGE,"E103.1.8"),sQuery(id+"F0.wireOp",EDGE,"E103.1.9"),sQuery(id+"F0.wireOp",EDGE,"E103.1.14"),sQuery(id+"F0.wireOp",EDGE,"E103.1.15"),sQuery(id+"F0.wireOp",EDGE,"E103.1.20"),sQuery(id+"F0.wireOp",EDGE,"E103.1.21"),sQuery(id+"F0.wireOp",EDGE,"E103.2.8"),sQuery(id+"F0.wireOp",EDGE,"E103.2.9"),sQuery(id+"F0.wireOp",EDGE,"E103.2.14"),sQuery(id+"F0.wireOp",EDGE,"E103.2.15"),sQuery(id+"F0.wireOp",EDGE,"E103.2.20"),sQuery(id+"F0.wireOp",EDGE,"E103.2.21"),sQuery(id+"F0.wireOp",EDGE,"E103.3.8"),sQuery(id+"F0.wireOp",EDGE,"E103.3.9"),sQuery(id+"F0.wireOp",EDGE,"E103.3.14"),sQuery(id+"F0.wireOp",EDGE,"E103.3.15"),sQuery(id+"F0.wireOp",EDGE,"E103.3.20"),sQuery(id+"F0.wireOp",EDGE,"E103.3.21"),sQuery(id+"F0.wireOp",EDGE,"E103.4.8"),sQuery(id+"F0.wireOp",EDGE,"E103.4.9"),sQuery(id+"F0.wireOp",EDGE,"E103.4.14"),sQuery(id+"F0.wireOp",EDGE,"E103.4.15"),sQuery(id+"F0.wireOp",EDGE,"E103.4.20"),sQuery(id+"F0.wireOp",EDGE,"E103.4.21"),sQuery(id+"F0.wireOp",EDGE,"E103.5.8"),sQuery(id+"F0.wireOp",EDGE,"E103.5.9"),sQuery(id+"F0.wireOp",EDGE,"E103.5.14"),sQuery(id+"F0.wireOp",EDGE,"E103.5.15"),sQuery(id+"F0.wireOp",EDGE,"E103.5.20"),sQuery(id+"F0.wireOp",EDGE,"E103.5.21"),sQuery(id+"F0.wireOp",EDGE,"E103.6.8"),sQuery(id+"F0.wireOp",EDGE,"E103.6.9"),sQuery(id+"F0.wireOp",EDGE,"E103.6.14"),sQuery(id+"F0.wireOp",EDGE,"E103.6.15"),sQuery(id+"F0.wireOp",EDGE,"E103.6.20"),sQuery(id+"F0.wireOp",EDGE,"E103.6.21"),sQuery(id+"F0.wireOp",EDGE,"E103.7.8"),sQuery(id+"F0.wireOp",EDGE,"E103.7.9"),sQuery(id+"F0.wireOp",EDGE,"E103.7.14"),sQuery(id+"F0.wireOp",EDGE,"E103.7.15"),sQuery(id+"F0.wireOp",EDGE,"E103.7.20"),sQuery(id+"F0.wireOp",EDGE,"E103.7.21"),sQuery(id+"F0.wireOp",EDGE,"E103.8.8"),sQuery(id+"F0.wireOp",EDGE,"E103.8.9"),sQuery(id+"F0.wireOp",EDGE,"E103.8.14"),sQuery(id+"F0.wireOp",EDGE,"E103.8.15"),sQuery(id+"F0.wireOp",EDGE,"E103.8.20"),sQuery(id+"F0.wireOp",EDGE,"E103.8.21"),sQuery(id+"F0.wireOp",EDGE,"E103.9.8"),sQuery(id+"F0.wireOp",EDGE,"E103.9.9"),sQuery(id+"F0.wireOp",EDGE,"E103.9.14"),sQuery(id+"F0.wireOp",EDGE,"E103.9.15"),sQuery(id+"F0.wireOp",EDGE,"E103.9.20"),sQuery(id+"F0.wireOp",EDGE,"E103.9.21"),sQuery(id+"F0.wireOp",EDGE,"E103.10.8"),sQuery(id+"F0.wireOp",EDGE,"E103.10.9"),sQuery(id+"F0.wireOp",EDGE,"E103.10.14"),sQuery(id+"F0.wireOp",EDGE,"E103.10.15"),sQuery(id+"F0.wireOp",EDGE,"E103.10.20"),sQuery(id+"F0.wireOp",EDGE,"E103.10.21"),sQuery(id+"F0.wireOp",EDGE,"E103.11.8"),sQuery(id+"F0.wireOp",EDGE,"E103.11.9"),sQuery(id+"F0.wireOp",EDGE,"E103.11.14"),sQuery(id+"F0.wireOp",EDGE,"E103.11.15"),sQuery(id+"F0.wireOp",EDGE,"E103.11.20"),sQuery(id+"F0.wireOp",EDGE,"E103.11.21"),sQuery(id+"F0.wireOp",EDGE,"E103.12.8"),sQuery(id+"F0.wireOp",EDGE,"E103.12.9"),sQuery(id+"F0.wireOp",EDGE,"E103.12.14"),sQuery(id+"F0.wireOp",EDGE,"E103.12.15"),sQuery(id+"F0.wireOp",EDGE,"E103.12.20"),sQuery(id+"F0.wireOp",EDGE,"E103.12.21"),sQuery(id+"F0.wireOp",EDGE,"E103.13.8"),sQuery(id+"F0.wireOp",EDGE,"E103.13.9"),sQuery(id+"F0.wireOp",EDGE,"E103.13.14"),sQuery(id+"F0.wireOp",EDGE,"E103.13.15"),sQuery(id+"F0.wireOp",EDGE,"E103.13.20"),sQuery(id+"F0.wireOp",EDGE,"E103.13.21"),sQuery(id+"F0.wireOp",EDGE,"E103.14.8"),sQuery(id+"F0.wireOp",EDGE,"E103.14.9"),sQuery(id+"F0.wireOp",EDGE,"E103.14.14"),sQuery(id+"F0.wireOp",EDGE,"E103.14.15"),sQuery(id+"F0.wireOp",EDGE,"E103.14.20"),sQuery(id+"F0.wireOp",EDGE,"E103.14.21"),sQuery(id+"F0.wireOp",EDGE,"E103.15.8"),sQuery(id+"F0.wireOp",EDGE,"E103.15.9"),sQuery(id+"F0.wireOp",EDGE,"E103.15.14"),sQuery(id+"F0.wireOp",EDGE,"E103.15.15"),sQuery(id+"F0.wireOp",EDGE,"E103.15.20"),sQuery(id+"F0.wireOp",EDGE,"E103.15.21"),sQuery(id+"F0.wireOp",EDGE,"E103.16.8"),sQuery(id+"F0.wireOp",EDGE,"E103.16.9"),sQuery(id+"F0.wireOp",EDGE,"E103.16.14"),sQuery(id+"F0.wireOp",EDGE,"E103.16.15"),sQuery(id+"F0.wireOp",EDGE,"E103.16.20"),sQuery(id+"F0.wireOp",EDGE,"E103.16.21"),sQuery(id+"F0.wireOp",EDGE,"E103.17.8"),sQuery(id+"F0.wireOp",EDGE,"E103.17.9"),sQuery(id+"F0.wireOp",EDGE,"E103.17.14"),sQuery(id+"F0.wireOp",EDGE,"E103.17.15"),sQuery(id+"F0.wireOp",EDGE,"E103.17.20"),sQuery(id+"F0.wireOp",EDGE,"E103.17.21"),sQuery(id+"F0.wireOp",EDGE,"E103.18.8"),sQuery(id+"F0.wireOp",EDGE,"E103.18.9"),sQuery(id+"F0.wireOp",EDGE,"E103.18.14"),sQuery(id+"F0.wireOp",EDGE,"E103.18.15"),sQuery(id+"F0.wireOp",EDGE,"E103.18.20"),sQuery(id+"F0.wireOp",EDGE,"E103.18.21"),sQuery(id+"F0.wireOp",EDGE,"E103.19.8"),sQuery(id+"F0.wireOp",EDGE,"E103.19.9"),sQuery(id+"F0.wireOp",EDGE,"E103.19.14"),sQuery(id+"F0.wireOp",EDGE,"E103.19.15"),sQuery(id+"F0.wireOp",EDGE,"E103.19.20"),sQuery(id+"F0.wireOp",EDGE,"E103.19.21"),sQuery(id+"F0.wireOp",EDGE,"E103.20.8"),sQuery(id+"F0.wireOp",EDGE,"E103.20.9"),sQuery(id+"F0.wireOp",EDGE,"E103.20.14"),sQuery(id+"F0.wireOp",EDGE,"E103.20.15"),sQuery(id+"F0.wireOp",EDGE,"E103.20.20"),sQuery(id+"F0.wireOp",EDGE,"E103.20.21"),sQuery(id+"F0.wireOp",EDGE,"E103.21.8"),sQuery(id+"F0.wireOp",EDGE,"E103.21.9"),sQuery(id+"F0.wireOp",EDGE,"E103.21.14"),sQuery(id+"F0.wireOp",EDGE,"E103.21.15"),sQuery(id+"F0.wireOp",EDGE,"E103.21.20"),sQuery(id+"F0.wireOp",EDGE,"E103.21.21"),sQuery(id+"F0.wireOp",EDGE,"E103.22.8"),sQuery(id+"F0.wireOp",EDGE,"E103.22.9"),sQuery(id+"F0.wireOp",EDGE,"E103.22.14"),sQuery(id+"F0.wireOp",EDGE,"E103.22.15"),sQuery(id+"F0.wireOp",EDGE,"E103.22.20"),sQuery(id+"F0.wireOp",EDGE,"E103.22.21"),sQuery(id+"F0.wireOp",EDGE,"E103.23.8"),sQuery(id+"F0.wireOp",EDGE,"E103.23.9"),sQuery(id+"F0.wireOp",EDGE,"E103.23.14"),sQuery(id+"F0.wireOp",EDGE,"E103.23.15"),sQuery(id+"F0.wireOp",EDGE,"E103.23.20"),sQuery(id+"F0.wireOp",EDGE,"E103.23.21"),sQuery(id+"F0.wireOp",EDGE,"E104.1.0"),sQuery(id+"F0.wireOp",EDGE,"E104.1.1"),sQuery(id+"F0.wireOp",EDGE,"E104.1.5"),sQuery(id+"F0.wireOp",EDGE,"E104.1.6"),sQuery(id+"F0.wireOp",EDGE,"E104.1.9"),sQuery(id+"F0.wireOp",EDGE,"E104.1.10"),sQuery(id+"F0.wireOp",EDGE,"E104.2.0"),sQuery(id+"F0.wireOp",EDGE,"E104.2.1"),sQuery(id+"F0.wireOp",EDGE,"E104.2.5"),sQuery(id+"F0.wireOp",EDGE,"E104.2.6"),sQuery(id+"F0.wireOp",EDGE,"E104.2.9"),sQuery(id+"F0.wireOp",EDGE,"E104.2.10"),sQuery(id+"F0.wireOp",EDGE,"E104.3.0"),sQuery(id+"F0.wireOp",EDGE,"E104.3.1"),sQuery(id+"F0.wireOp",EDGE,"E104.3.5"),sQuery(id+"F0.wireOp",EDGE,"E104.3.6"),sQuery(id+"F0.wireOp",EDGE,"E104.3.9"),sQuery(id+"F0.wireOp",EDGE,"E104.3.10"),sQuery(id+"F0.wireOp",EDGE,"E104.4.0"),sQuery(id+"F0.wireOp",EDGE,"E104.4.1"),sQuery(id+"F0.wireOp",EDGE,"E104.4.5"),sQuery(id+"F0.wireOp",EDGE,"E104.4.6"),sQuery(id+"F0.wireOp",EDGE,"E104.4.9"),sQuery(id+"F0.wireOp",EDGE,"E104.4.10"),sQuery(id+"F0.wireOp",EDGE,"E104.5.0"),sQuery(id+"F0.wireOp",EDGE,"E104.5.1"),sQuery(id+"F0.wireOp",EDGE,"E104.5.5"),sQuery(id+"F0.wireOp",EDGE,"E104.5.6"),sQuery(id+"F0.wireOp",EDGE,"E104.5.9"),sQuery(id+"F0.wireOp",EDGE,"E104.5.10"),sQuery(id+"F0.wireOp",EDGE,"E104.6.0"),sQuery(id+"F0.wireOp",EDGE,"E104.6.1"),sQuery(id+"F0.wireOp",EDGE,"E104.6.5"),sQuery(id+"F0.wireOp",EDGE,"E104.6.6"),sQuery(id+"F0.wireOp",EDGE,"E104.6.9"),sQuery(id+"F0.wireOp",EDGE,"E104.6.10"),sQuery(id+"F0.wireOp",EDGE,"E104.7.0"),sQuery(id+"F0.wireOp",EDGE,"E104.7.1"),sQuery(id+"F0.wireOp",EDGE,"E104.7.5"),sQuery(id+"F0.wireOp",EDGE,"E104.7.6"),sQuery(id+"F0.wireOp",EDGE,"E104.7.9"),sQuery(id+"F0.wireOp",EDGE,"E104.7.10"),sQuery(id+"F0.wireOp",EDGE,"E104.8.0"),sQuery(id+"F0.wireOp",EDGE,"E104.8.1"),sQuery(id+"F0.wireOp",EDGE,"E104.8.5"),sQuery(id+"F0.wireOp",EDGE,"E104.8.6"),sQuery(id+"F0.wireOp",EDGE,"E104.8.9"),sQuery(id+"F0.wireOp",EDGE,"E104.8.10"),sQuery(id+"F0.wireOp",EDGE,"E104.9.0"),sQuery(id+"F0.wireOp",EDGE,"E104.9.1"),sQuery(id+"F0.wireOp",EDGE,"E104.9.5"),sQuery(id+"F0.wireOp",EDGE,"E104.9.6"),sQuery(id+"F0.wireOp",EDGE,"E104.9.9"),sQuery(id+"F0.wireOp",EDGE,"E104.9.10"),sQuery(id+"F0.wireOp",EDGE,"E104.10.0"),sQuery(id+"F0.wireOp",EDGE,"E104.10.1"),sQuery(id+"F0.wireOp",EDGE,"E104.10.5"),sQuery(id+"F0.wireOp",EDGE,"E104.10.6"),sQuery(id+"F0.wireOp",EDGE,"E104.10.9"),sQuery(id+"F0.wireOp",EDGE,"E104.10.10"),sQuery(id+"F0.wireOp",EDGE,"E104.11.0"),sQuery(id+"F0.wireOp",EDGE,"E104.11.1"),sQuery(id+"F0.wireOp",EDGE,"E104.11.5"),sQuery(id+"F0.wireOp",EDGE,"E104.11.6"),sQuery(id+"F0.wireOp",EDGE,"E104.11.9"),sQuery(id+"F0.wireOp",EDGE,"E104.11.10"),sQuery(id+"F0.wireOp",EDGE,"E104.12.0"),sQuery(id+"F0.wireOp",EDGE,"E104.12.1"),sQuery(id+"F0.wireOp",EDGE,"E104.12.5"),sQuery(id+"F0.wireOp",EDGE,"E104.12.6"),sQuery(id+"F0.wireOp",EDGE,"E104.12.9"),sQuery(id+"F0.wireOp",EDGE,"E104.12.10"),sQuery(id+"F0.wireOp",EDGE,"E104.13.0"),sQuery(id+"F0.wireOp",EDGE,"E104.13.1"),sQuery(id+"F0.wireOp",EDGE,"E104.13.5"),sQuery(id+"F0.wireOp",EDGE,"E104.13.6"),sQuery(id+"F0.wireOp",EDGE,"E104.13.9"),sQuery(id+"F0.wireOp",EDGE,"E104.13.10"),sQuery(id+"F0.wireOp",EDGE,"E104.14.0"),sQuery(id+"F0.wireOp",EDGE,"E104.14.1"),sQuery(id+"F0.wireOp",EDGE,"E104.14.5"),sQuery(id+"F0.wireOp",EDGE,"E104.14.6"),sQuery(id+"F0.wireOp",EDGE,"E104.14.9"),sQuery(id+"F0.wireOp",EDGE,"E104.14.10"),sQuery(id+"F0.wireOp",EDGE,"E104.15.0"),sQuery(id+"F0.wireOp",EDGE,"E104.15.1"),sQuery(id+"F0.wireOp",EDGE,"E104.15.5"),sQuery(id+"F0.wireOp",EDGE,"E104.15.6"),sQuery(id+"F0.wireOp",EDGE,"E104.15.9"),sQuery(id+"F0.wireOp",EDGE,"E104.15.10"),sQuery(id+"F0.wireOp",EDGE,"E104.16.0"),sQuery(id+"F0.wireOp",EDGE,"E104.16.1"),sQuery(id+"F0.wireOp",EDGE,"E104.16.5"),sQuery(id+"F0.wireOp",EDGE,"E104.16.6"),sQuery(id+"F0.wireOp",EDGE,"E104.16.9"),sQuery(id+"F0.wireOp",EDGE,"E104.16.10"),sQuery(id+"F0.wireOp",EDGE,"E104.17.0"),sQuery(id+"F0.wireOp",EDGE,"E104.17.1"),sQuery(id+"F0.wireOp",EDGE,"E104.17.5"),sQuery(id+"F0.wireOp",EDGE,"E104.17.6"),sQuery(id+"F0.wireOp",EDGE,"E104.17.9"),sQuery(id+"F0.wireOp",EDGE,"E104.17.10"),sQuery(id+"F0.wireOp",EDGE,"E104.18.0"),sQuery(id+"F0.wireOp",EDGE,"E104.18.1"),sQuery(id+"F0.wireOp",EDGE,"E104.18.5"),sQuery(id+"F0.wireOp",EDGE,"E104.18.6"),sQuery(id+"F0.wireOp",EDGE,"E104.18.9"),sQuery(id+"F0.wireOp",EDGE,"E104.18.10"),sQuery(id+"F0.wireOp",EDGE,"E104.19.0"),sQuery(id+"F0.wireOp",EDGE,"E104.19.1"),sQuery(id+"F0.wireOp",EDGE,"E104.19.5"),sQuery(id+"F0.wireOp",EDGE,"E104.19.6"),sQuery(id+"F0.wireOp",EDGE,"E104.19.9"),sQuery(id+"F0.wireOp",EDGE,"E104.19.10"),sQuery(id+"F0.wireOp",EDGE,"E104.20.0"),sQuery(id+"F0.wireOp",EDGE,"E104.20.1"),sQuery(id+"F0.wireOp",EDGE,"E104.20.5"),sQuery(id+"F0.wireOp",EDGE,"E104.20.6"),sQuery(id+"F0.wireOp",EDGE,"E104.20.9"),sQuery(id+"F0.wireOp",EDGE,"E104.20.10"),sQuery(id+"F0.wireOp",EDGE,"E104.21.0"),sQuery(id+"F0.wireOp",EDGE,"E104.21.1"),sQuery(id+"F0.wireOp",EDGE,"E104.21.5"),sQuery(id+"F0.wireOp",EDGE,"E104.21.6"),sQuery(id+"F0.wireOp",EDGE,"E104.21.9"),sQuery(id+"F0.wireOp",EDGE,"E104.21.10"),sQuery(id+"F0.wireOp",EDGE,"E104.22.0"),sQuery(id+"F0.wireOp",EDGE,"E104.22.1"),sQuery(id+"F0.wireOp",EDGE,"E104.22.5"),sQuery(id+"F0.wireOp",EDGE,"E104.22.6"),sQuery(id+"F0.wireOp",EDGE,"E104.22.9"),sQuery(id+"F0.wireOp",EDGE,"E104.22.10"),sQuery(id+"F0.wireOp",EDGE,"E104.23.0"),sQuery(id+"F0.wireOp",EDGE,"E104.23.1"),sQuery(id+"F0.wireOp",EDGE,"E104.23.5"),sQuery(id+"F0.wireOp",EDGE,"E104.23.6"),sQuery(id+"F0.wireOp",EDGE,"E104.23.9"),sQuery(id+"F0.wireOp",EDGE,"E104.23.10"),sQuery(id+"F0.wireOp",EDGE,"E105.1.1"),sQuery(id+"F0.wireOp",EDGE,"E105.1.2"),sQuery(id+"F0.wireOp",EDGE,"E105.1.5"),sQuery(id+"F0.wireOp",EDGE,"E105.1.6"),sQuery(id+"F0.wireOp",EDGE,"E105.1.9"),sQuery(id+"F0.wireOp",EDGE,"E105.1.10"),sQuery(id+"F0.wireOp",EDGE,"E105.2.1"),sQuery(id+"F0.wireOp",EDGE,"E105.2.2"),sQuery(id+"F0.wireOp",EDGE,"E105.2.5"),sQuery(id+"F0.wireOp",EDGE,"E105.2.6"),sQuery(id+"F0.wireOp",EDGE,"E105.2.9"),sQuery(id+"F0.wireOp",EDGE,"E105.2.10"),sQuery(id+"F0.wireOp",EDGE,"E105.3.1"),sQuery(id+"F0.wireOp",EDGE,"E105.3.2"),sQuery(id+"F0.wireOp",EDGE,"E105.3.5"),sQuery(id+"F0.wireOp",EDGE,"E105.3.6"),sQuery(id+"F0.wireOp",EDGE,"E105.3.9"),sQuery(id+"F0.wireOp",EDGE,"E105.3.10"),sQuery(id+"F0.wireOp",EDGE,"E105.4.1"),sQuery(id+"F0.wireOp",EDGE,"E105.4.2"),sQuery(id+"F0.wireOp",EDGE,"E105.4.5"),sQuery(id+"F0.wireOp",EDGE,"E105.4.6"),sQuery(id+"F0.wireOp",EDGE,"E105.4.9"),sQuery(id+"F0.wireOp",EDGE,"E105.4.10"),sQuery(id+"F0.wireOp",EDGE,"E105.5.1"),sQuery(id+"F0.wireOp",EDGE,"E105.5.2"),sQuery(id+"F0.wireOp",EDGE,"E105.5.5"),sQuery(id+"F0.wireOp",EDGE,"E105.5.6"),sQuery(id+"F0.wireOp",EDGE,"E105.5.9"),sQuery(id+"F0.wireOp",EDGE,"E105.5.10"),sQuery(id+"F0.wireOp",EDGE,"E105.6.1"),sQuery(id+"F0.wireOp",EDGE,"E105.6.2"),sQuery(id+"F0.wireOp",EDGE,"E105.6.5"),sQuery(id+"F0.wireOp",EDGE,"E105.6.6"),sQuery(id+"F0.wireOp",EDGE,"E105.6.9"),sQuery(id+"F0.wireOp",EDGE,"E105.6.10"),sQuery(id+"F0.wireOp",EDGE,"E105.7.1"),sQuery(id+"F0.wireOp",EDGE,"E105.7.2"),sQuery(id+"F0.wireOp",EDGE,"E105.7.5"),sQuery(id+"F0.wireOp",EDGE,"E105.7.6"),sQuery(id+"F0.wireOp",EDGE,"E105.7.9"),sQuery(id+"F0.wireOp",EDGE,"E105.7.10"),sQuery(id+"F0.wireOp",EDGE,"E105.8.1"),sQuery(id+"F0.wireOp",EDGE,"E105.8.2"),sQuery(id+"F0.wireOp",EDGE,"E105.8.5"),sQuery(id+"F0.wireOp",EDGE,"E105.8.6"),sQuery(id+"F0.wireOp",EDGE,"E105.8.9"),sQuery(id+"F0.wireOp",EDGE,"E105.8.10"),sQuery(id+"F0.wireOp",EDGE,"E105.9.1"),sQuery(id+"F0.wireOp",EDGE,"E105.9.2"),sQuery(id+"F0.wireOp",EDGE,"E105.9.5"),sQuery(id+"F0.wireOp",EDGE,"E105.9.6"),sQuery(id+"F0.wireOp",EDGE,"E105.9.9"),sQuery(id+"F0.wireOp",EDGE,"E105.9.10"),sQuery(id+"F0.wireOp",EDGE,"E105.10.1"),sQuery(id+"F0.wireOp",EDGE,"E105.10.2"),sQuery(id+"F0.wireOp",EDGE,"E105.10.5"),sQuery(id+"F0.wireOp",EDGE,"E105.10.6"),sQuery(id+"F0.wireOp",EDGE,"E105.10.9"),sQuery(id+"F0.wireOp",EDGE,"E105.10.10"),sQuery(id+"F0.wireOp",EDGE,"E105.11.1"),sQuery(id+"F0.wireOp",EDGE,"E105.11.2"),sQuery(id+"F0.wireOp",EDGE,"E105.11.5"),sQuery(id+"F0.wireOp",EDGE,"E105.11.6"),sQuery(id+"F0.wireOp",EDGE,"E105.11.9"),sQuery(id+"F0.wireOp",EDGE,"E105.11.10"),sQuery(id+"F0.wireOp",EDGE,"E105.12.1"),sQuery(id+"F0.wireOp",EDGE,"E105.12.2"),sQuery(id+"F0.wireOp",EDGE,"E105.12.5"),sQuery(id+"F0.wireOp",EDGE,"E105.12.6"),sQuery(id+"F0.wireOp",EDGE,"E105.12.9"),sQuery(id+"F0.wireOp",EDGE,"E105.12.10"),sQuery(id+"F0.wireOp",EDGE,"E105.13.1"),sQuery(id+"F0.wireOp",EDGE,"E105.13.2"),sQuery(id+"F0.wireOp",EDGE,"E105.13.5"),sQuery(id+"F0.wireOp",EDGE,"E105.13.6"),sQuery(id+"F0.wireOp",EDGE,"E105.13.9"),sQuery(id+"F0.wireOp",EDGE,"E105.13.10"),sQuery(id+"F0.wireOp",EDGE,"E105.14.1"),sQuery(id+"F0.wireOp",EDGE,"E105.14.2"),sQuery(id+"F0.wireOp",EDGE,"E105.14.5"),sQuery(id+"F0.wireOp",EDGE,"E105.14.6"),sQuery(id+"F0.wireOp",EDGE,"E105.14.9"),sQuery(id+"F0.wireOp",EDGE,"E105.14.10"),sQuery(id+"F0.wireOp",EDGE,"E105.15.1"),sQuery(id+"F0.wireOp",EDGE,"E105.15.2"),sQuery(id+"F0.wireOp",EDGE,"E105.15.5"),sQuery(id+"F0.wireOp",EDGE,"E105.15.6"),sQuery(id+"F0.wireOp",EDGE,"E105.15.9"),sQuery(id+"F0.wireOp",EDGE,"E105.15.10"),sQuery(id+"F0.wireOp",EDGE,"E105.16.1"),sQuery(id+"F0.wireOp",EDGE,"E105.16.2"),sQuery(id+"F0.wireOp",EDGE,"E105.16.5"),sQuery(id+"F0.wireOp",EDGE,"E105.16.6"),sQuery(id+"F0.wireOp",EDGE,"E105.16.9"),sQuery(id+"F0.wireOp",EDGE,"E105.16.10"),sQuery(id+"F0.wireOp",EDGE,"E105.17.1"),sQuery(id+"F0.wireOp",EDGE,"E105.17.2"),sQuery(id+"F0.wireOp",EDGE,"E105.17.5"),sQuery(id+"F0.wireOp",EDGE,"E105.17.6"),sQuery(id+"F0.wireOp",EDGE,"E105.17.9"),sQuery(id+"F0.wireOp",EDGE,"E105.17.10"),sQuery(id+"F0.wireOp",EDGE,"E105.18.1"),sQuery(id+"F0.wireOp",EDGE,"E105.18.2"),sQuery(id+"F0.wireOp",EDGE,"E105.18.5"),sQuery(id+"F0.wireOp",EDGE,"E105.18.6"),sQuery(id+"F0.wireOp",EDGE,"E105.18.9"),sQuery(id+"F0.wireOp",EDGE,"E105.18.10"),sQuery(id+"F0.wireOp",EDGE,"E105.19.1"),sQuery(id+"F0.wireOp",EDGE,"E105.19.2"),sQuery(id+"F0.wireOp",EDGE,"E105.19.5"),sQuery(id+"F0.wireOp",EDGE,"E105.19.6"),sQuery(id+"F0.wireOp",EDGE,"E105.19.9"),sQuery(id+"F0.wireOp",EDGE,"E105.19.10"),sQuery(id+"F0.wireOp",EDGE,"E105.20.1"),sQuery(id+"F0.wireOp",EDGE,"E105.20.2"),sQuery(id+"F0.wireOp",EDGE,"E105.20.5"),sQuery(id+"F0.wireOp",EDGE,"E105.20.6"),sQuery(id+"F0.wireOp",EDGE,"E105.20.9"),sQuery(id+"F0.wireOp",EDGE,"E105.20.10"),sQuery(id+"F0.wireOp",EDGE,"E105.21.1"),sQuery(id+"F0.wireOp",EDGE,"E105.21.2"),sQuery(id+"F0.wireOp",EDGE,"E105.21.5"),sQuery(id+"F0.wireOp",EDGE,"E105.21.6"),sQuery(id+"F0.wireOp",EDGE,"E105.21.9"),sQuery(id+"F0.wireOp",EDGE,"E105.21.10"),sQuery(id+"F0.wireOp",EDGE,"E105.22.1"),sQuery(id+"F0.wireOp",EDGE,"E105.22.2"),sQuery(id+"F0.wireOp",EDGE,"E105.22.5"),sQuery(id+"F0.wireOp",EDGE,"E105.22.6"),sQuery(id+"F0.wireOp",EDGE,"E105.22.9"),sQuery(id+"F0.wireOp",EDGE,"E105.22.10"),sQuery(id+"F0.wireOp",EDGE,"E105.23.1"),sQuery(id+"F0.wireOp",EDGE,"E105.23.2"),sQuery(id+"F0.wireOp",EDGE,"E105.23.5"),sQuery(id+"F0.wireOp",EDGE,"E105.23.6"),sQuery(id+"F0.wireOp",EDGE,"E105.23.9"),sQuery(id+"F0.wireOp",EDGE,"E105.23.10"),sQuery(id+"F0.wireOp",EDGE,"E106.1.0"),sQuery(id+"F0.wireOp",EDGE,"E106.1.1"),sQuery(id+"F0.wireOp",EDGE,"E106.1.6"),sQuery(id+"F0.wireOp",EDGE,"E106.1.7"),sQuery(id+"F0.wireOp",EDGE,"E106.1.11"),sQuery(id+"F0.wireOp",EDGE,"E106.1.12"),sQuery(id+"F0.wireOp",EDGE,"E106.2.0"),sQuery(id+"F0.wireOp",EDGE,"E106.2.1"),sQuery(id+"F0.wireOp",EDGE,"E106.2.6"),sQuery(id+"F0.wireOp",EDGE,"E106.2.7"),sQuery(id+"F0.wireOp",EDGE,"E106.2.11"),sQuery(id+"F0.wireOp",EDGE,"E106.2.12"),sQuery(id+"F0.wireOp",EDGE,"E106.3.0"),sQuery(id+"F0.wireOp",EDGE,"E106.3.1"),sQuery(id+"F0.wireOp",EDGE,"E106.3.6"),sQuery(id+"F0.wireOp",EDGE,"E106.3.7"),sQuery(id+"F0.wireOp",EDGE,"E106.3.11"),sQuery(id+"F0.wireOp",EDGE,"E106.3.12"),sQuery(id+"F0.wireOp",EDGE,"E106.4.0"),sQuery(id+"F0.wireOp",EDGE,"E106.4.1"),sQuery(id+"F0.wireOp",EDGE,"E106.4.6"),sQuery(id+"F0.wireOp",EDGE,"E106.4.7"),sQuery(id+"F0.wireOp",EDGE,"E106.4.11"),sQuery(id+"F0.wireOp",EDGE,"E106.4.12"),sQuery(id+"F0.wireOp",EDGE,"E106.5.0"),sQuery(id+"F0.wireOp",EDGE,"E106.5.1"),sQuery(id+"F0.wireOp",EDGE,"E106.5.6"),sQuery(id+"F0.wireOp",EDGE,"E106.5.7"),sQuery(id+"F0.wireOp",EDGE,"E106.5.11"),sQuery(id+"F0.wireOp",EDGE,"E106.5.12"),sQuery(id+"F0.wireOp",EDGE,"E106.6.0"),sQuery(id+"F0.wireOp",EDGE,"E106.6.1"),sQuery(id+"F0.wireOp",EDGE,"E106.6.6"),sQuery(id+"F0.wireOp",EDGE,"E106.6.7"),sQuery(id+"F0.wireOp",EDGE,"E106.6.11"),sQuery(id+"F0.wireOp",EDGE,"E106.6.12"),sQuery(id+"F0.wireOp",EDGE,"E106.7.0"),sQuery(id+"F0.wireOp",EDGE,"E106.7.1"),sQuery(id+"F0.wireOp",EDGE,"E106.7.6"),sQuery(id+"F0.wireOp",EDGE,"E106.7.7"),sQuery(id+"F0.wireOp",EDGE,"E106.7.11"),sQuery(id+"F0.wireOp",EDGE,"E106.7.12"),sQuery(id+"F0.wireOp",EDGE,"E106.8.0"),sQuery(id+"F0.wireOp",EDGE,"E106.8.1"),sQuery(id+"F0.wireOp",EDGE,"E106.8.6"),sQuery(id+"F0.wireOp",EDGE,"E106.8.7"),sQuery(id+"F0.wireOp",EDGE,"E106.8.11"),sQuery(id+"F0.wireOp",EDGE,"E106.8.12"),sQuery(id+"F0.wireOp",EDGE,"E106.9.0"),sQuery(id+"F0.wireOp",EDGE,"E106.9.1"),sQuery(id+"F0.wireOp",EDGE,"E106.9.6"),sQuery(id+"F0.wireOp",EDGE,"E106.9.7"),sQuery(id+"F0.wireOp",EDGE,"E106.9.11"),sQuery(id+"F0.wireOp",EDGE,"E106.9.12"),sQuery(id+"F0.wireOp",EDGE,"E106.10.0"),sQuery(id+"F0.wireOp",EDGE,"E106.10.1"),sQuery(id+"F0.wireOp",EDGE,"E106.10.6"),sQuery(id+"F0.wireOp",EDGE,"E106.10.7"),sQuery(id+"F0.wireOp",EDGE,"E106.10.11"),sQuery(id+"F0.wireOp",EDGE,"E106.10.12"),sQuery(id+"F0.wireOp",EDGE,"E106.11.0"),sQuery(id+"F0.wireOp",EDGE,"E106.11.1"),sQuery(id+"F0.wireOp",EDGE,"E106.11.6"),sQuery(id+"F0.wireOp",EDGE,"E106.11.7"),sQuery(id+"F0.wireOp",EDGE,"E106.11.11"),sQuery(id+"F0.wireOp",EDGE,"E106.11.12"),sQuery(id+"F0.wireOp",EDGE,"E106.12.0"),sQuery(id+"F0.wireOp",EDGE,"E106.12.1"),sQuery(id+"F0.wireOp",EDGE,"E106.12.6"),sQuery(id+"F0.wireOp",EDGE,"E106.12.7"),sQuery(id+"F0.wireOp",EDGE,"E106.12.11"),sQuery(id+"F0.wireOp",EDGE,"E106.12.12"),sQuery(id+"F0.wireOp",EDGE,"E106.13.0"),sQuery(id+"F0.wireOp",EDGE,"E106.13.1"),sQuery(id+"F0.wireOp",EDGE,"E106.13.6"),sQuery(id+"F0.wireOp",EDGE,"E106.13.7"),sQuery(id+"F0.wireOp",EDGE,"E106.13.11"),sQuery(id+"F0.wireOp",EDGE,"E106.13.12"),sQuery(id+"F0.wireOp",EDGE,"E106.14.0"),sQuery(id+"F0.wireOp",EDGE,"E106.14.1"),sQuery(id+"F0.wireOp",EDGE,"E106.14.6"),sQuery(id+"F0.wireOp",EDGE,"E106.14.7"),sQuery(id+"F0.wireOp",EDGE,"E106.14.11"),sQuery(id+"F0.wireOp",EDGE,"E106.14.12"),sQuery(id+"F0.wireOp",EDGE,"E106.15.0"),sQuery(id+"F0.wireOp",EDGE,"E106.15.1"),sQuery(id+"F0.wireOp",EDGE,"E106.15.6"),sQuery(id+"F0.wireOp",EDGE,"E106.15.7"),sQuery(id+"F0.wireOp",EDGE,"E106.15.11"),sQuery(id+"F0.wireOp",EDGE,"E106.15.12"),sQuery(id+"F0.wireOp",EDGE,"E106.16.0"),sQuery(id+"F0.wireOp",EDGE,"E106.16.1"),sQuery(id+"F0.wireOp",EDGE,"E106.16.6"),sQuery(id+"F0.wireOp",EDGE,"E106.16.7"),sQuery(id+"F0.wireOp",EDGE,"E106.16.11"),sQuery(id+"F0.wireOp",EDGE,"E106.16.12"),sQuery(id+"F0.wireOp",EDGE,"E106.17.0"),sQuery(id+"F0.wireOp",EDGE,"E106.17.1"),sQuery(id+"F0.wireOp",EDGE,"E106.17.6"),sQuery(id+"F0.wireOp",EDGE,"E106.17.7"),sQuery(id+"F0.wireOp",EDGE,"E106.17.11"),sQuery(id+"F0.wireOp",EDGE,"E106.17.12"),sQuery(id+"F0.wireOp",EDGE,"E106.18.0"),sQuery(id+"F0.wireOp",EDGE,"E106.18.1"),sQuery(id+"F0.wireOp",EDGE,"E106.18.6"),sQuery(id+"F0.wireOp",EDGE,"E106.18.7"),sQuery(id+"F0.wireOp",EDGE,"E106.18.11"),sQuery(id+"F0.wireOp",EDGE,"E106.18.12"),sQuery(id+"F0.wireOp",EDGE,"E106.19.0"),sQuery(id+"F0.wireOp",EDGE,"E106.19.1"),sQuery(id+"F0.wireOp",EDGE,"E106.19.6"),sQuery(id+"F0.wireOp",EDGE,"E106.19.7"),sQuery(id+"F0.wireOp",EDGE,"E106.19.11"),sQuery(id+"F0.wireOp",EDGE,"E106.19.12")])]});
            hole(context, id + "F4", {"style" : HoleStyle.C_BORE, "endStyle" : HoleEndStyle.THROUGH, "holeDiameter" : 3.5 * mm, "cBoreDiameter" : 6.5 * mm, "cBoreDepth" : 2 * mm, "startFromSketch" : true, "locations" : qUnion([Q0, Q1, Q2, Q3, Q4, Q5, Q6, Q7, Q8, Q9]), "scope" : qUnion([Q10]), "isTappedThrough" : true});
        }
    });
